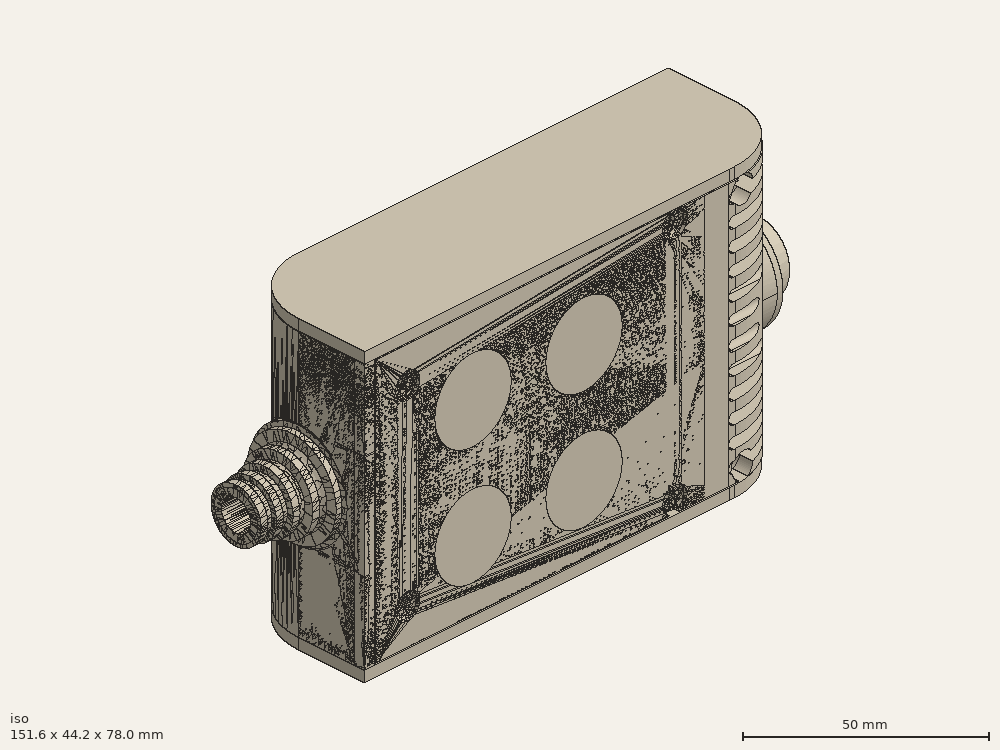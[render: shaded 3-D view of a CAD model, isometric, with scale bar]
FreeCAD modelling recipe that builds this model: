
FCSTD DOCUMENT  (FreeCAD 0.19R0.19.2)
Label: enclosure_182FCStd
License: All rights reserved
LicenseURL: http://en.wikipedia.org/wiki/All_rights_reserved
objects: Part::Revolution×152, Part::MultiFuse×146, Part::Feature×146, Sketcher::SketchObject×84, Part::Cut×70, Part::Cylinder×70, Part::Extrusion×67, Part::Fillet×58, Part::Box×36, App::MeasureDistance×4, PartDesign::Body×2, Image::ImagePlane×1
note: 831 computed .brp shape members not serialized (recipe doc carries the construction recipe); baked Part::Feature solids carry a one-line shape summary decoded from their .brp

FEATURE [Sketcher::SketchObject] Sketch  label="topSketch"
  FullyConstrained = true
  sketch-geometry (20):
    g0: LineSegment StartX=5.21097e-06 StartY=3 StartZ=0 EndX=5.21097e-06 EndY=19 EndZ=0
    g1: ArcOfCircle CenterX=19 CenterY=19 CenterZ=0 NormalX=0 NormalY=0 NormalZ=1 AngleXU=0 Radius=19 StartAngle=1.5708 EndAngle=3.14159
    g2: ArcOfCircle CenterX=19 CenterY=19 CenterZ=0 NormalX=0 NormalY=0 NormalZ=1 AngleXU=0 Radius=16 StartAngle=1.5708 EndAngle=3.14159
    g3: LineSegment StartX=114 StartY=35 StartZ=0 EndX=19 EndY=35 EndZ=0
    g4: LineSegment StartX=5.21097e-06 StartY=3 StartZ=0 EndX=5.21097e-06 EndY=0 EndZ=0
    g5: LineSegment StartX=3 StartY=0 StartZ=0 EndX=5.21097e-06 EndY=0 EndZ=0
    g6: LineSegment StartX=3 StartY=19 StartZ=0 EndX=3 EndY=0 EndZ=0
    g7: LineSegment StartX=19 StartY=38 StartZ=0 EndX=124 EndY=38 EndZ=0
    g8: Circle CenterX=119 CenterY=35 CenterZ=0 NormalX=0 NormalY=0 NormalZ=1 AngleXU=0 Radius=1
    g9: Circle CenterX=121 CenterY=35 CenterZ=0 NormalX=0 NormalY=0 NormalZ=1 AngleXU=0 Radius=1
    g10: Circle CenterX=121 CenterY=33 CenterZ=0 NormalX=0 NormalY=0 NormalZ=1 AngleXU=0 Radius=1
    g11: BSplineCurve PolesCount=3 KnotsCount=2 Degree=2 IsPeriodic=0
    g12: GeomPoint X=119 Y=35 Z=0
    g13: GeomPoint X=121 Y=33 Z=0
    g14: LineSegment StartX=119 StartY=35 StartZ=0 EndX=114 EndY=35 EndZ=0
    g15: ArcOfCircle CenterX=105 CenterY=19 CenterZ=0 NormalX=0 NormalY=0 NormalZ=1 AngleXU=0 Radius=19 StartAngle=5.7297 EndAngle=6.28319
    g16: ArcOfCircle CenterX=105 CenterY=19 CenterZ=0 NormalX=0 NormalY=0 NormalZ=1 AngleXU=0 Radius=16 StartAngle=5.60905 EndAngle=6.28319
    g17: LineSegment StartX=121 StartY=33 StartZ=0 EndX=121 EndY=19 EndZ=0
    g18: LineSegment StartX=124 StartY=38 StartZ=0 EndX=124 EndY=19 EndZ=0
    g19: LineSegment StartX=117.5 StartY=9.01251 StartZ=0 EndX=121.163 EndY=9.0125 EndZ=0
  constraints (46):
    c: Vertical(g0)
    c: Block(g0)
    c: Coincident(g1,g0)
    c: Block(g1)
    c: Coincident(g2,g1)
    c: Block(g2)
    c: Coincident(g3,g2)
    c: Horizontal(g3)
    c: Tangent(g3,g2)
    c: Coincident(g4,g0)
    c: Distance(g4) = 3
    c: Vertical(g4)
    c: Coincident(g5,g4)
    c: Horizontal(g5)
    c: Coincident(g6,g2)
    c: Coincident(g6,g5)
    c: Vertical(g6)
    c: Horizontal(g7)
    c: Distance(g7) = 105
    c: Coincident(g7,g1)
    c: Block(g3)
    c: Weight(g8) = 1
    c: Equal(g8,g9)
    c: Equal(g8,g10)
    c: InternalAlignment(g8,g11)
    c: InternalAlignment(g9,g11)
    c: InternalAlignment(g10,g11)
    c: InternalAlignment(g12,g11)
    c: InternalAlignment(g13,g11)
    c: Block(g11)
    c: Coincident(g14,g11)
    c: Coincident(g14,g3)
    c: Horizontal(g14)
    c: Block(g15)
    c: Coincident(g16,g15)
    c: Block(g16)
    c: Coincident(g17,g11)
    c: Coincident(g17,g16)
    c: Vertical(g17)
    c: Distance(g17) = 14
    c: Coincident(g18,g7)
    c: Coincident(g18,g15)
    c: Vertical(g18)
    c: Distance(g18) = 19
    c: Coincident(g19,g16)
    c: Coincident(g19,g15)
FEATURE [Sketcher::SketchObject] Sketch001  label="bottomSketch"
  FullyConstrained = true
  sketch-geometry (32):
    g0: LineSegment StartX=3.3 StartY=-6.03275e-07 StartZ=0 EndX=98 EndY=-6.03275e-07 EndZ=0
    g1: ArcOfCircle CenterX=98 CenterY=19 CenterZ=0 NormalX=0 NormalY=0 NormalZ=1 AngleXU=0 Radius=19 StartAngle=4.71239 EndAngle=5.71103
    g2: LineSegment StartX=6.3 StartY=8 StartZ=0 EndX=3.3 EndY=8 EndZ=0
    g3: LineSegment StartX=3.3 StartY=8 StartZ=0 EndX=3.3 EndY=-6.03275e-07 EndZ=0
    g4: ArcOfCircle CenterX=8.3 CenterY=5 CenterZ=0 NormalX=0 NormalY=0 NormalZ=1 AngleXU=0 Radius=2 StartAngle=3.14159 EndAngle=4.71239
    g5: LineSegment StartX=6.3 StartY=8 StartZ=0 EndX=6.3 EndY=5 EndZ=0
    g6: ArcOfCircle CenterX=98 CenterY=19 CenterZ=0 NormalX=0 NormalY=0 NormalZ=1 AngleXU=0 Radius=12.7 StartAngle=4.71239 EndAngle=6.28319
    g7: LineSegment StartX=94.7 StartY=3 StartZ=0 EndX=8.3 EndY=3 EndZ=0
    g8-g12: Circle x5 (B-spline internal-alignment scaffolding for g13; pole/knot coordinates omitted)
    g13: BSplineCurve PolesCount=5 KnotsCount=3 Degree=3 IsPeriodic=0
    g14: GeomPoint X=98 Y=6.3 Z=0
    g15: GeomPoint X=96.3938 Y=4.71946 Z=0
    g16: GeomPoint X=94.7 Y=3 Z=0
    g17-g23: Circle x7 (B-spline internal-alignment scaffolding for g24; pole/knot coordinates omitted)
    g24: BSplineCurve PolesCount=7 KnotsCount=5 Degree=3 IsPeriodic=0
    g25-g29: GeomPoint x5 (B-spline internal-alignment scaffolding for g24; pole/knot coordinates omitted)
    g30: ArcOfCircle CenterX=98 CenterY=19 CenterZ=0 NormalX=0 NormalY=0 NormalZ=1 AngleXU=0 Radius=15.7 StartAngle=5.81226 EndAngle=6.28319
    g31: LineSegment StartX=110.7 StartY=19 StartZ=0 EndX=113.7 EndY=19 EndZ=0
  constraints (41):
    c: Horizontal(g0)
    c: Coincident(g1,g0)
    c: Block(g1)
    c: Horizontal(g2)
    c: Distance(g2) = 3
    c: Coincident(g3,g2)
    c: Vertical(g3)
    c: Coincident(g3,g0)
    c: Block(g4)
    c: Block(g2)
    c: Coincident(g5,g2)
    c: Coincident(g5,g4)
    c: Vertical(g5)
    c: Coincident(g6,g1)
    c: Block(g6)
    c: Coincident(g7,g4)
    c: Horizontal(g7)
    c: Block(g0)
    c: Block(g7)
    c: Block(g3)
    c: Coincident(g13,g6)
    c: Weight(g8) = 1
    c: Equal(g8, g9-g12) x4
    c: Coincident(g13,g7)
    c: InternalAlignment(g8-g12 -> g13) x5
    c: InternalAlignment(g14,g13)
    c: InternalAlignment(g15,g13)
    c: InternalAlignment(g16,g13)
    c: Block(g13)
    c: Weight(g17) = 1
    c: Equal(g17, g18-g23) x6
    c: Coincident(g24,g1)
    c: InternalAlignment(g17-g23 -> g24) x7
    c: InternalAlignment(g25-g29 -> g24) x5
    c: Block(g24)
    c: Coincident(g30,g24)
    c: Coincident(g31,g6)
    c: Coincident(g31,g30)
    c: Horizontal(g31)
    c: Block(g31)
    c: Block(g30)
FEATURE [Part::Extrusion] Extrude  label="top"
  Base = -> Sketch
  Dir = (0,0,1)
  DirMode = 2
  FaceMakerClass = Part::FaceMakerBullseye
  LengthFwd = 72
  LengthRev = 0
  Solid = true
  Symmetric = false
FEATURE [Part::Extrusion] Extrude001  label="bottom"
  Base = -> Sketch001
  Dir = (0,0,1)
  DirMode = 2
  FaceMakerClass = Part::FaceMakerBullseye
  LengthFwd = 71.4
  LengthRev = 0
  Placement = pos=(0,0,0.3) rot=(0,0,1;0rad)
  Solid = true
  Symmetric = false
FEATURE [Sketcher::SketchObject] Sketch002  label="topSketch001"
  FullyConstrained = true
  sketch-geometry (8):
    g0: ArcOfCircle CenterX=19 CenterY=19.0975 CenterZ=0 NormalX=0 NormalY=0 NormalZ=1 AngleXU=0 Radius=18.9025 StartAngle=1.5708 EndAngle=3.14674
    g1: LineSegment StartX=0.0977805 StartY=19.0003 StartZ=0 EndX=0.0977805 EndY=0.000251602 EndZ=0
    g2: LineSegment StartX=19 StartY=38 StartZ=0 EndX=124 EndY=38 EndZ=0
    g3: LineSegment StartX=0.0977805 StartY=0.000251602 StartZ=0 EndX=105.098 EndY=0.000251602 EndZ=0
    g4: LineSegment StartX=124 StartY=38 StartZ=0 EndX=125.616 EndY=38 EndZ=0
    g5: LineSegment StartX=105.098 StartY=0.000251602 StartZ=0 EndX=106.713 EndY=0.000251602 EndZ=0
    g6: ArcOfCircle CenterX=106.616 CenterY=19 CenterZ=0 NormalX=0 NormalY=0 NormalZ=1 AngleXU=0 Radius=19 StartAngle=4.71754 EndAngle=6.28319
    g7: LineSegment StartX=125.616 StartY=38 StartZ=0 EndX=125.616 EndY=19 EndZ=0
  constraints (21):
    c: Block(g0)
    c: Coincident(g1,g0)
    c: Vertical(g1)
    c: Horizontal(g2)
    c: Distance(g2) = 105
    c: Coincident(g2,g0)
    c: Distance(g1) = 19
    c: Coincident(g3,g1)
    c: Horizontal(g3)
    c: Distance(g3) = 105
    c: Coincident(g4,g2)
    c: Horizontal(g4)
    c: Distance(g4) = 1.61553
    c: Horizontal(g5)
    c: Equal(g4,g5) = 1.61553
    c: Coincident(g5,g3)
    c: Block(g6)
    c: Coincident(g6,g5)
    c: Coincident(g7,g4)
    c: Coincident(g7,g6)
    c: Vertical(g7)
FEATURE [Part::Extrusion] Extrude002  label="sideA"
  Base = -> Sketch002
  Dir = (0,0,1)
  DirMode = 2
  FaceMakerClass = Part::FaceMakerBullseye
  LengthFwd = 3
  LengthRev = 0
  Placement = pos=(0,0,-3) rot=(0,0,1;0rad)
  Solid = true
  Symmetric = false
FEATURE [Sketcher::SketchObject] Sketch003  label="topSketch002"
  FullyConstrained = true
  sketch-geometry (6):
    g0: LineSegment StartX=19 StartY=38 StartZ=0 EndX=117 EndY=38 EndZ=0
    g1: ArcOfCircle CenterX=19 CenterY=19 CenterZ=0 NormalX=0 NormalY=0 NormalZ=1 AngleXU=0 Radius=19 StartAngle=1.5708 EndAngle=3.14159
    g2: LineSegment StartX=117 StartY=38 StartZ=0 EndX=117 EndY=19 EndZ=0
    g3: LineSegment StartX=98 StartY=1.0161e-12 StartZ=0 EndX=5.22862e-06 EndY=1.0161e-12 EndZ=0
    g4: LineSegment StartX=5.22862e-06 StartY=19 StartZ=0 EndX=5.22862e-06 EndY=1.0161e-12 EndZ=0
    g5: ArcOfCircle CenterX=98 CenterY=19 CenterZ=0 NormalX=0 NormalY=0 NormalZ=1 AngleXU=0 Radius=19 StartAngle=4.71239 EndAngle=6.28319
  constraints (16):
    c: Horizontal(g0)
    c: Distance(g0) = 98
    c: Coincident(g1,g0)
    c: Block(g1)
    c: Coincident(g2,g0)
    c: Vertical(g2)
    c: Distance(g2) = 19
    c: Horizontal(g3)
    c: Coincident(g4,g1)
    c: Vertical(g4)
    c: Coincident(g3,g4)
    c: Block(g3)
    c: Coincident(g5,g2)
    c: Coincident(g5,g3)
    c: Block(g0)
    c: Block(g5)
FEATURE [Sketcher::SketchObject] Sketch004
  FullyConstrained = true
  MapMode = 3
  Placement = pos=(0,0,0) rot=(1,0,0;1.5708rad)
  Support = -> [Extrude]
  sketch-geometry (8):
    g0: Circle CenterX=80.351 CenterY=-67.6202 CenterZ=0 NormalX=0 NormalY=0 NormalZ=1 AngleXU=0 Radius=2
    g1: Circle CenterX=80.351 CenterY=-67.6202 CenterZ=0 NormalX=0 NormalY=0 NormalZ=1 AngleXU=0 Radius=3
    g2: Circle CenterX=80.351 CenterY=-4.92017 CenterZ=0 NormalX=0 NormalY=0 NormalZ=1 AngleXU=0 Radius=2
    g3: Circle CenterX=80.351 CenterY=-4.92017 CenterZ=0 NormalX=0 NormalY=0 NormalZ=1 AngleXU=0 Radius=3
    g4: Circle CenterX=23.851 CenterY=-4.92017 CenterZ=0 NormalX=0 NormalY=0 NormalZ=1 AngleXU=0 Radius=2
    g5: Circle CenterX=23.851 CenterY=-4.92017 CenterZ=0 NormalX=0 NormalY=0 NormalZ=1 AngleXU=0 Radius=3
    g6: Circle CenterX=23.851 CenterY=-67.6202 CenterZ=0 NormalX=0 NormalY=0 NormalZ=1 AngleXU=0 Radius=2
    g7: Circle CenterX=23.851 CenterY=-67.6202 CenterZ=0 NormalX=0 NormalY=0 NormalZ=1 AngleXU=0 Radius=3
  constraints (8):
    c: Block(g3)
    c: Block(g2)
    c: Block(g1)
    c: Block(g0)
    c: Block(g6)
    c: Block(g7)
    c: Block(g4)
    c: Block(g5)
FEATURE [Part::Extrusion] Extrude004
  Base = -> Sketch004
  Dir = (0,-1,2e-16)
  DirMode = 2
  FaceMakerClass = Part::FaceMakerBullseye
  LengthFwd = 6
  LengthRev = 0
  Placement = pos=(0,9,0) rot=(0,0,1;0rad)
  Solid = true
  Symmetric = false
FEATURE [Sketcher::SketchObject] Sketch005
  FullyConstrained = true
  MapMode = 3
  Placement = pos=(0,0,0) rot=(1,0,0;1.5708rad)
  Support = -> [Extrude]
  sketch-geometry (8):
    g0: Circle CenterX=80.351 CenterY=-67.6202 CenterZ=0 NormalX=0 NormalY=0 NormalZ=1 AngleXU=0 Radius=3
    g1: Circle CenterX=80.351 CenterY=-4.92017 CenterZ=0 NormalX=0 NormalY=0 NormalZ=1 AngleXU=0 Radius=3
    g2: Circle CenterX=23.851 CenterY=-4.92017 CenterZ=0 NormalX=0 NormalY=0 NormalZ=1 AngleXU=0 Radius=3
    g3: Circle CenterX=23.851 CenterY=-67.6202 CenterZ=0 NormalX=0 NormalY=0 NormalZ=1 AngleXU=0 Radius=3
    g4: Circle CenterX=23.851 CenterY=-67.6202 CenterZ=0 NormalX=0 NormalY=0 NormalZ=1 AngleXU=0 Radius=5
    g5: Circle CenterX=80.351 CenterY=-67.6202 CenterZ=0 NormalX=0 NormalY=0 NormalZ=1 AngleXU=0 Radius=5
    g6: Circle CenterX=23.851 CenterY=-4.92017 CenterZ=0 NormalX=0 NormalY=0 NormalZ=1 AngleXU=0 Radius=5
    g7: Circle CenterX=80.351 CenterY=-4.92017 CenterZ=0 NormalX=0 NormalY=0 NormalZ=1 AngleXU=0 Radius=5
  constraints (8):
    c: Block(g1)
    c: Block(g0)
    c: Block(g3)
    c: Block(g2)
    c: Block(g5)
    c: Block(g4)
    c: Block(g6)
    c: Block(g7)
FEATURE [Part::Extrusion] Extrude005
  Base = -> Sketch005
  Dir = (0,-1,2e-16)
  DirMode = 2
  FaceMakerClass = Part::FaceMakerBullseye
  LengthFwd = 2
  LengthRev = 0
  Solid = true
  Symmetric = false
FEATURE [Sketcher::SketchObject] Sketch006
  FullyConstrained = true
  MapMode = 3
  Placement = pos=(0,0,0) rot=(1,0,0;1.5708rad)
  sketch-geometry (8):
    g0: Circle CenterX=80.351 CenterY=-67.6202 CenterZ=0 NormalX=0 NormalY=0 NormalZ=1 AngleXU=0 Radius=3
    g1: Circle CenterX=80.351 CenterY=-4.92017 CenterZ=0 NormalX=0 NormalY=0 NormalZ=1 AngleXU=0 Radius=3
    g2: Circle CenterX=23.851 CenterY=-4.92017 CenterZ=0 NormalX=0 NormalY=0 NormalZ=1 AngleXU=0 Radius=3
    g3: Circle CenterX=23.851 CenterY=-67.6202 CenterZ=0 NormalX=0 NormalY=0 NormalZ=1 AngleXU=0 Radius=3
    g4: Circle CenterX=23.851 CenterY=-67.6202 CenterZ=0 NormalX=0 NormalY=0 NormalZ=1 AngleXU=0 Radius=5
    g5: Circle CenterX=80.351 CenterY=-67.6202 CenterZ=0 NormalX=0 NormalY=0 NormalZ=1 AngleXU=0 Radius=5
    g6: Circle CenterX=23.851 CenterY=-4.92017 CenterZ=0 NormalX=0 NormalY=0 NormalZ=1 AngleXU=0 Radius=5
    g7: Circle CenterX=80.351 CenterY=-4.92017 CenterZ=0 NormalX=0 NormalY=0 NormalZ=1 AngleXU=0 Radius=5
  constraints (8):
    c: Block(g1)
    c: Block(g0)
    c: Block(g3)
    c: Block(g2)
    c: Block(g5)
    c: Block(g4)
    c: Block(g6)
    c: Block(g7)
FEATURE [Part::Extrusion] Extrude007
  Base = -> Sketch006
  Dir = (0,-1,2e-16)
  DirMode = 2
  FaceMakerClass = Part::FaceMakerBullseye
  LengthFwd = 2
  LengthRev = 0
  Solid = true
  Symmetric = false
FEATURE [Part::Fillet] Fillet
  Base = -> Extrude007
  Edges = 4 edges r=1.99: [Edge6,Edge12,Edge18,Edge24]
FEATURE [Part::Cut] Cut
  Base = -> Extrude005
  Placement = pos=(0,5,0) rot=(0,0,1;0rad)
  Tool = -> Fillet
FEATURE [Part::MultiFuse] Fusion  label="pCBScrews"
  Placement = pos=(-2.5,0,72.3) rot=(0,0,1;0rad)
  Shapes = -> [Extrude004,Cut]
FEATURE [App::MeasureDistance] Distance  label="Distance: 0.69 mm"
  Distance = 0.685967
  P1 = (24.0138,2.9647,0.3)
  P2 = (23.8901,3,-0.373787)
FEATURE [App::MeasureDistance] Distance001  label="Distance: 0.53 mm"
  Distance = 0.533607
  P1 = (80.2939,3,72.2334)
  P2 = (80.281,2.99661,71.7)
FEATURE [Part::Fillet] Fillet001
  Base = -> Extrude001
  Edges = 1 edges r=2.4: [Edge17]
FEATURE [Part::Fillet] Fillet002  label="bottom001"
  Base = -> Fillet001
  Edges = 1 edges r=2.4: [Edge36]
FEATURE [Part::Fillet] Fillet003  label="top001"
  Base = -> Extrude
  Edges = 1 edges r=2: [Edge1]
FEATURE [Sketcher::SketchObject] Sketch007
  FullyConstrained = true
  sketch-geometry (16):
    g0: LineSegment StartX=4 StartY=0 StartZ=0 EndX=4 EndY=2.4 EndZ=0
    g1: LineSegment StartX=4 StartY=2.4 StartZ=0 EndX=7 EndY=2.4 EndZ=0
    g2: LineSegment StartX=4 StartY=0 StartZ=0 EndX=5.7 EndY=0 EndZ=0
    g3: LineSegment StartX=5.7 StartY=0 StartZ=0 EndX=5.7 EndY=-5.6 EndZ=0
    g4-g8: Circle x5 (B-spline internal-alignment scaffolding for g9; pole/knot coordinates omitted)
    g9: BSplineCurve PolesCount=5 KnotsCount=3 Degree=3 IsPeriodic=0
    g10: GeomPoint X=7 Y=2.4 Z=0
    g11: GeomPoint X=10.4582 Y=-1.55472 Z=0
    g12: GeomPoint X=14 Y=-5.6 Z=0
    g13: LineSegment StartX=14 StartY=-5.6 StartZ=0 EndX=14 EndY=-14.1 EndZ=0
    g14: LineSegment StartX=14 StartY=-14.1 StartZ=0 EndX=6.5 EndY=-14.1 EndZ=0
    g15: LineSegment StartX=5.7 StartY=-5.6 StartZ=0 EndX=6.5 EndY=-14.1 EndZ=0
  constraints (28):
    c: Distance(g0) = 2.4
    c: Vertical(g0)
    c: Block(g0)
    c: Coincident(g1,g0)
    c: Horizontal(g1)
    c: Distance(g1) = 3
    c: Coincident(g2,g0)
    c: Horizontal(g2)
    c: Distance(g2) = 1.7
    c: Coincident(g3,g2)
    c: Vertical(g3)
    c: Distance(g3) = 5.6
    c: Coincident(g9,g1)
    c: Weight(g4) = 1
    c: Equal(g4, g5-g8) x4
    c: InternalAlignment(g4-g8 -> g9) x5
    c: InternalAlignment(g10,g9)
    c: InternalAlignment(g11,g9)
    c: InternalAlignment(g12,g9)
    c: Block(g9)
    c: Coincident(g13,g9)
    c: Vertical(g13)
    c: Distance(g13) = 8.5
    c: Coincident(g14,g13)
    c: Horizontal(g14)
    c: Distance(g14) = 7.5
    c: Coincident(g15,g3)
    c: Coincident(g15,g14)
FEATURE [Part::Feature] Face
  shape: bbox 10 x 16.5 x 2e-07 mm, 1 faces, 0 solids (baked)
FEATURE [Part::Revolution] Revolve  label="plugHousing"
  Angle = 360
  Axis = (0,1,0)
  Base = (0,0,0)
  FaceMakerClass = Part::FaceMakerBullseye
  Placement = pos=(0,0,36.15) rot=(0,0,1;0rad)
  Solid = false
  Source = -> Face
  Symmetric = false
FEATURE [Part::Feature] Face001
  shape: bbox 10 x 16.5 x 2e-07 mm, 1 faces, 0 solids (baked)
FEATURE [Part::Revolution] Revolve001  label="plugHousing001"
  Angle = 360
  Axis = (0,1,0)
  Base = (0,0,0)
  FaceMakerClass = Part::FaceMakerBullseye
  Placement = pos=(0,0,36.15) rot=(0,0,1;0rad)
  Solid = false
  Source = -> Face001
  Symmetric = false
FEATURE [Part::MultiFuse] Fusion001  label="plugHousing002"
  Placement = pos=(0,0,0) rot=(0,0,1;1.5708rad)
  Shapes = -> [Revolve001,Revolve]
FEATURE [Part::Feature] Face002
  shape: bbox 10 x 16.5 x 2e-07 mm, 1 faces, 0 solids (baked)
FEATURE [Part::Revolution] Revolve003  label="plugHousing005"
  Angle = 360
  Axis = (0,1,0)
  Base = (0,0,0)
  FaceMakerClass = Part::FaceMakerBullseye
  Placement = pos=(0,0,36.15) rot=(0,0,1;0rad)
  Solid = false
  Source = -> Face002
  Symmetric = false
FEATURE [Part::Feature] Face003
  shape: bbox 10 x 16.5 x 2e-07 mm, 1 faces, 0 solids (baked)
FEATURE [Part::Revolution] Revolve002  label="plugHousing003"
  Angle = 360
  Axis = (0,1,0)
  Base = (0,0,0)
  FaceMakerClass = Part::FaceMakerBullseye
  Placement = pos=(0,0,36.15) rot=(0,0,1;0rad)
  Solid = false
  Source = -> Face003
  Symmetric = false
FEATURE [Part::MultiFuse] Fusion002  label="plugHousing004"
  Placement = pos=(0,0,0) rot=(0,0,1;1.5708rad)
  Shapes = -> [Revolve002,Revolve003]
FEATURE [Part::MultiFuse] Fusion003  label="plugHousing006"
  Placement = pos=(0,19,0) rot=(0,0,1;3.14159rad)
  Shapes = -> [Fusion002,Fusion001]
FEATURE [Part::Feature] Face004
  shape: bbox 10 x 16.5 x 2e-07 mm, 1 faces, 0 solids (baked)
FEATURE [Part::Revolution] Revolve006  label="plugHousing010"
  Angle = 360
  Axis = (0,1,0)
  Base = (0,0,0)
  FaceMakerClass = Part::FaceMakerBullseye
  Placement = pos=(0,0,36.15) rot=(0,0,1;0rad)
  Solid = false
  Source = -> Face004
  Symmetric = false
FEATURE [Part::Feature] Face005
  shape: bbox 10 x 16.5 x 2e-07 mm, 1 faces, 0 solids (baked)
FEATURE [Part::Revolution] Revolve007  label="plugHousing011"
  Angle = 360
  Axis = (0,1,0)
  Base = (0,0,0)
  FaceMakerClass = Part::FaceMakerBullseye
  Placement = pos=(0,0,36.15) rot=(0,0,1;0rad)
  Solid = false
  Source = -> Face005
  Symmetric = false
FEATURE [Part::Feature] Face006
  shape: bbox 10 x 16.5 x 2e-07 mm, 1 faces, 0 solids (baked)
FEATURE [Part::Revolution] Revolve004  label="plugHousing007"
  Angle = 360
  Axis = (0,1,0)
  Base = (0,0,0)
  FaceMakerClass = Part::FaceMakerBullseye
  Placement = pos=(0,0,36.15) rot=(0,0,1;0rad)
  Solid = false
  Source = -> Face006
  Symmetric = false
FEATURE [Part::MultiFuse] Fusion004  label="plugHousing009"
  Placement = pos=(0,0,0) rot=(0,0,1;1.5708rad)
  Shapes = -> [Revolve004,Revolve007]
FEATURE [Part::Feature] Face007
  shape: bbox 10 x 16.5 x 2e-07 mm, 1 faces, 0 solids (baked)
FEATURE [Part::Revolution] Revolve005  label="plugHousing008"
  Angle = 360
  Axis = (0,1,0)
  Base = (0,0,0)
  FaceMakerClass = Part::FaceMakerBullseye
  Placement = pos=(0,0,36.15) rot=(0,0,1;0rad)
  Solid = false
  Source = -> Face007
  Symmetric = false
FEATURE [Part::MultiFuse] Fusion005  label="plugHousing012"
  Placement = pos=(0,0,0) rot=(0,0,1;1.5708rad)
  Shapes = -> [Revolve006,Revolve005]
FEATURE [Part::MultiFuse] Fusion006  label="plugHousing013"
  Placement = pos=(0,19,0) rot=(0,0,1;3.14159rad)
  Shapes = -> [Fusion005,Fusion004]
FEATURE [Part::MultiFuse] Fusion007  label="plugHousing014"
  Placement = pos=(122.621,0,-0.15) rot=(0,0,1;0rad)
  Shapes = -> [Fusion003,Fusion006]
FEATURE [Part::Cylinder] Cylinder002
  Angle = 360
  AttacherType = Attacher::AttachEngine3D
  Height = 20
  Placement = pos=(0,0,36.15) rot=(0,0,1;0rad)
  Radius = 4
FEATURE [Part::Cylinder] Cylinder003
  Angle = 360
  AttacherType = Attacher::AttachEngine3D
  Height = 10
  Placement = pos=(0,0,36.15) rot=(0,0,1;0rad)
  Radius = 4
FEATURE [Part::MultiFuse] Fusion009  label="removeToCreateHoleForPlugHousing"
  Placement = pos=(70,19,36.15) rot=(0,1,0;1.5708rad)
  Shapes = -> [Cylinder002,Cylinder003]
FEATURE [Part::Cylinder] Cylinder004
  Angle = 360
  AttacherType = Attacher::AttachEngine3D
  Height = 20
  Placement = pos=(0,0,36.15) rot=(0,0,1;0rad)
  Radius = 4
FEATURE [Part::Cylinder] Cylinder005
  Angle = 360
  AttacherType = Attacher::AttachEngine3D
  Height = 10
  Placement = pos=(0,0,36.15) rot=(0,0,1;0rad)
  Radius = 4
FEATURE [Part::MultiFuse] Fusion010  label="removeToCreateHoleForPlugHousing001"
  Placement = pos=(70,19,36.15) rot=(0,1,0;1.5708rad)
  Shapes = -> [Cylinder004,Cylinder005]
FEATURE [Part::Cut] Cut001
  Base = -> Fillet003
  Tool = -> Fusion010
FEATURE [Part::Cut] Cut002  label="Bottom"
  Base = -> Fillet002
  Tool = -> Fusion009
FEATURE [Part::Feature] Face008
  shape: bbox 10 x 16.5 x 2e-07 mm, 1 faces, 0 solids (baked)
FEATURE [Part::Revolution] Revolve011  label="plugHousing021"
  Angle = 360
  Axis = (0,1,0)
  Base = (0,0,0)
  FaceMakerClass = Part::FaceMakerBullseye
  Placement = pos=(0,0,36.15) rot=(0,0,1;0rad)
  Solid = false
  Source = -> Face008
  Symmetric = false
FEATURE [Part::Feature] Face009
  shape: bbox 10 x 16.5 x 2e-07 mm, 1 faces, 0 solids (baked)
FEATURE [Part::Revolution] Revolve012  label="plugHousing022"
  Angle = 360
  Axis = (0,1,0)
  Base = (0,0,0)
  FaceMakerClass = Part::FaceMakerBullseye
  Placement = pos=(0,0,36.15) rot=(0,0,1;0rad)
  Solid = false
  Source = -> Face009
  Symmetric = false
FEATURE [Part::Feature] Face010 .. Face013  x4 (patterned run collapsed; names and placements below)
  shape: bbox 10 x 16.5 x 2e-07 mm, 1 faces, 0 solids (baked)
FEATURE [Part::Revolution] Revolve015  label="plugHousing027"
  Angle = 360
  Axis = (0,1,0)
  Base = (0,0,0)
  FaceMakerClass = Part::FaceMakerBullseye
  Placement = pos=(0,0,36.15) rot=(0,0,1;0rad)
  Solid = false
  Source = -> Face013
  Symmetric = false
FEATURE [Part::Feature] Face014
  shape: bbox 10 x 16.5 x 2e-07 mm, 1 faces, 0 solids (baked)
FEATURE [Part::Feature] Face015
  shape: bbox 10 x 16.5 x 2e-07 mm, 1 faces, 0 solids (baked)
FEATURE [Part::Feature] Face016
  shape: bbox 10 x 16.5 x 2e-07 mm, 1 faces, 0 solids (baked)
FEATURE [Part::Revolution] Revolve019  label="plugHousing033"
  Angle = 360
  Axis = (0,1,0)
  Base = (0,0,0)
  FaceMakerClass = Part::FaceMakerBullseye
  Placement = pos=(0,0,36.15) rot=(0,0,1;0rad)
  Solid = false
  Source = -> Face016
  Symmetric = false
FEATURE [Part::Feature] Face017
  shape: bbox 10 x 16.5 x 2e-07 mm, 1 faces, 0 solids (baked)
FEATURE [Part::Revolution] Revolve020  label="plugHousing034"
  Angle = 360
  Axis = (0,1,0)
  Base = (0,0,0)
  FaceMakerClass = Part::FaceMakerBullseye
  Placement = pos=(0,0,36.15) rot=(0,0,1;0rad)
  Solid = false
  Source = -> Face017
  Symmetric = false
FEATURE [Part::Feature] Face018
  shape: bbox 10 x 16.5 x 2e-07 mm, 1 faces, 0 solids (baked)
FEATURE [Part::Revolution] Revolve016  label="plugHousing030"
  Angle = 360
  Axis = (0,1,0)
  Base = (0,0,0)
  FaceMakerClass = Part::FaceMakerBullseye
  Placement = pos=(0,0,36.15) rot=(0,0,1;0rad)
  Solid = false
  Source = -> Face018
  Symmetric = false
FEATURE [Part::MultiFuse] Fusion020  label="plugHousing038"
  Placement = pos=(0,0,0) rot=(0,0,1;1.5708rad)
  Shapes = -> [Revolve016,Revolve020]
FEATURE [Part::Feature] Face019
  shape: bbox 10 x 16.5 x 2e-07 mm, 1 faces, 0 solids (baked)
FEATURE [Part::Feature] Face020
  shape: bbox 10 x 16.5 x 2e-07 mm, 1 faces, 0 solids (baked)
FEATURE [Part::Revolution] Revolve017  label="plugHousing031"
  Angle = 360
  Axis = (0,1,0)
  Base = (0,0,0)
  FaceMakerClass = Part::FaceMakerBullseye
  Placement = pos=(0,0,36.15) rot=(0,0,1;0rad)
  Solid = false
  Source = -> Face020
  Symmetric = false
FEATURE [Part::MultiFuse] Fusion021  label="plugHousing039"
  Placement = pos=(0,0,0) rot=(0,0,1;1.5708rad)
  Shapes = -> [Revolve019,Revolve017]
FEATURE [Part::MultiFuse] Fusion023  label="plugHousing041"
  Placement = pos=(0,19,0) rot=(0,0,1;3.14159rad)
  Shapes = -> [Fusion021,Fusion020]
FEATURE [Part::Revolution] Revolve022  label="plugHousing043"
  Angle = 360
  Axis = (0,1,0)
  Base = (0,0,0)
  FaceMakerClass = Part::FaceMakerBullseye
  Placement = pos=(0,0,36.15) rot=(0,0,1;0rad)
  Solid = false
  Source = -> Face019
  Symmetric = false
FEATURE [Part::Feature] Face021
  shape: bbox 10 x 16.5 x 2e-07 mm, 1 faces, 0 solids (baked)
FEATURE [Part::Revolution] Revolve023  label="plugHousing044"
  Angle = 360
  Axis = (0,1,0)
  Base = (0,0,0)
  FaceMakerClass = Part::FaceMakerBullseye
  Placement = pos=(0,0,36.15) rot=(0,0,1;0rad)
  Solid = false
  Source = -> Face021
  Symmetric = false
FEATURE [Part::Feature] Face022
  shape: bbox 10 x 16.5 x 2e-07 mm, 1 faces, 0 solids (baked)
FEATURE [Part::Revolution] Revolve018  label="plugHousing032"
  Angle = 360
  Axis = (0,1,0)
  Base = (0,0,0)
  FaceMakerClass = Part::FaceMakerBullseye
  Placement = pos=(0,0,36.15) rot=(0,0,1;0rad)
  Solid = false
  Source = -> Face022
  Symmetric = false
FEATURE [Part::MultiFuse] Fusion022  label="plugHousing040"
  Placement = pos=(0,0,0) rot=(0,0,1;1.5708rad)
  Shapes = -> [Revolve018,Revolve023]
FEATURE [Part::Feature] Face023
  shape: bbox 10 x 16.5 x 2e-07 mm, 1 faces, 0 solids (baked)
FEATURE [Part::Revolution] Revolve021  label="plugHousing035"
  Angle = 360
  Axis = (0,1,0)
  Base = (0,0,0)
  FaceMakerClass = Part::FaceMakerBullseye
  Placement = pos=(0,0,36.15) rot=(0,0,1;0rad)
  Solid = false
  Source = -> Face023
  Symmetric = false
FEATURE [Part::MultiFuse] Fusion018  label="plugHousing036"
  Placement = pos=(0,0,0) rot=(0,0,1;1.5708rad)
  Shapes = -> [Revolve022,Revolve021]
FEATURE [Part::MultiFuse] Fusion019  label="plugHousing037"
  Placement = pos=(0,19,0) rot=(0,0,1;3.14159rad)
  Shapes = -> [Fusion018,Fusion022]
FEATURE [Part::MultiFuse] Fusion024  label="plugHousing042"
  Placement = pos=(122.621,0,-0.15) rot=(0,0,1;0rad)
  Shapes = -> [Fusion023,Fusion019]
FEATURE [Part::Cylinder] Cylinder006
  Angle = 360
  AttacherType = Attacher::AttachEngine3D
  Height = 20
  Placement = pos=(0,0,36.15) rot=(0,0,1;0rad)
  Radius = 14.3
FEATURE [Part::Cylinder] Cylinder007
  Angle = 360
  AttacherType = Attacher::AttachEngine3D
  Height = 10
  Placement = pos=(0,0,36.15) rot=(0,0,1;0rad)
  Radius = 4
FEATURE [Part::MultiFuse] Fusion026  label="removeToCreteHoleForPlugHousing"
  Placement = pos=(70,19,36) rot=(0,1,0;1.5708rad)
  Shapes = -> [Cylinder006,Cylinder007]
FEATURE [Part::Box] Box001  label="Cube001"
  AttacherType = Attacher::AttachEngine3D
  Height = 28
  Length = 3
  Placement = pos=(110.7,19,22) rot=(0,0,1;0rad)
  Width = 15.7
FEATURE [Part::Cut] Cut003  label="top002"
  Base = -> Cut001
  Tool = -> Fusion007
FEATURE [Part::Revolution] Revolve008  label="plugHousing015"
  Angle = 360
  Axis = (0,1,0)
  Base = (0,0,0)
  FaceMakerClass = Part::FaceMakerBullseye
  Placement = pos=(0,0,36.15) rot=(0,0,1;0rad)
  Solid = false
  Source = -> Face010
  Symmetric = false
FEATURE [Part::MultiFuse] Fusion013  label="plugHousing020"
  Placement = pos=(0,0,0) rot=(0,0,1;1.5708rad)
  Shapes = -> [Revolve008,Revolve012]
FEATURE [Part::Cut] Cut004  label="top003"
  Base = -> Cut003
  Placement = pos=(1,0,0) rot=(0,0,1;0rad)
  Tool = -> Fusion026
FEATURE [Part::Cylinder] Cylinder008
  Angle = 360
  AttacherType = Attacher::AttachEngine3D
  Height = 20
  Placement = pos=(0,0,36.15) rot=(0,0,1;0rad)
  Radius = 10.3
FEATURE [Part::Cylinder] Cylinder009
  Angle = 360
  AttacherType = Attacher::AttachEngine3D
  Height = 10
  Placement = pos=(0,0,36.15) rot=(0,0,1;0rad)
  Radius = 4
FEATURE [Part::MultiFuse] Fusion027  label="removeToCreteHoleForPlugHousing001"
  Placement = pos=(70,19,36) rot=(0,1,0;1.5708rad)
  Shapes = -> [Cylinder008,Cylinder009]
FEATURE [Part::Cut] Cut005  label="plugHousingTab"
  Base = -> Box001
  Tool = -> Fusion027
FEATURE [Part::MultiFuse] Fusion028  label="plugHousing045"
  Shapes = -> [Fusion024,Cut005]
FEATURE [Part::Box] Box002  label="Cube002"
  AttacherType = Attacher::AttachEngine3D
  Height = 28.8
  Length = 3
  Placement = pos=(107.3,28,21.6) rot=(0,0,1;0rad)
  Width = 7
FEATURE [Part::Box] Box003  label="Cube003"
  AttacherType = Attacher::AttachEngine3D
  Height = 3
  Length = 6.4
  Placement = pos=(107.3,28,18.6) rot=(0,0,1;0rad)
  Width = 7
FEATURE [Part::Box] Box004  label="Cube004"
  AttacherType = Attacher::AttachEngine3D
  Height = 3
  Length = 6.4
  Placement = pos=(107.3,28,50.4) rot=(0,0,1;0rad)
  Width = 7
FEATURE [Part::MultiFuse] Fusion029  label="plugHousingBracketHolder"
  Shapes = -> [Box004,Box002,Box003]
FEATURE [Part::Cylinder] Cylinder010
  Angle = 360
  AttacherType = Attacher::AttachEngine3D
  Height = 20
  Placement = pos=(0,0,36.15) rot=(0,0,1;0rad)
  Radius = 14.3
FEATURE [Part::Cylinder] Cylinder011
  Angle = 360
  AttacherType = Attacher::AttachEngine3D
  Height = 10
  Placement = pos=(0,0,36.15) rot=(0,0,1;0rad)
  Radius = 4
FEATURE [Part::MultiFuse] Fusion030  label="removeToCreteHoleForPlugHousing002"
  Placement = pos=(70,19,36) rot=(0,1,0;1.5708rad)
  Shapes = -> [Cylinder010,Cylinder011]
FEATURE [Part::Cut] Cut006  label="plugHousingBracketHolder001"
  Base = -> Fusion029
  Tool = -> Fusion030
FEATURE [Part::Cylinder] Cylinder012
  Angle = 360
  AttacherType = Attacher::AttachEngine3D
  Height = 20
  Placement = pos=(0,0,36.15) rot=(0,0,1;0rad)
  Radius = 7
FEATURE [Part::Cylinder] Cylinder013
  Angle = 360
  AttacherType = Attacher::AttachEngine3D
  Height = 10
  Placement = pos=(0,0,36.15) rot=(0,0,1;0rad)
  Radius = 4
FEATURE [Part::MultiFuse] Fusion032  label="removeToCreteHoleForPlugHousing003"
  Placement = pos=(70,19,36) rot=(0,1,0;1.5708rad)
  Shapes = -> [Cylinder012,Cylinder013]
FEATURE [Part::Cut] Cut007  label="bottom002"
  Base = -> Cut002
  Tool = -> Fusion032
FEATURE [Sketcher::SketchObject] Sketch008
  FullyConstrained = true
  sketch-geometry (54):
    g0: LineSegment StartX=-4.2 StartY=0 StartZ=0 EndX=-6.2 EndY=0 EndZ=0
    g1: LineSegment StartX=-14 StartY=-18 StartZ=0 EndX=-14 EndY=-26.5 EndZ=0
    g2: LineSegment StartX=-4.2 StartY=0 StartZ=0 EndX=-4.2 EndY=-13.4877 EndZ=0
    g3: Circle CenterX=-4.2 CenterY=-13.4877 CenterZ=0 NormalX=0 NormalY=0 NormalZ=1 AngleXU=0 Radius=1
    g4: Circle CenterX=-4.2 CenterY=-26.5 CenterZ=0 NormalX=0 NormalY=0 NormalZ=1 AngleXU=0 Radius=1
    g5: Circle CenterX=-8.2 CenterY=-26.5 CenterZ=0 NormalX=0 NormalY=0 NormalZ=1 AngleXU=0 Radius=1
    g6: BSplineCurve PolesCount=3 KnotsCount=2 Degree=2 IsPeriodic=0
    g7: GeomPoint X=-4.2 Y=-13.4877 Z=0
    g8: GeomPoint X=-8.2 Y=-26.5 Z=0
    g9: LineSegment StartX=-14 StartY=-26.5 StartZ=0 EndX=-8.2 EndY=-26.5 EndZ=0
    g10: LineSegment StartX=-10.15 StartY=-12 StartZ=0 EndX=-10.15 EndY=-14 EndZ=0
    g11: LineSegment StartX=-12.8401 StartY=-16 StartZ=0 EndX=-10.1571 EndY=-16 EndZ=0
    g12: LineSegment StartX=-10.15 StartY=-14 StartZ=0 EndX=-8.70761 EndY=-14 EndZ=0
    g13: LineSegment StartX=-12.8401 StartY=-16 StartZ=0 EndX=-12.8401 EndY=-17.6958 EndZ=0
    g14: LineSegment StartX=-10.15 StartY=-12 StartZ=0 EndX=-7.79258 EndY=-12 EndZ=0
    g15: Circle CenterX=-6.2215 CenterY=-2 CenterZ=0 NormalX=0 NormalY=0 NormalZ=1 AngleXU=0 Radius=1
    g16: Circle CenterX=-6.22762 CenterY=-2.58724 CenterZ=0 NormalX=0 NormalY=0 NormalZ=1 AngleXU=0 Radius=1
    g17: Circle CenterX=-6.32538 CenterY=-4 CenterZ=0 NormalX=0 NormalY=0 NormalZ=1 AngleXU=0 Radius=1
    g18: BSplineCurve PolesCount=3 KnotsCount=2 Degree=2 IsPeriodic=0
    g19: GeomPoint X=-6.2215 Y=-2 Z=0
    g20: GeomPoint X=-6.32538 Y=-4 Z=0
    g21: Circle CenterX=-6.48644 CenterY=-5.99526 CenterZ=0 NormalX=0 NormalY=0 NormalZ=1 AngleXU=0 Radius=1
    g22: Circle CenterX=-6.58486 CenterY=-6.99526 CenterZ=0 NormalX=0 NormalY=0 NormalZ=1 AngleXU=0 Radius=1
    g23: Circle CenterX=-6.77343 CenterY=-8 CenterZ=0 NormalX=0 NormalY=0 NormalZ=1 AngleXU=0 Radius=1
    g24: BSplineCurve PolesCount=3 KnotsCount=2 Degree=2 IsPeriodic=0
    g25: GeomPoint X=-6.48644 Y=-5.99526 Z=0
    g26: GeomPoint X=-6.77343 Y=-8 Z=0
    g27: Circle CenterX=-7.19003 CenterY=-10 CenterZ=0 NormalX=0 NormalY=0 NormalZ=1 AngleXU=0 Radius=1
    g28: Circle CenterX=-7.44407 CenterY=-11.0915 CenterZ=0 NormalX=0 NormalY=0 NormalZ=1 AngleXU=0 Radius=1
    g29: Circle CenterX=-7.79258 CenterY=-12 CenterZ=0 NormalX=0 NormalY=0 NormalZ=1 AngleXU=0 Radius=1
    g30: BSplineCurve PolesCount=3 KnotsCount=2 Degree=2 IsPeriodic=0
    g31: GeomPoint X=-7.19003 Y=-10 Z=0
    g32: GeomPoint X=-7.79258 Y=-12 Z=0
    g33: Circle CenterX=-8.70761 CenterY=-14 CenterZ=0 NormalX=0 NormalY=0 NormalZ=1 AngleXU=0 Radius=1
    g34: Circle CenterX=-9.33087 CenterY=-15.1837 CenterZ=0 NormalX=0 NormalY=0 NormalZ=1 AngleXU=0 Radius=1
    g35: Circle CenterX=-10.1571 CenterY=-16 CenterZ=0 NormalX=0 NormalY=0 NormalZ=1 AngleXU=0 Radius=1
    g36: BSplineCurve PolesCount=3 KnotsCount=2 Degree=2 IsPeriodic=0
    g37: GeomPoint X=-8.70761 Y=-14 Z=0
    g38: GeomPoint X=-10.1571 Y=-16 Z=0
    g39: Circle CenterX=-12.8401 CenterY=-17.6958 CenterZ=0 NormalX=0 NormalY=0 NormalZ=1 AngleXU=0 Radius=1
    g40: Circle CenterX=-13.3521 CenterY=-17.9027 CenterZ=0 NormalX=0 NormalY=0 NormalZ=1 AngleXU=0 Radius=1
    g41: Circle CenterX=-14 CenterY=-18 CenterZ=0 NormalX=0 NormalY=0 NormalZ=1 AngleXU=0 Radius=1
    g42: BSplineCurve PolesCount=3 KnotsCount=2 Degree=2 IsPeriodic=0
    g43: GeomPoint X=-12.8401 Y=-17.6958 Z=0
    g44: GeomPoint X=-14 Y=-18 Z=0
    g45: LineSegment StartX=-6.2 StartY=0 StartZ=0 EndX=-7.2 EndY=0 EndZ=0
    g46: LineSegment StartX=-7.2 StartY=0 StartZ=0 EndX=-7.2 EndY=-2 EndZ=0
    g47: LineSegment StartX=-7.2 StartY=-2 StartZ=0 EndX=-6.2215 EndY=-2 EndZ=0
    g48: LineSegment StartX=-6.32538 StartY=-4 StartZ=0 EndX=-7.65538 EndY=-4 EndZ=0
    g49: LineSegment StartX=-7.65538 StartY=-4 StartZ=0 EndX=-7.65538 EndY=-5.99526 EndZ=0
    g50: LineSegment StartX=-7.65538 StartY=-5.99526 StartZ=0 EndX=-6.48644 EndY=-5.99526 EndZ=0
    g51: LineSegment StartX=-6.77343 StartY=-8 StartZ=0 EndX=-8.43343 EndY=-8 EndZ=0
    g52: LineSegment StartX=-8.43343 StartY=-8 StartZ=0 EndX=-8.43343 EndY=-10 EndZ=0
    g53: LineSegment StartX=-8.43343 StartY=-10 StartZ=0 EndX=-7.19003 EndY=-10 EndZ=0
  constraints (112):
    c: Horizontal(g0)
    c: Distance(g0) = 2
    c: Block(g0)
    c: Vertical(g1)
    c: Coincident(g2,g0)
    c: Vertical(g2)
    c: Block(g2)
    c: Coincident(g6,g2)
    c: Weight(g3) = 1
    c: Equal(g3,g4)
    c: Equal(g3,g5)
    c: InternalAlignment(g3,g6)
    c: InternalAlignment(g4,g6)
    c: InternalAlignment(g5,g6)
    c: InternalAlignment(g7,g6)
    c: InternalAlignment(g8,g6)
    c: Block(g6)
    c: Coincident(g9,g1)
    c: Coincident(g9,g6)
    c: Horizontal(g9)
    c: Vertical(g10)
    c: Block(g10)
    c: Horizontal(g11)
    c: Block(g11)
    c: Coincident(g12,g10)
    c: Horizontal(g12)
    c: Block(g12)
    c: Coincident(g13,g11)
    c: Vertical(g13)
    c: Block(g13)
    c: Coincident(g14,g10)
    c: Horizontal(g14)
    c: Block(g14)
    c: Block(g9)
    c: Block(g1)
    c: Weight(g15) = 1
    c: Equal(g15,g16)
    c: Equal(g15,g17)
    c: InternalAlignment(g15,g18)
    c: InternalAlignment(g16,g18)
    c: InternalAlignment(g17,g18)
    c: InternalAlignment(g19,g18)
    c: InternalAlignment(g20,g18)
    c: Weight(g21) = 1
    c: Equal(g21,g22)
    c: Equal(g21,g23)
    c: InternalAlignment(g21,g24)
    c: InternalAlignment(g22,g24)
    c: InternalAlignment(g23,g24)
    c: InternalAlignment(g25,g24)
    c: InternalAlignment(g26,g24)
    c: Weight(g27) = 1
    c: Equal(g27,g28)
    c: Equal(g27,g29)
    c: Coincident(g30,g14)
    c: InternalAlignment(g27,g30)
    c: InternalAlignment(g28,g30)
    c: InternalAlignment(g29,g30)
    c: InternalAlignment(g31,g30)
    c: InternalAlignment(g32,g30)
    c: Coincident(g36,g12)
    c: Weight(g33) = 1
    c: Equal(g33,g34)
    c: Equal(g33,g35)
    c: Coincident(g36,g11)
    c: InternalAlignment(g33,g36)
    c: InternalAlignment(g34,g36)
    c: InternalAlignment(g35,g36)
    c: InternalAlignment(g37,g36)
    c: InternalAlignment(g38,g36)
    c: Coincident(g42,g13)
    c: Weight(g39) = 1
    c: Equal(g39,g40)
    c: Equal(g39,g41)
    c: Coincident(g42,g1)
    c: InternalAlignment(g39,g42)
    c: InternalAlignment(g40,g42)
    c: InternalAlignment(g41,g42)
    c: InternalAlignment(g43,g42)
    c: InternalAlignment(g44,g42)
    c: Block(g18)
    c: Block(g24)
    c: Block(g30)
    c: Block(g36)
    c: Block(g42)
    c: Horizontal(g45)
    c: Coincident(g45,g0)
    c: Vertical(g46)
    c: Coincident(g46,g45)
    c: Coincident(g47,g46)
    c: Coincident(g47,g18)
    c: Horizontal(g47)
    c: Block(g46)
    c: Coincident(g48,g18)
    c: Horizontal(g48)
    c: Distance(g48) = 1.33
    c: Vertical(g49)
    c: Coincident(g49,g48)
    c: Coincident(g50,g49)
    c: Coincident(g50,g24)
    c: Horizontal(g50)
    c: Tangent(g50,g22)
    c: Horizontal(g51)
    c: Coincident(g51,g24)
    c: Block(g51)
    c: Vertical(g52)
    c: Block(g52)
    c: Coincident(g52,g51)
    c: Coincident(g53,g52)
    c: Coincident(g53,g30)
    c: Horizontal(g53)
    c: Distance(g1) = 8.5
FEATURE [Part::Feature] Face024
  shape: bbox 9.8 x 26.5 x 2e-07 mm, 1 faces, 0 solids (baked)
FEATURE [Part::Revolution] Revolve024
  Angle = 360
  Axis = (0,1,0)
  Base = (0,0,0)
  FaceMakerClass = Part::FaceMakerBullseye
  Placement = pos=(0,0,0) rot=(0,0,1;1.5708rad)
  Solid = false
  Source = -> Face024
  Symmetric = false
FEATURE [Part::Feature] Face025
  shape: bbox 9.8 x 26.5 x 2e-07 mm, 1 faces, 0 solids (baked)
FEATURE [Part::Revolution] Revolve025
  Angle = 360
  Axis = (0,1,0)
  Base = (0,0,0)
  FaceMakerClass = Part::FaceMakerBullseye
  Placement = pos=(0,0,0) rot=(0,0,1;1.5708rad)
  Solid = false
  Source = -> Face025
  Symmetric = false
FEATURE [Part::MultiFuse] Fusion033
  Placement = pos=(-18,19,36) rot=(0,0,1;0rad)
  Shapes = -> [Revolve025,Revolve024]
FEATURE [Part::Cylinder] Cylinder014
  Angle = 360
  AttacherType = Attacher::AttachEngine3D
  Height = 20
  Placement = pos=(0,0,36.15) rot=(0,0,1;0rad)
  Radius = 14.3
FEATURE [Part::Cylinder] Cylinder015
  Angle = 360
  AttacherType = Attacher::AttachEngine3D
  Height = 10
  Placement = pos=(0,0,36.15) rot=(0,0,1;0rad)
  Radius = 4
FEATURE [Part::MultiFuse] Fusion034  label="removeToCreteHoleForPlugHousing004"
  Placement = pos=(-42,19,36) rot=(0,1,0;1.5708rad)
  Shapes = -> [Cylinder014,Cylinder015]
FEATURE [Part::Cut] Cut008  label="top004"
  Base = -> Cut004
  Placement = pos=(-1,0,0) rot=(0,0,1;0rad)
  Tool = -> Fusion034
FEATURE [Part::Box] Box005  label="Cube005"
  AttacherType = Attacher::AttachEngine3D
  Height = 28
  Length = 3
  Placement = pos=(110.7,19,22) rot=(0,0,1;0rad)
  Width = 15.7
FEATURE [Part::Cylinder] Cylinder016
  Angle = 360
  AttacherType = Attacher::AttachEngine3D
  Height = 10
  Placement = pos=(0,0,36.15) rot=(0,0,1;0rad)
  Radius = 4
FEATURE [Part::Cylinder] Cylinder017
  Angle = 360
  AttacherType = Attacher::AttachEngine3D
  Height = 20
  Placement = pos=(0,0,36.15) rot=(0,0,1;0rad)
  Radius = 10.3
FEATURE [Part::MultiFuse] Fusion035  label="removeToCreteHoleForPlugHousing005"
  Placement = pos=(70,19,36) rot=(0,1,0;1.5708rad)
  Shapes = -> [Cylinder017,Cylinder016]
FEATURE [Part::Cut] Cut009  label="plugHousingTab001"
  Base = -> Box005
  Placement = pos=(-107.4,-14,0) rot=(0,0,1;0rad)
  Tool = -> Fusion035
FEATURE [Part::Box] Box006  label="Cube006"
  AttacherType = Attacher::AttachEngine3D
  Height = 28
  Length = 3
  Placement = pos=(110.7,19,22) rot=(0,0,1;0rad)
  Width = 15.7
FEATURE [Part::Cylinder] Cylinder018
  Angle = 360
  AttacherType = Attacher::AttachEngine3D
  Height = 10
  Placement = pos=(0,0,36.15) rot=(0,0,1;0rad)
  Radius = 4
FEATURE [Part::Cylinder] Cylinder019
  Angle = 360
  AttacherType = Attacher::AttachEngine3D
  Height = 20
  Placement = pos=(0,0,36.15) rot=(0,0,1;0rad)
  Radius = 10.3
FEATURE [Part::MultiFuse] Fusion036  label="removeToCreteHoleForPlugHousing006"
  Placement = pos=(70,19,36) rot=(0,1,0;1.5708rad)
  Shapes = -> [Cylinder019,Cylinder018]
FEATURE [Part::Cut] Cut010  label="plugHousingTab002"
  Base = -> Box006
  Placement = pos=(-107.4,-14,0) rot=(0,0,1;0rad)
  Tool = -> Fusion036
FEATURE [Part::MultiFuse] Fusion037
  Placement = pos=(9.6,23,0) rot=(0,0,1;3.14159rad)
  Shapes = -> [Cut009,Cut010]
FEATURE [Part::Box] Box  label="Cube"
  AttacherType = Attacher::AttachEngine3D
  Height = 10
  Length = 3
  Placement = pos=(3.3,4,12) rot=(0,0,1;0rad)
  Width = 10
FEATURE [Part::Fillet] Fillet004
  Base = -> Fusion028
  Edges = 1 edges r=2: [Edge25]
FEATURE [Part::Fillet] Fillet005  label="plugHousing046"
  Base = -> Fillet004
  Edges = 1 edges r=2: [Edge8]
FEATURE [Part::Fillet] Fillet006
  Base = -> Box
  Edges = 1 edges r=2: [Edge11]
FEATURE [Part::Box] Box007  label="Cube007"
  AttacherType = Attacher::AttachEngine3D
  Height = 10
  Length = 3
  Placement = pos=(3.3,4,50) rot=(0,0,1;0rad)
  Width = 10
FEATURE [Part::Fillet] Fillet007
  Base = -> Box007
  Edges = 1 edges r=2: [Edge12]
FEATURE [Part::Box] Box008  label="Cube008"
  AttacherType = Attacher::AttachEngine3D
  Height = 28
  Length = 4
  Placement = pos=(5,0,22) rot=(0,0,1;0rad)
  Width = 10
FEATURE [Part::Fillet] Fillet008
  Base = -> Box008
  Edges = 1 edges r=1: [Edge7]
FEATURE [Part::Fillet] Fillet009
  Base = -> Fillet008
  Edges = 1 edges r=2: [Edge5]
FEATURE [Part::Fillet] Fillet010
  Base = -> Fillet009
  Edges = 1 edges r=2: [Edge2]
FEATURE [Sketcher::SketchObject] Sketch009  label="topSketch003"
  FullyConstrained = true
  sketch-geometry (4):
    g0: LineSegment StartX=16.8446 StartY=31.512 StartZ=0 EndX=16.3251 EndY=34.4666 EndZ=0
    g1: ArcOfCircle CenterX=19 CenterY=19.2524 CenterZ=0 NormalX=0 NormalY=0 NormalZ=1 AngleXU=0 Radius=15.4476 StartAngle=1.74483 EndAngle=2.72717
    g2: ArcOfCircle CenterX=19 CenterY=19.2524 CenterZ=0 NormalX=0 NormalY=0 NormalZ=1 AngleXU=0 Radius=12.4476 StartAngle=1.74483 EndAngle=2.73189
    g3: LineSegment StartX=4.86004 StartY=25.4725 StartZ=0 EndX=7.58253 EndY=24.2107 EndZ=0
  constraints (7):
    c: Block(g0)
    c: Coincident(g1,g0)
    c: Coincident(g2,g0)
    c: Coincident(g3,g1)
    c: Coincident(g3,g2)
    c: Block(g1)
    c: Block(g2)
FEATURE [Part::Extrusion] Extrude008
  Base = -> Sketch009
  Dir = (0,0,1)
  DirMode = 2
  FaceMakerClass = Part::FaceMakerBullseye
  LengthFwd = 10
  LengthRev = 0
  Placement = pos=(0,0,31) rot=(0,0,1;0rad)
  Solid = true
  Symmetric = false
FEATURE [Part::Cylinder] Cylinder020
  Angle = 360
  AttacherType = Attacher::AttachEngine3D
  Height = 20
  Placement = pos=(0,0,36.15) rot=(0,0,1;0rad)
  Radius = 8.2
FEATURE [Part::Cylinder] Cylinder021
  Angle = 360
  AttacherType = Attacher::AttachEngine3D
  Height = 10
  Placement = pos=(0,0,36.15) rot=(0,0,1;0rad)
  Radius = 4
FEATURE [Part::MultiFuse] Fusion038  label="removeToCreteHoleForPlugHousing007"
  Placement = pos=(-42,19,36) rot=(0,1,0;1.5708rad)
  Shapes = -> [Cylinder020,Cylinder021]
FEATURE [Part::Cut] Cut011
  Base = -> Extrude008
  Tool = -> Fusion038
FEATURE [Part::Fillet] Fillet011
  Base = -> Cut011
  Edges = 1 edges r=2: [Edge1]
FEATURE [Part::Fillet] Fillet012
  Base = -> Fillet011
  Edges = 1 edges r=2.5: [Edge1]
FEATURE [Part::Fillet] Fillet013
  Base = -> Fillet012
  Edges = 1 edges r=2.5: [Edge2]
FEATURE [Part::Box] Box010  label="Cube010"
  AttacherType = Attacher::AttachEngine3D
  Height = 16
  Length = 8
  Placement = pos=(12.7,31.52,28) rot=(0,0,1;0rad)
  Width = 4
FEATURE [Sketcher::SketchObject] Sketch010  label="topSketch004"
  FullyConstrained = true
  sketch-geometry (4):
    g0: LineSegment StartX=16.8446 StartY=31.512 StartZ=0 EndX=16.3251 EndY=34.4666 EndZ=0
    g1: ArcOfCircle CenterX=19 CenterY=19.2524 CenterZ=0 NormalX=0 NormalY=0 NormalZ=1 AngleXU=0 Radius=15.4476 StartAngle=1.74483 EndAngle=2.72717
    g2: ArcOfCircle CenterX=19 CenterY=19.2524 CenterZ=0 NormalX=0 NormalY=0 NormalZ=1 AngleXU=0 Radius=12.4476 StartAngle=1.74483 EndAngle=2.73189
    g3: LineSegment StartX=4.86004 StartY=25.4725 StartZ=0 EndX=7.58253 EndY=24.2107 EndZ=0
  constraints (7):
    c: Block(g0)
    c: Coincident(g1,g0)
    c: Coincident(g2,g0)
    c: Coincident(g3,g1)
    c: Coincident(g3,g2)
    c: Block(g1)
    c: Block(g2)
FEATURE [Part::Cylinder] Cylinder022
  Angle = 360
  AttacherType = Attacher::AttachEngine3D
  Height = 10
  Placement = pos=(0,0,36.15) rot=(0,0,1;0rad)
  Radius = 4
FEATURE [Sketcher::SketchObject] Sketch011  label="topSketch005"
  FullyConstrained = true
  sketch-geometry (4):
    g0: LineSegment StartX=16.8446 StartY=31.512 StartZ=0 EndX=16.3251 EndY=34.4666 EndZ=0
    g1: ArcOfCircle CenterX=19 CenterY=19.2524 CenterZ=0 NormalX=0 NormalY=0 NormalZ=1 AngleXU=0 Radius=15.4476 StartAngle=1.74483 EndAngle=2.72717
    g2: ArcOfCircle CenterX=19 CenterY=19.2524 CenterZ=0 NormalX=0 NormalY=0 NormalZ=1 AngleXU=0 Radius=12.4476 StartAngle=1.74483 EndAngle=2.73189
    g3: LineSegment StartX=4.86004 StartY=25.4725 StartZ=0 EndX=7.58253 EndY=24.2107 EndZ=0
  constraints (7):
    c: Block(g0)
    c: Coincident(g1,g0)
    c: Coincident(g2,g0)
    c: Coincident(g3,g1)
    c: Coincident(g3,g2)
    c: Block(g1)
    c: Block(g2)
FEATURE [Part::Extrusion] Extrude010
  Base = -> Sketch011
  Dir = (0,0,1)
  DirMode = 2
  FaceMakerClass = Part::FaceMakerBullseye
  LengthFwd = 10.6
  LengthRev = 0
  Placement = pos=(0,0,31) rot=(0,0,1;0rad)
  Solid = true
  Symmetric = false
FEATURE [Part::Cylinder] Cylinder023
  Angle = 360
  AttacherType = Attacher::AttachEngine3D
  Height = 20
  Placement = pos=(0,0,36.15) rot=(0,0,1;0rad)
  Radius = 8.2
FEATURE [Part::MultiFuse] Fusion039  label="removeToCreteHoleForPlugHousing008"
  Placement = pos=(-42,19,36) rot=(0,1,0;1.5708rad)
  Shapes = -> [Cylinder023,Cylinder022]
FEATURE [Part::Cut] Cut012
  Base = -> Extrude010
  Placement = pos=(0,0,-0.3) rot=(0,0,1;0rad)
  Tool = -> Fusion039
FEATURE [Part::Cut] Cut013
  Base = -> Box010
  Tool = -> Cut012
FEATURE [Part::Fillet] Fillet014
  Base = -> Cut013
  Edges = 1 edges r=0.7: [Edge13]
FEATURE [Part::Fillet] Fillet015
  Base = -> Fillet014
  Edges = 1 edges r=0.7: [Edge13]
FEATURE [Part::Fillet] Fillet016
  Base = -> Fillet015
  Edges = 1 edges r=0.7: [Edge16]
FEATURE [Part::Fillet] Fillet017
  Base = -> Fillet016
  Edges = 1 edges r=0.7: [Edge11]
FEATURE [Part::Fillet] Fillet018
  Base = -> Fillet017
  Edges = 1 edges r=0.7: [Edge10]
FEATURE [Part::Fillet] Fillet019
  Base = -> Fillet018
  Edges = 1 edges r=1.2: [Edge5]
FEATURE [Part::Fillet] Fillet020
  Base = -> Fillet019
  Edges = 1 edges r=1.2: [Edge12]
FEATURE [Part::Fillet] Fillet021
  Base = -> Fillet020
  Edges = 1 edges r=2: [Edge1]
  Placement = pos=(0.3,0,0) rot=(0,0,1;0rad)
FEATURE [Part::MultiFuse] Fusion040  label="top005"
  Shapes = -> [Cut008,Fillet021]
FEATURE [Part::MultiFuse] Fusion041  label="wireHolder"
  Shapes = -> [Fusion033,Fillet013]
FEATURE [Part::MultiFuse] Fusion042
  Shapes = -> [Fillet007,Fusion041]
FEATURE [Part::MultiFuse] Fusion043  label="wireHolder001"
  Shapes = -> [Fusion042,Fillet010]
FEATURE [Part::MultiFuse] Fusion044  label="wireHolder002"
  Shapes = -> [Fillet006,Fusion037,Fusion043]
FEATURE [Part::Feature] Face026
  shape: bbox 11 x 6 x 2e-07 mm, 1 faces, 0 solids (baked)
FEATURE [Part::Revolution] Revolve026
  Angle = 360
  Axis = (0,1,0)
  Base = (0,0,0)
  FaceMakerClass = Part::FaceMakerBullseye
  Placement = pos=(30.3,-1,19.7) rot=(0,0,1;0rad)
  Solid = false
  Source = -> Face026
  Symmetric = false
FEATURE [Sketcher::SketchObject] Sketch013  label="topSketch006"
  FullyConstrained = true
  sketch-geometry (13):
    g0: LineSegment StartX=117 StartY=19 StartZ=0 EndX=117 EndY=38 EndZ=0
    g1: ArcOfCircle CenterX=98 CenterY=19 CenterZ=0 NormalX=0 NormalY=0 NormalZ=1 AngleXU=0 Radius=19 StartAngle=5.7297 EndAngle=6.28319
    g2: LineSegment StartX=0 StartY=3 StartZ=0 EndX=0 EndY=19 EndZ=0
    g3: LineSegment StartX=19 StartY=38 StartZ=0 EndX=117 EndY=38 EndZ=0
    g4: ArcOfCircle CenterX=19 CenterY=19 CenterZ=0 NormalX=0 NormalY=0 NormalZ=1 AngleXU=0 Radius=19 StartAngle=1.5708 EndAngle=3.14159
    g5: ArcOfCircle CenterX=19 CenterY=19 CenterZ=0 NormalX=0 NormalY=0 NormalZ=1 AngleXU=0 Radius=16 StartAngle=1.5708 EndAngle=3.14159
    g6: ArcOfCircle CenterX=98 CenterY=19 CenterZ=0 NormalX=0 NormalY=0 NormalZ=1 AngleXU=0 Radius=16 StartAngle=5.60905 EndAngle=6.28319
    g7: LineSegment StartX=114 StartY=19 StartZ=0 EndX=114 EndY=35 EndZ=0
    g8: LineSegment StartX=110.5 StartY=9.01251 StartZ=0 EndX=114.163 EndY=9.01251 EndZ=0
    g9: LineSegment StartX=114 StartY=35 StartZ=0 EndX=19 EndY=35 EndZ=0
    g10: LineSegment StartX=0 StartY=3 StartZ=0 EndX=0 EndY=0 EndZ=0
    g11: LineSegment StartX=3 StartY=0 StartZ=0 EndX=0 EndY=0 EndZ=0
    g12: LineSegment StartX=3 StartY=19 StartZ=0 EndX=3 EndY=0 EndZ=0
  constraints (33):
    c: Vertical(g0)
    c: Distance(g0) = 19
    c: Block(g0)
    c: Coincident(g1,g0)
    c: Block(g1)
    c: Vertical(g2)
    c: Block(g2)
    c: Coincident(g3,g0)
    c: Horizontal(g3)
    c: Distance(g3) = 98
    c: Coincident(g4,g3)
    c: Coincident(g4,g2)
    c: Block(g4)
    c: Coincident(g5,g4)
    c: Coincident(g6,g1)
    c: Block(g6)
    c: Block(g5)
    c: Coincident(g7,g6)
    c: Vertical(g7)
    c: Coincident(g8,g6)
    c: Coincident(g8,g1)
    c: Coincident(g9,g7)
    c: Coincident(g9,g5)
    c: Horizontal(g9)
    c: Tangent(g9,g5)
    c: Coincident(g10,g2)
    c: Distance(g10) = 3
    c: Vertical(g10)
    c: Coincident(g11,g10)
    c: Horizontal(g11)
    c: Coincident(g12,g5)
    c: Coincident(g12,g11)
    c: Vertical(g12)
FEATURE [Part::Extrusion] Extrude011  label="top006"
  Base = -> Sketch013
  Dir = (0,0,1)
  DirMode = 2
  FaceMakerClass = Part::FaceMakerBullseye
  LengthFwd = 72
  LengthRev = 0
  Solid = true
  Symmetric = false
FEATURE [Sketcher::SketchObject] Sketch014
  FullyConstrained = true
  MapMode = 3
  Placement = pos=(0,0,0) rot=(1,0,0;1.5708rad)
  Support = -> [Extrude011]
  sketch-geometry (8):
    g0: Circle CenterX=80.351 CenterY=-67.6202 CenterZ=0 NormalX=0 NormalY=0 NormalZ=1 AngleXU=0 Radius=2
    g1: Circle CenterX=80.351 CenterY=-67.6202 CenterZ=0 NormalX=0 NormalY=0 NormalZ=1 AngleXU=0 Radius=3
    g2: Circle CenterX=80.351 CenterY=-4.92017 CenterZ=0 NormalX=0 NormalY=0 NormalZ=1 AngleXU=0 Radius=2
    g3: Circle CenterX=80.351 CenterY=-4.92017 CenterZ=0 NormalX=0 NormalY=0 NormalZ=1 AngleXU=0 Radius=3
    g4: Circle CenterX=23.851 CenterY=-4.92017 CenterZ=0 NormalX=0 NormalY=0 NormalZ=1 AngleXU=0 Radius=2
    g5: Circle CenterX=23.851 CenterY=-4.92017 CenterZ=0 NormalX=0 NormalY=0 NormalZ=1 AngleXU=0 Radius=3
    g6: Circle CenterX=23.851 CenterY=-67.6202 CenterZ=0 NormalX=0 NormalY=0 NormalZ=1 AngleXU=0 Radius=2
    g7: Circle CenterX=23.851 CenterY=-67.6202 CenterZ=0 NormalX=0 NormalY=0 NormalZ=1 AngleXU=0 Radius=3
  constraints (8):
    c: Block(g3)
    c: Block(g2)
    c: Block(g1)
    c: Block(g0)
    c: Block(g6)
    c: Block(g7)
    c: Block(g4)
    c: Block(g5)
FEATURE [Part::Feature] Face027
  shape: bbox 11 x 6 x 2e-07 mm, 1 faces, 0 solids (baked)
FEATURE [Part::Revolution] Revolve027
  Angle = 360
  Axis = (0,1,0)
  Base = (0,0,0)
  FaceMakerClass = Part::FaceMakerBullseye
  Placement = pos=(30.3,-1,51.7) rot=(0,0,1;0rad)
  Solid = false
  Source = -> Face027
  Symmetric = false
FEATURE [Part::Feature] Face028
  shape: bbox 11 x 6 x 2e-07 mm, 1 faces, 0 solids (baked)
FEATURE [Part::Revolution] Revolve028
  Angle = 360
  Axis = (0,1,0)
  Base = (0,0,0)
  FaceMakerClass = Part::FaceMakerBullseye
  Placement = pos=(62.3,-1,19.7) rot=(0,0,1;0rad)
  Solid = false
  Source = -> Face028
  Symmetric = false
FEATURE [Part::Feature] Face029
  shape: bbox 11 x 6 x 2e-07 mm, 1 faces, 0 solids (baked)
FEATURE [Part::Revolution] Revolve029
  Angle = 360
  Axis = (0,1,0)
  Base = (0,0,0)
  FaceMakerClass = Part::FaceMakerBullseye
  Placement = pos=(62.3,-1,51.7) rot=(0,0,1;0rad)
  Solid = false
  Source = -> Face029
  Symmetric = false
FEATURE [Part::Feature] Wire
  shape: bbox 11 x 5.2 x 2e-07 mm, 0 faces, 0 solids (baked)
FEATURE [Part::Revolution] Revolve030
  Angle = 360
  Axis = (0,1,0)
  Base = (0,0,0)
  FaceMakerClass = Part::FaceMakerBullseye
  Placement = pos=(30.3,38,19.7) rot=(0,0,1;0rad)
  Solid = true
  Source = -> Wire
  Symmetric = false
FEATURE [Part::Feature] Wire001
  shape: bbox 11 x 5.2 x 2e-07 mm, 0 faces, 0 solids (baked)
FEATURE [Part::Revolution] Revolve031
  Angle = 360
  Axis = (0,1,0)
  Base = (0,0,0)
  FaceMakerClass = Part::FaceMakerBullseye
  Placement = pos=(30.3,38,51.7) rot=(0,0,1;0rad)
  Solid = true
  Source = -> Wire001
  Symmetric = false
FEATURE [Part::Feature] Wire002
  shape: bbox 11 x 5.2 x 2e-07 mm, 0 faces, 0 solids (baked)
FEATURE [Part::Revolution] Revolve032
  Angle = 360
  Axis = (0,1,0)
  Base = (0,0,0)
  FaceMakerClass = Part::FaceMakerBullseye
  Placement = pos=(62.3,38,51.7) rot=(0,0,1;0rad)
  Solid = true
  Source = -> Wire002
  Symmetric = false
FEATURE [Part::Feature] Wire003
  shape: bbox 11 x 5.2 x 2e-07 mm, 0 faces, 0 solids (baked)
FEATURE [Part::Revolution] Revolve033
  Angle = 360
  Axis = (0,1,0)
  Base = (0,0,0)
  FaceMakerClass = Part::FaceMakerBullseye
  Placement = pos=(62.3,38,19.7) rot=(0,0,1;0rad)
  Solid = true
  Source = -> Wire003
  Symmetric = false
FEATURE [Part::MultiFuse] Fusion045  label="altRandScrewHousing"
  Shapes = -> [Revolve029,Revolve027,Revolve028,Revolve026]
FEATURE [Part::MultiFuse] Fusion046  label="fanScrewHousing"
  Shapes = -> [Revolve033,Revolve032,Revolve031,Revolve030]
FEATURE [Sketcher::SketchObject] Sketch015
  FullyConstrained = true
  sketch-geometry (17):
    g0: Circle CenterX=-3.5 CenterY=23.5 CenterZ=0 NormalX=0 NormalY=0 NormalZ=1 AngleXU=0 Radius=1
    g1: Circle CenterX=-1 CenterY=15.25 CenterZ=0 NormalX=0 NormalY=0 NormalZ=1 AngleXU=0 Radius=1
    g2: Circle CenterX=-3.5 CenterY=7 CenterZ=0 NormalX=0 NormalY=0 NormalZ=1 AngleXU=0 Radius=1
    g3: BSplineCurve PolesCount=3 KnotsCount=2 Degree=2 IsPeriodic=0
    g4: GeomPoint X=-3.5 Y=23.5 Z=0
    g5: GeomPoint X=-3.5 Y=7 Z=0
    g6: Circle CenterX=-4.8 CenterY=30.5 CenterZ=0 NormalX=0 NormalY=0 NormalZ=1 AngleXU=0 Radius=1
    g7: Circle CenterX=-3.5 CenterY=30.5 CenterZ=0 NormalX=0 NormalY=0 NormalZ=1 AngleXU=0 Radius=1
    g8: Circle CenterX=-3.5 CenterY=29.2 CenterZ=0 NormalX=0 NormalY=0 NormalZ=1 AngleXU=0 Radius=1
    g9: BSplineCurve PolesCount=3 KnotsCount=2 Degree=2 IsPeriodic=0
    g10: GeomPoint X=-4.8 Y=30.5 Z=0
    g11: GeomPoint X=-3.5 Y=29.2 Z=0
    g12: LineSegment StartX=-3.5 StartY=29.2 StartZ=0 EndX=-3.5 EndY=23.5 EndZ=0
    g13: LineSegment StartX=-4.8 StartY=30.5 StartZ=0 EndX=0 EndY=30.5 EndZ=0
    g14: LineSegment StartX=-3.5 StartY=0.3 StartZ=0 EndX=0 EndY=0.3 EndZ=0
    g15: LineSegment StartX=-3.5 StartY=0.3 StartZ=0 EndX=-3.5 EndY=7 EndZ=0
    g16: LineSegment StartX=0 StartY=0.3 StartZ=0 EndX=0 EndY=30.5 EndZ=0
  constraints (33):
    c: Weight(g0) = 1
    c: Equal(g0,g1)
    c: Equal(g0,g2)
    c: InternalAlignment(g0,g3)
    c: InternalAlignment(g1,g3)
    c: InternalAlignment(g2,g3)
    c: InternalAlignment(g4,g3)
    c: InternalAlignment(g5,g3)
    c: Block(g3)
    c: Weight(g6) = 1
    c: Equal(g6,g7)
    c: Equal(g6,g8)
    c: InternalAlignment(g6,g9)
    c: InternalAlignment(g7,g9)
    c: InternalAlignment(g8,g9)
    c: InternalAlignment(g10,g9)
    c: InternalAlignment(g11,g9)
    c: Block(g9)
    c: Coincident(g12,g9)
    c: Coincident(g12,g3)
    c: Vertical(g12)
    c: Coincident(g13,g9)
    c: Horizontal(g13)
    c: Distance(g13) = 4.8
    c: Horizontal(g14)
    c: Block(g14)
    c: Coincident(g15,g14)
    c: Coincident(g15,g3)
    c: Vertical(g15)
    c: Coincident(g16,g14)
    c: Coincident(g16,g13)
    c: Vertical(g16)
    c: Tangent(g16,g1)
FEATURE [Sketcher::SketchObject] Sketch016
  FullyConstrained = true
  sketch-geometry (16):
    g0: Circle CenterX=-3.5 CenterY=23.5 CenterZ=0 NormalX=0 NormalY=0 NormalZ=1 AngleXU=0 Radius=1
    g1: Circle CenterX=-1 CenterY=15.25 CenterZ=0 NormalX=0 NormalY=0 NormalZ=1 AngleXU=0 Radius=1
    g2: Circle CenterX=-3.5 CenterY=7 CenterZ=0 NormalX=0 NormalY=0 NormalZ=1 AngleXU=0 Radius=1
    g3: BSplineCurve PolesCount=3 KnotsCount=2 Degree=2 IsPeriodic=0
    g4: GeomPoint X=-3.5 Y=23.5 Z=0
    g5: GeomPoint X=-3.5 Y=7 Z=0
    g6: LineSegment StartX=-3.5 StartY=28.2 StartZ=0 EndX=-3.5 EndY=23.5 EndZ=0
    g7: LineSegment StartX=0 StartY=29.5 StartZ=0 EndX=0 EndY=30 EndZ=0
    g8: LineSegment StartX=-3.5 StartY=28.2 StartZ=0 EndX=-3.5 EndY=30 EndZ=0
    g9: LineSegment StartX=0 StartY=30 StartZ=0 EndX=0 EndY=30.5 EndZ=0
    g10: LineSegment StartX=0 StartY=30.5 StartZ=0 EndX=-3.5 EndY=30.5 EndZ=0
    g11: LineSegment StartX=-3.5 StartY=30.5 StartZ=0 EndX=-3.5 EndY=30 EndZ=0
    g12: LineSegment StartX=0 StartY=29.5 StartZ=0 EndX=0 EndY=5 EndZ=0
    g13: LineSegment StartX=-3.5 StartY=0.3 StartZ=0 EndX=-3.5 EndY=7 EndZ=0
    g14: LineSegment StartX=-3.5 StartY=0.3 StartZ=0 EndX=0 EndY=0.3 EndZ=0
    g15: LineSegment StartX=0 StartY=5 StartZ=0 EndX=0 EndY=0.3 EndZ=0
  constraints (39):
    c: Weight(g0) = 1
    c: Equal(g0,g1)
    c: Equal(g0,g2)
    c: InternalAlignment(g0,g3)
    c: InternalAlignment(g1,g3)
    c: InternalAlignment(g2,g3)
    c: InternalAlignment(g4,g3)
    c: InternalAlignment(g5,g3)
    c: Block(g3)
    c: Coincident(g6,g3)
    c: Vertical(g6)
    c: Vertical(g7)
    c: Distance(g7) = 0.5
    c: Coincident(g8,g6)
    c: Vertical(g8)
    c: Block(g6)
    c: Block(g7)
    c: Vertical(g9)
    c: Equal(g7,g9) = 0.5
    c: Block(g9)
    c: Coincident(g9,g7)
    c: Horizontal(g10)
    c: Coincident(g10,g9)
    c: Coincident(g11,g10)
    c: Coincident(g11,g8)
    c: Vertical(g11)
    c: Block(g11)
    c: Coincident(g12,g7)
    c: Vertical(g12)
    c: Coincident(g13,g3)
    c: Vertical(g13)
    c: Distance(g13) = 6.7
    c: Coincident(g14,g13)
    c: Horizontal(g14)
    c: Block(g14)
    c: Coincident(g15,g12)
    c: Coincident(g15,g14)
    c: Vertical(g15)
    c: Block(g15)
FEATURE [Sketcher::SketchObject] Sketch017
  FullyConstrained = true
  sketch-geometry (11):
    g0: LineSegment StartX=-3.5 StartY=1e-16 StartZ=0 EndX=-1.6 EndY=1e-16 EndZ=0
    g1: LineSegment StartX=-1.6 StartY=1e-16 StartZ=0 EndX=-1.6 EndY=1.5 EndZ=0
    g2: LineSegment StartX=-3.5 StartY=1.5 StartZ=0 EndX=-1.6 EndY=1.5 EndZ=0
    g3: LineSegment StartX=-3.5 StartY=1e-16 StartZ=0 EndX=-4.8 EndY=1e-16 EndZ=0
    g4: Circle CenterX=-3.5 CenterY=1.3 CenterZ=0 NormalX=0 NormalY=0 NormalZ=1 AngleXU=0 Radius=1
    g5: Circle CenterX=-3.5 CenterY=1e-16 CenterZ=0 NormalX=0 NormalY=0 NormalZ=1 AngleXU=0 Radius=1
    g6: Circle CenterX=-4.8 CenterY=1e-16 CenterZ=0 NormalX=0 NormalY=0 NormalZ=1 AngleXU=0 Radius=1
    g7: BSplineCurve PolesCount=3 KnotsCount=2 Degree=2 IsPeriodic=0
    g8: GeomPoint X=-3.5 Y=1.3 Z=0
    g9: GeomPoint X=-4.8 Y=1e-16 Z=0
    g10: LineSegment StartX=-3.5 StartY=1.3 StartZ=0 EndX=-3.5 EndY=1.5 EndZ=0
  constraints (24):
    c: Horizontal(g0)
    c: Distance(g0) = 1.9
    c: Block(g0)
    c: Coincident(g1,g0)
    c: Vertical(g1)
    c: Coincident(g2,g1)
    c: Horizontal(g2)
    c: Coincident(g3,g0)
    c: Horizontal(g3)
    c: Distance(g3) = 1.3
    c: Weight(g4) = 1
    c: Equal(g4,g5)
    c: Coincident(g5,g0)
    c: Equal(g4,g6)
    c: Coincident(g7,g3)
    c: InternalAlignment(g4,g7)
    c: InternalAlignment(g5,g7)
    c: InternalAlignment(g6,g7)
    c: InternalAlignment(g8,g7)
    c: InternalAlignment(g9,g7)
    c: Coincident(g10,g7)
    c: Coincident(g10,g2)
    c: Vertical(g10)
    c: Block(g10)
FEATURE [Part::Feature] Face035
  shape: bbox 3.2 x 1.5 x 2e-07 mm, 1 faces, 0 solids (baked)
FEATURE [Part::Revolution] Revolve039  label="backCaseScrewRetainer"
  Angle = 360
  Axis = (0,1,0)
  Base = (0,0,0)
  FaceMakerClass = Part::FaceMakerBullseye
  Placement = pos=(12.5,3,62) rot=(0,0,1;0rad)
  Solid = false
  Source = -> Face035
  Symmetric = false
FEATURE [Part::Feature] Face036
  shape: bbox 3.2 x 1.5 x 2e-07 mm, 1 faces, 0 solids (baked)
FEATURE [Part::Feature] Face039
  shape: bbox 4.8 x 30.2 x 2e-07 mm, 1 faces, 0 solids (baked)
FEATURE [Part::Revolution] Revolve043  label="frontCaseScrewPost002"
  Angle = 360
  Axis = (0,1,0)
  Base = (0,0,0)
  FaceMakerClass = Part::FaceMakerBullseye
  Placement = pos=(89.5,4.5,3.5) rot=(0,0,1;0rad)
  Solid = false
  Source = -> Face039
  Symmetric = false
FEATURE [Part::Feature] Face042
  shape: bbox 4.8 x 30.2 x 2e-07 mm, 1 faces, 0 solids (baked)
FEATURE [Part::Revolution] Revolve046  label="frontCaseScrewPost003"
  Angle = 360
  Axis = (0,1,0)
  Base = (0,0,0)
  FaceMakerClass = Part::FaceMakerBullseye
  Placement = pos=(89.5,4.5,68.5) rot=(0,0,1;0rad)
  Solid = false
  Source = -> Face042
  Symmetric = false
FEATURE [Part::Feature] Face043
  shape: bbox 3.2 x 1.5 x 2e-07 mm, 1 faces, 0 solids (baked)
FEATURE [Part::Revolution] Revolve047  label="frontCaseScrewRetainer002"
  Angle = 360
  Axis = (0,1,0)
  Base = (0,0,0)
  FaceMakerClass = Part::FaceMakerBullseye
  Placement = pos=(89.5,3,68.5) rot=(0,0,1;0rad)
  Solid = false
  Source = -> Face043
  Symmetric = false
FEATURE [Part::Feature] Face044
  shape: bbox 3.2 x 1.5 x 2e-07 mm, 1 faces, 0 solids (baked)
FEATURE [Part::Revolution] Revolve048  label="frontCaseScrewRetainer003"
  Angle = 360
  Axis = (0,1,0)
  Base = (0,0,0)
  FaceMakerClass = Part::FaceMakerBullseye
  Placement = pos=(89.5,3,3.5) rot=(0,0,1;0rad)
  Solid = false
  Source = -> Face044
  Symmetric = false
FEATURE [App::MeasureDistance] Distance002  label="Distance: 1.67 mm"
  Distance = 1.66921
  P1 = (99.2361,4.7524,71.7)
  P2 = (99.2347,6.42161,71.7)
FEATURE [Sketcher::SketchObject] Sketch018
  FullyConstrained = true
  sketch-geometry (7):
    g0: LineSegment StartX=0 StartY=0 StartZ=0 EndX=0 EndY=6 EndZ=0
    g1: Circle CenterX=0 CenterY=0 CenterZ=0 NormalX=0 NormalY=0 NormalZ=1 AngleXU=0 Radius=1
    g2: Circle CenterX=8 CenterY=6 CenterZ=0 NormalX=0 NormalY=0 NormalZ=1 AngleXU=0 Radius=1
    g3: BSplineCurve PolesCount=3 KnotsCount=2 Degree=2 IsPeriodic=0
    g4: GeomPoint X=0 Y=0 Z=0
    g5: GeomPoint X=8 Y=6 Z=0
    g6: LineSegment StartX=0 StartY=6 StartZ=0 EndX=8 EndY=6 EndZ=0
  constraints (14):
    c: Coincident(g0,g-1)
    c: Distance(g0) = 6
    c: Vertical(g0)
    c: Coincident(g3,g0)
    c: Weight(g1) = 1
    c: Equal(g1,g2)
    c: InternalAlignment(g1,g3)
    c: InternalAlignment(g2,g3)
    c: InternalAlignment(g4,g3)
    c: InternalAlignment(g5,g3)
    c: Block(g3)
    c: Coincident(g6,g0)
    c: Coincident(g6,g3)
    c: Horizontal(g6)
FEATURE [Part::Extrusion] Extrude012  label="caseScrewPillarBracket"
  Base = -> Sketch018
  Dir = (0,0,1)
  DirMode = 2
  FaceMakerClass = Part::FaceMakerBullseye
  LengthFwd = 2.4
  LengthRev = 0
  Placement = pos=(15.76,29,8.8) rot=(0,1,0;0rad)
  Solid = true
  Symmetric = false
FEATURE [Sketcher::SketchObject] Sketch019
  FullyConstrained = true
  sketch-geometry (7):
    g0: LineSegment StartX=0 StartY=0 StartZ=0 EndX=0 EndY=6 EndZ=0
    g1: Circle CenterX=0 CenterY=0 CenterZ=0 NormalX=0 NormalY=0 NormalZ=1 AngleXU=0 Radius=1
    g2: Circle CenterX=8 CenterY=6 CenterZ=0 NormalX=0 NormalY=0 NormalZ=1 AngleXU=0 Radius=1
    g3: BSplineCurve PolesCount=3 KnotsCount=2 Degree=2 IsPeriodic=0
    g4: GeomPoint X=0 Y=0 Z=0
    g5: GeomPoint X=8 Y=6 Z=0
    g6: LineSegment StartX=0 StartY=6 StartZ=0 EndX=8 EndY=6 EndZ=0
  constraints (14):
    c: Coincident(g0,g-1)
    c: Distance(g0) = 6
    c: Vertical(g0)
    c: Coincident(g3,g0)
    c: Weight(g1) = 1
    c: Equal(g1,g2)
    c: InternalAlignment(g1,g3)
    c: InternalAlignment(g2,g3)
    c: InternalAlignment(g4,g3)
    c: InternalAlignment(g5,g3)
    c: Block(g3)
    c: Coincident(g6,g0)
    c: Coincident(g6,g3)
    c: Horizontal(g6)
FEATURE [Part::Extrusion] Extrude013  label="caseScrewPillarBracket001"
  Base = -> Sketch019
  Dir = (0,0,1)
  DirMode = 2
  FaceMakerClass = Part::FaceMakerBullseye
  LengthFwd = 2.4
  LengthRev = 0
  Placement = pos=(15.76,29,60.8) rot=(0,0,1;0rad)
  Solid = true
  Symmetric = false
FEATURE [Sketcher::SketchObject] Sketch020
  FullyConstrained = true
  sketch-geometry (7):
    g0: LineSegment StartX=0 StartY=0 StartZ=0 EndX=0 EndY=6 EndZ=0
    g1: Circle CenterX=0 CenterY=0 CenterZ=0 NormalX=0 NormalY=0 NormalZ=1 AngleXU=0 Radius=1
    g2: Circle CenterX=8 CenterY=6 CenterZ=0 NormalX=0 NormalY=0 NormalZ=1 AngleXU=0 Radius=1
    g3: BSplineCurve PolesCount=3 KnotsCount=2 Degree=2 IsPeriodic=0
    g4: GeomPoint X=0 Y=0 Z=0
    g5: GeomPoint X=8 Y=6 Z=0
    g6: LineSegment StartX=0 StartY=6 StartZ=0 EndX=8 EndY=6 EndZ=0
  constraints (14):
    c: Coincident(g0,g-1)
    c: Distance(g0) = 6
    c: Vertical(g0)
    c: Coincident(g3,g0)
    c: Weight(g1) = 1
    c: Equal(g1,g2)
    c: InternalAlignment(g1,g3)
    c: InternalAlignment(g2,g3)
    c: InternalAlignment(g4,g3)
    c: InternalAlignment(g5,g3)
    c: Block(g3)
    c: Coincident(g6,g0)
    c: Coincident(g6,g3)
    c: Horizontal(g6)
FEATURE [Part::Extrusion] Extrude014  label="caseScrewPillarBracket002"
  Base = -> Sketch020
  Dir = (0,0,1)
  DirMode = 2
  FaceMakerClass = Part::FaceMakerBullseye
  LengthFwd = 2.4
  LengthRev = 0
  Placement = pos=(13.7,29,13.26) rot=(0,-1,0;1.5708rad)
  Solid = true
  Symmetric = false
FEATURE [Sketcher::SketchObject] Sketch021
  FullyConstrained = true
  sketch-geometry (7):
    g0: LineSegment StartX=0 StartY=0 StartZ=0 EndX=0 EndY=6 EndZ=0
    g1: Circle CenterX=0 CenterY=0 CenterZ=0 NormalX=0 NormalY=0 NormalZ=1 AngleXU=0 Radius=1
    g2: Circle CenterX=8 CenterY=6 CenterZ=0 NormalX=0 NormalY=0 NormalZ=1 AngleXU=0 Radius=1
    g3: BSplineCurve PolesCount=3 KnotsCount=2 Degree=2 IsPeriodic=0
    g4: GeomPoint X=0 Y=0 Z=0
    g5: GeomPoint X=8 Y=6 Z=0
    g6: LineSegment StartX=0 StartY=6 StartZ=0 EndX=8 EndY=6 EndZ=0
  constraints (14):
    c: Coincident(g0,g-1)
    c: Distance(g0) = 6
    c: Vertical(g0)
    c: Coincident(g3,g0)
    c: Weight(g1) = 1
    c: Equal(g1,g2)
    c: InternalAlignment(g1,g3)
    c: InternalAlignment(g2,g3)
    c: InternalAlignment(g4,g3)
    c: InternalAlignment(g5,g3)
    c: Block(g3)
    c: Coincident(g6,g0)
    c: Coincident(g6,g3)
    c: Horizontal(g6)
FEATURE [Part::Extrusion] Extrude015  label="caseScrewPillarBracket003"
  Base = -> Sketch021
  Dir = (0,0,1)
  DirMode = 2
  FaceMakerClass = Part::FaceMakerBullseye
  LengthFwd = 2.4
  LengthRev = 0
  Placement = pos=(11.3,29,58.74) rot=(0,1,0;1.5708rad)
  Solid = true
  Symmetric = false
FEATURE [Sketcher::SketchObject] Sketch022
  FullyConstrained = true
  sketch-geometry (7):
    g0: LineSegment StartX=0 StartY=0 StartZ=0 EndX=0 EndY=6 EndZ=0
    g1: Circle CenterX=0 CenterY=0 CenterZ=0 NormalX=0 NormalY=0 NormalZ=1 AngleXU=0 Radius=1
    g2: Circle CenterX=8 CenterY=6 CenterZ=0 NormalX=0 NormalY=0 NormalZ=1 AngleXU=0 Radius=1
    g3: BSplineCurve PolesCount=3 KnotsCount=2 Degree=2 IsPeriodic=0
    g4: GeomPoint X=0 Y=0 Z=0
    g5: GeomPoint X=8 Y=6 Z=0
    g6: LineSegment StartX=0 StartY=6 StartZ=0 EndX=8 EndY=6 EndZ=0
  constraints (14):
    c: Coincident(g0,g-1)
    c: Distance(g0) = 6
    c: Vertical(g0)
    c: Coincident(g3,g0)
    c: Weight(g1) = 1
    c: Equal(g1,g2)
    c: InternalAlignment(g1,g3)
    c: InternalAlignment(g2,g3)
    c: InternalAlignment(g4,g3)
    c: InternalAlignment(g5,g3)
    c: Block(g3)
    c: Coincident(g6,g0)
    c: Coincident(g6,g3)
    c: Horizontal(g6)
FEATURE [Part::Extrusion] Extrude016  label="caseScrewPillarBracket004"
  Base = -> Sketch022
  Dir = (0,0,1)
  DirMode = 2
  FaceMakerClass = Part::FaceMakerBullseye
  LengthFwd = 2.4
  LengthRev = 0
  Placement = pos=(88.3,29,65.23) rot=(0,1,0;1.5708rad)
  Solid = true
  Symmetric = false
FEATURE [Sketcher::SketchObject] Sketch023
  FullyConstrained = true
  sketch-geometry (7):
    g0: LineSegment StartX=0 StartY=0 StartZ=0 EndX=0 EndY=6 EndZ=0
    g1: Circle CenterX=0 CenterY=0 CenterZ=0 NormalX=0 NormalY=0 NormalZ=1 AngleXU=0 Radius=1
    g2: Circle CenterX=8 CenterY=6 CenterZ=0 NormalX=0 NormalY=0 NormalZ=1 AngleXU=0 Radius=1
    g3: BSplineCurve PolesCount=3 KnotsCount=2 Degree=2 IsPeriodic=0
    g4: GeomPoint X=0 Y=0 Z=0
    g5: GeomPoint X=8 Y=6 Z=0
    g6: LineSegment StartX=0 StartY=6 StartZ=0 EndX=8 EndY=6 EndZ=0
  constraints (14):
    c: Coincident(g0,g-1)
    c: Distance(g0) = 6
    c: Vertical(g0)
    c: Coincident(g3,g0)
    c: Weight(g1) = 1
    c: Equal(g1,g2)
    c: InternalAlignment(g1,g3)
    c: InternalAlignment(g2,g3)
    c: InternalAlignment(g4,g3)
    c: InternalAlignment(g5,g3)
    c: Block(g3)
    c: Coincident(g6,g0)
    c: Coincident(g6,g3)
    c: Horizontal(g6)
FEATURE [Part::Extrusion] Extrude017  label="caseScrewPillarBracket005"
  Base = -> Sketch023
  Dir = (0,0,1)
  DirMode = 2
  FaceMakerClass = Part::FaceMakerBullseye
  LengthFwd = 2.4
  LengthRev = 0
  Placement = pos=(90.7,29,6.77) rot=(0,-1,0;1.5708rad)
  Solid = true
  Symmetric = false
FEATURE [Sketcher::SketchObject] Sketch024
  FullyConstrained = true
  sketch-geometry (7):
    g0: LineSegment StartX=0 StartY=0 StartZ=0 EndX=0 EndY=6 EndZ=0
    g1: Circle CenterX=0 CenterY=0 CenterZ=0 NormalX=0 NormalY=0 NormalZ=1 AngleXU=0 Radius=1
    g2: Circle CenterX=8 CenterY=6 CenterZ=0 NormalX=0 NormalY=0 NormalZ=1 AngleXU=0 Radius=1
    g3: BSplineCurve PolesCount=3 KnotsCount=2 Degree=2 IsPeriodic=0
    g4: GeomPoint X=0 Y=0 Z=0
    g5: GeomPoint X=8 Y=6 Z=0
    g6: LineSegment StartX=0 StartY=6 StartZ=0 EndX=8 EndY=6 EndZ=0
  constraints (14):
    c: Coincident(g0,g-1)
    c: Distance(g0) = 6
    c: Vertical(g0)
    c: Coincident(g3,g0)
    c: Weight(g1) = 1
    c: Equal(g1,g2)
    c: InternalAlignment(g1,g3)
    c: InternalAlignment(g2,g3)
    c: InternalAlignment(g4,g3)
    c: InternalAlignment(g5,g3)
    c: Block(g3)
    c: Coincident(g6,g0)
    c: Coincident(g6,g3)
    c: Horizontal(g6)
FEATURE [Part::Extrusion] Extrude018  label="caseScrewPillarBracket006"
  Base = -> Sketch024
  Dir = (0,0,1)
  DirMode = 2
  FaceMakerClass = Part::FaceMakerBullseye
  LengthFwd = 2.4
  LengthRev = 0
  Placement = pos=(103.7,29,6.77) rot=(0,-1,0;1.5708rad)
  Solid = true
  Symmetric = false
FEATURE [Sketcher::SketchObject] Sketch025
  FullyConstrained = true
  sketch-geometry (7):
    g0: LineSegment StartX=0 StartY=0 StartZ=0 EndX=0 EndY=6 EndZ=0
    g1: Circle CenterX=0 CenterY=0 CenterZ=0 NormalX=0 NormalY=0 NormalZ=1 AngleXU=0 Radius=1
    g2: Circle CenterX=8 CenterY=6 CenterZ=0 NormalX=0 NormalY=0 NormalZ=1 AngleXU=0 Radius=1
    g3: BSplineCurve PolesCount=3 KnotsCount=2 Degree=2 IsPeriodic=0
    g4: GeomPoint X=0 Y=0 Z=0
    g5: GeomPoint X=8 Y=6 Z=0
    g6: LineSegment StartX=0 StartY=6 StartZ=0 EndX=8 EndY=6 EndZ=0
  constraints (14):
    c: Coincident(g0,g-1)
    c: Distance(g0) = 6
    c: Vertical(g0)
    c: Coincident(g3,g0)
    c: Weight(g1) = 1
    c: Equal(g1,g2)
    c: InternalAlignment(g1,g3)
    c: InternalAlignment(g2,g3)
    c: InternalAlignment(g4,g3)
    c: InternalAlignment(g5,g3)
    c: Block(g3)
    c: Coincident(g6,g0)
    c: Coincident(g6,g3)
    c: Horizontal(g6)
FEATURE [Part::Extrusion] Extrude019  label="caseScrewPillarBracket007"
  Base = -> Sketch025
  Dir = (0,0,1)
  DirMode = 2
  FaceMakerClass = Part::FaceMakerBullseye
  LengthFwd = 2.4
  LengthRev = 0
  Placement = pos=(101.3,29,65.23) rot=(0,1,0;1.5708rad)
  Solid = true
  Symmetric = false
FEATURE [Part::Box] Box011  label="frontCaseScrewPillarBracket"
  AttacherType = Attacher::AttachEngine3D
  Height = 2.4
  Length = 16
  Placement = pos=(87,28,2.3) rot=(0,0,1;0rad)
  Width = 7
FEATURE [Part::Box] Box012  label="frontCaseScrewPillarBracket001"
  AttacherType = Attacher::AttachEngine3D
  Height = 2.4
  Length = 16
  Placement = pos=(87,28,67.3) rot=(0,0,1;0rad)
  Width = 7
FEATURE [Sketcher::SketchObject] Sketch026
  FullyConstrained = true
  sketch-geometry (17):
    g0: Circle CenterX=-3.5 CenterY=23.5 CenterZ=0 NormalX=0 NormalY=0 NormalZ=1 AngleXU=0 Radius=1
    g1: Circle CenterX=-1 CenterY=15.25 CenterZ=0 NormalX=0 NormalY=0 NormalZ=1 AngleXU=0 Radius=1
    g2: Circle CenterX=-3.5 CenterY=7 CenterZ=0 NormalX=0 NormalY=0 NormalZ=1 AngleXU=0 Radius=1
    g3: BSplineCurve PolesCount=3 KnotsCount=2 Degree=2 IsPeriodic=0
    g4: GeomPoint X=-3.5 Y=23.5 Z=0
    g5: GeomPoint X=-3.5 Y=7 Z=0
    g6: Circle CenterX=-4.8 CenterY=30.5 CenterZ=0 NormalX=0 NormalY=0 NormalZ=1 AngleXU=0 Radius=1
    g7: Circle CenterX=-3.5 CenterY=30.5 CenterZ=0 NormalX=0 NormalY=0 NormalZ=1 AngleXU=0 Radius=1
    g8: Circle CenterX=-3.5 CenterY=29.2 CenterZ=0 NormalX=0 NormalY=0 NormalZ=1 AngleXU=0 Radius=1
    g9: BSplineCurve PolesCount=3 KnotsCount=2 Degree=2 IsPeriodic=0
    g10: GeomPoint X=-4.8 Y=30.5 Z=0
    g11: GeomPoint X=-3.5 Y=29.2 Z=0
    g12: LineSegment StartX=-3.5 StartY=29.2 StartZ=0 EndX=-3.5 EndY=23.5 EndZ=0
    g13: LineSegment StartX=-4.8 StartY=30.5 StartZ=0 EndX=0 EndY=30.5 EndZ=0
    g14: LineSegment StartX=-3.5 StartY=5 StartZ=0 EndX=-3.5 EndY=7 EndZ=0
    g15: LineSegment StartX=0 StartY=5 StartZ=0 EndX=0 EndY=30.5 EndZ=0
    g16: LineSegment StartX=-3.5 StartY=5 StartZ=0 EndX=0 EndY=5 EndZ=0
  constraints (33):
    c: Weight(g0) = 1
    c: Equal(g0,g1)
    c: Equal(g0,g2)
    c: InternalAlignment(g0,g3)
    c: InternalAlignment(g1,g3)
    c: InternalAlignment(g2,g3)
    c: InternalAlignment(g4,g3)
    c: InternalAlignment(g5,g3)
    c: Block(g3)
    c: Weight(g6) = 1
    c: Equal(g6,g7)
    c: Equal(g6,g8)
    c: InternalAlignment(g6,g9)
    c: InternalAlignment(g7,g9)
    c: InternalAlignment(g8,g9)
    c: InternalAlignment(g10,g9)
    c: InternalAlignment(g11,g9)
    c: Block(g9)
    c: Coincident(g12,g9)
    c: Coincident(g12,g3)
    c: Vertical(g12)
    c: Coincident(g13,g9)
    c: Horizontal(g13)
    c: Distance(g13) = 4.8
    c: Coincident(g14,g3)
    c: Vertical(g14)
    c: Coincident(g15,g13)
    c: Vertical(g15)
    c: Tangent(g15,g1)
    c: Distance(g14) = 2
    c: Coincident(g16,g14)
    c: Horizontal(g16)
    c: Coincident(g15,g16)
FEATURE [Part::Feature] Face050
  shape: bbox 4.8 x 25.5 x 2e-07 mm, 1 faces, 0 solids (baked)
FEATURE [Part::Revolution] Revolve054  label="moreFrontCaseScrewPost001"
  Angle = 360
  Axis = (0,1,0)
  Base = (0,0,0)
  FaceMakerClass = Part::FaceMakerBullseye
  Placement = pos=(102.5,4.5,3.5) rot=(0,0,1;0rad)
  Solid = false
  Source = -> Face050
  Symmetric = false
FEATURE [Part::Feature] Face051
  shape: bbox 4.8 x 25.5 x 2e-07 mm, 1 faces, 0 solids (baked)
FEATURE [Part::Revolution] Revolve055  label="moreFrontCaseScrewPost002"
  Angle = 360
  Axis = (0,1,0)
  Base = (0,0,0)
  FaceMakerClass = Part::FaceMakerBullseye
  Placement = pos=(102.5,4.5,68.5) rot=(0,0,1;0rad)
  Solid = false
  Source = -> Face051
  Symmetric = false
FEATURE [Sketcher::SketchObject] Sketch027
  FullyConstrained = true
  sketch-geometry (10):
    g0: LineSegment StartX=-1.6 StartY=4.7 StartZ=0 EndX=-1.6 EndY=1.7 EndZ=0
    g1: LineSegment StartX=-3.5 StartY=4.7 StartZ=0 EndX=-1.6 EndY=4.7 EndZ=0
    g2: LineSegment StartX=-1.6 StartY=1.7 StartZ=0 EndX=-1.6 EndY=1.5 EndZ=0
    g3: LineSegment StartX=-1.6 StartY=1.5 StartZ=0 EndX=-5.2 EndY=1.5 EndZ=0
    g4: Circle CenterX=-3.5 CenterY=4.7 CenterZ=0 NormalX=0 NormalY=0 NormalZ=1 AngleXU=0 Radius=1
    g5: Circle CenterX=-3.59627 CenterY=2.99743 CenterZ=0 NormalX=0 NormalY=0 NormalZ=1 AngleXU=0 Radius=1
    g6: Circle CenterX=-5.2 CenterY=1.5 CenterZ=0 NormalX=0 NormalY=0 NormalZ=1 AngleXU=0 Radius=1
    g7: BSplineCurve PolesCount=3 KnotsCount=2 Degree=2 IsPeriodic=0
    g8: GeomPoint X=-3.5 Y=4.7 Z=0
    g9: GeomPoint X=-5.2 Y=1.5 Z=0
  constraints (23):
    c: Vertical(g0)
    c: Distance(g0) = 3
    c: Coincident(g1,g0)
    c: Horizontal(g1)
    c: Block(g0)
    c: Block(g1)
    c: Coincident(g2,g0)
    c: Vertical(g2)
    c: Distance(g2) = 0.2
    c: Coincident(g3,g2)
    c: Horizontal(g3)
    c: Block(g3)
    c: Coincident(g7,g1)
    c: Weight(g4) = 1
    c: Equal(g4,g5)
    c: Equal(g4,g6)
    c: Coincident(g7,g3)
    c: InternalAlignment(g4,g7)
    c: InternalAlignment(g5,g7)
    c: InternalAlignment(g6,g7)
    c: InternalAlignment(g8,g7)
    c: InternalAlignment(g9,g7)
    c: Block(g7)
FEATURE [Sketcher::SketchObject] Sketch028
  FullyConstrained = true
  sketch-geometry (18):
    g0: LineSegment StartX=0 StartY=3e-16 StartZ=0 EndX=0 EndY=1.7 EndZ=0
    g1: LineSegment StartX=-3.5 StartY=0 StartZ=0 EndX=-3.5 EndY=0.9 EndZ=0
    g2: Circle CenterX=-2.7 CenterY=1.7 CenterZ=0 NormalX=0 NormalY=0 NormalZ=1 AngleXU=0 Radius=1
    g3: Circle CenterX=-3.5 CenterY=1.7 CenterZ=0 NormalX=0 NormalY=0 NormalZ=1 AngleXU=0 Radius=1
    g4: Circle CenterX=-3.5 CenterY=0.9 CenterZ=0 NormalX=0 NormalY=0 NormalZ=1 AngleXU=0 Radius=1
    g5: BSplineCurve PolesCount=3 KnotsCount=2 Degree=2 IsPeriodic=0
    g6: GeomPoint X=-2.7 Y=1.7 Z=0
    g7: GeomPoint X=-3.5 Y=0.9 Z=0
    g8: LineSegment StartX=-3.5 StartY=0 StartZ=0 EndX=-3.5 EndY=-7 EndZ=0
    g9: LineSegment StartX=0 StartY=3e-16 StartZ=0 EndX=0 EndY=-7 EndZ=0
    g10: LineSegment StartX=-3.5 StartY=-7 StartZ=0 EndX=0 EndY=-7 EndZ=0
    g11: LineSegment StartX=-2.7 StartY=1.7 StartZ=0 EndX=-1.6 EndY=1.7 EndZ=0
    g12: LineSegment StartX=0 StartY=1.7 StartZ=0 EndX=0 EndY=4.5 EndZ=0
    g13: LineSegment StartX=0 StartY=4.5 StartZ=0 EndX=0 EndY=10.8 EndZ=0
    g14: LineSegment StartX=0 StartY=10.8 StartZ=0 EndX=-2 EndY=10.8 EndZ=0
    g15: LineSegment StartX=-1.6 StartY=4.7 StartZ=0 EndX=-1.6 EndY=1.7 EndZ=0
    g16: LineSegment StartX=-1.6 StartY=4.7 StartZ=0 EndX=-2 EndY=4.7 EndZ=0
    g17: LineSegment StartX=-2 StartY=4.7 StartZ=0 EndX=-2 EndY=10.8 EndZ=0
  constraints (44):
    c: Vertical(g0)
    c: Vertical(g1)
    c: Distance(g1) = 0.9
    c: Block(g0)
    c: Distance(g0) = 1.7
    c: Weight(g2) = 1
    c: Equal(g2,g3)
    c: Equal(g2,g4)
    c: Coincident(g5,g1)
    c: InternalAlignment(g2,g5)
    c: InternalAlignment(g3,g5)
    c: InternalAlignment(g4,g5)
    c: InternalAlignment(g6,g5)
    c: InternalAlignment(g7,g5)
    c: Block(g5)
    c: Coincident(g8,g1)
    c: Vertical(g8)
    c: Distance(g8) = 7
    c: Vertical(g9)
    c: Equal(g8,g9) = 7
    c: Coincident(g9,g0)
    c: Coincident(g10,g8)
    c: Coincident(g10,g9)
    c: Horizontal(g10)
    c: Coincident(g11,g5)
    c: Horizontal(g11)
    c: Coincident(g12,g0)
    c: Vertical(g12)
    c: Distance(g12) = 2.8
    c: Coincident(g13,g12)
    c: Vertical(g13)
    c: Distance(g13) = 6.3
    c: Coincident(g14,g13)
    c: Horizontal(g14)
    c: Distance(g14) = 2
    c: Vertical(g15)
    c: Distance(g15) = 3
    c: Block(g11)
    c: Coincident(g15,g11)
    c: Coincident(g16,g15)
    c: Horizontal(g16)
    c: Coincident(g17,g16)
    c: Coincident(g17,g14)
    c: Vertical(g17)
FEATURE [Part::Revolution] Revolve040  label="backCaseScrewRetainer001"
  Angle = 360
  Axis = (0,1,0)
  Base = (0,0,0)
  FaceMakerClass = Part::FaceMakerBullseye
  Placement = pos=(12.5,3,10) rot=(0,0,1;0rad)
  Solid = false
  Source = -> Face036
  Symmetric = false
FEATURE [Part::Feature] Face055
  shape: bbox 3.5 x 30.2 x 2e-07 mm, 1 faces, 0 solids (baked)
FEATURE [Part::Revolution] Revolve059  label="backCaseScrewPost"
  Angle = 360
  Axis = (0,1,0)
  Base = (0,0,0)
  FaceMakerClass = Part::FaceMakerBullseye
  Placement = pos=(12.5,4.5,10) rot=(0,0,1;0rad)
  Solid = false
  Source = -> Face055
  Symmetric = false
FEATURE [Part::Feature] Face056
  shape: bbox 3.5 x 30.2 x 2e-07 mm, 1 faces, 0 solids (baked)
FEATURE [Part::Revolution] Revolve060  label="backCaseScrewPost001"
  Angle = 360
  Axis = (0,1,0)
  Base = (0,0,0)
  FaceMakerClass = Part::FaceMakerBullseye
  Placement = pos=(12.5,4.5,62) rot=(0,0,1;0rad)
  Solid = false
  Source = -> Face056
  Symmetric = false
FEATURE [Part::Feature] Face057
  shape: bbox 3.5 x 17.8 x 2e-07 mm, 1 faces, 0 solids (baked)
FEATURE [Part::Revolution] Revolve061  label="removeToCreateScrewAndThreadedInsertHole"
  Angle = 360
  Axis = (0,1,0)
  Base = (0,0,0)
  FaceMakerClass = Part::FaceMakerBullseye
  Placement = pos=(12.5,0,10) rot=(0,0,1;0rad)
  Solid = false
  Source = -> Face057
  Symmetric = false
FEATURE [Part::Feature] Face058
  shape: bbox 3.5 x 17.8 x 2e-07 mm, 1 faces, 0 solids (baked)
FEATURE [Part::Revolution] Revolve062  label="removeToCreateScrewAndThreadedInsertHole001"
  Angle = 360
  Axis = (0,1,0)
  Base = (0,0,0)
  FaceMakerClass = Part::FaceMakerBullseye
  Placement = pos=(12.5,0,62) rot=(0,0,1;0rad)
  Solid = false
  Source = -> Face058
  Symmetric = false
FEATURE [Part::Feature] Face059
  shape: bbox 3.5 x 17.8 x 2e-07 mm, 1 faces, 0 solids (baked)
FEATURE [Part::Revolution] Revolve063  label="removeToCreateScrewAndThreadedInsertHole002"
  Angle = 360
  Axis = (0,1,0)
  Base = (0,0,0)
  FaceMakerClass = Part::FaceMakerBullseye
  Placement = pos=(89.5,0,68.5) rot=(0,0,1;0rad)
  Solid = false
  Source = -> Face059
  Symmetric = false
FEATURE [Part::Feature] Face060
  shape: bbox 3.5 x 17.8 x 2e-07 mm, 1 faces, 0 solids (baked)
FEATURE [Part::Revolution] Revolve064  label="removeToCreateScrewAndThreadedInsertHole003"
  Angle = 360
  Axis = (0,1,0)
  Base = (0,0,0)
  FaceMakerClass = Part::FaceMakerBullseye
  Placement = pos=(89.5,0,3.5) rot=(0,0,1;0rad)
  Solid = false
  Source = -> Face060
  Symmetric = false
FEATURE [Part::Feature] Face061
  shape: bbox 3.5 x 17.8 x 2e-07 mm, 1 faces, 0 solids (baked)
FEATURE [Part::Revolution] Revolve065  label="removeToCreateScrewAndThreadedInsertHole004"
  Angle = 360
  Axis = (0,1,0)
  Base = (0,0,0)
  FaceMakerClass = Part::FaceMakerBullseye
  Placement = pos=(102.5,4.7,3.5) rot=(0,0,1;0rad)
  Solid = false
  Source = -> Face061
  Symmetric = false
FEATURE [Part::Feature] Face062
  shape: bbox 3.5 x 17.8 x 2e-07 mm, 1 faces, 0 solids (baked)
FEATURE [Part::Revolution] Revolve066  label="removeToCreateScrewAndThreadedInsertHole005"
  Angle = 360
  Axis = (0,1,0)
  Base = (0,0,0)
  FaceMakerClass = Part::FaceMakerBullseye
  Placement = pos=(102.5,4.7,68.5) rot=(0,0,1;0rad)
  Solid = false
  Source = -> Face062
  Symmetric = false
FEATURE [Part::MultiFuse] Fusion047  label="makeHoles"
  Shapes = -> [Revolve066,Revolve065,Revolve064,Revolve063,Revolve062,Revolve061]
FEATURE [Part::Feature] Face063
  shape: bbox 3.6 x 3.2 x 2e-07 mm, 1 faces, 0 solids (baked)
FEATURE [Part::Revolution] Revolve067  label="moreFrontCaseScrewRetainer002"
  Angle = 360
  Axis = (0,1,0)
  Base = (0,0,0)
  FaceMakerClass = Part::FaceMakerBullseye
  Placement = pos=(102.5,4.5,68.5) rot=(0,0,1;0rad)
  Solid = false
  Source = -> Face063
  Symmetric = false
FEATURE [Part::Feature] Face064
  shape: bbox 3.6 x 3.2 x 2e-07 mm, 1 faces, 0 solids (baked)
FEATURE [Part::Revolution] Revolve068  label="moreFrontCaseScrewRetainer003"
  Angle = 360
  Axis = (0,1,0)
  Base = (0,0,0)
  FaceMakerClass = Part::FaceMakerBullseye
  Placement = pos=(102.5,4.5,3.5) rot=(0,0,1;0rad)
  Solid = false
  Source = -> Face064
  Symmetric = false
FEATURE [Part::Feature] Face065
  shape: bbox 3.5 x 17.8 x 2e-07 mm, 1 faces, 0 solids (baked)
FEATURE [Part::Revolution] Revolve069  label="removeToCreateScrewAndThreadedInsertHole006"
  Angle = 360
  Axis = (0,1,0)
  Base = (0,0,0)
  FaceMakerClass = Part::FaceMakerBullseye
  Placement = pos=(12.5,0,10) rot=(0,0,1;0rad)
  Solid = false
  Source = -> Face065
  Symmetric = false
FEATURE [Part::Feature] Face066
  shape: bbox 3.5 x 17.8 x 2e-07 mm, 1 faces, 0 solids (baked)
FEATURE [Part::Revolution] Revolve070  label="removeToCreateScrewAndThreadedInsertHole007"
  Angle = 360
  Axis = (0,1,0)
  Base = (0,0,0)
  FaceMakerClass = Part::FaceMakerBullseye
  Placement = pos=(12.5,0,62) rot=(0,0,1;0rad)
  Solid = false
  Source = -> Face066
  Symmetric = false
FEATURE [Part::Feature] Face067
  shape: bbox 3.5 x 17.8 x 2e-07 mm, 1 faces, 0 solids (baked)
FEATURE [Part::Revolution] Revolve071  label="removeToCreateScrewAndThreadedInsertHole008"
  Angle = 360
  Axis = (0,1,0)
  Base = (0,0,0)
  FaceMakerClass = Part::FaceMakerBullseye
  Placement = pos=(89.5,0,68.5) rot=(0,0,1;0rad)
  Solid = false
  Source = -> Face067
  Symmetric = false
FEATURE [Part::Feature] Face068
  shape: bbox 3.5 x 17.8 x 2e-07 mm, 1 faces, 0 solids (baked)
FEATURE [Part::Revolution] Revolve072  label="removeToCreateScrewAndThreadedInsertHole009"
  Angle = 360
  Axis = (0,1,0)
  Base = (0,0,0)
  FaceMakerClass = Part::FaceMakerBullseye
  Placement = pos=(89.5,0,3.5) rot=(0,0,1;0rad)
  Solid = false
  Source = -> Face068
  Symmetric = false
FEATURE [Part::Feature] Face069
  shape: bbox 3.5 x 17.8 x 2e-07 mm, 1 faces, 0 solids (baked)
FEATURE [Part::Feature] Face070
  shape: bbox 3.5 x 17.8 x 2e-07 mm, 1 faces, 0 solids (baked)
FEATURE [Part::Revolution] Revolve073  label="removeToCreateScrewAndThreadedInsertHole010"
  Angle = 360
  Axis = (0,1,0)
  Base = (0,0,0)
  FaceMakerClass = Part::FaceMakerBullseye
  Placement = pos=(102.5,4.7,3.5) rot=(0,0,1;0rad)
  Solid = false
  Source = -> Face069
  Symmetric = false
FEATURE [Part::Revolution] Revolve074  label="removeToCreateScrewAndThreadedInsertHole011"
  Angle = 360
  Axis = (0,1,0)
  Base = (0,0,0)
  FaceMakerClass = Part::FaceMakerBullseye
  Placement = pos=(102.5,4.7,68.5) rot=(0,0,1;0rad)
  Solid = false
  Source = -> Face070
  Symmetric = false
FEATURE [Part::MultiFuse] Fusion048  label="makeHoles001"
  Shapes = -> [Revolve074,Revolve073,Revolve072,Revolve071,Revolve070,Revolve069]
FEATURE [Part::MultiFuse] Fusion049  label="caseScrewRetainers"
  Shapes = -> [Revolve067,Revolve068,Revolve048,Revolve047,Revolve039,Revolve040]
FEATURE [Part::Cut] Cut015  label="caseScrewRetainers001"
  Base = -> Fusion049
  Tool = -> Fusion048
FEATURE [Part::MultiFuse] Fusion050  label="casePillars"
  Shapes = -> [Revolve055,Revolve054,Revolve043,Revolve046,Revolve059,Revolve060]
FEATURE [Part::Feature] Face071 .. Face076  x6 (patterned run collapsed; names and placements below)
  shape: bbox 3.5 x 17.8 x 2e-07 mm, 1 faces, 0 solids (baked)
FEATURE [Part::Revolution] Revolve075  label="removeToCreateScrewAndThreadedInsertHole012"
  Angle = 360
  Axis = (0,1,0)
  Base = (0,0,0)
  FaceMakerClass = Part::FaceMakerBullseye
  Placement = pos=(12.5,0,10) rot=(0,0,1;0rad)
  Solid = false
  Source = -> Face071
  Symmetric = false
FEATURE [Part::Revolution] Revolve076  label="removeToCreateScrewAndThreadedInsertHole013"
  Angle = 360
  Axis = (0,1,0)
  Base = (0,0,0)
  FaceMakerClass = Part::FaceMakerBullseye
  Placement = pos=(12.5,0,62) rot=(0,0,1;0rad)
  Solid = false
  Source = -> Face072
  Symmetric = false
FEATURE [Part::Revolution] Revolve077  label="removeToCreateScrewAndThreadedInsertHole014"
  Angle = 360
  Axis = (0,1,0)
  Base = (0,0,0)
  FaceMakerClass = Part::FaceMakerBullseye
  Placement = pos=(89.5,0,68.5) rot=(0,0,1;0rad)
  Solid = false
  Source = -> Face073
  Symmetric = false
FEATURE [Part::Revolution] Revolve078  label="removeToCreateScrewAndThreadedInsertHole015"
  Angle = 360
  Axis = (0,1,0)
  Base = (0,0,0)
  FaceMakerClass = Part::FaceMakerBullseye
  Placement = pos=(89.5,0,3.5) rot=(0,0,1;0rad)
  Solid = false
  Source = -> Face074
  Symmetric = false
FEATURE [Part::Revolution] Revolve079  label="removeToCreateScrewAndThreadedInsertHole016"
  Angle = 360
  Axis = (0,1,0)
  Base = (0,0,0)
  FaceMakerClass = Part::FaceMakerBullseye
  Placement = pos=(102.5,4.7,3.5) rot=(0,0,1;0rad)
  Solid = false
  Source = -> Face075
  Symmetric = false
FEATURE [Part::Revolution] Revolve080  label="removeToCreateScrewAndThreadedInsertHole017"
  Angle = 360
  Axis = (0,1,0)
  Base = (0,0,0)
  FaceMakerClass = Part::FaceMakerBullseye
  Placement = pos=(102.5,4.7,68.5) rot=(0,0,1;0rad)
  Solid = false
  Source = -> Face076
  Symmetric = false
FEATURE [Part::MultiFuse] Fusion051  label="makeHoles002"
  Shapes = -> [Revolve080,Revolve079,Revolve078,Revolve077,Revolve076,Revolve075]
FEATURE [Part::Cut] Cut016  label="caesPillars"
  Base = -> Fusion050
  Tool = -> Fusion051
FEATURE [Part::Revolution] Revolve009  label="plugHousing016"
  Angle = 360
  Axis = (0,1,0)
  Base = (0,0,0)
  FaceMakerClass = Part::FaceMakerBullseye
  Placement = pos=(0,0,36.15) rot=(0,0,1;0rad)
  Solid = false
  Source = -> Face012
  Symmetric = false
FEATURE [Part::MultiFuse] Fusion014  label="plugHousing023"
  Placement = pos=(0,0,0) rot=(0,0,1;1.5708rad)
  Shapes = -> [Revolve011,Revolve009]
FEATURE [Part::Revolution] Revolve010  label="plugHousing017"
  Angle = 360
  Axis = (0,1,0)
  Base = (0,0,0)
  FaceMakerClass = Part::FaceMakerBullseye
  Placement = pos=(0,0,36.15) rot=(0,0,1;0rad)
  Solid = false
  Source = -> Face014
  Symmetric = false
FEATURE [Part::MultiFuse] Fusion015  label="plugHousing024"
  Placement = pos=(0,0,0) rot=(0,0,1;1.5708rad)
  Shapes = -> [Revolve010,Revolve015]
FEATURE [Part::Revolution] Revolve014  label="plugHousing026"
  Angle = 360
  Axis = (0,1,0)
  Base = (0,0,0)
  FaceMakerClass = Part::FaceMakerBullseye
  Placement = pos=(0,0,36.15) rot=(0,0,1;0rad)
  Solid = false
  Source = -> Face011
  Symmetric = false
FEATURE [Part::Revolution] Revolve013  label="plugHousing025"
  Angle = 360
  Axis = (0,1,0)
  Base = (0,0,0)
  FaceMakerClass = Part::FaceMakerBullseye
  Placement = pos=(0,0,36.15) rot=(0,0,1;0rad)
  Solid = false
  Source = -> Face015
  Symmetric = false
FEATURE [Part::MultiFuse] Fusion016  label="plugHousing028"
  Placement = pos=(0,19,0) rot=(0,0,1;3.14159rad)
  Shapes = -> [Fusion014,Fusion013]
FEATURE [Part::MultiFuse] Fusion011  label="plugHousing018"
  Placement = pos=(0,0,0) rot=(0,0,1;1.5708rad)
  Shapes = -> [Revolve014,Revolve013]
FEATURE [Part::MultiFuse] Fusion012  label="plugHousing019"
  Placement = pos=(0,19,0) rot=(0,0,1;3.14159rad)
  Shapes = -> [Fusion011,Fusion015]
FEATURE [Part::MultiFuse] Fusion017  label="plugHousing029"
  Placement = pos=(122.621,0,-0.15) rot=(0,0,1;0rad)
  Shapes = -> [Fusion016,Fusion012]
FEATURE [Part::MultiFuse] Fusion052  label="casePillarRetainers"
  Shapes = -> [Extrude012,Extrude013,Extrude014,Extrude015,Extrude016,Extrude017,Extrude018,Extrude019,Box011,Box012]
FEATURE [Part::Feature] Face077
  shape: bbox 3.5 x 17.8 x 2e-07 mm, 1 faces, 0 solids (baked)
FEATURE [Part::Revolution] Revolve081  label="removeToCreateScrewAndThreadedInsertHole018"
  Angle = 360
  Axis = (0,1,0)
  Base = (0,0,0)
  FaceMakerClass = Part::FaceMakerBullseye
  Placement = pos=(62.3,30.3,19.7) rot=(0,0,1;0rad)
  Solid = false
  Source = -> Face077
  Symmetric = false
FEATURE [Part::Feature] Face078
  shape: bbox 3.5 x 17.8 x 2e-07 mm, 1 faces, 0 solids (baked)
FEATURE [Part::Revolution] Revolve082  label="removeToCreateScrewAndThreadedInsertHole019"
  Angle = 360
  Axis = (0,1,0)
  Base = (0,0,0)
  FaceMakerClass = Part::FaceMakerBullseye
  Placement = pos=(62.3,30.3,51.7) rot=(0,0,1;0rad)
  Solid = false
  Source = -> Face078
  Symmetric = false
FEATURE [Part::Feature] Face079
  shape: bbox 3.5 x 17.8 x 2e-07 mm, 1 faces, 0 solids (baked)
FEATURE [Part::Revolution] Revolve083  label="removeToCreateScrewAndThreadedInsertHole020"
  Angle = 360
  Axis = (0,1,0)
  Base = (0,0,0)
  FaceMakerClass = Part::FaceMakerBullseye
  Placement = pos=(30.3,30.3,19.7) rot=(0,0,1;0rad)
  Solid = false
  Source = -> Face079
  Symmetric = false
FEATURE [Part::Feature] Face080
  shape: bbox 3.5 x 17.8 x 2e-07 mm, 1 faces, 0 solids (baked)
FEATURE [Part::Revolution] Revolve084  label="removeToCreateScrewAndThreadedInsertHole021"
  Angle = 360
  Axis = (0,1,0)
  Base = (0,0,0)
  FaceMakerClass = Part::FaceMakerBullseye
  Placement = pos=(30.3,30.3,51.7) rot=(0,0,1;0rad)
  Solid = false
  Source = -> Face080
  Symmetric = false
FEATURE [Part::MultiFuse] Fusion053  label="createThreadedInsertHolesForFan"
  Shapes = -> [Revolve081,Revolve082,Revolve083,Revolve084]
FEATURE [Part::Cut] Cut017  label="fanScrewHousing001"
  Base = -> Fusion046
  Tool = -> Fusion053
FEATURE [Part::Feature] Face081
  shape: bbox 3.5 x 17.8 x 2e-07 mm, 1 faces, 0 solids (baked)
FEATURE [Part::Revolution] Revolve085  label="removeToCreateScrewAndThreadedInsertHole022"
  Angle = 360
  Axis = (0,1,0)
  Base = (0,0,0)
  FaceMakerClass = Part::FaceMakerBullseye
  Placement = pos=(62.3,30.3,19.7) rot=(0,0,1;0rad)
  Solid = false
  Source = -> Face081
  Symmetric = false
FEATURE [Part::Feature] Face082
  shape: bbox 3.5 x 17.8 x 2e-07 mm, 1 faces, 0 solids (baked)
FEATURE [Part::Revolution] Revolve086  label="removeToCreateScrewAndThreadedInsertHole023"
  Angle = 360
  Axis = (0,1,0)
  Base = (0,0,0)
  FaceMakerClass = Part::FaceMakerBullseye
  Placement = pos=(62.3,30.3,51.7) rot=(0,0,1;0rad)
  Solid = false
  Source = -> Face082
  Symmetric = false
FEATURE [Part::Feature] Face083
  shape: bbox 3.5 x 17.8 x 2e-07 mm, 1 faces, 0 solids (baked)
FEATURE [Part::Revolution] Revolve087  label="removeToCreateScrewAndThreadedInsertHole024"
  Angle = 360
  Axis = (0,1,0)
  Base = (0,0,0)
  FaceMakerClass = Part::FaceMakerBullseye
  Placement = pos=(30.3,30.3,19.7) rot=(0,0,1;0rad)
  Solid = false
  Source = -> Face083
  Symmetric = false
FEATURE [Part::Feature] Face084
  shape: bbox 3.5 x 17.8 x 2e-07 mm, 1 faces, 0 solids (baked)
FEATURE [Part::Revolution] Revolve088  label="removeToCreateScrewAndThreadedInsertHole025"
  Angle = 360
  Axis = (0,1,0)
  Base = (0,0,0)
  FaceMakerClass = Part::FaceMakerBullseye
  Placement = pos=(30.3,30.3,51.7) rot=(0,0,1;0rad)
  Solid = false
  Source = -> Face084
  Symmetric = false
FEATURE [Part::MultiFuse] Fusion054  label="createThreadedInsertHolesForFan001"
  Shapes = -> [Revolve085,Revolve086,Revolve087,Revolve088]
FEATURE [Part::Cut] Cut018  label="top007"
  Base = -> Fusion040
  Tool = -> Fusion054
FEATURE [Sketcher::SketchObject] Sketch029
  FullyConstrained = false
  Placement = pos=(0,0,0) rot=(1,0,0;1.5708rad)
  sketch-geometry (24):
    g0: ArcOfCircle CenterX=-4 CenterY=-10.5 CenterZ=0 NormalX=0 NormalY=0 NormalZ=1 AngleXU=0 Radius=1.5 StartAngle=6e-16 EndAngle=3.14159
    g1: ArcOfCircle CenterX=-34.2 CenterY=-10.5 CenterZ=0 NormalX=0 NormalY=0 NormalZ=1 AngleXU=0 Radius=1.5 StartAngle=0 EndAngle=3.14159
    g2: ArcOfCircle CenterX=-34.2 CenterY=-27.7 CenterZ=0 NormalX=0 NormalY=0 NormalZ=1 AngleXU=0 Radius=1.5 StartAngle=3.14159 EndAngle=6.28319
    g3: ArcOfCircle CenterX=-4 CenterY=-27.7 CenterZ=0 NormalX=0 NormalY=0 NormalZ=1 AngleXU=0 Radius=1.5 StartAngle=3.1416 EndAngle=6.28319
    g4: ArcOfCircle CenterX=-10 CenterY=-4.3 CenterZ=0 NormalX=0 NormalY=0 NormalZ=1 AngleXU=0 Radius=1.5 StartAngle=2e-16 EndAngle=3.14159
    g5: ArcOfCircle CenterX=-16.1 CenterY=-1.8 CenterZ=0 NormalX=0 NormalY=0 NormalZ=1 AngleXU=0 Radius=1.5 StartAngle=5e-16 EndAngle=3.14159
    g6: ArcOfCircle CenterX=-22.1 CenterY=-1.8 CenterZ=0 NormalX=0 NormalY=0 NormalZ=1 AngleXU=0 Radius=1.5 StartAngle=5e-16 EndAngle=3.14159
    g7: ArcOfCircle CenterX=-28.2 CenterY=-4.3 CenterZ=0 NormalX=0 NormalY=0 NormalZ=1 AngleXU=0 Radius=1.5 StartAngle=2e-16 EndAngle=3.14159
    g8: ArcOfCircle CenterX=-10 CenterY=-33.9 CenterZ=0 NormalX=0 NormalY=0 NormalZ=1 AngleXU=0 Radius=1.5 StartAngle=3.14159 EndAngle=6.28319
    g9: ArcOfCircle CenterX=-16.1 CenterY=-36.4 CenterZ=0 NormalX=0 NormalY=0 NormalZ=1 AngleXU=0 Radius=1.5 StartAngle=3.14159 EndAngle=6.28319
    g10: ArcOfCircle CenterX=-22.1 CenterY=-36.4 CenterZ=0 NormalX=0 NormalY=0 NormalZ=1 AngleXU=0 Radius=1.5 StartAngle=3.14159 EndAngle=6.28319
    g11: ArcOfCircle CenterX=-28.2 CenterY=-33.9 CenterZ=0 NormalX=0 NormalY=0 NormalZ=1 AngleXU=0 Radius=1.5 StartAngle=3.14159 EndAngle=6.28319
    g12: LineSegment StartX=-35.7 StartY=-10.5 StartZ=0 EndX=-35.7 EndY=-27.7 EndZ=0
    g13: LineSegment StartX=-32.7 StartY=-10.5 StartZ=0 EndX=-32.7 EndY=-27.7 EndZ=0
    g14: LineSegment StartX=-29.7 StartY=-33.9 StartZ=0 EndX=-29.7 EndY=-4.3 EndZ=0
    g15: LineSegment StartX=-26.7 StartY=-33.9 StartZ=0 EndX=-26.7 EndY=-4.3 EndZ=0
    g16: LineSegment StartX=-2.5 StartY=-10.5 StartZ=0 EndX=-2.5 EndY=-27.7 EndZ=0
    g17: LineSegment StartX=-8.5 StartY=-4.3 StartZ=0 EndX=-8.5 EndY=-33.9 EndZ=0
    g18: LineSegment StartX=-5.5 StartY=-10.5 StartZ=0 EndX=-5.5 EndY=-27.7 EndZ=0
    g19: LineSegment StartX=-11.5 StartY=-4.3 StartZ=0 EndX=-11.5 EndY=-33.9 EndZ=0
    g20: LineSegment StartX=-14.6 StartY=-1.8 StartZ=0 EndX=-14.6 EndY=-36.4 EndZ=0
    g21: LineSegment StartX=-17.6 StartY=-1.8 StartZ=0 EndX=-17.6 EndY=-36.4 EndZ=0
    g22: LineSegment StartX=-20.6 StartY=-36.4 StartZ=0 EndX=-20.6 EndY=-1.8 EndZ=0
    g23: LineSegment StartX=-23.6 StartY=-1.8 StartZ=0 EndX=-23.6 EndY=-36.4 EndZ=0
  constraints (48):
    c: Block(g0)
    c: Block(g1)
    c: Block(g2)
    c: Block(g3)
    c: Block(g4)
    c: Block(g5)
    c: Block(g6)
    c: Block(g7)
    c: Block(g8)
    c: Block(g9)
    c: Block(g10)
    c: Block(g11)
    c: Coincident(g12,g1)
    c: Coincident(g12,g2)
    c: Vertical(g12)
    c: Coincident(g13,g1)
    c: Coincident(g13,g2)
    c: Vertical(g13)
    c: Coincident(g14,g11)
    c: Coincident(g14,g7)
    c: Vertical(g14)
    c: Coincident(g15,g11)
    c: Coincident(g15,g7)
    c: Vertical(g15)
    c: Coincident(g16,g0)
    c: Coincident(g16,g3)
    c: Vertical(g16)
    c: Coincident(g17,g4)
    c: Coincident(g17,g8)
    c: Vertical(g17)
    c: Coincident(g18,g0)
    c: Coincident(g18,g3)
    c: Vertical(g18)
    c: Coincident(g19,g4)
    c: Coincident(g19,g8)
    c: Vertical(g19)
    c: Coincident(g20,g5)
    c: Coincident(g20,g9)
    c: Vertical(g20)
    c: Coincident(g21,g5)
    c: Coincident(g21,g9)
    c: Vertical(g21)
    c: Coincident(g22,g10)
    c: Coincident(g22,g6)
    c: Vertical(g22)
    c: Coincident(g23,g6)
    c: Coincident(g23,g10)
    c: Vertical(g23)
FEATURE [Part::Extrusion] Extrude020  label="removeToCreateFanGrillHoles"
  Base = -> Sketch029
  Dir = (0,-1,6e-16)
  DirMode = 2
  FaceMakerClass = Part::FaceMakerBullseye
  LengthFwd = 10
  LengthRev = 0
  Placement = pos=(65.4,44,54.82) rot=(0,0,1;0rad)
  Solid = true
  Symmetric = false
FEATURE [Part::MultiFuse] Fusion055  label="top008"
  Shapes = -> [Cut017,Cut018]
FEATURE [Part::Cut] Cut019  label="top009"
  Base = -> Fusion055
  Tool = -> Extrude020
FEATURE [App::MeasureDistance] Distance003  label="Distance: 71.95 mm"
  Distance = 71.9513
  P1 = (117,38,72)
  P2 = (117,38,0.0487319)
FEATURE [Sketcher::SketchObject] Sketch030
  FullyConstrained = true
  Placement = pos=(117,19,0) rot=(0.57735,0.57735,0.57735;2.0944rad)
  sketch-geometry (48):
    g0: LineSegment StartX=-49.19 StartY=69.25 StartZ=0 EndX=-49.19 EndY=66.25 EndZ=0
    g1: LineSegment StartX=-49.19 StartY=63.5 StartZ=0 EndX=-49.19 EndY=60.5 EndZ=0
    g2: LineSegment StartX=-49.19 StartY=57.75 StartZ=0 EndX=-49.19 EndY=54.75 EndZ=0
    g3: LineSegment StartX=-49.19 StartY=52 StartZ=0 EndX=-49.19 EndY=49 EndZ=0
    g4: LineSegment StartX=-49.19 StartY=46.25 StartZ=0 EndX=-49.19 EndY=43.25 EndZ=0
    g5: LineSegment StartX=-49.19 StartY=40.5 StartZ=0 EndX=-49.19 EndY=37.5 EndZ=0
    g6: LineSegment StartX=-49.19 StartY=34.5 StartZ=0 EndX=-49.19 EndY=31.5 EndZ=0
    g7: LineSegment StartX=-49.19 StartY=28.75 StartZ=0 EndX=-49.19 EndY=25.75 EndZ=0
    g8: LineSegment StartX=-49.19 StartY=23 StartZ=0 EndX=-49.19 EndY=20 EndZ=0
    g9: LineSegment StartX=-49.19 StartY=17.25 StartZ=0 EndX=-49.19 EndY=14.25 EndZ=0
    g10: LineSegment StartX=-49.19 StartY=11.5 StartZ=0 EndX=-49.19 EndY=8.5 EndZ=0
    g11: LineSegment StartX=-49.19 StartY=5.75 StartZ=0 EndX=-49.19 EndY=2.75 EndZ=0
    g12: ArcOfCircle CenterX=-1.5 CenterY=67.75 CenterZ=0 NormalX=0 NormalY=0 NormalZ=1 AngleXU=0 Radius=1.5 StartAngle=4.71239 EndAngle=7.85398
    g13: ArcOfCircle CenterX=-1.5 CenterY=62 CenterZ=0 NormalX=0 NormalY=0 NormalZ=1 AngleXU=0 Radius=1.5 StartAngle=4.71239 EndAngle=7.85398
    g14: ArcOfCircle CenterX=-1.5 CenterY=56.25 CenterZ=0 NormalX=0 NormalY=0 NormalZ=1 AngleXU=0 Radius=1.5 StartAngle=4.71239 EndAngle=7.85398
    g15: ArcOfCircle CenterX=-11.49 CenterY=50.5 CenterZ=0 NormalX=0 NormalY=0 NormalZ=1 AngleXU=0 Radius=1.5 StartAngle=4.71239 EndAngle=7.85398
    g16: ArcOfCircle CenterX=-16.28 CenterY=44.75 CenterZ=0 NormalX=0 NormalY=0 NormalZ=1 AngleXU=0 Radius=1.5 StartAngle=4.71239 EndAngle=7.85398
    g17: ArcOfCircle CenterX=-18.2337 CenterY=39 CenterZ=0 NormalX=0 NormalY=0 NormalZ=1 AngleXU=0 Radius=1.5 StartAngle=4.71485 EndAngle=7.85398
    g18: ArcOfCircle CenterX=-16.2837 CenterY=27.25 CenterZ=0 NormalX=0 NormalY=0 NormalZ=1 AngleXU=0 Radius=1.5 StartAngle=4.71485 EndAngle=7.85398
    g19: ArcOfCircle CenterX=-18.2337 CenterY=33 CenterZ=0 NormalX=0 NormalY=0 NormalZ=1 AngleXU=0 Radius=1.5 StartAngle=4.71485 EndAngle=7.85398
    g20: ArcOfCircle CenterX=-11.49 CenterY=21.5 CenterZ=0 NormalX=0 NormalY=0 NormalZ=1 AngleXU=0 Radius=1.5 StartAngle=4.71239 EndAngle=7.85398
    g21: ArcOfCircle CenterX=-1.5 CenterY=4.25 CenterZ=0 NormalX=0 NormalY=0 NormalZ=1 AngleXU=0 Radius=1.5 StartAngle=4.71239 EndAngle=7.85398
    g22: ArcOfCircle CenterX=-1.5 CenterY=10 CenterZ=0 NormalX=0 NormalY=0 NormalZ=1 AngleXU=0 Radius=1.5 StartAngle=4.71239 EndAngle=7.85398
    g23: ArcOfCircle CenterX=-1.5 CenterY=15.75 CenterZ=0 NormalX=0 NormalY=0 NormalZ=1 AngleXU=0 Radius=1.5 StartAngle=4.71239 EndAngle=7.85398
    g24: LineSegment StartX=-49.19 StartY=69.25 StartZ=0 EndX=-1.5 EndY=69.25 EndZ=0
    g25: LineSegment StartX=-49.19 StartY=66.25 StartZ=0 EndX=-1.5 EndY=66.25 EndZ=0
    g26: LineSegment StartX=-49.19 StartY=63.5 StartZ=0 EndX=-1.5 EndY=63.5 EndZ=0
    g27: LineSegment StartX=-49.19 StartY=60.5 StartZ=0 EndX=-1.5 EndY=60.5 EndZ=0
    g28: LineSegment StartX=-49.19 StartY=57.75 StartZ=0 EndX=-1.5 EndY=57.75 EndZ=0
    g29: LineSegment StartX=-49.19 StartY=54.75 StartZ=0 EndX=-1.5 EndY=54.75 EndZ=0
    g30: LineSegment StartX=-49.19 StartY=52 StartZ=0 EndX=-11.49 EndY=52 EndZ=0
    g31: LineSegment StartX=-49.19 StartY=49 StartZ=0 EndX=-11.49 EndY=49 EndZ=0
    g32: LineSegment StartX=-49.19 StartY=46.25 StartZ=0 EndX=-16.28 EndY=46.25 EndZ=0
    g33: LineSegment StartX=-49.19 StartY=43.25 StartZ=0 EndX=-16.28 EndY=43.25 EndZ=0
    g34: LineSegment StartX=-49.19 StartY=40.5 StartZ=0 EndX=-18.2337 EndY=40.5 EndZ=0
    g35: LineSegment StartX=-49.19 StartY=37.5 StartZ=0 EndX=-18.23 EndY=37.5 EndZ=0
    g36: LineSegment StartX=-49.19 StartY=34.5 StartZ=0 EndX=-18.2337 EndY=34.5 EndZ=0
    g37: LineSegment StartX=-49.19 StartY=31.5 StartZ=0 EndX=-18.23 EndY=31.5 EndZ=0
    g38: LineSegment StartX=-49.19 StartY=28.75 StartZ=0 EndX=-16.2837 EndY=28.75 EndZ=0
    g39: LineSegment StartX=-49.19 StartY=25.75 StartZ=0 EndX=-16.28 EndY=25.75 EndZ=0
    g40: LineSegment StartX=-49.19 StartY=23 StartZ=0 EndX=-11.49 EndY=23 EndZ=0
    g41: LineSegment StartX=-49.19 StartY=20 StartZ=0 EndX=-11.49 EndY=20 EndZ=0
    g42: LineSegment StartX=-49.19 StartY=17.25 StartZ=0 EndX=-1.5 EndY=17.25 EndZ=0
    g43: LineSegment StartX=-49.19 StartY=14.25 StartZ=0 EndX=-1.5 EndY=14.25 EndZ=0
    g44: LineSegment StartX=-49.19 StartY=11.5 StartZ=0 EndX=-1.5 EndY=11.5 EndZ=0
    g45: LineSegment StartX=-49.19 StartY=8.5 StartZ=0 EndX=-1.5 EndY=8.5 EndZ=0
    g46: LineSegment StartX=-49.19 StartY=5.75 StartZ=0 EndX=-1.5 EndY=5.75 EndZ=0
    g47: LineSegment StartX=-49.19 StartY=2.75 StartZ=0 EndX=-1.5 EndY=2.75 EndZ=0
  constraints (120):
    c: Vertical(g0)
    c: Distance(g0) = 3
    c: Block(g0)
    c: Vertical(g1)
    c: Distance(g1) = 3
    c: Vertical(g2)
    c: Equal(g0,g2) = 3
    c: Block(g2)
    c: Vertical(g3)
    c: Equal(g1,g3) = 3
    c: Vertical(g4)
    c: Equal(g0,g4) = 3
    c: Block(g4)
    c: Vertical(g5)
    c: Equal(g1,g5) = 3
    c: Vertical(g6)
    c: Equal(g0,g6) = 3
    c: Block(g6)
    c: Vertical(g7)
    c: Equal(g1,g7) = 3
    c: Vertical(g8)
    c: Equal(g0,g8) = 3
    c: Block(g8)
    c: Vertical(g9)
    c: Equal(g1,g9) = 3
    c: Vertical(g10)
    c: Equal(g0,g10) = 3
    c: Block(g10)
    c: Vertical(g11)
    c: Equal(g1,g11) = 3
    c: Block(g12)
    c: Block(g13)
    c: Block(g14)
    c: Block(g15)
    c: Block(g16)
    c: Block(g17)
    c: Block(g18)
    c: Block(g19)
    c: Block(g20)
    c: Block(g21)
    c: Block(g22)
    c: Block(g23)
    c: Block(g11)
    c: Block(g9)
    c: Block(g7)
    c: Block(g5)
    c: Block(g3)
    c: Block(g1)
    c: Coincident(g24,g0)
    c: Coincident(g24,g12)
    c: Horizontal(g24)
    c: Coincident(g25,g0)
    c: Coincident(g25,g12)
    c: Horizontal(g25)
    c: Coincident(g26,g1)
    c: Coincident(g26,g13)
    c: Horizontal(g26)
    c: Coincident(g27,g1)
    c: Coincident(g27,g13)
    c: Horizontal(g27)
    c: Coincident(g28,g2)
    c: Coincident(g28,g14)
    c: Horizontal(g28)
    c: Coincident(g29,g2)
    c: Coincident(g29,g14)
    c: Horizontal(g29)
    c: Coincident(g30,g3)
    c: Coincident(g30,g15)
    c: Horizontal(g30)
    c: Coincident(g31,g3)
    c: Coincident(g31,g15)
    c: Horizontal(g31)
    c: Coincident(g32,g4)
    c: Coincident(g32,g16)
    c: Horizontal(g32)
    c: Coincident(g33,g4)
    c: Coincident(g33,g16)
    c: Horizontal(g33)
    c: Coincident(g34,g5)
    c: Coincident(g34,g17)
    c: Horizontal(g34)
    c: Coincident(g35,g5)
    c: Coincident(g35,g17)
    c: Horizontal(g35)
    c: Coincident(g36,g6)
    c: Coincident(g36,g19)
    c: Horizontal(g36)
    c: Coincident(g37,g6)
    c: Coincident(g37,g19)
    c: Horizontal(g37)
    c: Coincident(g38,g7)
    c: Coincident(g38,g18)
    c: Horizontal(g38)
    c: Coincident(g39,g7)
    c: Coincident(g39,g18)
    c: Horizontal(g39)
    c: Coincident(g40,g8)
    c: Coincident(g40,g20)
    c: Horizontal(g40)
    c: Coincident(g41,g8)
    c: Coincident(g41,g20)
    c: Horizontal(g41)
    c: Coincident(g42,g9)
    c: Coincident(g42,g23)
    c: Horizontal(g42)
    c: Coincident(g43,g9)
    c: Coincident(g43,g23)
    c: Horizontal(g43)
    c: Coincident(g44,g10)
    c: Coincident(g44,g22)
    c: Horizontal(g44)
    c: Coincident(g45,g10)
    c: Coincident(g45,g22)
    c: Horizontal(g45)
    c: Coincident(g46,g11)
    c: Coincident(g46,g21)
    c: Horizontal(g46)
    c: Coincident(g47,g11)
    c: Coincident(g47,g21)
    c: Horizontal(g47)
FEATURE [Sketcher::SketchObject] Sketch031
  FullyConstrained = true
  Placement = pos=(117,19,0) rot=(0.57735,0.57735,0.57735;2.0944rad)
  sketch-geometry (24):
    g0: ArcOfCircle CenterX=-49.19 CenterY=67.75 CenterZ=0 NormalX=0 NormalY=0 NormalZ=1 AngleXU=0 Radius=1.5 StartAngle=1.5708 EndAngle=4.71239
    g1: ArcOfCircle CenterX=-49.19 CenterY=62 CenterZ=0 NormalX=0 NormalY=0 NormalZ=1 AngleXU=0 Radius=1.5 StartAngle=1.5708 EndAngle=4.71239
    g2: ArcOfCircle CenterX=-49.19 CenterY=56.25 CenterZ=0 NormalX=0 NormalY=0 NormalZ=1 AngleXU=0 Radius=1.5 StartAngle=1.5708 EndAngle=4.71239
    g3: ArcOfCircle CenterX=-49.19 CenterY=50.5 CenterZ=0 NormalX=0 NormalY=0 NormalZ=1 AngleXU=0 Radius=1.5 StartAngle=1.5708 EndAngle=4.71239
    g4: ArcOfCircle CenterX=-49.19 CenterY=44.75 CenterZ=0 NormalX=0 NormalY=0 NormalZ=1 AngleXU=0 Radius=1.5 StartAngle=1.5708 EndAngle=4.71239
    g5: ArcOfCircle CenterX=-49.19 CenterY=39 CenterZ=0 NormalX=0 NormalY=0 NormalZ=1 AngleXU=0 Radius=1.5 StartAngle=1.5708 EndAngle=4.71239
    g6: ArcOfCircle CenterX=-49.19 CenterY=33 CenterZ=0 NormalX=0 NormalY=0 NormalZ=1 AngleXU=0 Radius=1.5 StartAngle=1.5708 EndAngle=4.71239
    g7: ArcOfCircle CenterX=-49.19 CenterY=27.25 CenterZ=0 NormalX=0 NormalY=0 NormalZ=1 AngleXU=0 Radius=1.5 StartAngle=1.5708 EndAngle=4.71239
    g8: ArcOfCircle CenterX=-49.19 CenterY=21.5 CenterZ=0 NormalX=0 NormalY=0 NormalZ=1 AngleXU=0 Radius=1.5 StartAngle=1.5708 EndAngle=4.71239
    g9: ArcOfCircle CenterX=-49.19 CenterY=15.75 CenterZ=0 NormalX=0 NormalY=0 NormalZ=1 AngleXU=0 Radius=1.5 StartAngle=1.5708 EndAngle=4.71239
    g10: ArcOfCircle CenterX=-49.19 CenterY=10 CenterZ=0 NormalX=0 NormalY=0 NormalZ=1 AngleXU=0 Radius=1.5 StartAngle=1.5708 EndAngle=4.71239
    g11: ArcOfCircle CenterX=-49.19 CenterY=4.25 CenterZ=0 NormalX=0 NormalY=0 NormalZ=1 AngleXU=0 Radius=1.5 StartAngle=1.5708 EndAngle=4.71239
    g12: LineSegment StartX=-49.19 StartY=69.25 StartZ=0 EndX=-49.19 EndY=66.25 EndZ=0
    g13: LineSegment StartX=-49.19 StartY=63.5 StartZ=0 EndX=-49.19 EndY=60.5 EndZ=0
    g14: LineSegment StartX=-49.19 StartY=57.75 StartZ=0 EndX=-49.19 EndY=54.75 EndZ=0
    g15: LineSegment StartX=-49.19 StartY=52 StartZ=0 EndX=-49.19 EndY=49 EndZ=0
    g16: LineSegment StartX=-49.19 StartY=46.25 StartZ=0 EndX=-49.19 EndY=43.25 EndZ=0
    g17: LineSegment StartX=-49.19 StartY=40.5 StartZ=0 EndX=-49.19 EndY=37.5 EndZ=0
    g18: LineSegment StartX=-49.19 StartY=34.5 StartZ=0 EndX=-49.19 EndY=31.5 EndZ=0
    g19: LineSegment StartX=-49.19 StartY=28.75 StartZ=0 EndX=-49.19 EndY=25.75 EndZ=0
    g20: LineSegment StartX=-49.19 StartY=23 StartZ=0 EndX=-49.19 EndY=20 EndZ=0
    g21: LineSegment StartX=-49.19 StartY=17.25 StartZ=0 EndX=-49.19 EndY=14.25 EndZ=0
    g22: LineSegment StartX=-49.19 StartY=11.5 StartZ=0 EndX=-49.19 EndY=8.5 EndZ=0
    g23: LineSegment StartX=-49.19 StartY=5.75 StartZ=0 EndX=-49.19 EndY=2.75 EndZ=0
  constraints (48):
    c: Block(g0)
    c: Block(g1)
    c: Block(g2)
    c: Block(g3)
    c: Block(g4)
    c: Block(g5)
    c: Block(g6)
    c: Block(g7)
    c: Block(g8)
    c: Block(g9)
    c: Block(g10)
    c: Block(g11)
    c: Coincident(g12,g0)
    c: Coincident(g12,g0)
    c: Vertical(g12)
    c: Vertical(g13)
    c: Coincident(g13,g1)
    c: Vertical(g14)
    c: Coincident(g14,g2)
    c: Vertical(g15)
    c: Coincident(g15,g3)
    c: Vertical(g16)
    c: Coincident(g16,g4)
    c: Vertical(g17)
    c: Coincident(g17,g5)
    c: Vertical(g18)
    c: Coincident(g18,g6)
    c: Vertical(g19)
    c: Coincident(g19,g7)
    c: Vertical(g20)
    c: Coincident(g20,g8)
    c: Vertical(g21)
    c: Coincident(g21,g9)
    c: Vertical(g22)
    c: Coincident(g22,g10)
    c: Vertical(g23)
    c: Coincident(g23,g11)
    c: Block(g23)
    c: Block(g22)
    c: Block(g21)
    c: Block(g20)
    c: Block(g13)
    c: Block(g14)
    c: Block(g15)
    c: Block(g16)
    c: Block(g17)
    c: Block(g18)
    c: Block(g19)
FEATURE [Part::Extrusion] Extrude022
  Base = -> Sketch030
  Dir = (1,-2e-16,2e-16)
  DirMode = 2
  FaceMakerClass = Part::FaceMakerBullseye
  LengthFwd = 19
  LengthRev = 0
  Placement = pos=(-19,0,0) rot=(0,0,1;0rad)
  Solid = true
  Symmetric = false
FEATURE [Part::Fillet] Fillet022
  Base = -> Extrude022
  Edges = 24 edges r=1.49: [Edge6,Edge11,Edge18,Edge23,Edge30,Edge35,Edge42,Edge47,Edge54,Edge59,Edge66,Edge71,Edge78,Edge83,Edge90,Edge95,Edge102,Edge107,Edge114,Edge119,Edge126,Edge131,Edge138,Edge143]
FEATURE [Part::Cut] Cut020  label="top010"
  Base = -> Cut019
  Tool = -> Fillet022
FEATURE [Sketcher::SketchObject] Sketch032
  FullyConstrained = true
  Placement = pos=(117,19,0) rot=(0.57735,0.57735,0.57735;2.0944rad)
  sketch-geometry (48):
    g0: LineSegment StartX=-49.19 StartY=69.25 StartZ=0 EndX=-49.19 EndY=66.25 EndZ=0
    g1: LineSegment StartX=-49.19 StartY=63.5 StartZ=0 EndX=-49.19 EndY=60.5 EndZ=0
    g2: LineSegment StartX=-49.19 StartY=57.75 StartZ=0 EndX=-49.19 EndY=54.75 EndZ=0
    g3: LineSegment StartX=-49.19 StartY=52 StartZ=0 EndX=-49.19 EndY=49 EndZ=0
    g4: LineSegment StartX=-49.19 StartY=46.25 StartZ=0 EndX=-49.19 EndY=43.25 EndZ=0
    g5: LineSegment StartX=-49.19 StartY=40.5 StartZ=0 EndX=-49.19 EndY=37.5 EndZ=0
    g6: LineSegment StartX=-49.19 StartY=34.5 StartZ=0 EndX=-49.19 EndY=31.5 EndZ=0
    g7: LineSegment StartX=-49.19 StartY=28.75 StartZ=0 EndX=-49.19 EndY=25.75 EndZ=0
    g8: LineSegment StartX=-49.19 StartY=23 StartZ=0 EndX=-49.19 EndY=20 EndZ=0
    g9: LineSegment StartX=-49.19 StartY=17.25 StartZ=0 EndX=-49.19 EndY=14.25 EndZ=0
    g10: LineSegment StartX=-49.19 StartY=11.5 StartZ=0 EndX=-49.19 EndY=8.5 EndZ=0
    g11: LineSegment StartX=-49.19 StartY=5.75 StartZ=0 EndX=-49.19 EndY=2.75 EndZ=0
    g12: ArcOfCircle CenterX=-1.5 CenterY=67.75 CenterZ=0 NormalX=0 NormalY=0 NormalZ=1 AngleXU=0 Radius=1.5 StartAngle=4.71239 EndAngle=7.85398
    g13: ArcOfCircle CenterX=-1.5 CenterY=62 CenterZ=0 NormalX=0 NormalY=0 NormalZ=1 AngleXU=0 Radius=1.5 StartAngle=4.71239 EndAngle=7.85398
    g14: ArcOfCircle CenterX=-1.5 CenterY=56.25 CenterZ=0 NormalX=0 NormalY=0 NormalZ=1 AngleXU=0 Radius=1.5 StartAngle=4.71239 EndAngle=7.85398
    g15: ArcOfCircle CenterX=-11.49 CenterY=50.5 CenterZ=0 NormalX=0 NormalY=0 NormalZ=1 AngleXU=0 Radius=1.5 StartAngle=4.71239 EndAngle=7.85398
    g16: ArcOfCircle CenterX=-16.28 CenterY=44.75 CenterZ=0 NormalX=0 NormalY=0 NormalZ=1 AngleXU=0 Radius=1.5 StartAngle=4.71239 EndAngle=7.85398
    g17: ArcOfCircle CenterX=-18.2337 CenterY=39 CenterZ=0 NormalX=0 NormalY=0 NormalZ=1 AngleXU=0 Radius=1.5 StartAngle=4.71485 EndAngle=7.85398
    g18: ArcOfCircle CenterX=-16.2837 CenterY=27.25 CenterZ=0 NormalX=0 NormalY=0 NormalZ=1 AngleXU=0 Radius=1.5 StartAngle=4.71485 EndAngle=7.85398
    g19: ArcOfCircle CenterX=-18.2337 CenterY=33 CenterZ=0 NormalX=0 NormalY=0 NormalZ=1 AngleXU=0 Radius=1.5 StartAngle=4.71485 EndAngle=7.85398
    g20: ArcOfCircle CenterX=-11.49 CenterY=21.5 CenterZ=0 NormalX=0 NormalY=0 NormalZ=1 AngleXU=0 Radius=1.5 StartAngle=4.71239 EndAngle=7.85398
    g21: ArcOfCircle CenterX=-1.5 CenterY=4.25 CenterZ=0 NormalX=0 NormalY=0 NormalZ=1 AngleXU=0 Radius=1.5 StartAngle=4.71239 EndAngle=7.85398
    g22: ArcOfCircle CenterX=-1.5 CenterY=10 CenterZ=0 NormalX=0 NormalY=0 NormalZ=1 AngleXU=0 Radius=1.5 StartAngle=4.71239 EndAngle=7.85398
    g23: ArcOfCircle CenterX=-1.5 CenterY=15.75 CenterZ=0 NormalX=0 NormalY=0 NormalZ=1 AngleXU=0 Radius=1.5 StartAngle=4.71239 EndAngle=7.85398
    g24: LineSegment StartX=-49.19 StartY=69.25 StartZ=0 EndX=-1.5 EndY=69.25 EndZ=0
    g25: LineSegment StartX=-49.19 StartY=66.25 StartZ=0 EndX=-1.5 EndY=66.25 EndZ=0
    g26: LineSegment StartX=-49.19 StartY=63.5 StartZ=0 EndX=-1.5 EndY=63.5 EndZ=0
    g27: LineSegment StartX=-49.19 StartY=60.5 StartZ=0 EndX=-1.5 EndY=60.5 EndZ=0
    g28: LineSegment StartX=-49.19 StartY=57.75 StartZ=0 EndX=-1.5 EndY=57.75 EndZ=0
    g29: LineSegment StartX=-49.19 StartY=54.75 StartZ=0 EndX=-1.5 EndY=54.75 EndZ=0
    g30: LineSegment StartX=-49.19 StartY=52 StartZ=0 EndX=-11.49 EndY=52 EndZ=0
    g31: LineSegment StartX=-49.19 StartY=49 StartZ=0 EndX=-11.49 EndY=49 EndZ=0
    g32: LineSegment StartX=-49.19 StartY=46.25 StartZ=0 EndX=-16.28 EndY=46.25 EndZ=0
    g33: LineSegment StartX=-49.19 StartY=43.25 StartZ=0 EndX=-16.28 EndY=43.25 EndZ=0
    g34: LineSegment StartX=-49.19 StartY=40.5 StartZ=0 EndX=-18.2337 EndY=40.5 EndZ=0
    g35: LineSegment StartX=-49.19 StartY=37.5 StartZ=0 EndX=-18.23 EndY=37.5 EndZ=0
    g36: LineSegment StartX=-49.19 StartY=34.5 StartZ=0 EndX=-18.2337 EndY=34.5 EndZ=0
    g37: LineSegment StartX=-49.19 StartY=31.5 StartZ=0 EndX=-18.23 EndY=31.5 EndZ=0
    g38: LineSegment StartX=-49.19 StartY=28.75 StartZ=0 EndX=-16.2837 EndY=28.75 EndZ=0
    g39: LineSegment StartX=-49.19 StartY=25.75 StartZ=0 EndX=-16.28 EndY=25.75 EndZ=0
    g40: LineSegment StartX=-49.19 StartY=23 StartZ=0 EndX=-11.49 EndY=23 EndZ=0
    g41: LineSegment StartX=-49.19 StartY=20 StartZ=0 EndX=-11.49 EndY=20 EndZ=0
    g42: LineSegment StartX=-49.19 StartY=17.25 StartZ=0 EndX=-1.5 EndY=17.25 EndZ=0
    g43: LineSegment StartX=-49.19 StartY=14.25 StartZ=0 EndX=-1.5 EndY=14.25 EndZ=0
    g44: LineSegment StartX=-49.19 StartY=11.5 StartZ=0 EndX=-1.5 EndY=11.5 EndZ=0
    g45: LineSegment StartX=-49.19 StartY=8.5 StartZ=0 EndX=-1.5 EndY=8.5 EndZ=0
    g46: LineSegment StartX=-49.19 StartY=5.75 StartZ=0 EndX=-1.5 EndY=5.75 EndZ=0
    g47: LineSegment StartX=-49.19 StartY=2.75 StartZ=0 EndX=-1.5 EndY=2.75 EndZ=0
  constraints (120):
    c: Vertical(g0)
    c: Distance(g0) = 3
    c: Block(g0)
    c: Vertical(g1)
    c: Distance(g1) = 3
    c: Vertical(g2)
    c: Equal(g0,g2) = 3
    c: Block(g2)
    c: Vertical(g3)
    c: Equal(g1,g3) = 3
    c: Vertical(g4)
    c: Equal(g0,g4) = 3
    c: Block(g4)
    c: Vertical(g5)
    c: Equal(g1,g5) = 3
    c: Vertical(g6)
    c: Equal(g0,g6) = 3
    c: Block(g6)
    c: Vertical(g7)
    c: Equal(g1,g7) = 3
    c: Vertical(g8)
    c: Equal(g0,g8) = 3
    c: Block(g8)
    c: Vertical(g9)
    c: Equal(g1,g9) = 3
    c: Vertical(g10)
    c: Equal(g0,g10) = 3
    c: Block(g10)
    c: Vertical(g11)
    c: Equal(g1,g11) = 3
    c: Block(g12)
    c: Block(g13)
    c: Block(g14)
    c: Block(g15)
    c: Block(g16)
    c: Block(g17)
    c: Block(g18)
    c: Block(g19)
    c: Block(g20)
    c: Block(g21)
    c: Block(g22)
    c: Block(g23)
    c: Block(g11)
    c: Block(g9)
    c: Block(g7)
    c: Block(g5)
    c: Block(g3)
    c: Block(g1)
    c: Coincident(g24,g0)
    c: Coincident(g24,g12)
    c: Horizontal(g24)
    c: Coincident(g25,g0)
    c: Coincident(g25,g12)
    c: Horizontal(g25)
    c: Coincident(g26,g1)
    c: Coincident(g26,g13)
    c: Horizontal(g26)
    c: Coincident(g27,g1)
    c: Coincident(g27,g13)
    c: Horizontal(g27)
    c: Coincident(g28,g2)
    c: Coincident(g28,g14)
    c: Horizontal(g28)
    c: Coincident(g29,g2)
    c: Coincident(g29,g14)
    c: Horizontal(g29)
    c: Coincident(g30,g3)
    c: Coincident(g30,g15)
    c: Horizontal(g30)
    c: Coincident(g31,g3)
    c: Coincident(g31,g15)
    c: Horizontal(g31)
    c: Coincident(g32,g4)
    c: Coincident(g32,g16)
    c: Horizontal(g32)
    c: Coincident(g33,g4)
    c: Coincident(g33,g16)
    c: Horizontal(g33)
    c: Coincident(g34,g5)
    c: Coincident(g34,g17)
    c: Horizontal(g34)
    c: Coincident(g35,g5)
    c: Coincident(g35,g17)
    c: Horizontal(g35)
    c: Coincident(g36,g6)
    c: Coincident(g36,g19)
    c: Horizontal(g36)
    c: Coincident(g37,g6)
    c: Coincident(g37,g19)
    c: Horizontal(g37)
    c: Coincident(g38,g7)
    c: Coincident(g38,g18)
    c: Horizontal(g38)
    c: Coincident(g39,g7)
    c: Coincident(g39,g18)
    c: Horizontal(g39)
    c: Coincident(g40,g8)
    c: Coincident(g40,g20)
    c: Horizontal(g40)
    c: Coincident(g41,g8)
    c: Coincident(g41,g20)
    c: Horizontal(g41)
    c: Coincident(g42,g9)
    c: Coincident(g42,g23)
    c: Horizontal(g42)
    c: Coincident(g43,g9)
    c: Coincident(g43,g23)
    c: Horizontal(g43)
    c: Coincident(g44,g10)
    c: Coincident(g44,g22)
    c: Horizontal(g44)
    c: Coincident(g45,g10)
    c: Coincident(g45,g22)
    c: Horizontal(g45)
    c: Coincident(g46,g11)
    c: Coincident(g46,g21)
    c: Horizontal(g46)
    c: Coincident(g47,g11)
    c: Coincident(g47,g21)
    c: Horizontal(g47)
FEATURE [Part::Extrusion] Extrude023
  Base = -> Sketch032
  Dir = (1,-2e-16,2e-16)
  DirMode = 2
  FaceMakerClass = Part::FaceMakerBullseye
  LengthFwd = 19
  LengthRev = 0
  Placement = pos=(-19,0,0) rot=(0,0,1;0rad)
  Solid = true
  Symmetric = false
FEATURE [Part::Fillet] Fillet023
  Base = -> Extrude023
  Edges = <same value as first occurrence — deduplicated (x6 in doc)>
  Placement = pos=(0,0.05,0) rot=(0,0,1;0rad)
FEATURE [Part::Cut] Cut014  label="bottom003"
  Base = -> Cut007
  Tool = -> Fusion047
FEATURE [Part::Cut] Cut021  label="bottom004"
  Base = -> Cut014
  Tool = -> Fillet023
FEATURE [Sketcher::SketchObject] Sketch033
  FullyConstrained = true
  Placement = pos=(117,19,0) rot=(0.57735,0.57735,0.57735;2.0944rad)
  sketch-geometry (8):
    g0: LineSegment StartX=-49.19 StartY=69.25 StartZ=0 EndX=-49.19 EndY=66.25 EndZ=0
    g1: LineSegment StartX=-49.19 StartY=5.75 StartZ=0 EndX=-49.19 EndY=2.75 EndZ=0
    g2: ArcOfCircle CenterX=-1.5 CenterY=67.75 CenterZ=0 NormalX=0 NormalY=0 NormalZ=1 AngleXU=0 Radius=1.5 StartAngle=4.71239 EndAngle=7.85398
    g3: ArcOfCircle CenterX=-1.5 CenterY=4.25 CenterZ=0 NormalX=0 NormalY=0 NormalZ=1 AngleXU=0 Radius=1.5 StartAngle=4.71239 EndAngle=7.85398
    g4: LineSegment StartX=-49.19 StartY=69.25 StartZ=0 EndX=-1.5 EndY=69.25 EndZ=0
    g5: LineSegment StartX=-49.19 StartY=66.25 StartZ=0 EndX=-1.5 EndY=66.25 EndZ=0
    g6: LineSegment StartX=-49.19 StartY=5.75 StartZ=0 EndX=-1.5 EndY=5.75 EndZ=0
    g7: LineSegment StartX=-49.19 StartY=2.75 StartZ=0 EndX=-1.5 EndY=2.75 EndZ=0
  constraints (19):
    c: Vertical(g0)
    c: Distance(g0) = 3
    c: Block(g0)
    c: Vertical(g1)
    c: Block(g2)
    c: Block(g3)
    c: Block(g1)
    c: Coincident(g4,g0)
    c: Coincident(g4,g2)
    c: Horizontal(g4)
    c: Coincident(g5,g0)
    c: Coincident(g5,g2)
    c: Horizontal(g5)
    c: Coincident(g6,g1)
    c: Coincident(g6,g3)
    c: Horizontal(g6)
    c: Coincident(g7,g1)
    c: Coincident(g7,g3)
    c: Horizontal(g7)
FEATURE [Sketcher::SketchObject] Sketch034
  FullyConstrained = true
  Placement = pos=(117,19,0) rot=(0.57735,0.57735,0.57735;2.0944rad)
  sketch-geometry (8):
    g0: LineSegment StartX=-49.19 StartY=63.5 StartZ=0 EndX=-49.19 EndY=60.5 EndZ=0
    g1: LineSegment StartX=-49.19 StartY=11.5 StartZ=0 EndX=-49.19 EndY=8.5 EndZ=0
    g2: ArcOfCircle CenterX=-1.5 CenterY=62 CenterZ=0 NormalX=0 NormalY=0 NormalZ=1 AngleXU=0 Radius=1.5 StartAngle=4.71239 EndAngle=7.85398
    g3: ArcOfCircle CenterX=-1.5 CenterY=10 CenterZ=0 NormalX=0 NormalY=0 NormalZ=1 AngleXU=0 Radius=1.5 StartAngle=4.71239 EndAngle=7.85398
    g4: LineSegment StartX=-49.19 StartY=63.5 StartZ=0 EndX=-1.5 EndY=63.5 EndZ=0
    g5: LineSegment StartX=-49.19 StartY=60.5 StartZ=0 EndX=-1.5 EndY=60.5 EndZ=0
    g6: LineSegment StartX=-49.19 StartY=11.5 StartZ=0 EndX=-1.5 EndY=11.5 EndZ=0
    g7: LineSegment StartX=-49.19 StartY=8.5 StartZ=0 EndX=-1.5 EndY=8.5 EndZ=0
  constraints (19):
    c: Vertical(g0)
    c: Distance(g0) = 3
    c: Vertical(g1)
    c: Block(g1)
    c: Block(g2)
    c: Block(g3)
    c: Block(g0)
    c: Coincident(g4,g0)
    c: Coincident(g4,g2)
    c: Horizontal(g4)
    c: Coincident(g5,g0)
    c: Coincident(g5,g2)
    c: Horizontal(g5)
    c: Coincident(g6,g1)
    c: Coincident(g6,g3)
    c: Horizontal(g6)
    c: Coincident(g7,g1)
    c: Coincident(g7,g3)
    c: Horizontal(g7)
FEATURE [Part::Extrusion] Extrude024
  Base = -> Sketch033
  Dir = (1,0,0)
  DirMode = 2
  FaceMakerClass = Part::FaceMakerBullseye
  LengthFwd = 10
  LengthRev = 0
  Solid = true
  Symmetric = false
FEATURE [Part::Extrusion] Extrude025
  Base = -> Sketch034
  Dir = (1,0,0)
  DirMode = 2
  FaceMakerClass = Part::FaceMakerBullseye
  LengthFwd = 10
  LengthRev = 0
  Solid = true
  Symmetric = false
FEATURE [Part::Fillet] Fillet024  label="removeFromtMoreFrontCaseScrewRetainers"
  Base = -> Extrude024
  Edges = 4 edges r=1.49: [Edge6,Edge11,Edge18,Edge23]
  Placement = pos=(-11,0,0) rot=(0,0,1;0rad)
FEATURE [Part::Fillet] Fillet025  label="removeFromtMoreFrontCaseScrewRetainers001"
  Base = -> Extrude025
  Edges = 4 edges r=1.49: [Edge6,Edge11,Edge18,Edge23]
  Placement = pos=(-19,0,0) rot=(0,0,1;0rad)
FEATURE [Part::Cut] Cut022
  Base = -> Cut015
  Tool = -> Fillet025
FEATURE [Part::Cut] Cut023  label="screwRetainers"
  Base = -> Cut022
  Tool = -> Fillet024
FEATURE [Part::MultiFuse] Fusion056  label="bottom005"
  Shapes = -> [Fusion044,Cut021]
FEATURE [Part::MultiFuse] Fusion057  label="casePillars001"
  Shapes = -> [Cut016,Fusion052]
FEATURE [Part::MultiFuse] Fusion058  label="bottom006"
  Shapes = -> [Fusion056,Cut023]
FEATURE [Part::MultiFuse] Fusion059  label="bottom007"
  Shapes = -> [Fusion058,Fillet005]
FEATURE [Part::MultiFuse] Fusion060  label="bottom008"
  Shapes = -> [Fusion059,Fusion]
FEATURE [Part::MultiFuse] Fusion061  label="top011"
  Shapes = -> [Cut006,Cut020]
FEATURE [Part::MultiFuse] Fusion062  label="top012"
  Shapes = -> [Fusion057,Fusion061]
FEATURE [Sketcher::SketchObject] Sketch035  label="topSketch007"
  FullyConstrained = true
  sketch-geometry (6):
    g0: LineSegment StartX=19 StartY=38 StartZ=0 EndX=117 EndY=38 EndZ=0
    g1: ArcOfCircle CenterX=19 CenterY=19 CenterZ=0 NormalX=0 NormalY=0 NormalZ=1 AngleXU=0 Radius=19 StartAngle=1.5708 EndAngle=3.14159
    g2: LineSegment StartX=117 StartY=38 StartZ=0 EndX=117 EndY=19 EndZ=0
    g3: LineSegment StartX=98 StartY=1.0161e-12 StartZ=0 EndX=5.22862e-06 EndY=1.0161e-12 EndZ=0
    g4: LineSegment StartX=5.22862e-06 StartY=19 StartZ=0 EndX=5.22862e-06 EndY=1.0161e-12 EndZ=0
    g5: ArcOfCircle CenterX=98 CenterY=19 CenterZ=0 NormalX=0 NormalY=0 NormalZ=1 AngleXU=0 Radius=19 StartAngle=4.71239 EndAngle=6.28319
  constraints (16):
    c: Horizontal(g0)
    c: Distance(g0) = 98
    c: Coincident(g1,g0)
    c: Block(g1)
    c: Coincident(g2,g0)
    c: Vertical(g2)
    c: Distance(g2) = 19
    c: Horizontal(g3)
    c: Coincident(g4,g1)
    c: Vertical(g4)
    c: Coincident(g3,g4)
    c: Block(g3)
    c: Coincident(g5,g2)
    c: Coincident(g5,g3)
    c: Block(g0)
    c: Block(g5)
FEATURE [Part::Extrusion] Extrude026  label="sideA001"
  Base = -> Sketch035
  Dir = (0,0,1)
  DirMode = 2
  FaceMakerClass = Part::FaceMakerBullseye
  LengthFwd = 3
  LengthRev = 0
  Placement = pos=(0,0,-2.7) rot=(0,0,1;0rad)
  Solid = true
  Symmetric = false
FEATURE [Sketcher::SketchObject] Sketch036  label="topSketch008"
  FullyConstrained = true
  sketch-geometry (6):
    g0: LineSegment StartX=19 StartY=38 StartZ=0 EndX=117 EndY=38 EndZ=0
    g1: ArcOfCircle CenterX=19 CenterY=19 CenterZ=0 NormalX=0 NormalY=0 NormalZ=1 AngleXU=0 Radius=19 StartAngle=1.5708 EndAngle=3.14159
    g2: LineSegment StartX=117 StartY=38 StartZ=0 EndX=117 EndY=19 EndZ=0
    g3: LineSegment StartX=98 StartY=1.0161e-12 StartZ=0 EndX=5.22862e-06 EndY=1.0161e-12 EndZ=0
    g4: LineSegment StartX=5.22862e-06 StartY=19 StartZ=0 EndX=5.22862e-06 EndY=1.0161e-12 EndZ=0
    g5: ArcOfCircle CenterX=98 CenterY=19 CenterZ=0 NormalX=0 NormalY=0 NormalZ=1 AngleXU=0 Radius=19 StartAngle=4.71239 EndAngle=6.28319
  constraints (16):
    c: Horizontal(g0)
    c: Distance(g0) = 98
    c: Coincident(g1,g0)
    c: Block(g1)
    c: Coincident(g2,g0)
    c: Vertical(g2)
    c: Distance(g2) = 19
    c: Horizontal(g3)
    c: Coincident(g4,g1)
    c: Vertical(g4)
    c: Coincident(g3,g4)
    c: Block(g3)
    c: Coincident(g5,g2)
    c: Coincident(g5,g3)
    c: Block(g0)
    c: Block(g5)
FEATURE [Part::Extrusion] Extrude027  label="sideB001"
  Base = -> Sketch036
  Dir = (0,0,1)
  DirMode = 2
  FaceMakerClass = Part::FaceMakerBullseye
  LengthFwd = 3
  LengthRev = 0
  Placement = pos=(0,0,71.7) rot=(0,0,1;0rad)
  Solid = true
  Symmetric = false
FEATURE [Part::MultiFuse] Fusion064  label="removeFromBottom"
  Shapes = -> [Extrude026,Extrude027]
FEATURE [Part::Cut] Cut024  label="bottom009"
  Base = -> Fusion060
  Tool = -> Fusion064
FEATURE [Sketcher::SketchObject] Sketch037  label="topSketch009"
  FullyConstrained = true
  sketch-geometry (8):
    g0: ArcOfCircle CenterX=19 CenterY=19.1201 CenterZ=0 NormalX=0 NormalY=0 NormalZ=1 AngleXU=0 Radius=18.8799 StartAngle=1.5708 EndAngle=3.14793
    g1: LineSegment StartX=0.120501 StartY=19.0004 StartZ=0 EndX=0.120501 EndY=0.000382114 EndZ=0
    g2: LineSegment StartX=19 StartY=38 StartZ=0 EndX=124 EndY=38 EndZ=0
    g3: LineSegment StartX=0.120501 StartY=0.000382114 StartZ=0 EndX=105.121 EndY=0.000382114 EndZ=0
    g4: LineSegment StartX=124 StartY=38 StartZ=0 EndX=125.616 EndY=38 EndZ=0
    g5: LineSegment StartX=105.121 StartY=0.000382114 StartZ=0 EndX=106.736 EndY=0.000382114 EndZ=0
    g6: ArcOfCircle CenterX=106.616 CenterY=19 CenterZ=0 NormalX=0 NormalY=0 NormalZ=1 AngleXU=0 Radius=19 StartAngle=4.71873 EndAngle=6.28319
    g7: LineSegment StartX=125.616 StartY=38 StartZ=0 EndX=125.616 EndY=19 EndZ=0
  constraints (21):
    c: Block(g0)
    c: Coincident(g1,g0)
    c: Vertical(g1)
    c: Horizontal(g2)
    c: Distance(g2) = 105
    c: Coincident(g2,g0)
    c: Distance(g1) = 19
    c: Coincident(g3,g1)
    c: Horizontal(g3)
    c: Distance(g3) = 105
    c: Coincident(g4,g2)
    c: Horizontal(g4)
    c: Distance(g4) = 1.61553
    c: Horizontal(g5)
    c: Equal(g4,g5) = 1.61553
    c: Coincident(g5,g3)
    c: Block(g6)
    c: Coincident(g6,g5)
    c: Coincident(g7,g4)
    c: Coincident(g7,g6)
    c: Vertical(g7)
FEATURE [Part::Extrusion] Extrude028  label="sideB"
  Base = -> Sketch037
  Dir = (0,0,1)
  DirMode = 2
  FaceMakerClass = Part::FaceMakerBullseye
  LengthFwd = 3
  LengthRev = 0
  Placement = pos=(0,0,72) rot=(0,0,1;0rad)
  Solid = true
  Symmetric = false
FEATURE [Sketcher::SketchObject] Sketch038  label="topSketch010"
  FullyConstrained = true
  sketch-geometry (22):
    g0: LineSegment StartX=5.21097e-06 StartY=3 StartZ=0 EndX=5.21097e-06 EndY=19 EndZ=0
    g1: ArcOfCircle CenterX=19 CenterY=19 CenterZ=0 NormalX=0 NormalY=0 NormalZ=1 AngleXU=0 Radius=19 StartAngle=1.5708 EndAngle=3.14159
    g2: ArcOfCircle CenterX=19 CenterY=19 CenterZ=0 NormalX=0 NormalY=0 NormalZ=1 AngleXU=0 Radius=16 StartAngle=1.5708 EndAngle=3.14159
    g3: LineSegment StartX=114 StartY=35 StartZ=0 EndX=19 EndY=35 EndZ=0
    g4: LineSegment StartX=5.21097e-06 StartY=3 StartZ=0 EndX=5.21097e-06 EndY=0 EndZ=0
    g5: LineSegment StartX=3 StartY=0 StartZ=0 EndX=5.21097e-06 EndY=0 EndZ=0
    g6: LineSegment StartX=3 StartY=19 StartZ=0 EndX=3 EndY=0 EndZ=0
    g7: LineSegment StartX=19 StartY=38 StartZ=0 EndX=124 EndY=38 EndZ=0
    g8: Circle CenterX=119 CenterY=35 CenterZ=0 NormalX=0 NormalY=0 NormalZ=1 AngleXU=0 Radius=1
    g9: Circle CenterX=121 CenterY=35 CenterZ=0 NormalX=0 NormalY=0 NormalZ=1 AngleXU=0 Radius=1
    g10: Circle CenterX=121 CenterY=33 CenterZ=0 NormalX=0 NormalY=0 NormalZ=1 AngleXU=0 Radius=1
    g11: BSplineCurve PolesCount=3 KnotsCount=2 Degree=2 IsPeriodic=0
    g12: GeomPoint X=119 Y=35 Z=0
    g13: GeomPoint X=121 Y=33 Z=0
    g14: LineSegment StartX=119 StartY=35 StartZ=0 EndX=114 EndY=35 EndZ=0
    g15: ArcOfCircle CenterX=105 CenterY=19 CenterZ=0 NormalX=0 NormalY=0 NormalZ=1 AngleXU=0 Radius=16 StartAngle=5.60905 EndAngle=6.28319
    g16: LineSegment StartX=121 StartY=33 StartZ=0 EndX=121 EndY=19 EndZ=0
    g17: LineSegment StartX=117.5 StartY=9.01251 StartZ=0 EndX=121.163 EndY=9.0125 EndZ=0
    g18: ArcOfCircle CenterX=105 CenterY=19 CenterZ=0 NormalX=0 NormalY=0 NormalZ=1 AngleXU=0 Radius=20.6155 StartAngle=5.7297 EndAngle=6.28319
    g19: LineSegment StartX=121.163 StartY=9.0125 StartZ=0 EndX=122.538 EndY=8.16329 EndZ=0
    g20: LineSegment StartX=124 StartY=38 StartZ=0 EndX=125.616 EndY=38 EndZ=0
    g21: LineSegment StartX=125.616 StartY=19 StartZ=0 EndX=125.616 EndY=38 EndZ=0
  constraints (49):
    c: Vertical(g0)
    c: Block(g0)
    c: Coincident(g1,g0)
    c: Block(g1)
    c: Coincident(g2,g1)
    c: Block(g2)
    c: Coincident(g3,g2)
    c: Horizontal(g3)
    c: Tangent(g3,g2)
    c: Coincident(g4,g0)
    c: Distance(g4) = 3
    c: Vertical(g4)
    c: Coincident(g5,g4)
    c: Horizontal(g5)
    c: Coincident(g6,g2)
    c: Coincident(g6,g5)
    c: Vertical(g6)
    c: Horizontal(g7)
    c: Distance(g7) = 105
    c: Coincident(g7,g1)
    c: Block(g3)
    c: Weight(g8) = 1
    c: Equal(g8,g9)
    c: Equal(g8,g10)
    c: InternalAlignment(g8,g11)
    c: InternalAlignment(g9,g11)
    c: InternalAlignment(g10,g11)
    c: InternalAlignment(g12,g11)
    c: InternalAlignment(g13,g11)
    c: Block(g11)
    c: Coincident(g14,g11)
    c: Coincident(g14,g3)
    c: Horizontal(g14)
    c: Block(g15)
    c: Coincident(g16,g11)
    c: Coincident(g16,g15)
    c: Vertical(g16)
    c: Distance(g16) = 14
    c: Coincident(g17,g15)
    c: Block(g18)
    c: Coincident(g19,g18)
    c: Coincident(g20,g7)
    c: Horizontal(g20)
    c: Vertical(g21)
    c: Coincident(g20,g21)
    c: Block(g20)
    c: Block(g21)
    c: Block(g19)
    c: Block(g17)
FEATURE [Part::Extrusion] Extrude029
  Base = -> Sketch038
  Dir = (0,0,1)
  DirMode = 2
  FaceMakerClass = Part::FaceMakerBullseye
  LengthFwd = 72
  LengthRev = 0
  Solid = true
  Symmetric = false
FEATURE [Part::Feature] Face085
  shape: bbox 4.8 x 25.5 x 2e-07 mm, 1 faces, 0 solids (baked)
FEATURE [Part::Revolution] Revolve089  label="moreFrontCaseScrewPost003"
  Angle = 360
  Axis = (0,1,0)
  Base = (0,0,0)
  FaceMakerClass = Part::FaceMakerBullseye
  Placement = pos=(109.5,4.5,3.5) rot=(0,0,1;0rad)
  Solid = false
  Source = -> Face085
  Symmetric = false
FEATURE [Part::Feature] Face086
  shape: bbox 4.8 x 25.5 x 2e-07 mm, 1 faces, 0 solids (baked)
FEATURE [Part::Revolution] Revolve090  label="moreFrontCaseScrewPost004"
  Angle = 360
  Axis = (0,1,0)
  Base = (0,0,0)
  FaceMakerClass = Part::FaceMakerBullseye
  Placement = pos=(109.5,4.5,68.5) rot=(0,0,1;0rad)
  Solid = false
  Source = -> Face086
  Symmetric = false
FEATURE [Part::Fillet] Fillet026  label="top013"
  Base = -> Extrude029
  Edges = 1 edges r=2: [Edge35]
FEATURE [Sketcher::SketchObject] Sketch039
  FullyConstrained = true
  sketch-geometry (7):
    g0: LineSegment StartX=0 StartY=0 StartZ=0 EndX=0 EndY=6 EndZ=0
    g1: Circle CenterX=0 CenterY=0 CenterZ=0 NormalX=0 NormalY=0 NormalZ=1 AngleXU=0 Radius=1
    g2: Circle CenterX=8 CenterY=6 CenterZ=0 NormalX=0 NormalY=0 NormalZ=1 AngleXU=0 Radius=1
    g3: BSplineCurve PolesCount=3 KnotsCount=2 Degree=2 IsPeriodic=0
    g4: GeomPoint X=0 Y=0 Z=0
    g5: GeomPoint X=8 Y=6 Z=0
    g6: LineSegment StartX=0 StartY=6 StartZ=0 EndX=8 EndY=6 EndZ=0
  constraints (14):
    c: Coincident(g0,g-1)
    c: Distance(g0) = 6
    c: Vertical(g0)
    c: Coincident(g3,g0)
    c: Weight(g1) = 1
    c: Equal(g1,g2)
    c: InternalAlignment(g1,g3)
    c: InternalAlignment(g2,g3)
    c: InternalAlignment(g4,g3)
    c: InternalAlignment(g5,g3)
    c: Block(g3)
    c: Coincident(g6,g0)
    c: Coincident(g6,g3)
    c: Horizontal(g6)
FEATURE [Sketcher::SketchObject] Sketch040
  FullyConstrained = true
  sketch-geometry (7):
    g0: LineSegment StartX=0 StartY=0 StartZ=0 EndX=0 EndY=6 EndZ=0
    g1: Circle CenterX=0 CenterY=0 CenterZ=0 NormalX=0 NormalY=0 NormalZ=1 AngleXU=0 Radius=1
    g2: Circle CenterX=8 CenterY=6 CenterZ=0 NormalX=0 NormalY=0 NormalZ=1 AngleXU=0 Radius=1
    g3: BSplineCurve PolesCount=3 KnotsCount=2 Degree=2 IsPeriodic=0
    g4: GeomPoint X=0 Y=0 Z=0
    g5: GeomPoint X=8 Y=6 Z=0
    g6: LineSegment StartX=0 StartY=6 StartZ=0 EndX=8 EndY=6 EndZ=0
  constraints (14):
    c: Coincident(g0,g-1)
    c: Distance(g0) = 6
    c: Vertical(g0)
    c: Coincident(g3,g0)
    c: Weight(g1) = 1
    c: Equal(g1,g2)
    c: InternalAlignment(g1,g3)
    c: InternalAlignment(g2,g3)
    c: InternalAlignment(g4,g3)
    c: InternalAlignment(g5,g3)
    c: Block(g3)
    c: Coincident(g6,g0)
    c: Coincident(g6,g3)
    c: Horizontal(g6)
FEATURE [Sketcher::SketchObject] Sketch041
  FullyConstrained = true
  sketch-geometry (7):
    g0: LineSegment StartX=0 StartY=0 StartZ=0 EndX=0 EndY=6 EndZ=0
    g1: Circle CenterX=0 CenterY=0 CenterZ=0 NormalX=0 NormalY=0 NormalZ=1 AngleXU=0 Radius=1
    g2: Circle CenterX=8 CenterY=6 CenterZ=0 NormalX=0 NormalY=0 NormalZ=1 AngleXU=0 Radius=1
    g3: BSplineCurve PolesCount=3 KnotsCount=2 Degree=2 IsPeriodic=0
    g4: GeomPoint X=0 Y=0 Z=0
    g5: GeomPoint X=8 Y=6 Z=0
    g6: LineSegment StartX=0 StartY=6 StartZ=0 EndX=8 EndY=6 EndZ=0
  constraints (14):
    c: Coincident(g0,g-1)
    c: Distance(g0) = 6
    c: Vertical(g0)
    c: Coincident(g3,g0)
    c: Weight(g1) = 1
    c: Equal(g1,g2)
    c: InternalAlignment(g1,g3)
    c: InternalAlignment(g2,g3)
    c: InternalAlignment(g4,g3)
    c: InternalAlignment(g5,g3)
    c: Block(g3)
    c: Coincident(g6,g0)
    c: Coincident(g6,g3)
    c: Horizontal(g6)
FEATURE [Sketcher::SketchObject] Sketch042
  FullyConstrained = true
  sketch-geometry (7):
    g0: LineSegment StartX=0 StartY=0 StartZ=0 EndX=0 EndY=6 EndZ=0
    g1: Circle CenterX=0 CenterY=0 CenterZ=0 NormalX=0 NormalY=0 NormalZ=1 AngleXU=0 Radius=1
    g2: Circle CenterX=8 CenterY=6 CenterZ=0 NormalX=0 NormalY=0 NormalZ=1 AngleXU=0 Radius=1
    g3: BSplineCurve PolesCount=3 KnotsCount=2 Degree=2 IsPeriodic=0
    g4: GeomPoint X=0 Y=0 Z=0
    g5: GeomPoint X=8 Y=6 Z=0
    g6: LineSegment StartX=0 StartY=6 StartZ=0 EndX=8 EndY=6 EndZ=0
  constraints (14):
    c: Coincident(g0,g-1)
    c: Distance(g0) = 6
    c: Vertical(g0)
    c: Coincident(g3,g0)
    c: Weight(g1) = 1
    c: Equal(g1,g2)
    c: InternalAlignment(g1,g3)
    c: InternalAlignment(g2,g3)
    c: InternalAlignment(g4,g3)
    c: InternalAlignment(g5,g3)
    c: Block(g3)
    c: Coincident(g6,g0)
    c: Coincident(g6,g3)
    c: Horizontal(g6)
FEATURE [Part::Extrusion] Extrude030  label="caseScrewPillarBracket008"
  Base = -> Sketch039
  Dir = (0,0,1)
  DirMode = 2
  FaceMakerClass = Part::FaceMakerBullseye
  LengthFwd = 2.4
  LengthRev = 0
  Placement = pos=(15.76,29,8.8) rot=(0,1,0;0rad)
  Solid = true
  Symmetric = false
FEATURE [Part::Extrusion] Extrude031  label="caseScrewPillarBracket009"
  Base = -> Sketch040
  Dir = (0,0,1)
  DirMode = 2
  FaceMakerClass = Part::FaceMakerBullseye
  LengthFwd = 2.4
  LengthRev = 0
  Placement = pos=(15.76,29,60.8) rot=(0,0,1;0rad)
  Solid = true
  Symmetric = false
FEATURE [Part::Extrusion] Extrude032  label="caseScrewPillarBracket010"
  Base = -> Sketch041
  Dir = (0,0,1)
  DirMode = 2
  FaceMakerClass = Part::FaceMakerBullseye
  LengthFwd = 2.4
  LengthRev = 0
  Placement = pos=(13.7,29,13.26) rot=(0,-1,0;1.5708rad)
  Solid = true
  Symmetric = false
FEATURE [Part::Extrusion] Extrude033  label="caseScrewPillarBracket011"
  Base = -> Sketch042
  Dir = (0,0,1)
  DirMode = 2
  FaceMakerClass = Part::FaceMakerBullseye
  LengthFwd = 2.4
  LengthRev = 0
  Placement = pos=(11.3,29,58.74) rot=(0,1,0;1.5708rad)
  Solid = true
  Symmetric = false
FEATURE [Sketcher::SketchObject] Sketch043
  FullyConstrained = true
  sketch-geometry (7):
    g0: LineSegment StartX=0 StartY=0 StartZ=0 EndX=0 EndY=6 EndZ=0
    g1: Circle CenterX=0 CenterY=0 CenterZ=0 NormalX=0 NormalY=0 NormalZ=1 AngleXU=0 Radius=1
    g2: Circle CenterX=8 CenterY=6 CenterZ=0 NormalX=0 NormalY=0 NormalZ=1 AngleXU=0 Radius=1
    g3: BSplineCurve PolesCount=3 KnotsCount=2 Degree=2 IsPeriodic=0
    g4: GeomPoint X=0 Y=0 Z=0
    g5: GeomPoint X=8 Y=6 Z=0
    g6: LineSegment StartX=0 StartY=6 StartZ=0 EndX=8 EndY=6 EndZ=0
  constraints (14):
    c: Coincident(g0,g-1)
    c: Distance(g0) = 6
    c: Vertical(g0)
    c: Coincident(g3,g0)
    c: Weight(g1) = 1
    c: Equal(g1,g2)
    c: InternalAlignment(g1,g3)
    c: InternalAlignment(g2,g3)
    c: InternalAlignment(g4,g3)
    c: InternalAlignment(g5,g3)
    c: Block(g3)
    c: Coincident(g6,g0)
    c: Coincident(g6,g3)
    c: Horizontal(g6)
FEATURE [Part::Extrusion] Extrude034  label="caseScrewPillarBracket012"
  Base = -> Sketch043
  Dir = (0,0,1)
  DirMode = 2
  FaceMakerClass = Part::FaceMakerBullseye
  LengthFwd = 2.4
  LengthRev = 0
  Placement = pos=(88.3,29,65.23) rot=(0,1,0;1.5708rad)
  Solid = true
  Symmetric = false
FEATURE [Sketcher::SketchObject] Sketch044
  FullyConstrained = true
  sketch-geometry (7):
    g0: LineSegment StartX=0 StartY=0 StartZ=0 EndX=0 EndY=6 EndZ=0
    g1: Circle CenterX=0 CenterY=0 CenterZ=0 NormalX=0 NormalY=0 NormalZ=1 AngleXU=0 Radius=1
    g2: Circle CenterX=8 CenterY=6 CenterZ=0 NormalX=0 NormalY=0 NormalZ=1 AngleXU=0 Radius=1
    g3: BSplineCurve PolesCount=3 KnotsCount=2 Degree=2 IsPeriodic=0
    g4: GeomPoint X=0 Y=0 Z=0
    g5: GeomPoint X=8 Y=6 Z=0
    g6: LineSegment StartX=0 StartY=6 StartZ=0 EndX=8 EndY=6 EndZ=0
  constraints (14):
    c: Coincident(g0,g-1)
    c: Distance(g0) = 6
    c: Vertical(g0)
    c: Coincident(g3,g0)
    c: Weight(g1) = 1
    c: Equal(g1,g2)
    c: InternalAlignment(g1,g3)
    c: InternalAlignment(g2,g3)
    c: InternalAlignment(g4,g3)
    c: InternalAlignment(g5,g3)
    c: Block(g3)
    c: Coincident(g6,g0)
    c: Coincident(g6,g3)
    c: Horizontal(g6)
FEATURE [Part::Extrusion] Extrude035  label="caseScrewPillarBracket013"
  Base = -> Sketch044
  Dir = (0,0,1)
  DirMode = 2
  FaceMakerClass = Part::FaceMakerBullseye
  LengthFwd = 2.4
  LengthRev = 0
  Placement = pos=(90.7,29,6.77) rot=(0,-1,0;1.5708rad)
  Solid = true
  Symmetric = false
FEATURE [Sketcher::SketchObject] Sketch045
  FullyConstrained = true
  sketch-geometry (7):
    g0: LineSegment StartX=0 StartY=0 StartZ=0 EndX=0 EndY=6 EndZ=0
    g1: Circle CenterX=0 CenterY=0 CenterZ=0 NormalX=0 NormalY=0 NormalZ=1 AngleXU=0 Radius=1
    g2: Circle CenterX=8 CenterY=6 CenterZ=0 NormalX=0 NormalY=0 NormalZ=1 AngleXU=0 Radius=1
    g3: BSplineCurve PolesCount=3 KnotsCount=2 Degree=2 IsPeriodic=0
    g4: GeomPoint X=0 Y=0 Z=0
    g5: GeomPoint X=8 Y=6 Z=0
    g6: LineSegment StartX=0 StartY=6 StartZ=0 EndX=8 EndY=6 EndZ=0
  constraints (14):
    c: Coincident(g0,g-1)
    c: Distance(g0) = 6
    c: Vertical(g0)
    c: Coincident(g3,g0)
    c: Weight(g1) = 1
    c: Equal(g1,g2)
    c: InternalAlignment(g1,g3)
    c: InternalAlignment(g2,g3)
    c: InternalAlignment(g4,g3)
    c: InternalAlignment(g5,g3)
    c: Block(g3)
    c: Coincident(g6,g0)
    c: Coincident(g6,g3)
    c: Horizontal(g6)
FEATURE [Sketcher::SketchObject] Sketch046
  FullyConstrained = true
  sketch-geometry (7):
    g0: LineSegment StartX=0 StartY=0 StartZ=0 EndX=0 EndY=6 EndZ=0
    g1: Circle CenterX=0 CenterY=0 CenterZ=0 NormalX=0 NormalY=0 NormalZ=1 AngleXU=0 Radius=1
    g2: Circle CenterX=8 CenterY=6 CenterZ=0 NormalX=0 NormalY=0 NormalZ=1 AngleXU=0 Radius=1
    g3: BSplineCurve PolesCount=3 KnotsCount=2 Degree=2 IsPeriodic=0
    g4: GeomPoint X=0 Y=0 Z=0
    g5: GeomPoint X=8 Y=6 Z=0
    g6: LineSegment StartX=0 StartY=6 StartZ=0 EndX=8 EndY=6 EndZ=0
  constraints (14):
    c: Coincident(g0,g-1)
    c: Distance(g0) = 6
    c: Vertical(g0)
    c: Coincident(g3,g0)
    c: Weight(g1) = 1
    c: Equal(g1,g2)
    c: InternalAlignment(g1,g3)
    c: InternalAlignment(g2,g3)
    c: InternalAlignment(g4,g3)
    c: InternalAlignment(g5,g3)
    c: Block(g3)
    c: Coincident(g6,g0)
    c: Coincident(g6,g3)
    c: Horizontal(g6)
FEATURE [Part::Extrusion] Extrude036  label="caseScrewPillarBracket014"
  Base = -> Sketch045
  Dir = (0,0,1)
  DirMode = 2
  FaceMakerClass = Part::FaceMakerBullseye
  LengthFwd = 2.4
  LengthRev = 0
  Placement = pos=(110.7,29,6.77) rot=(0,-1,0;1.5708rad)
  Solid = true
  Symmetric = false
FEATURE [Part::Extrusion] Extrude037  label="caseScrewPillarBracket015"
  Base = -> Sketch046
  Dir = (0,0,1)
  DirMode = 2
  FaceMakerClass = Part::FaceMakerBullseye
  LengthFwd = 2.4
  LengthRev = 0
  Placement = pos=(108.3,29,65.23) rot=(0,1,0;1.5708rad)
  Solid = true
  Symmetric = false
FEATURE [Part::Box] Box013  label="frontCaseScrewPillarBracket002"
  AttacherType = Attacher::AttachEngine3D
  Height = 2.4
  Length = 22
  Placement = pos=(87,28,2.3) rot=(0,0,1;0rad)
  Width = 7
FEATURE [Part::Box] Box014  label="frontCaseScrewPillarBracket003"
  AttacherType = Attacher::AttachEngine3D
  Height = 2.4
  Length = 22
  Placement = pos=(87,28,67.3) rot=(0,0,1;0rad)
  Width = 7
FEATURE [Part::Feature] Face087
  shape: bbox 4.8 x 30.2 x 2e-07 mm, 1 faces, 0 solids (baked)
FEATURE [Part::Revolution] Revolve091  label="frontCaseScrewPost004"
  Angle = 360
  Axis = (0,1,0)
  Base = (0,0,0)
  FaceMakerClass = Part::FaceMakerBullseye
  Placement = pos=(89.5,4.5,3.5) rot=(0,0,1;0rad)
  Solid = false
  Source = -> Face087
  Symmetric = false
FEATURE [Part::Feature] Face088
  shape: bbox 4.8 x 30.2 x 2e-07 mm, 1 faces, 0 solids (baked)
FEATURE [Part::Revolution] Revolve092  label="frontCaseScrewPost005"
  Angle = 360
  Axis = (0,1,0)
  Base = (0,0,0)
  FaceMakerClass = Part::FaceMakerBullseye
  Placement = pos=(89.5,4.5,68.5) rot=(0,0,1;0rad)
  Solid = false
  Source = -> Face088
  Symmetric = false
FEATURE [Part::Feature] Face089
  shape: bbox 3.5 x 30.2 x 2e-07 mm, 1 faces, 0 solids (baked)
FEATURE [Part::Revolution] Revolve093  label="backCaseScrewPost002"
  Angle = 360
  Axis = (0,1,0)
  Base = (0,0,0)
  FaceMakerClass = Part::FaceMakerBullseye
  Placement = pos=(12.5,4.5,10) rot=(0,0,1;0rad)
  Solid = false
  Source = -> Face089
  Symmetric = false
FEATURE [Part::Feature] Face090
  shape: bbox 3.5 x 30.2 x 2e-07 mm, 1 faces, 0 solids (baked)
FEATURE [Part::Revolution] Revolve094  label="backCaseScrewPost003"
  Angle = 360
  Axis = (0,1,0)
  Base = (0,0,0)
  FaceMakerClass = Part::FaceMakerBullseye
  Placement = pos=(12.5,4.5,62) rot=(0,0,1;0rad)
  Solid = false
  Source = -> Face090
  Symmetric = false
FEATURE [Part::Box] Box015  label="Cube011"
  AttacherType = Attacher::AttachEngine3D
  Height = 28.8
  Length = 3
  Placement = pos=(107.3,28,21.6) rot=(0,0,1;0rad)
  Width = 7
FEATURE [Part::Box] Box016  label="Cube012"
  AttacherType = Attacher::AttachEngine3D
  Height = 3
  Length = 7.4
  Placement = pos=(107.3,28,18.6) rot=(0,0,1;0rad)
  Width = 7
FEATURE [Part::Box] Box017  label="Cube013"
  AttacherType = Attacher::AttachEngine3D
  Height = 3
  Length = 7.4
  Placement = pos=(107.3,28,50.4) rot=(0,0,1;0rad)
  Width = 7
FEATURE [Part::Cylinder] Cylinder024
  Angle = 360
  AttacherType = Attacher::AttachEngine3D
  Height = 20
  Placement = pos=(0,0,36.15) rot=(0,0,1;0rad)
  Radius = 14.3
FEATURE [Part::Cylinder] Cylinder025
  Angle = 360
  AttacherType = Attacher::AttachEngine3D
  Height = 10
  Placement = pos=(0,0,36.15) rot=(0,0,1;0rad)
  Radius = 4
FEATURE [Part::MultiFuse] Fusion066  label="removeToCreteHoleForPlugHousing009"
  Placement = pos=(70,19,36) rot=(0,1,0;1.5708rad)
  Shapes = -> [Cylinder024,Cylinder025]
FEATURE [Part::MultiFuse] Fusion065  label="plugHousingBracketHolder002"
  Shapes = -> [Box017,Box015,Box016]
FEATURE [Part::Cut] Cut025  label="plugHousingBracketHolder003"
  Base = -> Fusion065
  Placement = pos=(7,0,0) rot=(0,0,1;0rad)
  Tool = -> Fusion066
FEATURE [Sketcher::SketchObject] Sketch047
  FullyConstrained = false
  Placement = pos=(0,0,0) rot=(1,0,0;1.5708rad)
  sketch-geometry (24):
    g0: ArcOfCircle CenterX=-4 CenterY=-10.5 CenterZ=0 NormalX=0 NormalY=0 NormalZ=1 AngleXU=0 Radius=1.5 StartAngle=6e-16 EndAngle=3.14159
    g1: ArcOfCircle CenterX=-34.2 CenterY=-10.5 CenterZ=0 NormalX=0 NormalY=0 NormalZ=1 AngleXU=0 Radius=1.5 StartAngle=0 EndAngle=3.14159
    g2: ArcOfCircle CenterX=-34.2 CenterY=-27.7 CenterZ=0 NormalX=0 NormalY=0 NormalZ=1 AngleXU=0 Radius=1.5 StartAngle=3.14159 EndAngle=6.28319
    g3: ArcOfCircle CenterX=-4 CenterY=-27.7 CenterZ=0 NormalX=0 NormalY=0 NormalZ=1 AngleXU=0 Radius=1.5 StartAngle=3.1416 EndAngle=6.28319
    g4: ArcOfCircle CenterX=-10 CenterY=-4.3 CenterZ=0 NormalX=0 NormalY=0 NormalZ=1 AngleXU=0 Radius=1.5 StartAngle=2e-16 EndAngle=3.14159
    g5: ArcOfCircle CenterX=-16.1 CenterY=-1.8 CenterZ=0 NormalX=0 NormalY=0 NormalZ=1 AngleXU=0 Radius=1.5 StartAngle=5e-16 EndAngle=3.14159
    g6: ArcOfCircle CenterX=-22.1 CenterY=-1.8 CenterZ=0 NormalX=0 NormalY=0 NormalZ=1 AngleXU=0 Radius=1.5 StartAngle=5e-16 EndAngle=3.14159
    g7: ArcOfCircle CenterX=-28.2 CenterY=-4.3 CenterZ=0 NormalX=0 NormalY=0 NormalZ=1 AngleXU=0 Radius=1.5 StartAngle=2e-16 EndAngle=3.14159
    g8: ArcOfCircle CenterX=-10 CenterY=-33.9 CenterZ=0 NormalX=0 NormalY=0 NormalZ=1 AngleXU=0 Radius=1.5 StartAngle=3.14159 EndAngle=6.28319
    g9: ArcOfCircle CenterX=-16.1 CenterY=-36.4 CenterZ=0 NormalX=0 NormalY=0 NormalZ=1 AngleXU=0 Radius=1.5 StartAngle=3.14159 EndAngle=6.28319
    g10: ArcOfCircle CenterX=-22.1 CenterY=-36.4 CenterZ=0 NormalX=0 NormalY=0 NormalZ=1 AngleXU=0 Radius=1.5 StartAngle=3.14159 EndAngle=6.28319
    g11: ArcOfCircle CenterX=-28.2 CenterY=-33.9 CenterZ=0 NormalX=0 NormalY=0 NormalZ=1 AngleXU=0 Radius=1.5 StartAngle=3.14159 EndAngle=6.28319
    g12: LineSegment StartX=-35.7 StartY=-10.5 StartZ=0 EndX=-35.7 EndY=-27.7 EndZ=0
    g13: LineSegment StartX=-32.7 StartY=-10.5 StartZ=0 EndX=-32.7 EndY=-27.7 EndZ=0
    g14: LineSegment StartX=-29.7 StartY=-33.9 StartZ=0 EndX=-29.7 EndY=-4.3 EndZ=0
    g15: LineSegment StartX=-26.7 StartY=-33.9 StartZ=0 EndX=-26.7 EndY=-4.3 EndZ=0
    g16: LineSegment StartX=-2.5 StartY=-10.5 StartZ=0 EndX=-2.5 EndY=-27.7 EndZ=0
    g17: LineSegment StartX=-8.5 StartY=-4.3 StartZ=0 EndX=-8.5 EndY=-33.9 EndZ=0
    g18: LineSegment StartX=-5.5 StartY=-10.5 StartZ=0 EndX=-5.5 EndY=-27.7 EndZ=0
    g19: LineSegment StartX=-11.5 StartY=-4.3 StartZ=0 EndX=-11.5 EndY=-33.9 EndZ=0
    g20: LineSegment StartX=-14.6 StartY=-1.8 StartZ=0 EndX=-14.6 EndY=-36.4 EndZ=0
    g21: LineSegment StartX=-17.6 StartY=-1.8 StartZ=0 EndX=-17.6 EndY=-36.4 EndZ=0
    g22: LineSegment StartX=-20.6 StartY=-36.4 StartZ=0 EndX=-20.6 EndY=-1.8 EndZ=0
    g23: LineSegment StartX=-23.6 StartY=-1.8 StartZ=0 EndX=-23.6 EndY=-36.4 EndZ=0
  constraints (48):
    c: Block(g0)
    c: Block(g1)
    c: Block(g2)
    c: Block(g3)
    c: Block(g4)
    c: Block(g5)
    c: Block(g6)
    c: Block(g7)
    c: Block(g8)
    c: Block(g9)
    c: Block(g10)
    c: Block(g11)
    c: Coincident(g12,g1)
    c: Coincident(g12,g2)
    c: Vertical(g12)
    c: Coincident(g13,g1)
    c: Coincident(g13,g2)
    c: Vertical(g13)
    c: Coincident(g14,g11)
    c: Coincident(g14,g7)
    c: Vertical(g14)
    c: Coincident(g15,g11)
    c: Coincident(g15,g7)
    c: Vertical(g15)
    c: Coincident(g16,g0)
    c: Coincident(g16,g3)
    c: Vertical(g16)
    c: Coincident(g17,g4)
    c: Coincident(g17,g8)
    c: Vertical(g17)
    c: Coincident(g18,g0)
    c: Coincident(g18,g3)
    c: Vertical(g18)
    c: Coincident(g19,g4)
    c: Coincident(g19,g8)
    c: Vertical(g19)
    c: Coincident(g20,g5)
    c: Coincident(g20,g9)
    c: Vertical(g20)
    c: Coincident(g21,g5)
    c: Coincident(g21,g9)
    c: Vertical(g21)
    c: Coincident(g22,g10)
    c: Coincident(g22,g6)
    c: Vertical(g22)
    c: Coincident(g23,g6)
    c: Coincident(g23,g10)
    c: Vertical(g23)
FEATURE [Part::Extrusion] Extrude038  label="removeToCreateFanGrillHoles001"
  Base = -> Sketch047
  Dir = (0,-1,6e-16)
  DirMode = 2
  FaceMakerClass = Part::FaceMakerBullseye
  LengthFwd = 10
  LengthRev = 0
  Placement = pos=(65.4,44,54.82) rot=(0,0,1;0rad)
  Solid = true
  Symmetric = false
FEATURE [Part::Feature] Wire004
  shape: bbox 11 x 5.2 x 2e-07 mm, 0 faces, 0 solids (baked)
FEATURE [Part::Revolution] Revolve095
  Angle = 360
  Axis = (0,1,0)
  Base = (0,0,0)
  FaceMakerClass = Part::FaceMakerBullseye
  Placement = pos=(30.3,38,19.7) rot=(0,0,1;0rad)
  Solid = true
  Source = -> Wire004
  Symmetric = false
FEATURE [Part::Feature] Wire005
  shape: bbox 11 x 5.2 x 2e-07 mm, 0 faces, 0 solids (baked)
FEATURE [Part::Revolution] Revolve096
  Angle = 360
  Axis = (0,1,0)
  Base = (0,0,0)
  FaceMakerClass = Part::FaceMakerBullseye
  Placement = pos=(30.3,38,51.7) rot=(0,0,1;0rad)
  Solid = true
  Source = -> Wire005
  Symmetric = false
FEATURE [Part::Feature] Wire006
  shape: bbox 11 x 5.2 x 2e-07 mm, 0 faces, 0 solids (baked)
FEATURE [Part::Revolution] Revolve097
  Angle = 360
  Axis = (0,1,0)
  Base = (0,0,0)
  FaceMakerClass = Part::FaceMakerBullseye
  Placement = pos=(62.3,38,51.7) rot=(0,0,1;0rad)
  Solid = true
  Source = -> Wire006
  Symmetric = false
FEATURE [Part::Feature] Wire007
  shape: bbox 11 x 5.2 x 2e-07 mm, 0 faces, 0 solids (baked)
FEATURE [Part::Revolution] Revolve098
  Angle = 360
  Axis = (0,1,0)
  Base = (0,0,0)
  FaceMakerClass = Part::FaceMakerBullseye
  Placement = pos=(62.3,38,19.7) rot=(0,0,1;0rad)
  Solid = true
  Source = -> Wire007
  Symmetric = false
FEATURE [Part::MultiFuse] Fusion067  label="fanScrewHousing002"
  Shapes = -> [Revolve098,Revolve097,Revolve096,Revolve095]
FEATURE [Part::Feature] Face091 .. Face094  x4 (patterned run collapsed; names and placements below)
  shape: bbox 3.5 x 17.8 x 2e-07 mm, 1 faces, 0 solids (baked)
FEATURE [Part::Revolution] Revolve099  label="removeToCreateScrewAndThreadedInsertHole026"
  Angle = 360
  Axis = (0,1,0)
  Base = (0,0,0)
  FaceMakerClass = Part::FaceMakerBullseye
  Placement = pos=(62.3,30.3,19.7) rot=(0,0,1;0rad)
  Solid = false
  Source = -> Face091
  Symmetric = false
FEATURE [Part::Revolution] Revolve100  label="removeToCreateScrewAndThreadedInsertHole027"
  Angle = 360
  Axis = (0,1,0)
  Base = (0,0,0)
  FaceMakerClass = Part::FaceMakerBullseye
  Placement = pos=(62.3,30.3,51.7) rot=(0,0,1;0rad)
  Solid = false
  Source = -> Face092
  Symmetric = false
FEATURE [Part::Revolution] Revolve101  label="removeToCreateScrewAndThreadedInsertHole028"
  Angle = 360
  Axis = (0,1,0)
  Base = (0,0,0)
  FaceMakerClass = Part::FaceMakerBullseye
  Placement = pos=(30.3,30.3,19.7) rot=(0,0,1;0rad)
  Solid = false
  Source = -> Face093
  Symmetric = false
FEATURE [Part::Revolution] Revolve102  label="removeToCreateScrewAndThreadedInsertHole029"
  Angle = 360
  Axis = (0,1,0)
  Base = (0,0,0)
  FaceMakerClass = Part::FaceMakerBullseye
  Placement = pos=(30.3,30.3,51.7) rot=(0,0,1;0rad)
  Solid = false
  Source = -> Face094
  Symmetric = false
FEATURE [Part::MultiFuse] Fusion068  label="createThreadedInsertHolesForFan002"
  Shapes = -> [Revolve099,Revolve100,Revolve101,Revolve102]
FEATURE [Part::Cut] Cut026  label="fanScrewHousing003"
  Base = -> Fusion067
  Tool = -> Fusion068
FEATURE [Sketcher::SketchObject] Sketch048
  FullyConstrained = false
  Placement = pos=(0,0,0) rot=(1,0,0;1.5708rad)
  sketch-geometry (24):
    g0: ArcOfCircle CenterX=-4 CenterY=-10.5 CenterZ=0 NormalX=0 NormalY=0 NormalZ=1 AngleXU=0 Radius=1.5 StartAngle=6e-16 EndAngle=3.14159
    g1: ArcOfCircle CenterX=-34.2 CenterY=-10.5 CenterZ=0 NormalX=0 NormalY=0 NormalZ=1 AngleXU=0 Radius=1.5 StartAngle=0 EndAngle=3.14159
    g2: ArcOfCircle CenterX=-34.2 CenterY=-27.7 CenterZ=0 NormalX=0 NormalY=0 NormalZ=1 AngleXU=0 Radius=1.5 StartAngle=3.14159 EndAngle=6.28319
    g3: ArcOfCircle CenterX=-4 CenterY=-27.7 CenterZ=0 NormalX=0 NormalY=0 NormalZ=1 AngleXU=0 Radius=1.5 StartAngle=3.1416 EndAngle=6.28319
    g4: ArcOfCircle CenterX=-10 CenterY=-4.3 CenterZ=0 NormalX=0 NormalY=0 NormalZ=1 AngleXU=0 Radius=1.5 StartAngle=2e-16 EndAngle=3.14159
    g5: ArcOfCircle CenterX=-16.1 CenterY=-1.8 CenterZ=0 NormalX=0 NormalY=0 NormalZ=1 AngleXU=0 Radius=1.5 StartAngle=5e-16 EndAngle=3.14159
    g6: ArcOfCircle CenterX=-22.1 CenterY=-1.8 CenterZ=0 NormalX=0 NormalY=0 NormalZ=1 AngleXU=0 Radius=1.5 StartAngle=5e-16 EndAngle=3.14159
    g7: ArcOfCircle CenterX=-28.2 CenterY=-4.3 CenterZ=0 NormalX=0 NormalY=0 NormalZ=1 AngleXU=0 Radius=1.5 StartAngle=2e-16 EndAngle=3.14159
    g8: ArcOfCircle CenterX=-10 CenterY=-33.9 CenterZ=0 NormalX=0 NormalY=0 NormalZ=1 AngleXU=0 Radius=1.5 StartAngle=3.14159 EndAngle=6.28319
    g9: ArcOfCircle CenterX=-16.1 CenterY=-36.4 CenterZ=0 NormalX=0 NormalY=0 NormalZ=1 AngleXU=0 Radius=1.5 StartAngle=3.14159 EndAngle=6.28319
    g10: ArcOfCircle CenterX=-22.1 CenterY=-36.4 CenterZ=0 NormalX=0 NormalY=0 NormalZ=1 AngleXU=0 Radius=1.5 StartAngle=3.14159 EndAngle=6.28319
    g11: ArcOfCircle CenterX=-28.2 CenterY=-33.9 CenterZ=0 NormalX=0 NormalY=0 NormalZ=1 AngleXU=0 Radius=1.5 StartAngle=3.14159 EndAngle=6.28319
    g12: LineSegment StartX=-35.7 StartY=-10.5 StartZ=0 EndX=-35.7 EndY=-27.7 EndZ=0
    g13: LineSegment StartX=-32.7 StartY=-10.5 StartZ=0 EndX=-32.7 EndY=-27.7 EndZ=0
    g14: LineSegment StartX=-29.7 StartY=-33.9 StartZ=0 EndX=-29.7 EndY=-4.3 EndZ=0
    g15: LineSegment StartX=-26.7 StartY=-33.9 StartZ=0 EndX=-26.7 EndY=-4.3 EndZ=0
    g16: LineSegment StartX=-2.5 StartY=-10.5 StartZ=0 EndX=-2.5 EndY=-27.7 EndZ=0
    g17: LineSegment StartX=-8.5 StartY=-4.3 StartZ=0 EndX=-8.5 EndY=-33.9 EndZ=0
    g18: LineSegment StartX=-5.5 StartY=-10.5 StartZ=0 EndX=-5.5 EndY=-27.7 EndZ=0
    g19: LineSegment StartX=-11.5 StartY=-4.3 StartZ=0 EndX=-11.5 EndY=-33.9 EndZ=0
    g20: LineSegment StartX=-14.6 StartY=-1.8 StartZ=0 EndX=-14.6 EndY=-36.4 EndZ=0
    g21: LineSegment StartX=-17.6 StartY=-1.8 StartZ=0 EndX=-17.6 EndY=-36.4 EndZ=0
    g22: LineSegment StartX=-20.6 StartY=-36.4 StartZ=0 EndX=-20.6 EndY=-1.8 EndZ=0
    g23: LineSegment StartX=-23.6 StartY=-1.8 StartZ=0 EndX=-23.6 EndY=-36.4 EndZ=0
  constraints (48):
    c: Block(g0)
    c: Block(g1)
    c: Block(g2)
    c: Block(g3)
    c: Block(g4)
    c: Block(g5)
    c: Block(g6)
    c: Block(g7)
    c: Block(g8)
    c: Block(g9)
    c: Block(g10)
    c: Block(g11)
    c: Coincident(g12,g1)
    c: Coincident(g12,g2)
    c: Vertical(g12)
    c: Coincident(g13,g1)
    c: Coincident(g13,g2)
    c: Vertical(g13)
    c: Coincident(g14,g11)
    c: Coincident(g14,g7)
    c: Vertical(g14)
    c: Coincident(g15,g11)
    c: Coincident(g15,g7)
    c: Vertical(g15)
    c: Coincident(g16,g0)
    c: Coincident(g16,g3)
    c: Vertical(g16)
    c: Coincident(g17,g4)
    c: Coincident(g17,g8)
    c: Vertical(g17)
    c: Coincident(g18,g0)
    c: Coincident(g18,g3)
    c: Vertical(g18)
    c: Coincident(g19,g4)
    c: Coincident(g19,g8)
    c: Vertical(g19)
    c: Coincident(g20,g5)
    c: Coincident(g20,g9)
    c: Vertical(g20)
    c: Coincident(g21,g5)
    c: Coincident(g21,g9)
    c: Vertical(g21)
    c: Coincident(g22,g10)
    c: Coincident(g22,g6)
    c: Vertical(g22)
    c: Coincident(g23,g6)
    c: Coincident(g23,g10)
    c: Vertical(g23)
FEATURE [Part::Extrusion] Extrude039  label="removeToCreateFanGrillHoles002"
  Base = -> Sketch048
  Dir = (0,-1,6e-16)
  DirMode = 2
  FaceMakerClass = Part::FaceMakerBullseye
  LengthFwd = 10
  LengthRev = 0
  Placement = pos=(65.4,44,54.82) rot=(0,0,1;0rad)
  Solid = true
  Symmetric = false
FEATURE [Part::Cut] Cut027  label="fanScrewHousing004"
  Base = -> Cut026
  Tool = -> Extrude038
FEATURE [Part::Cut] Cut028  label="top014"
  Base = -> Fillet026
  Tool = -> Extrude039
FEATURE [Part::Feature] Face095 .. Face098  x4 (patterned run collapsed; names and placements below)
  shape: bbox 3.5 x 17.8 x 2e-07 mm, 1 faces, 0 solids (baked)
FEATURE [Part::Revolution] Revolve103  label="removeToCreateScrewAndThreadedInsertHole030"
  Angle = 360
  Axis = (0,1,0)
  Base = (0,0,0)
  FaceMakerClass = Part::FaceMakerBullseye
  Placement = pos=(62.3,30.3,19.7) rot=(0,0,1;0rad)
  Solid = false
  Source = -> Face095
  Symmetric = false
FEATURE [Part::Revolution] Revolve104  label="removeToCreateScrewAndThreadedInsertHole031"
  Angle = 360
  Axis = (0,1,0)
  Base = (0,0,0)
  FaceMakerClass = Part::FaceMakerBullseye
  Placement = pos=(62.3,30.3,51.7) rot=(0,0,1;0rad)
  Solid = false
  Source = -> Face096
  Symmetric = false
FEATURE [Part::Revolution] Revolve105  label="removeToCreateScrewAndThreadedInsertHole032"
  Angle = 360
  Axis = (0,1,0)
  Base = (0,0,0)
  FaceMakerClass = Part::FaceMakerBullseye
  Placement = pos=(30.3,30.3,19.7) rot=(0,0,1;0rad)
  Solid = false
  Source = -> Face097
  Symmetric = false
FEATURE [Part::Revolution] Revolve106  label="removeToCreateScrewAndThreadedInsertHole033"
  Angle = 360
  Axis = (0,1,0)
  Base = (0,0,0)
  FaceMakerClass = Part::FaceMakerBullseye
  Placement = pos=(30.3,30.3,51.7) rot=(0,0,1;0rad)
  Solid = false
  Source = -> Face098
  Symmetric = false
FEATURE [Part::MultiFuse] Fusion069  label="createThreadedInsertHolesForFan003"
  Shapes = -> [Revolve103,Revolve104,Revolve105,Revolve106]
FEATURE [Part::Cut] Cut029  label="top015"
  Base = -> Cut028
  Tool = -> Fusion054
FEATURE [Part::Cut] Cut030  label="fanScrewHousing005"
  Base = -> Cut027
  Tool = -> Fusion069
FEATURE [Part::Cylinder] Cylinder026  label="removeToCreteHoleForPlugHousing010"
  Angle = 360
  AttacherType = Attacher::AttachEngine3D
  Height = 20
  Placement = pos=(-2,19,36) rot=(0,1,0;1.5708rad)
  Radius = 14.3
FEATURE [Part::Box] Box018  label="removeToCreteHoleForPlugHousing011"
  AttacherType = Attacher::AttachEngine3D
  Height = 28.6
  Length = 10
  Placement = pos=(-2,0,21.7) rot=(0,0,1;0rad)
  Width = 19
FEATURE [Part::Box] Box019  label="wireHolderBottomCaseBit"
  AttacherType = Attacher::AttachEngine3D
  Height = 28
  Length = 3
  Placement = pos=(0,0,22) rot=(0,0,1;0rad)
  Width = 21
FEATURE [Part::Cylinder] Cylinder027  label="removeToCreteHoleForPlugHousing012"
  Angle = 360
  AttacherType = Attacher::AttachEngine3D
  Height = 20
  Placement = pos=(-2,19,36) rot=(0,1,0;1.5708rad)
  Radius = 14.3
FEATURE [Part::Cut] Cut031  label="wireHolderBottomCaseBit001"
  Base = -> Box019
  Tool = -> Cylinder027
FEATURE [Part::MultiFuse] Fusion070  label="removeToCreteHoleForPlugHousing013"
  Shapes = -> [Box018,Cylinder026]
FEATURE [Part::Cut] Cut032  label="top016"
  Base = -> Cut029
  Tool = -> Fusion070
FEATURE [Part::Cylinder] Cylinder028
  Angle = 360
  AttacherType = Attacher::AttachEngine3D
  Height = 20
  Placement = pos=(0,0,36.15) rot=(0,0,1;0rad)
  Radius = 14.3
FEATURE [Part::Cylinder] Cylinder029
  Angle = 360
  AttacherType = Attacher::AttachEngine3D
  Height = 10
  Placement = pos=(0,0,36.15) rot=(0,0,1;0rad)
  Radius = 4
FEATURE [Part::MultiFuse] Fusion071  label="removeToCreteHoleForPlugHousing014"
  Placement = pos=(70,19,36) rot=(0,1,0;1.5708rad)
  Shapes = -> [Cylinder028,Cylinder029]
FEATURE [Sketcher::SketchObject] Sketch049  label="topSketch011"
  FullyConstrained = true
  sketch-geometry (4):
    g0: ArcOfCircle CenterX=105 CenterY=19 CenterZ=0 NormalX=0 NormalY=0 NormalZ=1 AngleXU=0 Radius=20.6155 StartAngle=5.54125 EndAngle=6.28319
    g1: ArcOfCircle CenterX=105 CenterY=19 CenterZ=0 NormalX=0 NormalY=0 NormalZ=1 AngleXU=0 Radius=13 StartAngle=5.54125 EndAngle=6.28319
    g2: LineSegment StartX=118 StartY=19 StartZ=0 EndX=125.616 EndY=19 EndZ=0
    g3: LineSegment StartX=114.583 StartY=10.2157 StartZ=0 EndX=120.197 EndY=5.06982 EndZ=0
  constraints (7):
    c: Block(g0)
    c: Block(g1)
    c: Coincident(g2,g1)
    c: Coincident(g2,g0)
    c: Horizontal(g2)
    c: Coincident(g3,g1)
    c: Coincident(g3,g0)
FEATURE [Part::Box] Box020  label="removeToCreteHoleForPlugHousing015"
  AttacherType = Attacher::AttachEngine3D
  Height = 28.6
  Length = 20
  Placement = pos=(106.15,0,21.7) rot=(0,0,1;0rad)
  Width = 19
FEATURE [Part::MultiFuse] Fusion072  label="removeToCreteHoleForPlugHousing016"
  Shapes = -> [Box020,Fusion071]
FEATURE [Part::Cut] Cut033  label="removeToCreteHoleForPlugHousing017"
  Base = -> Cut032
  Tool = -> Fusion072
FEATURE [Part::Cylinder] Cylinder030
  Angle = 360
  AttacherType = Attacher::AttachEngine3D
  Height = 20
  Placement = pos=(0,0,36.15) rot=(0,0,1;0rad)
  Radius = 14.3
FEATURE [Part::Cylinder] Cylinder031
  Angle = 360
  AttacherType = Attacher::AttachEngine3D
  Height = 10
  Placement = pos=(0,0,36.15) rot=(0,0,1;0rad)
  Radius = 4
FEATURE [Part::Box] Box021  label="removeToCreteHoleForPlugHousing019"
  AttacherType = Attacher::AttachEngine3D
  Height = 28.6
  Length = 20
  Placement = pos=(106.15,0,21.7) rot=(0,0,1;0rad)
  Width = 19
FEATURE [Part::MultiFuse] Fusion074  label="removeToCreteHoleForPlugHousing020"
  Placement = pos=(70,19,36) rot=(0,1,0;1.5708rad)
  Shapes = -> [Cylinder030,Cylinder031]
FEATURE [Part::MultiFuse] Fusion073  label="removeToCreteHoleForPlugHousing018"
  Placement = pos=(0,0,28.3) rot=(0,0,1;0rad)
  Shapes = -> [Box021,Fusion074]
FEATURE [Part::Cylinder] Cylinder032
  Angle = 360
  AttacherType = Attacher::AttachEngine3D
  Height = 20
  Placement = pos=(0,0,36.15) rot=(0,0,1;0rad)
  Radius = 14.3
FEATURE [Part::Cylinder] Cylinder033
  Angle = 360
  AttacherType = Attacher::AttachEngine3D
  Height = 10
  Placement = pos=(0,0,36.15) rot=(0,0,1;0rad)
  Radius = 4
FEATURE [Part::Box] Box022  label="removeToCreteHoleForPlugHousing021"
  AttacherType = Attacher::AttachEngine3D
  Height = 28.6
  Length = 20
  Placement = pos=(106.15,0,21.7) rot=(0,0,1;0rad)
  Width = 19
FEATURE [Part::MultiFuse] Fusion076  label="removeToCreteHoleForPlugHousing023"
  Placement = pos=(70,19,36) rot=(0,1,0;1.5708rad)
  Shapes = -> [Cylinder032,Cylinder033]
FEATURE [Part::MultiFuse] Fusion075  label="removeToCreteHoleForPlugHousing022"
  Placement = pos=(0,0,-28.3) rot=(0,0,1;0rad)
  Shapes = -> [Box022,Fusion076]
FEATURE [Part::MultiFuse] Fusion077  label="removeToCreatePlugHousingBottomBit"
  Shapes = -> [Fusion075,Fusion073]
FEATURE [Part::Cylinder] Cylinder034
  Angle = 360
  AttacherType = Attacher::AttachEngine3D
  Height = 20
  Placement = pos=(0,0,36.15) rot=(0,0,1;0rad)
  Radius = 14
FEATURE [Part::Cylinder] Cylinder035
  Angle = 360
  AttacherType = Attacher::AttachEngine3D
  Height = 10
  Placement = pos=(0,0,36.15) rot=(0,0,1;0rad)
  Radius = 4
FEATURE [Part::MultiFuse] Fusion078  label="removeToCreteHoleForPlugHousing024"
  Placement = pos=(70,19,36) rot=(0,1,0;1.5708rad)
  Shapes = -> [Cylinder034,Cylinder035]
FEATURE [Part::MultiFuse] Fusion079  label="removeToCreatePlugHousingBottomBit001"
  Shapes = -> [Fusion078,Fusion077]
FEATURE [Part::Extrusion] Extrude040  label="bottomPlugHousingBit"
  Base = -> Sketch049
  Dir = (0,0,1)
  DirMode = 2
  FaceMakerClass = Part::FaceMakerBullseye
  LengthFwd = 72
  LengthRev = 0
  Solid = true
  Symmetric = false
FEATURE [Part::Cut] Cut034  label="bottomPlugHousingBit001"
  Base = -> Extrude040
  Placement = pos=(-0.09,0,0) rot=(0,0,1;0rad)
  Tool = -> Fusion079
FEATURE [Part::Box] Box023  label="Cube014"
  AttacherType = Attacher::AttachEngine3D
  Height = 16
  Length = 8
  Placement = pos=(12.7,31.52,28) rot=(0,0,1;0rad)
  Width = 4
FEATURE [Part::Cylinder] Cylinder036
  Angle = 360
  AttacherType = Attacher::AttachEngine3D
  Height = 10
  Placement = pos=(0,0,36.15) rot=(0,0,1;0rad)
  Radius = 4
FEATURE [Part::Cylinder] Cylinder037
  Angle = 360
  AttacherType = Attacher::AttachEngine3D
  Height = 20
  Placement = pos=(0,0,36.15) rot=(0,0,1;0rad)
  Radius = 8.2
FEATURE [Part::MultiFuse] Fusion080  label="removeToCreteHoleForPlugHousing025"
  Placement = pos=(-42,19,36) rot=(0,1,0;1.5708rad)
  Shapes = -> [Cylinder037,Cylinder036]
FEATURE [Sketcher::SketchObject] Sketch050  label="topSketch012"
  FullyConstrained = true
  sketch-geometry (4):
    g0: LineSegment StartX=16.8446 StartY=31.512 StartZ=0 EndX=16.3251 EndY=34.4666 EndZ=0
    g1: ArcOfCircle CenterX=19 CenterY=19.2524 CenterZ=0 NormalX=0 NormalY=0 NormalZ=1 AngleXU=0 Radius=15.4476 StartAngle=1.74483 EndAngle=2.72717
    g2: ArcOfCircle CenterX=19 CenterY=19.2524 CenterZ=0 NormalX=0 NormalY=0 NormalZ=1 AngleXU=0 Radius=12.4476 StartAngle=1.74483 EndAngle=2.73189
    g3: LineSegment StartX=4.86004 StartY=25.4725 StartZ=0 EndX=7.58253 EndY=24.2107 EndZ=0
  constraints (7):
    c: Block(g0)
    c: Coincident(g1,g0)
    c: Coincident(g2,g0)
    c: Coincident(g3,g1)
    c: Coincident(g3,g2)
    c: Block(g1)
    c: Block(g2)
FEATURE [Part::Extrusion] Extrude041
  Base = -> Sketch050
  Dir = (0,0,1)
  DirMode = 2
  FaceMakerClass = Part::FaceMakerBullseye
  LengthFwd = 10.6
  LengthRev = 0
  Placement = pos=(0,0,31) rot=(0,0,1;0rad)
  Solid = true
  Symmetric = false
FEATURE [Part::Cut] Cut035
  Base = -> Extrude041
  Placement = pos=(0,0,-0.3) rot=(0,0,1;0rad)
  Tool = -> Fusion080
FEATURE [Part::Cut] Cut036
  Base = -> Box023
  Tool = -> Cut035
FEATURE [Part::Fillet] Fillet027
  Base = -> Cut036
  Edges = 1 edges r=0.7: [Edge13]
FEATURE [Part::Fillet] Fillet028
  Base = -> Fillet027
  Edges = 1 edges r=0.7: [Edge13]
FEATURE [Part::Fillet] Fillet029
  Base = -> Fillet028
  Edges = 1 edges r=0.7: [Edge16]
FEATURE [Part::Fillet] Fillet030
  Base = -> Fillet029
  Edges = 1 edges r=0.7: [Edge11]
FEATURE [Part::Fillet] Fillet031
  Base = -> Fillet030
  Edges = 1 edges r=0.7: [Edge10]
FEATURE [Part::Fillet] Fillet032
  Base = -> Fillet031
  Edges = 1 edges r=1.2: [Edge5]
FEATURE [Part::Fillet] Fillet033
  Base = -> Fillet032
  Edges = 1 edges r=1.2: [Edge12]
FEATURE [Part::Fillet] Fillet034  label="wireHousingRetainer"
  Base = -> Fillet033
  Edges = 1 edges r=2: [Edge1]
  Placement = pos=(0.3,0,0) rot=(0,0,1;0rad)
FEATURE [Part::Feature] Face099
  shape: bbox 3.5 x 17.8 x 2e-07 mm, 1 faces, 0 solids (baked)
FEATURE [Part::Revolution] Revolve107  label="removeToCreateScrewAndThreadedInsertHole034"
  Angle = 360
  Axis = (0,1,0)
  Base = (0,0,0)
  FaceMakerClass = Part::FaceMakerBullseye
  Placement = pos=(12.5,0,10) rot=(0,0,1;0rad)
  Solid = false
  Source = -> Face099
  Symmetric = false
FEATURE [Part::Feature] Face100
  shape: bbox 3.5 x 17.8 x 2e-07 mm, 1 faces, 0 solids (baked)
FEATURE [Part::Revolution] Revolve108  label="removeToCreateScrewAndThreadedInsertHole035"
  Angle = 360
  Axis = (0,1,0)
  Base = (0,0,0)
  FaceMakerClass = Part::FaceMakerBullseye
  Placement = pos=(12.5,0,62) rot=(0,0,1;0rad)
  Solid = false
  Source = -> Face100
  Symmetric = false
FEATURE [Part::Feature] Face101
  shape: bbox 3.5 x 17.8 x 2e-07 mm, 1 faces, 0 solids (baked)
FEATURE [Part::Revolution] Revolve109  label="removeToCreateScrewAndThreadedInsertHole036"
  Angle = 360
  Axis = (0,1,0)
  Base = (0,0,0)
  FaceMakerClass = Part::FaceMakerBullseye
  Placement = pos=(89.5,0,68.5) rot=(0,0,1;0rad)
  Solid = false
  Source = -> Face101
  Symmetric = false
FEATURE [Part::Feature] Face102
  shape: bbox 3.5 x 17.8 x 2e-07 mm, 1 faces, 0 solids (baked)
FEATURE [Part::Revolution] Revolve110  label="removeToCreateScrewAndThreadedInsertHole037"
  Angle = 360
  Axis = (0,1,0)
  Base = (0,0,0)
  FaceMakerClass = Part::FaceMakerBullseye
  Placement = pos=(89.5,0,3.5) rot=(0,0,1;0rad)
  Solid = false
  Source = -> Face102
  Symmetric = false
FEATURE [Part::Feature] Face103
  shape: bbox 3.5 x 17.8 x 2e-07 mm, 1 faces, 0 solids (baked)
FEATURE [Part::Revolution] Revolve111  label="removeToCreateScrewAndThreadedInsertHole038"
  Angle = 360
  Axis = (0,1,0)
  Base = (0,0,0)
  FaceMakerClass = Part::FaceMakerBullseye
  Placement = pos=(109.5,4.7,3.5) rot=(0,0,1;0rad)
  Solid = false
  Source = -> Face103
  Symmetric = false
FEATURE [Part::Feature] Face104
  shape: bbox 3.5 x 17.8 x 2e-07 mm, 1 faces, 0 solids (baked)
FEATURE [Part::Revolution] Revolve112  label="removeToCreateScrewAndThreadedInsertHole039"
  Angle = 360
  Axis = (0,1,0)
  Base = (0,0,0)
  FaceMakerClass = Part::FaceMakerBullseye
  Placement = pos=(109.5,4.7,68.5) rot=(0,0,1;0rad)
  Solid = false
  Source = -> Face104
  Symmetric = false
FEATURE [Part::MultiFuse] Fusion081  label="removeToCreateScrewAndThreadedInsertHole040"
  Shapes = -> [Revolve107,Revolve108,Revolve109,Revolve110,Revolve111,Revolve112]
FEATURE [Part::MultiFuse] Fusion082  label="casePillars002"
  Shapes = -> [Revolve094,Revolve092,Revolve090,Revolve089,Revolve091,Revolve093]
FEATURE [Part::Cut] Cut037  label="casePillars003"
  Base = -> Fusion082
  Tool = -> Fusion081
FEATURE [Sketcher::SketchObject] Sketch051
  FullyConstrained = true
  Placement = pos=(117,19,0) rot=(0.57735,0.57735,0.57735;2.0944rad)
  sketch-geometry (48):
    g0: LineSegment StartX=-49.19 StartY=69.25 StartZ=0 EndX=-49.19 EndY=66.25 EndZ=0
    g1: LineSegment StartX=-49.19 StartY=63.5 StartZ=0 EndX=-49.19 EndY=60.5 EndZ=0
    g2: LineSegment StartX=-49.19 StartY=57.75 StartZ=0 EndX=-49.19 EndY=54.75 EndZ=0
    g3: LineSegment StartX=-49.19 StartY=52 StartZ=0 EndX=-49.19 EndY=49 EndZ=0
    g4: LineSegment StartX=-49.19 StartY=46.25 StartZ=0 EndX=-49.19 EndY=43.25 EndZ=0
    g5: LineSegment StartX=-49.19 StartY=40.5 StartZ=0 EndX=-49.19 EndY=37.5 EndZ=0
    g6: LineSegment StartX=-49.19 StartY=34.5 StartZ=0 EndX=-49.19 EndY=31.5 EndZ=0
    g7: LineSegment StartX=-49.19 StartY=28.75 StartZ=0 EndX=-49.19 EndY=25.75 EndZ=0
    g8: LineSegment StartX=-49.19 StartY=23 StartZ=0 EndX=-49.19 EndY=20 EndZ=0
    g9: LineSegment StartX=-49.19 StartY=17.25 StartZ=0 EndX=-49.19 EndY=14.25 EndZ=0
    g10: LineSegment StartX=-49.19 StartY=11.5 StartZ=0 EndX=-49.19 EndY=8.5 EndZ=0
    g11: LineSegment StartX=-49.19 StartY=5.75 StartZ=0 EndX=-49.19 EndY=2.75 EndZ=0
    g12: ArcOfCircle CenterX=-1.5 CenterY=67.75 CenterZ=0 NormalX=0 NormalY=0 NormalZ=1 AngleXU=0 Radius=1.5 StartAngle=4.71239 EndAngle=7.85398
    g13: ArcOfCircle CenterX=-1.5 CenterY=62 CenterZ=0 NormalX=0 NormalY=0 NormalZ=1 AngleXU=0 Radius=1.5 StartAngle=4.71239 EndAngle=7.85398
    g14: ArcOfCircle CenterX=-1.5 CenterY=56.25 CenterZ=0 NormalX=0 NormalY=0 NormalZ=1 AngleXU=0 Radius=1.5 StartAngle=4.71239 EndAngle=7.85398
    g15: ArcOfCircle CenterX=-11.49 CenterY=50.5 CenterZ=0 NormalX=0 NormalY=0 NormalZ=1 AngleXU=0 Radius=1.5 StartAngle=4.71239 EndAngle=7.85398
    g16: ArcOfCircle CenterX=-16.28 CenterY=44.75 CenterZ=0 NormalX=0 NormalY=0 NormalZ=1 AngleXU=0 Radius=1.5 StartAngle=4.71239 EndAngle=7.85398
    g17: ArcOfCircle CenterX=-18.2337 CenterY=39 CenterZ=0 NormalX=0 NormalY=0 NormalZ=1 AngleXU=0 Radius=1.5 StartAngle=4.71485 EndAngle=7.85398
    g18: ArcOfCircle CenterX=-16.2837 CenterY=27.25 CenterZ=0 NormalX=0 NormalY=0 NormalZ=1 AngleXU=0 Radius=1.5 StartAngle=4.71485 EndAngle=7.85398
    g19: ArcOfCircle CenterX=-18.2337 CenterY=33 CenterZ=0 NormalX=0 NormalY=0 NormalZ=1 AngleXU=0 Radius=1.5 StartAngle=4.71485 EndAngle=7.85398
    g20: ArcOfCircle CenterX=-11.49 CenterY=21.5 CenterZ=0 NormalX=0 NormalY=0 NormalZ=1 AngleXU=0 Radius=1.5 StartAngle=4.71239 EndAngle=7.85398
    g21: ArcOfCircle CenterX=-1.5 CenterY=4.25 CenterZ=0 NormalX=0 NormalY=0 NormalZ=1 AngleXU=0 Radius=1.5 StartAngle=4.71239 EndAngle=7.85398
    g22: ArcOfCircle CenterX=-1.5 CenterY=10 CenterZ=0 NormalX=0 NormalY=0 NormalZ=1 AngleXU=0 Radius=1.5 StartAngle=4.71239 EndAngle=7.85398
    g23: ArcOfCircle CenterX=-1.5 CenterY=15.75 CenterZ=0 NormalX=0 NormalY=0 NormalZ=1 AngleXU=0 Radius=1.5 StartAngle=4.71239 EndAngle=7.85398
    g24: LineSegment StartX=-49.19 StartY=69.25 StartZ=0 EndX=-1.5 EndY=69.25 EndZ=0
    g25: LineSegment StartX=-49.19 StartY=66.25 StartZ=0 EndX=-1.5 EndY=66.25 EndZ=0
    g26: LineSegment StartX=-49.19 StartY=63.5 StartZ=0 EndX=-1.5 EndY=63.5 EndZ=0
    g27: LineSegment StartX=-49.19 StartY=60.5 StartZ=0 EndX=-1.5 EndY=60.5 EndZ=0
    g28: LineSegment StartX=-49.19 StartY=57.75 StartZ=0 EndX=-1.5 EndY=57.75 EndZ=0
    g29: LineSegment StartX=-49.19 StartY=54.75 StartZ=0 EndX=-1.5 EndY=54.75 EndZ=0
    g30: LineSegment StartX=-49.19 StartY=52 StartZ=0 EndX=-11.49 EndY=52 EndZ=0
    g31: LineSegment StartX=-49.19 StartY=49 StartZ=0 EndX=-11.49 EndY=49 EndZ=0
    g32: LineSegment StartX=-49.19 StartY=46.25 StartZ=0 EndX=-16.28 EndY=46.25 EndZ=0
    g33: LineSegment StartX=-49.19 StartY=43.25 StartZ=0 EndX=-16.28 EndY=43.25 EndZ=0
    g34: LineSegment StartX=-49.19 StartY=40.5 StartZ=0 EndX=-18.2337 EndY=40.5 EndZ=0
    g35: LineSegment StartX=-49.19 StartY=37.5 StartZ=0 EndX=-18.23 EndY=37.5 EndZ=0
    g36: LineSegment StartX=-49.19 StartY=34.5 StartZ=0 EndX=-18.2337 EndY=34.5 EndZ=0
    g37: LineSegment StartX=-49.19 StartY=31.5 StartZ=0 EndX=-18.23 EndY=31.5 EndZ=0
    g38: LineSegment StartX=-49.19 StartY=28.75 StartZ=0 EndX=-16.2837 EndY=28.75 EndZ=0
    g39: LineSegment StartX=-49.19 StartY=25.75 StartZ=0 EndX=-16.28 EndY=25.75 EndZ=0
    g40: LineSegment StartX=-49.19 StartY=23 StartZ=0 EndX=-11.49 EndY=23 EndZ=0
    g41: LineSegment StartX=-49.19 StartY=20 StartZ=0 EndX=-11.49 EndY=20 EndZ=0
    g42: LineSegment StartX=-49.19 StartY=17.25 StartZ=0 EndX=-1.5 EndY=17.25 EndZ=0
    g43: LineSegment StartX=-49.19 StartY=14.25 StartZ=0 EndX=-1.5 EndY=14.25 EndZ=0
    g44: LineSegment StartX=-49.19 StartY=11.5 StartZ=0 EndX=-1.5 EndY=11.5 EndZ=0
    g45: LineSegment StartX=-49.19 StartY=8.5 StartZ=0 EndX=-1.5 EndY=8.5 EndZ=0
    g46: LineSegment StartX=-49.19 StartY=5.75 StartZ=0 EndX=-1.5 EndY=5.75 EndZ=0
    g47: LineSegment StartX=-49.19 StartY=2.75 StartZ=0 EndX=-1.5 EndY=2.75 EndZ=0
  constraints (120):
    c: Vertical(g0)
    c: Distance(g0) = 3
    c: Block(g0)
    c: Vertical(g1)
    c: Distance(g1) = 3
    c: Vertical(g2)
    c: Equal(g0,g2) = 3
    c: Block(g2)
    c: Vertical(g3)
    c: Equal(g1,g3) = 3
    c: Vertical(g4)
    c: Equal(g0,g4) = 3
    c: Block(g4)
    c: Vertical(g5)
    c: Equal(g1,g5) = 3
    c: Vertical(g6)
    c: Equal(g0,g6) = 3
    c: Block(g6)
    c: Vertical(g7)
    c: Equal(g1,g7) = 3
    c: Vertical(g8)
    c: Equal(g0,g8) = 3
    c: Block(g8)
    c: Vertical(g9)
    c: Equal(g1,g9) = 3
    c: Vertical(g10)
    c: Equal(g0,g10) = 3
    c: Block(g10)
    c: Vertical(g11)
    c: Equal(g1,g11) = 3
    c: Block(g12)
    c: Block(g13)
    c: Block(g14)
    c: Block(g15)
    c: Block(g16)
    c: Block(g17)
    c: Block(g18)
    c: Block(g19)
    c: Block(g20)
    c: Block(g21)
    c: Block(g22)
    c: Block(g23)
    c: Block(g11)
    c: Block(g9)
    c: Block(g7)
    c: Block(g5)
    c: Block(g3)
    c: Block(g1)
    c: Coincident(g24,g0)
    c: Coincident(g24,g12)
    c: Horizontal(g24)
    c: Coincident(g25,g0)
    c: Coincident(g25,g12)
    c: Horizontal(g25)
    c: Coincident(g26,g1)
    c: Coincident(g26,g13)
    c: Horizontal(g26)
    c: Coincident(g27,g1)
    c: Coincident(g27,g13)
    c: Horizontal(g27)
    c: Coincident(g28,g2)
    c: Coincident(g28,g14)
    c: Horizontal(g28)
    c: Coincident(g29,g2)
    c: Coincident(g29,g14)
    c: Horizontal(g29)
    c: Coincident(g30,g3)
    c: Coincident(g30,g15)
    c: Horizontal(g30)
    c: Coincident(g31,g3)
    c: Coincident(g31,g15)
    c: Horizontal(g31)
    c: Coincident(g32,g4)
    c: Coincident(g32,g16)
    c: Horizontal(g32)
    c: Coincident(g33,g4)
    c: Coincident(g33,g16)
    c: Horizontal(g33)
    c: Coincident(g34,g5)
    c: Coincident(g34,g17)
    c: Horizontal(g34)
    c: Coincident(g35,g5)
    c: Coincident(g35,g17)
    c: Horizontal(g35)
    c: Coincident(g36,g6)
    c: Coincident(g36,g19)
    c: Horizontal(g36)
    c: Coincident(g37,g6)
    c: Coincident(g37,g19)
    c: Horizontal(g37)
    c: Coincident(g38,g7)
    c: Coincident(g38,g18)
    c: Horizontal(g38)
    c: Coincident(g39,g7)
    c: Coincident(g39,g18)
    c: Horizontal(g39)
    c: Coincident(g40,g8)
    c: Coincident(g40,g20)
    c: Horizontal(g40)
    c: Coincident(g41,g8)
    c: Coincident(g41,g20)
    c: Horizontal(g41)
    c: Coincident(g42,g9)
    c: Coincident(g42,g23)
    c: Horizontal(g42)
    c: Coincident(g43,g9)
    c: Coincident(g43,g23)
    c: Horizontal(g43)
    c: Coincident(g44,g10)
    c: Coincident(g44,g22)
    c: Horizontal(g44)
    c: Coincident(g45,g10)
    c: Coincident(g45,g22)
    c: Horizontal(g45)
    c: Coincident(g46,g11)
    c: Coincident(g46,g21)
    c: Horizontal(g46)
    c: Coincident(g47,g11)
    c: Coincident(g47,g21)
    c: Horizontal(g47)
FEATURE [Part::Extrusion] Extrude042
  Base = -> Sketch051
  Dir = (1,-2e-16,2e-16)
  DirMode = 2
  FaceMakerClass = Part::FaceMakerBullseye
  LengthFwd = 19
  LengthRev = 0
  Placement = pos=(-19,0,0) rot=(0,0,1;0rad)
  Solid = true
  Symmetric = false
FEATURE [Part::Fillet] Fillet035  label="removeToCreateVentalationHoles"
  Base = -> Extrude042
  Edges = <same value as first occurrence — deduplicated (x6 in doc)>
  Placement = pos=(7,0,0) rot=(0,0,1;0rad)
FEATURE [Part::Cut] Cut038  label="top017"
  Base = -> Cut033
  Tool = -> Fillet035
FEATURE [Sketcher::SketchObject] Sketch052  label="bottomSketch001"
  FullyConstrained = true
  sketch-geometry (45):
    g0: LineSegment StartX=6.29999 StartY=8 StartZ=0 EndX=3.29999 EndY=8 EndZ=0
    g1: LineSegment StartX=3.29999 StartY=8 StartZ=0 EndX=3.29999 EndY=-6.03275e-07 EndZ=0
    g2: ArcOfCircle CenterX=8.29999 CenterY=5 CenterZ=0 NormalX=0 NormalY=0 NormalZ=1 AngleXU=0 Radius=2 StartAngle=3.14159 EndAngle=4.71239
    g3: LineSegment StartX=6.29999 StartY=8 StartZ=0 EndX=6.29999 EndY=5 EndZ=0
    g4: ArcOfCircle CenterX=105 CenterY=19 CenterZ=0 NormalX=0 NormalY=0 NormalZ=1 AngleXU=0 Radius=12.7 StartAngle=4.71239 EndAngle=5.94289
    g5-g11: Circle x7 (B-spline internal-alignment scaffolding for g12; pole/knot coordinates omitted)
    g12: BSplineCurve PolesCount=7 KnotsCount=5 Degree=3 IsPeriodic=0
    g13-g17: GeomPoint x5 (B-spline internal-alignment scaffolding for g12; pole/knot coordinates omitted)
    g18: ArcOfCircle CenterX=105 CenterY=19 CenterZ=0 NormalX=0 NormalY=0 NormalZ=1 AngleXU=0 Radius=15.7 StartAngle=5.81226 EndAngle=6.28319
    g19: BSplineCurve PolesCount=5 KnotsCount=3 Degree=3 IsPeriodic=0
    g20: LineSegment StartX=8.29999 StartY=3 StartZ=0 EndX=101.7 EndY=3 EndZ=0
    g21: LineSegment StartX=3.29999 StartY=-6.03275e-07 StartZ=0 EndX=105 EndY=-6.03275e-07 EndZ=0
    g22: LineSegment StartX=120.974 StartY=8.71251 StartZ=0 EndX=122.332 EndY=7.83778 EndZ=0
    g23: LineSegment StartX=105 StartY=-6.03274e-07 StartZ=0 EndX=113 EndY=-6.03274e-07 EndZ=0
    g24: ArcOfCircle CenterX=105 CenterY=19 CenterZ=0 NormalX=0 NormalY=0 NormalZ=1 AngleXU=0 Radius=20.6155 StartAngle=5.11091 EndAngle=5.71103
    g25: ArcOfCircle CenterX=117.7 CenterY=19 CenterZ=0 NormalX=0 NormalY=0 NormalZ=1 AngleXU=0 Radius=3 StartAngle=1.2e-15 EndAngle=2.10468
    g26: Circle CenterX=116.345 CenterY=16.3232 CenterZ=0 NormalX=0 NormalY=0 NormalZ=1 AngleXU=0 Radius=1
    g27: Circle CenterX=117.24 CenterY=15.7584 CenterZ=0 NormalX=0 NormalY=0 NormalZ=1 AngleXU=0 Radius=1
    g28: Circle CenterX=116.972 CenterY=14.7612 CenterZ=0 NormalX=0 NormalY=0 NormalZ=1 AngleXU=0 Radius=1
    g29: BSplineCurve PolesCount=3 KnotsCount=2 Degree=2 IsPeriodic=0
    g30: GeomPoint X=116.345 Y=16.3232 Z=0
    g31: GeomPoint X=116.972 Y=14.7612 Z=0
    g32: Circle CenterX=115.828 CenterY=17.157 CenterZ=0 NormalX=0 NormalY=0 NormalZ=1 AngleXU=0 Radius=1
    g33: Circle CenterX=115.841 CenterY=16.639 CenterZ=0 NormalX=0 NormalY=0 NormalZ=1 AngleXU=0 Radius=1
    g34: Circle CenterX=116.345 CenterY=16.3232 CenterZ=0 NormalX=0 NormalY=0 NormalZ=1 AngleXU=0 Radius=1
    g35: BSplineCurve PolesCount=3 KnotsCount=2 Degree=2 IsPeriodic=0
    g36: GeomPoint X=115.828 Y=17.157 Z=0
    g37: GeomPoint X=116.345 Y=16.3232 Z=0
    g38: LineSegment StartX=115.828 StartY=17.157 StartZ=0 EndX=115.828 EndY=20.8307 EndZ=0
    g39: Circle CenterX=115.828 CenterY=20.8307 CenterZ=0 NormalX=0 NormalY=0 NormalZ=1 AngleXU=0 Radius=1
    g40: Circle CenterX=115.831 CenterY=21.3396 CenterZ=0 NormalX=0 NormalY=0 NormalZ=1 AngleXU=0 Radius=1
    g41: Circle CenterX=116.173 CenterY=21.5825 CenterZ=0 NormalX=0 NormalY=0 NormalZ=1 AngleXU=0 Radius=1
    g42: BSplineCurve PolesCount=3 KnotsCount=2 Degree=2 IsPeriodic=0
    g43: GeomPoint X=115.828 Y=20.8307 Z=0
    g44: GeomPoint X=116.173 Y=21.5825 Z=0
  constraints (70):
    c: Horizontal(g0)
    c: Distance(g0) = 3
    c: Coincident(g1,g0)
    c: Vertical(g1)
    c: Block(g2)
    c: Block(g0)
    c: Coincident(g3,g0)
    c: Coincident(g3,g2)
    c: Vertical(g3)
    c: Block(g1)
    c: Block(g4)
    c: Coincident(g19,g4)
    c: Block(g19)
    c: Equal(g5, g6-g11) x6
    c: InternalAlignment(g5-g11 -> g12) x7
    c: InternalAlignment(g13-g17 -> g12) x5
    c: Block(g12)
    c: Coincident(g18,g12)
    c: Block(g18)
    c: Coincident(g20,g2)
    c: Coincident(g20,g19)
    c: Horizontal(g20)
    c: Distance(g20) = 93.4
    c: Coincident(g21,g1)
    c: Horizontal(g21)
    c: Distance(g21) = 101.7
    c: Horizontal(g23)
    c: Distance(g23) = 8
    c: Coincident(g24,g23)
    c: Block(g23)
    c: Coincident(g22,g24)
    c: Block(g24)
    c: Block(g22)
    c: Distance(g22) = 1.61553
    c: Coincident(g25,g18)
    c: Block(g25)
    c: Weight(g26) = 1
    c: Equal(g26,g27)
    c: Equal(g26,g28)
    c: Coincident(g29,g4)
    c: InternalAlignment(g26,g29)
    c: InternalAlignment(g27,g29)
    c: InternalAlignment(g28,g29)
    c: InternalAlignment(g30,g29)
    c: InternalAlignment(g31,g29)
    c: Block(g29)
    c: Weight(g32) = 1
    c: Equal(g32,g33)
    c: Equal(g32,g34)
    c: Coincident(g35,g29)
    c: InternalAlignment(g32,g35)
    c: InternalAlignment(g33,g35)
    c: InternalAlignment(g34,g35)
    c: InternalAlignment(g36,g35)
    c: InternalAlignment(g37,g35)
    c: Block(g35)
    c: Coincident(g38,g35)
    c: Vertical(g38)
    c: Block(g38)
    c: Coincident(g42,g38)
    c: Weight(g39) = 1
    c: Equal(g39,g40)
    c: Equal(g39,g41)
    c: Coincident(g42,g25)
    c: InternalAlignment(g39,g42)
    c: InternalAlignment(g40,g42)
    c: InternalAlignment(g41,g42)
    c: InternalAlignment(g43,g42)
    c: InternalAlignment(g44,g42)
    c: Block(g42)
FEATURE [Part::Extrusion] Extrude043  label="bottom010"
  Base = -> Sketch052
  Dir = (0,0,1)
  DirMode = 2
  FaceMakerClass = Part::FaceMakerBullseye
  LengthFwd = 71.4
  LengthRev = 0
  Placement = pos=(0,0,0.3) rot=(0,0,1;0rad)
  Solid = true
  Symmetric = false
FEATURE [Sketcher::SketchObject] Sketch053  label="topSketch013"
  FullyConstrained = true
  sketch-geometry (22):
    g0: LineSegment StartX=5.21097e-06 StartY=3 StartZ=0 EndX=5.21097e-06 EndY=19 EndZ=0
    g1: ArcOfCircle CenterX=19 CenterY=19 CenterZ=0 NormalX=0 NormalY=0 NormalZ=1 AngleXU=0 Radius=19 StartAngle=1.5708 EndAngle=3.14159
    g2: ArcOfCircle CenterX=19 CenterY=19 CenterZ=0 NormalX=0 NormalY=0 NormalZ=1 AngleXU=0 Radius=16 StartAngle=1.5708 EndAngle=3.14159
    g3: LineSegment StartX=114 StartY=35 StartZ=0 EndX=19 EndY=35 EndZ=0
    g4: LineSegment StartX=5.21097e-06 StartY=3 StartZ=0 EndX=5.21097e-06 EndY=0 EndZ=0
    g5: LineSegment StartX=3 StartY=0 StartZ=0 EndX=5.21097e-06 EndY=0 EndZ=0
    g6: LineSegment StartX=3 StartY=19 StartZ=0 EndX=3 EndY=0 EndZ=0
    g7: LineSegment StartX=19 StartY=38 StartZ=0 EndX=124 EndY=38 EndZ=0
    g8: Circle CenterX=119 CenterY=35 CenterZ=0 NormalX=0 NormalY=0 NormalZ=1 AngleXU=0 Radius=1
    g9: Circle CenterX=121 CenterY=35 CenterZ=0 NormalX=0 NormalY=0 NormalZ=1 AngleXU=0 Radius=1
    g10: Circle CenterX=121 CenterY=33 CenterZ=0 NormalX=0 NormalY=0 NormalZ=1 AngleXU=0 Radius=1
    g11: BSplineCurve PolesCount=3 KnotsCount=2 Degree=2 IsPeriodic=0
    g12: GeomPoint X=119 Y=35 Z=0
    g13: GeomPoint X=121 Y=33 Z=0
    g14: LineSegment StartX=119 StartY=35 StartZ=0 EndX=114 EndY=35 EndZ=0
    g15: ArcOfCircle CenterX=105 CenterY=19 CenterZ=0 NormalX=0 NormalY=0 NormalZ=1 AngleXU=0 Radius=16 StartAngle=5.60905 EndAngle=6.28319
    g16: LineSegment StartX=121 StartY=33 StartZ=0 EndX=121 EndY=19 EndZ=0
    g17: LineSegment StartX=117.5 StartY=9.01251 StartZ=0 EndX=121.163 EndY=9.0125 EndZ=0
    g18: ArcOfCircle CenterX=105 CenterY=19 CenterZ=0 NormalX=0 NormalY=0 NormalZ=1 AngleXU=0 Radius=20.6155 StartAngle=5.7297 EndAngle=6.28319
    g19: LineSegment StartX=121.163 StartY=9.0125 StartZ=0 EndX=122.538 EndY=8.16329 EndZ=0
    g20: LineSegment StartX=124 StartY=38 StartZ=0 EndX=125.616 EndY=38 EndZ=0
    g21: LineSegment StartX=125.616 StartY=19 StartZ=0 EndX=125.616 EndY=38 EndZ=0
  constraints (50):
    c: Vertical(g0)
    c: Block(g0)
    c: Coincident(g1,g0)
    c: Block(g1)
    c: Coincident(g2,g1)
    c: Block(g2)
    c: Coincident(g3,g2)
    c: Horizontal(g3)
    c: Tangent(g3,g2)
    c: Coincident(g4,g0)
    c: Distance(g4) = 3
    c: Vertical(g4)
    c: Coincident(g5,g4)
    c: Horizontal(g5)
    c: Coincident(g6,g2)
    c: Coincident(g6,g5)
    c: Vertical(g6)
    c: Horizontal(g7)
    c: Distance(g7) = 105
    c: Coincident(g7,g1)
    c: Block(g3)
    c: Weight(g8) = 1
    c: Equal(g8,g9)
    c: Equal(g8,g10)
    c: InternalAlignment(g8,g11)
    c: InternalAlignment(g9,g11)
    c: InternalAlignment(g10,g11)
    c: InternalAlignment(g12,g11)
    c: InternalAlignment(g13,g11)
    c: Block(g11)
    c: Coincident(g14,g11)
    c: Coincident(g14,g3)
    c: Horizontal(g14)
    c: Block(g15)
    c: Coincident(g16,g11)
    c: Coincident(g16,g15)
    c: Vertical(g16)
    c: Distance(g16) = 14
    c: Coincident(g17,g15)
    c: Block(g18)
    c: Coincident(g19,g18)
    c: Coincident(g20,g7)
    c: Horizontal(g20)
    c: Vertical(g21)
    c: Coincident(g20,g21)
    c: Block(g20)
    c: Block(g21)
    c: Block(g19)
    c: Block(g17)
    c: Distance(g20) = 1.61553
FEATURE [Part::Extrusion] Extrude044
  Base = -> Sketch053
  Dir = (0,0,1)
  DirMode = 2
  FaceMakerClass = Part::FaceMakerBullseye
  LengthFwd = 72
  LengthRev = 0
  Solid = true
  Symmetric = false
FEATURE [Part::Fillet] Fillet036  label="top018"
  Base = -> Extrude044
  Edges = 1 edges r=2: [Edge41]
FEATURE [Sketcher::SketchObject] Sketch054
  FullyConstrained = false
  Placement = pos=(0,0,0) rot=(1,0,0;1.5708rad)
  sketch-geometry (24):
    g0: ArcOfCircle CenterX=-4 CenterY=-10.5 CenterZ=0 NormalX=0 NormalY=0 NormalZ=1 AngleXU=0 Radius=1.5 StartAngle=6e-16 EndAngle=3.14159
    g1: ArcOfCircle CenterX=-34.2 CenterY=-10.5 CenterZ=0 NormalX=0 NormalY=0 NormalZ=1 AngleXU=0 Radius=1.5 StartAngle=0 EndAngle=3.14159
    g2: ArcOfCircle CenterX=-34.2 CenterY=-27.7 CenterZ=0 NormalX=0 NormalY=0 NormalZ=1 AngleXU=0 Radius=1.5 StartAngle=3.14159 EndAngle=6.28319
    g3: ArcOfCircle CenterX=-4 CenterY=-27.7 CenterZ=0 NormalX=0 NormalY=0 NormalZ=1 AngleXU=0 Radius=1.5 StartAngle=3.1416 EndAngle=6.28319
    g4: ArcOfCircle CenterX=-10 CenterY=-4.3 CenterZ=0 NormalX=0 NormalY=0 NormalZ=1 AngleXU=0 Radius=1.5 StartAngle=2e-16 EndAngle=3.14159
    g5: ArcOfCircle CenterX=-16.1 CenterY=-1.8 CenterZ=0 NormalX=0 NormalY=0 NormalZ=1 AngleXU=0 Radius=1.5 StartAngle=5e-16 EndAngle=3.14159
    g6: ArcOfCircle CenterX=-22.1 CenterY=-1.8 CenterZ=0 NormalX=0 NormalY=0 NormalZ=1 AngleXU=0 Radius=1.5 StartAngle=5e-16 EndAngle=3.14159
    g7: ArcOfCircle CenterX=-28.2 CenterY=-4.3 CenterZ=0 NormalX=0 NormalY=0 NormalZ=1 AngleXU=0 Radius=1.5 StartAngle=2e-16 EndAngle=3.14159
    g8: ArcOfCircle CenterX=-10 CenterY=-33.9 CenterZ=0 NormalX=0 NormalY=0 NormalZ=1 AngleXU=0 Radius=1.5 StartAngle=3.14159 EndAngle=6.28319
    g9: ArcOfCircle CenterX=-16.1 CenterY=-36.4 CenterZ=0 NormalX=0 NormalY=0 NormalZ=1 AngleXU=0 Radius=1.5 StartAngle=3.14159 EndAngle=6.28319
    g10: ArcOfCircle CenterX=-22.1 CenterY=-36.4 CenterZ=0 NormalX=0 NormalY=0 NormalZ=1 AngleXU=0 Radius=1.5 StartAngle=3.14159 EndAngle=6.28319
    g11: ArcOfCircle CenterX=-28.2 CenterY=-33.9 CenterZ=0 NormalX=0 NormalY=0 NormalZ=1 AngleXU=0 Radius=1.5 StartAngle=3.14159 EndAngle=6.28319
    g12: LineSegment StartX=-35.7 StartY=-10.5 StartZ=0 EndX=-35.7 EndY=-27.7 EndZ=0
    g13: LineSegment StartX=-32.7 StartY=-10.5 StartZ=0 EndX=-32.7 EndY=-27.7 EndZ=0
    g14: LineSegment StartX=-29.7 StartY=-33.9 StartZ=0 EndX=-29.7 EndY=-4.3 EndZ=0
    g15: LineSegment StartX=-26.7 StartY=-33.9 StartZ=0 EndX=-26.7 EndY=-4.3 EndZ=0
    g16: LineSegment StartX=-2.5 StartY=-10.5 StartZ=0 EndX=-2.5 EndY=-27.7 EndZ=0
    g17: LineSegment StartX=-8.5 StartY=-4.3 StartZ=0 EndX=-8.5 EndY=-33.9 EndZ=0
    g18: LineSegment StartX=-5.5 StartY=-10.5 StartZ=0 EndX=-5.5 EndY=-27.7 EndZ=0
    g19: LineSegment StartX=-11.5 StartY=-4.3 StartZ=0 EndX=-11.5 EndY=-33.9 EndZ=0
    g20: LineSegment StartX=-14.6 StartY=-1.8 StartZ=0 EndX=-14.6 EndY=-36.4 EndZ=0
    g21: LineSegment StartX=-17.6 StartY=-1.8 StartZ=0 EndX=-17.6 EndY=-36.4 EndZ=0
    g22: LineSegment StartX=-20.6 StartY=-36.4 StartZ=0 EndX=-20.6 EndY=-1.8 EndZ=0
    g23: LineSegment StartX=-23.6 StartY=-1.8 StartZ=0 EndX=-23.6 EndY=-36.4 EndZ=0
  constraints (48):
    c: Block(g0)
    c: Block(g1)
    c: Block(g2)
    c: Block(g3)
    c: Block(g4)
    c: Block(g5)
    c: Block(g6)
    c: Block(g7)
    c: Block(g8)
    c: Block(g9)
    c: Block(g10)
    c: Block(g11)
    c: Coincident(g12,g1)
    c: Coincident(g12,g2)
    c: Vertical(g12)
    c: Coincident(g13,g1)
    c: Coincident(g13,g2)
    c: Vertical(g13)
    c: Coincident(g14,g11)
    c: Coincident(g14,g7)
    c: Vertical(g14)
    c: Coincident(g15,g11)
    c: Coincident(g15,g7)
    c: Vertical(g15)
    c: Coincident(g16,g0)
    c: Coincident(g16,g3)
    c: Vertical(g16)
    c: Coincident(g17,g4)
    c: Coincident(g17,g8)
    c: Vertical(g17)
    c: Coincident(g18,g0)
    c: Coincident(g18,g3)
    c: Vertical(g18)
    c: Coincident(g19,g4)
    c: Coincident(g19,g8)
    c: Vertical(g19)
    c: Coincident(g20,g5)
    c: Coincident(g20,g9)
    c: Vertical(g20)
    c: Coincident(g21,g5)
    c: Coincident(g21,g9)
    c: Vertical(g21)
    c: Coincident(g22,g10)
    c: Coincident(g22,g6)
    c: Vertical(g22)
    c: Coincident(g23,g6)
    c: Coincident(g23,g10)
    c: Vertical(g23)
FEATURE [Part::Extrusion] Extrude045  label="removeToCreateFanGrillHoles003"
  Base = -> Sketch054
  Dir = (0,-1,6e-16)
  DirMode = 2
  FaceMakerClass = Part::FaceMakerBullseye
  LengthFwd = 10
  LengthRev = 0
  Placement = pos=(65.4,44,54.82) rot=(0,0,1;0rad)
  Solid = true
  Symmetric = false
FEATURE [Part::Feature] Face105 .. Face108  x4 (patterned run collapsed; names and placements below)
  shape: bbox 3.5 x 17.8 x 2e-07 mm, 1 faces, 0 solids (baked)
FEATURE [Part::Revolution] Revolve113  label="removeToCreateScrewAndThreadedInsertHole041"
  Angle = 360
  Axis = (0,1,0)
  Base = (0,0,0)
  FaceMakerClass = Part::FaceMakerBullseye
  Placement = pos=(62.3,30.3,19.7) rot=(0,0,1;0rad)
  Solid = false
  Source = -> Face105
  Symmetric = false
FEATURE [Part::Revolution] Revolve114  label="removeToCreateScrewAndThreadedInsertHole042"
  Angle = 360
  Axis = (0,1,0)
  Base = (0,0,0)
  FaceMakerClass = Part::FaceMakerBullseye
  Placement = pos=(62.3,30.3,51.7) rot=(0,0,1;0rad)
  Solid = false
  Source = -> Face106
  Symmetric = false
FEATURE [Part::Revolution] Revolve115  label="removeToCreateScrewAndThreadedInsertHole043"
  Angle = 360
  Axis = (0,1,0)
  Base = (0,0,0)
  FaceMakerClass = Part::FaceMakerBullseye
  Placement = pos=(30.3,30.3,19.7) rot=(0,0,1;0rad)
  Solid = false
  Source = -> Face107
  Symmetric = false
FEATURE [Part::Revolution] Revolve116  label="removeToCreateScrewAndThreadedInsertHole044"
  Angle = 360
  Axis = (0,1,0)
  Base = (0,0,0)
  FaceMakerClass = Part::FaceMakerBullseye
  Placement = pos=(30.3,30.3,51.7) rot=(0,0,1;0rad)
  Solid = false
  Source = -> Face108
  Symmetric = false
FEATURE [Part::MultiFuse] Fusion083  label="createThreadedInsertHolesForFan004"
  Shapes = -> [Revolve113,Revolve114,Revolve115,Revolve116]
FEATURE [Part::Box] Box024  label="removeToCreteHoleForPlugHousing026"
  AttacherType = Attacher::AttachEngine3D
  Height = 28.6
  Length = 10
  Placement = pos=(-2,0,21.7) rot=(0,0,1;0rad)
  Width = 19
FEATURE [Part::Cylinder] Cylinder038  label="removeToCreteHoleForPlugHousing027"
  Angle = 360
  AttacherType = Attacher::AttachEngine3D
  Height = 20
  Placement = pos=(-2,19,36) rot=(0,1,0;1.5708rad)
  Radius = 14.3
FEATURE [Part::MultiFuse] Fusion084  label="removeToCreteHoleForPlugHousing028"
  Shapes = -> [Box024,Cylinder038]
FEATURE [Part::Cylinder] Cylinder039
  Angle = 360
  AttacherType = Attacher::AttachEngine3D
  Height = 20
  Placement = pos=(0,0,36.15) rot=(0,0,1;0rad)
  Radius = 14.3
FEATURE [Part::Cylinder] Cylinder040
  Angle = 360
  AttacherType = Attacher::AttachEngine3D
  Height = 10
  Placement = pos=(0,0,36.15) rot=(0,0,1;0rad)
  Radius = 4
FEATURE [Part::Box] Box025  label="removeToCreteHoleForPlugHousing030"
  AttacherType = Attacher::AttachEngine3D
  Height = 28.6
  Length = 20
  Placement = pos=(106.15,0,21.7) rot=(0,0,1;0rad)
  Width = 19
FEATURE [Part::MultiFuse] Fusion086  label="removeToCreteHoleForPlugHousing031"
  Placement = pos=(70,19,36) rot=(0,1,0;1.5708rad)
  Shapes = -> [Cylinder039,Cylinder040]
FEATURE [Part::MultiFuse] Fusion085  label="removeToCreteHoleForPlugHousing029"
  Shapes = -> [Box025,Fusion086]
FEATURE [Sketcher::SketchObject] Sketch055
  FullyConstrained = true
  Placement = pos=(117,19,0) rot=(0.57735,0.57735,0.57735;2.0944rad)
  sketch-geometry (48):
    g0: LineSegment StartX=-49.19 StartY=69.25 StartZ=0 EndX=-49.19 EndY=66.25 EndZ=0
    g1: LineSegment StartX=-49.19 StartY=63.5 StartZ=0 EndX=-49.19 EndY=60.5 EndZ=0
    g2: LineSegment StartX=-49.19 StartY=57.75 StartZ=0 EndX=-49.19 EndY=54.75 EndZ=0
    g3: LineSegment StartX=-49.19 StartY=52 StartZ=0 EndX=-49.19 EndY=49 EndZ=0
    g4: LineSegment StartX=-49.19 StartY=46.25 StartZ=0 EndX=-49.19 EndY=43.25 EndZ=0
    g5: LineSegment StartX=-49.19 StartY=40.5 StartZ=0 EndX=-49.19 EndY=37.5 EndZ=0
    g6: LineSegment StartX=-49.19 StartY=34.5 StartZ=0 EndX=-49.19 EndY=31.5 EndZ=0
    g7: LineSegment StartX=-49.19 StartY=28.75 StartZ=0 EndX=-49.19 EndY=25.75 EndZ=0
    g8: LineSegment StartX=-49.19 StartY=23 StartZ=0 EndX=-49.19 EndY=20 EndZ=0
    g9: LineSegment StartX=-49.19 StartY=17.25 StartZ=0 EndX=-49.19 EndY=14.25 EndZ=0
    g10: LineSegment StartX=-49.19 StartY=11.5 StartZ=0 EndX=-49.19 EndY=8.5 EndZ=0
    g11: LineSegment StartX=-49.19 StartY=5.75 StartZ=0 EndX=-49.19 EndY=2.75 EndZ=0
    g12: ArcOfCircle CenterX=-1.5 CenterY=67.75 CenterZ=0 NormalX=0 NormalY=0 NormalZ=1 AngleXU=0 Radius=1.5 StartAngle=4.71239 EndAngle=7.85398
    g13: ArcOfCircle CenterX=-1.5 CenterY=62 CenterZ=0 NormalX=0 NormalY=0 NormalZ=1 AngleXU=0 Radius=1.5 StartAngle=4.71239 EndAngle=7.85398
    g14: ArcOfCircle CenterX=-1.5 CenterY=56.25 CenterZ=0 NormalX=0 NormalY=0 NormalZ=1 AngleXU=0 Radius=1.5 StartAngle=4.71239 EndAngle=7.85398
    g15: ArcOfCircle CenterX=-11.49 CenterY=50.5 CenterZ=0 NormalX=0 NormalY=0 NormalZ=1 AngleXU=0 Radius=1.5 StartAngle=4.71239 EndAngle=7.85398
    g16: ArcOfCircle CenterX=-16.28 CenterY=44.75 CenterZ=0 NormalX=0 NormalY=0 NormalZ=1 AngleXU=0 Radius=1.5 StartAngle=4.71239 EndAngle=7.85398
    g17: ArcOfCircle CenterX=-18.2337 CenterY=39 CenterZ=0 NormalX=0 NormalY=0 NormalZ=1 AngleXU=0 Radius=1.5 StartAngle=4.71485 EndAngle=7.85398
    g18: ArcOfCircle CenterX=-16.2837 CenterY=27.25 CenterZ=0 NormalX=0 NormalY=0 NormalZ=1 AngleXU=0 Radius=1.5 StartAngle=4.71485 EndAngle=7.85398
    g19: ArcOfCircle CenterX=-18.2337 CenterY=33 CenterZ=0 NormalX=0 NormalY=0 NormalZ=1 AngleXU=0 Radius=1.5 StartAngle=4.71485 EndAngle=7.85398
    g20: ArcOfCircle CenterX=-11.49 CenterY=21.5 CenterZ=0 NormalX=0 NormalY=0 NormalZ=1 AngleXU=0 Radius=1.5 StartAngle=4.71239 EndAngle=7.85398
    g21: ArcOfCircle CenterX=-1.5 CenterY=4.25 CenterZ=0 NormalX=0 NormalY=0 NormalZ=1 AngleXU=0 Radius=1.5 StartAngle=4.71239 EndAngle=7.85398
    g22: ArcOfCircle CenterX=-1.5 CenterY=10 CenterZ=0 NormalX=0 NormalY=0 NormalZ=1 AngleXU=0 Radius=1.5 StartAngle=4.71239 EndAngle=7.85398
    g23: ArcOfCircle CenterX=-1.5 CenterY=15.75 CenterZ=0 NormalX=0 NormalY=0 NormalZ=1 AngleXU=0 Radius=1.5 StartAngle=4.71239 EndAngle=7.85398
    g24: LineSegment StartX=-49.19 StartY=69.25 StartZ=0 EndX=-1.5 EndY=69.25 EndZ=0
    g25: LineSegment StartX=-49.19 StartY=66.25 StartZ=0 EndX=-1.5 EndY=66.25 EndZ=0
    g26: LineSegment StartX=-49.19 StartY=63.5 StartZ=0 EndX=-1.5 EndY=63.5 EndZ=0
    g27: LineSegment StartX=-49.19 StartY=60.5 StartZ=0 EndX=-1.5 EndY=60.5 EndZ=0
    g28: LineSegment StartX=-49.19 StartY=57.75 StartZ=0 EndX=-1.5 EndY=57.75 EndZ=0
    g29: LineSegment StartX=-49.19 StartY=54.75 StartZ=0 EndX=-1.5 EndY=54.75 EndZ=0
    g30: LineSegment StartX=-49.19 StartY=52 StartZ=0 EndX=-11.49 EndY=52 EndZ=0
    g31: LineSegment StartX=-49.19 StartY=49 StartZ=0 EndX=-11.49 EndY=49 EndZ=0
    g32: LineSegment StartX=-49.19 StartY=46.25 StartZ=0 EndX=-16.28 EndY=46.25 EndZ=0
    g33: LineSegment StartX=-49.19 StartY=43.25 StartZ=0 EndX=-16.28 EndY=43.25 EndZ=0
    g34: LineSegment StartX=-49.19 StartY=40.5 StartZ=0 EndX=-18.2337 EndY=40.5 EndZ=0
    g35: LineSegment StartX=-49.19 StartY=37.5 StartZ=0 EndX=-18.23 EndY=37.5 EndZ=0
    g36: LineSegment StartX=-49.19 StartY=34.5 StartZ=0 EndX=-18.2337 EndY=34.5 EndZ=0
    g37: LineSegment StartX=-49.19 StartY=31.5 StartZ=0 EndX=-18.23 EndY=31.5 EndZ=0
    g38: LineSegment StartX=-49.19 StartY=28.75 StartZ=0 EndX=-16.2837 EndY=28.75 EndZ=0
    g39: LineSegment StartX=-49.19 StartY=25.75 StartZ=0 EndX=-16.28 EndY=25.75 EndZ=0
    g40: LineSegment StartX=-49.19 StartY=23 StartZ=0 EndX=-11.49 EndY=23 EndZ=0
    g41: LineSegment StartX=-49.19 StartY=20 StartZ=0 EndX=-11.49 EndY=20 EndZ=0
    g42: LineSegment StartX=-49.19 StartY=17.25 StartZ=0 EndX=-1.5 EndY=17.25 EndZ=0
    g43: LineSegment StartX=-49.19 StartY=14.25 StartZ=0 EndX=-1.5 EndY=14.25 EndZ=0
    g44: LineSegment StartX=-49.19 StartY=11.5 StartZ=0 EndX=-1.5 EndY=11.5 EndZ=0
    g45: LineSegment StartX=-49.19 StartY=8.5 StartZ=0 EndX=-1.5 EndY=8.5 EndZ=0
    g46: LineSegment StartX=-49.19 StartY=5.75 StartZ=0 EndX=-1.5 EndY=5.75 EndZ=0
    g47: LineSegment StartX=-49.19 StartY=2.75 StartZ=0 EndX=-1.5 EndY=2.75 EndZ=0
  constraints (120):
    c: Vertical(g0)
    c: Distance(g0) = 3
    c: Block(g0)
    c: Vertical(g1)
    c: Distance(g1) = 3
    c: Vertical(g2)
    c: Equal(g0,g2) = 3
    c: Block(g2)
    c: Vertical(g3)
    c: Equal(g1,g3) = 3
    c: Vertical(g4)
    c: Equal(g0,g4) = 3
    c: Block(g4)
    c: Vertical(g5)
    c: Equal(g1,g5) = 3
    c: Vertical(g6)
    c: Equal(g0,g6) = 3
    c: Block(g6)
    c: Vertical(g7)
    c: Equal(g1,g7) = 3
    c: Vertical(g8)
    c: Equal(g0,g8) = 3
    c: Block(g8)
    c: Vertical(g9)
    c: Equal(g1,g9) = 3
    c: Vertical(g10)
    c: Equal(g0,g10) = 3
    c: Block(g10)
    c: Vertical(g11)
    c: Equal(g1,g11) = 3
    c: Block(g12)
    c: Block(g13)
    c: Block(g14)
    c: Block(g15)
    c: Block(g16)
    c: Block(g17)
    c: Block(g18)
    c: Block(g19)
    c: Block(g20)
    c: Block(g21)
    c: Block(g22)
    c: Block(g23)
    c: Block(g11)
    c: Block(g9)
    c: Block(g7)
    c: Block(g5)
    c: Block(g3)
    c: Block(g1)
    c: Coincident(g24,g0)
    c: Coincident(g24,g12)
    c: Horizontal(g24)
    c: Coincident(g25,g0)
    c: Coincident(g25,g12)
    c: Horizontal(g25)
    c: Coincident(g26,g1)
    c: Coincident(g26,g13)
    c: Horizontal(g26)
    c: Coincident(g27,g1)
    c: Coincident(g27,g13)
    c: Horizontal(g27)
    c: Coincident(g28,g2)
    c: Coincident(g28,g14)
    c: Horizontal(g28)
    c: Coincident(g29,g2)
    c: Coincident(g29,g14)
    c: Horizontal(g29)
    c: Coincident(g30,g3)
    c: Coincident(g30,g15)
    c: Horizontal(g30)
    c: Coincident(g31,g3)
    c: Coincident(g31,g15)
    c: Horizontal(g31)
    c: Coincident(g32,g4)
    c: Coincident(g32,g16)
    c: Horizontal(g32)
    c: Coincident(g33,g4)
    c: Coincident(g33,g16)
    c: Horizontal(g33)
    c: Coincident(g34,g5)
    c: Coincident(g34,g17)
    c: Horizontal(g34)
    c: Coincident(g35,g5)
    c: Coincident(g35,g17)
    c: Horizontal(g35)
    c: Coincident(g36,g6)
    c: Coincident(g36,g19)
    c: Horizontal(g36)
    c: Coincident(g37,g6)
    c: Coincident(g37,g19)
    c: Horizontal(g37)
    c: Coincident(g38,g7)
    c: Coincident(g38,g18)
    c: Horizontal(g38)
    c: Coincident(g39,g7)
    c: Coincident(g39,g18)
    c: Horizontal(g39)
    c: Coincident(g40,g8)
    c: Coincident(g40,g20)
    c: Horizontal(g40)
    c: Coincident(g41,g8)
    c: Coincident(g41,g20)
    c: Horizontal(g41)
    c: Coincident(g42,g9)
    c: Coincident(g42,g23)
    c: Horizontal(g42)
    c: Coincident(g43,g9)
    c: Coincident(g43,g23)
    c: Horizontal(g43)
    c: Coincident(g44,g10)
    c: Coincident(g44,g22)
    c: Horizontal(g44)
    c: Coincident(g45,g10)
    c: Coincident(g45,g22)
    c: Horizontal(g45)
    c: Coincident(g46,g11)
    c: Coincident(g46,g21)
    c: Horizontal(g46)
    c: Coincident(g47,g11)
    c: Coincident(g47,g21)
    c: Horizontal(g47)
FEATURE [Part::Extrusion] Extrude046
  Base = -> Sketch055
  Dir = (1,0,0)
  DirMode = 2
  FaceMakerClass = Part::FaceMakerBullseye
  LengthFwd = 23
  LengthRev = 0
  Placement = pos=(-19,0,0) rot=(0,0,1;0rad)
  Solid = true
  Symmetric = false
FEATURE [Part::Fillet] Fillet038  label="removeToCreateVentalationHoles001"
  Base = -> Extrude046
  Edges = <same value as first occurrence — deduplicated (x6 in doc)>
  Placement = pos=(7,0,0) rot=(0,0,1;0rad)
FEATURE [Sketcher::SketchObject] Sketch056  label="topSketch014"
  FullyConstrained = true
  sketch-geometry (22):
    g0: LineSegment StartX=5.21097e-06 StartY=3 StartZ=0 EndX=5.21097e-06 EndY=19 EndZ=0
    g1: ArcOfCircle CenterX=19 CenterY=19 CenterZ=0 NormalX=0 NormalY=0 NormalZ=1 AngleXU=0 Radius=19 StartAngle=1.5708 EndAngle=3.14159
    g2: ArcOfCircle CenterX=19 CenterY=19 CenterZ=0 NormalX=0 NormalY=0 NormalZ=1 AngleXU=0 Radius=16 StartAngle=1.5708 EndAngle=3.14159
    g3: LineSegment StartX=114 StartY=35 StartZ=0 EndX=19 EndY=35 EndZ=0
    g4: LineSegment StartX=5.21097e-06 StartY=3 StartZ=0 EndX=5.21097e-06 EndY=0 EndZ=0
    g5: LineSegment StartX=3 StartY=0 StartZ=0 EndX=5.21097e-06 EndY=0 EndZ=0
    g6: LineSegment StartX=3 StartY=19 StartZ=0 EndX=3 EndY=0 EndZ=0
    g7: LineSegment StartX=19 StartY=38 StartZ=0 EndX=124 EndY=38 EndZ=0
    g8: Circle CenterX=119 CenterY=35 CenterZ=0 NormalX=0 NormalY=0 NormalZ=1 AngleXU=0 Radius=1
    g9: Circle CenterX=121 CenterY=35 CenterZ=0 NormalX=0 NormalY=0 NormalZ=1 AngleXU=0 Radius=1
    g10: Circle CenterX=121 CenterY=33 CenterZ=0 NormalX=0 NormalY=0 NormalZ=1 AngleXU=0 Radius=1
    g11: BSplineCurve PolesCount=3 KnotsCount=2 Degree=2 IsPeriodic=0
    g12: GeomPoint X=119 Y=35 Z=0
    g13: GeomPoint X=121 Y=33 Z=0
    g14: LineSegment StartX=119 StartY=35 StartZ=0 EndX=114 EndY=35 EndZ=0
    g15: ArcOfCircle CenterX=105 CenterY=19 CenterZ=0 NormalX=0 NormalY=0 NormalZ=1 AngleXU=0 Radius=16 StartAngle=5.60905 EndAngle=6.28319
    g16: LineSegment StartX=121 StartY=33 StartZ=0 EndX=121 EndY=19 EndZ=0
    g17: LineSegment StartX=117.5 StartY=9.01251 StartZ=0 EndX=121.163 EndY=9.0125 EndZ=0
    g18: ArcOfCircle CenterX=105 CenterY=19 CenterZ=0 NormalX=0 NormalY=0 NormalZ=1 AngleXU=0 Radius=20.6155 StartAngle=5.7297 EndAngle=6.28319
    g19: LineSegment StartX=121.163 StartY=9.0125 StartZ=0 EndX=122.538 EndY=8.16329 EndZ=0
    g20: LineSegment StartX=124 StartY=38 StartZ=0 EndX=125.616 EndY=38 EndZ=0
    g21: LineSegment StartX=125.616 StartY=19 StartZ=0 EndX=125.616 EndY=38 EndZ=0
  constraints (49):
    c: Vertical(g0)
    c: Block(g0)
    c: Coincident(g1,g0)
    c: Block(g1)
    c: Coincident(g2,g1)
    c: Block(g2)
    c: Coincident(g3,g2)
    c: Horizontal(g3)
    c: Tangent(g3,g2)
    c: Coincident(g4,g0)
    c: Distance(g4) = 3
    c: Vertical(g4)
    c: Coincident(g5,g4)
    c: Horizontal(g5)
    c: Coincident(g6,g2)
    c: Coincident(g6,g5)
    c: Vertical(g6)
    c: Horizontal(g7)
    c: Distance(g7) = 105
    c: Coincident(g7,g1)
    c: Block(g3)
    c: Weight(g8) = 1
    c: Equal(g8,g9)
    c: Equal(g8,g10)
    c: InternalAlignment(g8,g11)
    c: InternalAlignment(g9,g11)
    c: InternalAlignment(g10,g11)
    c: InternalAlignment(g12,g11)
    c: InternalAlignment(g13,g11)
    c: Block(g11)
    c: Coincident(g14,g11)
    c: Coincident(g14,g3)
    c: Horizontal(g14)
    c: Block(g15)
    c: Coincident(g16,g11)
    c: Coincident(g16,g15)
    c: Vertical(g16)
    c: Distance(g16) = 14
    c: Coincident(g17,g15)
    c: Block(g18)
    c: Coincident(g19,g18)
    c: Coincident(g20,g7)
    c: Horizontal(g20)
    c: Vertical(g21)
    c: Coincident(g20,g21)
    c: Block(g20)
    c: Block(g21)
    c: Block(g19)
    c: Block(g17)
FEATURE [Part::Box] Box026  label="removeToCreteHoleForPlugHousing032"
  AttacherType = Attacher::AttachEngine3D
  Height = 28.6
  Length = 10
  Placement = pos=(-2,0,21.7) rot=(0,0,1;0rad)
  Width = 19
FEATURE [Part::Feature] Face109 .. Face112  x4 (patterned run collapsed; names and placements below)
  shape: bbox 3.5 x 17.8 x 2e-07 mm, 1 faces, 0 solids (baked)
FEATURE [Part::Revolution] Revolve117  label="removeToCreateScrewAndThreadedInsertHole045"
  Angle = 360
  Axis = (0,1,0)
  Base = (0,0,0)
  FaceMakerClass = Part::FaceMakerBullseye
  Placement = pos=(62.3,30.3,19.7) rot=(0,0,1;0rad)
  Solid = false
  Source = -> Face109
  Symmetric = false
FEATURE [Part::Revolution] Revolve118  label="removeToCreateScrewAndThreadedInsertHole046"
  Angle = 360
  Axis = (0,1,0)
  Base = (0,0,0)
  FaceMakerClass = Part::FaceMakerBullseye
  Placement = pos=(62.3,30.3,51.7) rot=(0,0,1;0rad)
  Solid = false
  Source = -> Face110
  Symmetric = false
FEATURE [Part::Revolution] Revolve119  label="removeToCreateScrewAndThreadedInsertHole047"
  Angle = 360
  Axis = (0,1,0)
  Base = (0,0,0)
  FaceMakerClass = Part::FaceMakerBullseye
  Placement = pos=(30.3,30.3,19.7) rot=(0,0,1;0rad)
  Solid = false
  Source = -> Face111
  Symmetric = false
FEATURE [Part::Revolution] Revolve120  label="removeToCreateScrewAndThreadedInsertHole048"
  Angle = 360
  Axis = (0,1,0)
  Base = (0,0,0)
  FaceMakerClass = Part::FaceMakerBullseye
  Placement = pos=(30.3,30.3,51.7) rot=(0,0,1;0rad)
  Solid = false
  Source = -> Face112
  Symmetric = false
FEATURE [Part::MultiFuse] Fusion087  label="createThreadedInsertHolesForFan005"
  Shapes = -> [Revolve117,Revolve118,Revolve119,Revolve120]
FEATURE [Part::Extrusion] Extrude047
  Base = -> Sketch056
  Dir = (0,0,1)
  DirMode = 2
  FaceMakerClass = Part::FaceMakerBullseye
  LengthFwd = 72
  LengthRev = 0
  Solid = true
  Symmetric = false
FEATURE [Part::Fillet] Fillet039  label="top019"
  Base = -> Extrude047
  Edges = 1 edges r=2: [Edge35]
FEATURE [Sketcher::SketchObject] Sketch057
  FullyConstrained = false
  Placement = pos=(0,0,0) rot=(1,0,0;1.5708rad)
  sketch-geometry (24):
    g0: ArcOfCircle CenterX=-4 CenterY=-10.5 CenterZ=0 NormalX=0 NormalY=0 NormalZ=1 AngleXU=0 Radius=1.5 StartAngle=6e-16 EndAngle=3.14159
    g1: ArcOfCircle CenterX=-34.2 CenterY=-10.5 CenterZ=0 NormalX=0 NormalY=0 NormalZ=1 AngleXU=0 Radius=1.5 StartAngle=0 EndAngle=3.14159
    g2: ArcOfCircle CenterX=-34.2 CenterY=-27.7 CenterZ=0 NormalX=0 NormalY=0 NormalZ=1 AngleXU=0 Radius=1.5 StartAngle=3.14159 EndAngle=6.28319
    g3: ArcOfCircle CenterX=-4 CenterY=-27.7 CenterZ=0 NormalX=0 NormalY=0 NormalZ=1 AngleXU=0 Radius=1.5 StartAngle=3.1416 EndAngle=6.28319
    g4: ArcOfCircle CenterX=-10 CenterY=-4.3 CenterZ=0 NormalX=0 NormalY=0 NormalZ=1 AngleXU=0 Radius=1.5 StartAngle=2e-16 EndAngle=3.14159
    g5: ArcOfCircle CenterX=-16.1 CenterY=-1.8 CenterZ=0 NormalX=0 NormalY=0 NormalZ=1 AngleXU=0 Radius=1.5 StartAngle=5e-16 EndAngle=3.14159
    g6: ArcOfCircle CenterX=-22.1 CenterY=-1.8 CenterZ=0 NormalX=0 NormalY=0 NormalZ=1 AngleXU=0 Radius=1.5 StartAngle=5e-16 EndAngle=3.14159
    g7: ArcOfCircle CenterX=-28.2 CenterY=-4.3 CenterZ=0 NormalX=0 NormalY=0 NormalZ=1 AngleXU=0 Radius=1.5 StartAngle=2e-16 EndAngle=3.14159
    g8: ArcOfCircle CenterX=-10 CenterY=-33.9 CenterZ=0 NormalX=0 NormalY=0 NormalZ=1 AngleXU=0 Radius=1.5 StartAngle=3.14159 EndAngle=6.28319
    g9: ArcOfCircle CenterX=-16.1 CenterY=-36.4 CenterZ=0 NormalX=0 NormalY=0 NormalZ=1 AngleXU=0 Radius=1.5 StartAngle=3.14159 EndAngle=6.28319
    g10: ArcOfCircle CenterX=-22.1 CenterY=-36.4 CenterZ=0 NormalX=0 NormalY=0 NormalZ=1 AngleXU=0 Radius=1.5 StartAngle=3.14159 EndAngle=6.28319
    g11: ArcOfCircle CenterX=-28.2 CenterY=-33.9 CenterZ=0 NormalX=0 NormalY=0 NormalZ=1 AngleXU=0 Radius=1.5 StartAngle=3.14159 EndAngle=6.28319
    g12: LineSegment StartX=-35.7 StartY=-10.5 StartZ=0 EndX=-35.7 EndY=-27.7 EndZ=0
    g13: LineSegment StartX=-32.7 StartY=-10.5 StartZ=0 EndX=-32.7 EndY=-27.7 EndZ=0
    g14: LineSegment StartX=-29.7 StartY=-33.9 StartZ=0 EndX=-29.7 EndY=-4.3 EndZ=0
    g15: LineSegment StartX=-26.7 StartY=-33.9 StartZ=0 EndX=-26.7 EndY=-4.3 EndZ=0
    g16: LineSegment StartX=-2.5 StartY=-10.5 StartZ=0 EndX=-2.5 EndY=-27.7 EndZ=0
    g17: LineSegment StartX=-8.5 StartY=-4.3 StartZ=0 EndX=-8.5 EndY=-33.9 EndZ=0
    g18: LineSegment StartX=-5.5 StartY=-10.5 StartZ=0 EndX=-5.5 EndY=-27.7 EndZ=0
    g19: LineSegment StartX=-11.5 StartY=-4.3 StartZ=0 EndX=-11.5 EndY=-33.9 EndZ=0
    g20: LineSegment StartX=-14.6 StartY=-1.8 StartZ=0 EndX=-14.6 EndY=-36.4 EndZ=0
    g21: LineSegment StartX=-17.6 StartY=-1.8 StartZ=0 EndX=-17.6 EndY=-36.4 EndZ=0
    g22: LineSegment StartX=-20.6 StartY=-36.4 StartZ=0 EndX=-20.6 EndY=-1.8 EndZ=0
    g23: LineSegment StartX=-23.6 StartY=-1.8 StartZ=0 EndX=-23.6 EndY=-36.4 EndZ=0
  constraints (48):
    c: Block(g0)
    c: Block(g1)
    c: Block(g2)
    c: Block(g3)
    c: Block(g4)
    c: Block(g5)
    c: Block(g6)
    c: Block(g7)
    c: Block(g8)
    c: Block(g9)
    c: Block(g10)
    c: Block(g11)
    c: Coincident(g12,g1)
    c: Coincident(g12,g2)
    c: Vertical(g12)
    c: Coincident(g13,g1)
    c: Coincident(g13,g2)
    c: Vertical(g13)
    c: Coincident(g14,g11)
    c: Coincident(g14,g7)
    c: Vertical(g14)
    c: Coincident(g15,g11)
    c: Coincident(g15,g7)
    c: Vertical(g15)
    c: Coincident(g16,g0)
    c: Coincident(g16,g3)
    c: Vertical(g16)
    c: Coincident(g17,g4)
    c: Coincident(g17,g8)
    c: Vertical(g17)
    c: Coincident(g18,g0)
    c: Coincident(g18,g3)
    c: Vertical(g18)
    c: Coincident(g19,g4)
    c: Coincident(g19,g8)
    c: Vertical(g19)
    c: Coincident(g20,g5)
    c: Coincident(g20,g9)
    c: Vertical(g20)
    c: Coincident(g21,g5)
    c: Coincident(g21,g9)
    c: Vertical(g21)
    c: Coincident(g22,g10)
    c: Coincident(g22,g6)
    c: Vertical(g22)
    c: Coincident(g23,g6)
    c: Coincident(g23,g10)
    c: Vertical(g23)
FEATURE [Part::Extrusion] Extrude048  label="removeToCreateFanGrillHoles004"
  Base = -> Sketch057
  Dir = (0,-1,6e-16)
  DirMode = 2
  FaceMakerClass = Part::FaceMakerBullseye
  LengthFwd = 10
  LengthRev = 0
  Placement = pos=(65.4,44,54.82) rot=(0,0,1;0rad)
  Solid = true
  Symmetric = false
FEATURE [Part::Cut] Cut040  label="top021"
  Base = -> Fillet039
  Tool = -> Extrude048
FEATURE [Part::Cylinder] Cylinder041  label="removeToCreteHoleForPlugHousing034"
  Angle = 360
  AttacherType = Attacher::AttachEngine3D
  Height = 20
  Placement = pos=(-2,19,36) rot=(0,1,0;1.5708rad)
  Radius = 14.3
FEATURE [Part::MultiFuse] Fusion089  label="removeToCreteHoleForPlugHousing035"
  Shapes = -> [Box026,Cylinder041]
FEATURE [Part::Cylinder] Cylinder042
  Angle = 360
  AttacherType = Attacher::AttachEngine3D
  Height = 20
  Placement = pos=(0,0,36.15) rot=(0,0,1;0rad)
  Radius = 14.3
FEATURE [Part::Cylinder] Cylinder043
  Angle = 360
  AttacherType = Attacher::AttachEngine3D
  Height = 10
  Placement = pos=(0,0,36.15) rot=(0,0,1;0rad)
  Radius = 4
FEATURE [Part::Box] Box027  label="removeToCreteHoleForPlugHousing036"
  AttacherType = Attacher::AttachEngine3D
  Height = 28.6
  Length = 20
  Placement = pos=(106.15,0,21.7) rot=(0,0,1;0rad)
  Width = 19
FEATURE [Part::Cut] Cut041  label="top022"
  Base = -> Cut040
  Tool = -> Fusion087
FEATURE [Part::Cut] Cut039  label="top020"
  Base = -> Cut041
  Tool = -> Fusion089
FEATURE [Part::MultiFuse] Fusion090  label="removeToCreteHoleForPlugHousing037"
  Placement = pos=(70,19,36) rot=(0,1,0;1.5708rad)
  Shapes = -> [Cylinder042,Cylinder043]
FEATURE [Part::MultiFuse] Fusion088  label="removeToCreteHoleForPlugHousing033"
  Shapes = -> [Box027,Fusion090]
FEATURE [Part::Cut] Cut042  label="removeToCreteHoleForPlugHousing038"
  Base = -> Cut039
  Tool = -> Fusion088
FEATURE [Part::MultiFuse] Fusion091  label="removeFromTop"
  Shapes = -> [Fillet038,Fusion085,Fusion084,Fusion083,Extrude045]
FEATURE [Part::Cut] Cut043  label="REAL TOP ====="
  Base = -> Fillet036
  Tool = -> Fusion091
FEATURE [Part::MultiFuse] Fusion092  label="caseScrewPillarBracket016"
  Shapes = -> [Extrude030,Extrude031,Extrude032,Extrude033,Extrude034,Extrude035,Extrude036,Extrude037,Box013,Box014]
FEATURE [Sketcher::SketchObject] Sketch058  label="topSketch015"
  FullyConstrained = true
  sketch-geometry (20):
    g0: LineSegment StartX=5.21097e-06 StartY=3 StartZ=0 EndX=5.21097e-06 EndY=19 EndZ=0
    g1: ArcOfCircle CenterX=19 CenterY=19 CenterZ=0 NormalX=0 NormalY=0 NormalZ=1 AngleXU=0 Radius=19 StartAngle=1.5708 EndAngle=3.14159
    g2: ArcOfCircle CenterX=19 CenterY=19 CenterZ=0 NormalX=0 NormalY=0 NormalZ=1 AngleXU=0 Radius=16 StartAngle=1.5708 EndAngle=3.14159
    g3: LineSegment StartX=114 StartY=35 StartZ=0 EndX=19 EndY=35 EndZ=0
    g4: LineSegment StartX=5.21097e-06 StartY=3 StartZ=0 EndX=5.21097e-06 EndY=0 EndZ=0
    g5: LineSegment StartX=3 StartY=0 StartZ=0 EndX=5.21097e-06 EndY=0 EndZ=0
    g6: LineSegment StartX=3 StartY=19 StartZ=0 EndX=3 EndY=0 EndZ=0
    g7: LineSegment StartX=19 StartY=38 StartZ=0 EndX=124 EndY=38 EndZ=0
    g8: Circle CenterX=119 CenterY=35 CenterZ=0 NormalX=0 NormalY=0 NormalZ=1 AngleXU=0 Radius=1
    g9: Circle CenterX=121 CenterY=35 CenterZ=0 NormalX=0 NormalY=0 NormalZ=1 AngleXU=0 Radius=1
    g10: Circle CenterX=121 CenterY=33 CenterZ=0 NormalX=0 NormalY=0 NormalZ=1 AngleXU=0 Radius=1
    g11: BSplineCurve PolesCount=3 KnotsCount=2 Degree=2 IsPeriodic=0
    g12: GeomPoint X=119 Y=35 Z=0
    g13: GeomPoint X=121 Y=33 Z=0
    g14: LineSegment StartX=119 StartY=35 StartZ=0 EndX=114 EndY=35 EndZ=0
    g15: ArcOfCircle CenterX=105 CenterY=19 CenterZ=0 NormalX=0 NormalY=0 NormalZ=1 AngleXU=0 Radius=19 StartAngle=5.7297 EndAngle=6.28319
    g16: ArcOfCircle CenterX=105 CenterY=19 CenterZ=0 NormalX=0 NormalY=0 NormalZ=1 AngleXU=0 Radius=16 StartAngle=5.60905 EndAngle=6.28319
    g17: LineSegment StartX=121 StartY=33 StartZ=0 EndX=121 EndY=19 EndZ=0
    g18: LineSegment StartX=124 StartY=38 StartZ=0 EndX=124 EndY=19 EndZ=0
    g19: LineSegment StartX=117.5 StartY=9.01251 StartZ=0 EndX=121.163 EndY=9.0125 EndZ=0
  constraints (46):
    c: Vertical(g0)
    c: Block(g0)
    c: Coincident(g1,g0)
    c: Block(g1)
    c: Coincident(g2,g1)
    c: Block(g2)
    c: Coincident(g3,g2)
    c: Horizontal(g3)
    c: Tangent(g3,g2)
    c: Coincident(g4,g0)
    c: Distance(g4) = 3
    c: Vertical(g4)
    c: Coincident(g5,g4)
    c: Horizontal(g5)
    c: Coincident(g6,g2)
    c: Coincident(g6,g5)
    c: Vertical(g6)
    c: Horizontal(g7)
    c: Distance(g7) = 105
    c: Coincident(g7,g1)
    c: Block(g3)
    c: Weight(g8) = 1
    c: Equal(g8,g9)
    c: Equal(g8,g10)
    c: InternalAlignment(g8,g11)
    c: InternalAlignment(g9,g11)
    c: InternalAlignment(g10,g11)
    c: InternalAlignment(g12,g11)
    c: InternalAlignment(g13,g11)
    c: Block(g11)
    c: Coincident(g14,g11)
    c: Coincident(g14,g3)
    c: Horizontal(g14)
    c: Block(g15)
    c: Coincident(g16,g15)
    c: Block(g16)
    c: Coincident(g17,g11)
    c: Coincident(g17,g16)
    c: Vertical(g17)
    c: Distance(g17) = 14
    c: Coincident(g18,g7)
    c: Coincident(g18,g15)
    c: Vertical(g18)
    c: Distance(g18) = 19
    c: Coincident(g19,g16)
    c: Coincident(g19,g15)
FEATURE [Part::Extrusion] Extrude049  label="top023"
  Base = -> Sketch058
  Dir = (0,0,1)
  DirMode = 2
  FaceMakerClass = Part::FaceMakerBullseye
  LengthFwd = 72
  LengthRev = 0
  Solid = true
  Symmetric = false
FEATURE [Sketcher::SketchObject] Sketch059
  FullyConstrained = true
  MapMode = 3
  Placement = pos=(0,0,0) rot=(1,0,0;1.5708rad)
  Support = -> [Extrude049]
  sketch-geometry (8):
    g0: Circle CenterX=80.351 CenterY=-67.6202 CenterZ=0 NormalX=0 NormalY=0 NormalZ=1 AngleXU=0 Radius=2
    g1: Circle CenterX=80.351 CenterY=-67.6202 CenterZ=0 NormalX=0 NormalY=0 NormalZ=1 AngleXU=0 Radius=3
    g2: Circle CenterX=80.351 CenterY=-4.92017 CenterZ=0 NormalX=0 NormalY=0 NormalZ=1 AngleXU=0 Radius=2
    g3: Circle CenterX=80.351 CenterY=-4.92017 CenterZ=0 NormalX=0 NormalY=0 NormalZ=1 AngleXU=0 Radius=3
    g4: Circle CenterX=23.851 CenterY=-4.92017 CenterZ=0 NormalX=0 NormalY=0 NormalZ=1 AngleXU=0 Radius=2
    g5: Circle CenterX=23.851 CenterY=-4.92017 CenterZ=0 NormalX=0 NormalY=0 NormalZ=1 AngleXU=0 Radius=3
    g6: Circle CenterX=23.851 CenterY=-67.6202 CenterZ=0 NormalX=0 NormalY=0 NormalZ=1 AngleXU=0 Radius=2
    g7: Circle CenterX=23.851 CenterY=-67.6202 CenterZ=0 NormalX=0 NormalY=0 NormalZ=1 AngleXU=0 Radius=3
  constraints (8):
    c: Block(g3)
    c: Block(g2)
    c: Block(g1)
    c: Block(g0)
    c: Block(g6)
    c: Block(g7)
    c: Block(g4)
    c: Block(g5)
FEATURE [Sketcher::SketchObject] Sketch060
  FullyConstrained = true
  MapMode = 3
  Placement = pos=(0,0,0) rot=(1,0,0;1.5708rad)
  Support = -> [Extrude049]
  sketch-geometry (8):
    g0: Circle CenterX=80.351 CenterY=-67.6202 CenterZ=0 NormalX=0 NormalY=0 NormalZ=1 AngleXU=0 Radius=3
    g1: Circle CenterX=80.351 CenterY=-4.92017 CenterZ=0 NormalX=0 NormalY=0 NormalZ=1 AngleXU=0 Radius=3
    g2: Circle CenterX=23.851 CenterY=-4.92017 CenterZ=0 NormalX=0 NormalY=0 NormalZ=1 AngleXU=0 Radius=3
    g3: Circle CenterX=23.851 CenterY=-67.6202 CenterZ=0 NormalX=0 NormalY=0 NormalZ=1 AngleXU=0 Radius=3
    g4: Circle CenterX=23.851 CenterY=-67.6202 CenterZ=0 NormalX=0 NormalY=0 NormalZ=1 AngleXU=0 Radius=5
    g5: Circle CenterX=80.351 CenterY=-67.6202 CenterZ=0 NormalX=0 NormalY=0 NormalZ=1 AngleXU=0 Radius=5
    g6: Circle CenterX=23.851 CenterY=-4.92017 CenterZ=0 NormalX=0 NormalY=0 NormalZ=1 AngleXU=0 Radius=5
    g7: Circle CenterX=80.351 CenterY=-4.92017 CenterZ=0 NormalX=0 NormalY=0 NormalZ=1 AngleXU=0 Radius=5
  constraints (8):
    c: Block(g1)
    c: Block(g0)
    c: Block(g3)
    c: Block(g2)
    c: Block(g5)
    c: Block(g4)
    c: Block(g6)
    c: Block(g7)
FEATURE [Sketcher::SketchObject] Sketch061
  FullyConstrained = true
  MapMode = 3
  Placement = pos=(0,0,0) rot=(1,0,0;1.5708rad)
  sketch-geometry (8):
    g0: Circle CenterX=80.351 CenterY=-67.6202 CenterZ=0 NormalX=0 NormalY=0 NormalZ=1 AngleXU=0 Radius=3
    g1: Circle CenterX=80.351 CenterY=-4.92017 CenterZ=0 NormalX=0 NormalY=0 NormalZ=1 AngleXU=0 Radius=3
    g2: Circle CenterX=23.851 CenterY=-4.92017 CenterZ=0 NormalX=0 NormalY=0 NormalZ=1 AngleXU=0 Radius=3
    g3: Circle CenterX=23.851 CenterY=-67.6202 CenterZ=0 NormalX=0 NormalY=0 NormalZ=1 AngleXU=0 Radius=3
    g4: Circle CenterX=23.851 CenterY=-67.6202 CenterZ=0 NormalX=0 NormalY=0 NormalZ=1 AngleXU=0 Radius=5
    g5: Circle CenterX=80.351 CenterY=-67.6202 CenterZ=0 NormalX=0 NormalY=0 NormalZ=1 AngleXU=0 Radius=5
    g6: Circle CenterX=23.851 CenterY=-4.92017 CenterZ=0 NormalX=0 NormalY=0 NormalZ=1 AngleXU=0 Radius=5
    g7: Circle CenterX=80.351 CenterY=-4.92017 CenterZ=0 NormalX=0 NormalY=0 NormalZ=1 AngleXU=0 Radius=5
  constraints (8):
    c: Block(g1)
    c: Block(g0)
    c: Block(g3)
    c: Block(g2)
    c: Block(g5)
    c: Block(g4)
    c: Block(g6)
    c: Block(g7)
FEATURE [Sketcher::SketchObject] Sketch062  label="topSketch016"
  FullyConstrained = true
  sketch-geometry (20):
    g0: LineSegment StartX=5.21097e-06 StartY=3 StartZ=0 EndX=5.21097e-06 EndY=19 EndZ=0
    g1: ArcOfCircle CenterX=19 CenterY=19 CenterZ=0 NormalX=0 NormalY=0 NormalZ=1 AngleXU=0 Radius=19 StartAngle=1.5708 EndAngle=3.14159
    g2: ArcOfCircle CenterX=19 CenterY=19 CenterZ=0 NormalX=0 NormalY=0 NormalZ=1 AngleXU=0 Radius=16 StartAngle=1.5708 EndAngle=3.14159
    g3: LineSegment StartX=114 StartY=35 StartZ=0 EndX=19 EndY=35 EndZ=0
    g4: LineSegment StartX=5.21097e-06 StartY=3 StartZ=0 EndX=5.21097e-06 EndY=0 EndZ=0
    g5: LineSegment StartX=3 StartY=0 StartZ=0 EndX=5.21097e-06 EndY=0 EndZ=0
    g6: LineSegment StartX=3 StartY=19 StartZ=0 EndX=3 EndY=0 EndZ=0
    g7: LineSegment StartX=19 StartY=38 StartZ=0 EndX=124 EndY=38 EndZ=0
    g8: Circle CenterX=119 CenterY=35 CenterZ=0 NormalX=0 NormalY=0 NormalZ=1 AngleXU=0 Radius=1
    g9: Circle CenterX=121 CenterY=35 CenterZ=0 NormalX=0 NormalY=0 NormalZ=1 AngleXU=0 Radius=1
    g10: Circle CenterX=121 CenterY=33 CenterZ=0 NormalX=0 NormalY=0 NormalZ=1 AngleXU=0 Radius=1
    g11: BSplineCurve PolesCount=3 KnotsCount=2 Degree=2 IsPeriodic=0
    g12: GeomPoint X=119 Y=35 Z=0
    g13: GeomPoint X=121 Y=33 Z=0
    g14: LineSegment StartX=119 StartY=35 StartZ=0 EndX=114 EndY=35 EndZ=0
    g15: ArcOfCircle CenterX=105 CenterY=19 CenterZ=0 NormalX=0 NormalY=0 NormalZ=1 AngleXU=0 Radius=19 StartAngle=5.7297 EndAngle=6.28319
    g16: ArcOfCircle CenterX=105 CenterY=19 CenterZ=0 NormalX=0 NormalY=0 NormalZ=1 AngleXU=0 Radius=16 StartAngle=5.60905 EndAngle=6.28319
    g17: LineSegment StartX=121 StartY=33 StartZ=0 EndX=121 EndY=19 EndZ=0
    g18: LineSegment StartX=124 StartY=38 StartZ=0 EndX=124 EndY=19 EndZ=0
    g19: LineSegment StartX=117.5 StartY=9.01251 StartZ=0 EndX=121.163 EndY=9.0125 EndZ=0
  constraints (46):
    c: Vertical(g0)
    c: Block(g0)
    c: Coincident(g1,g0)
    c: Block(g1)
    c: Coincident(g2,g1)
    c: Block(g2)
    c: Coincident(g3,g2)
    c: Horizontal(g3)
    c: Tangent(g3,g2)
    c: Coincident(g4,g0)
    c: Distance(g4) = 3
    c: Vertical(g4)
    c: Coincident(g5,g4)
    c: Horizontal(g5)
    c: Coincident(g6,g2)
    c: Coincident(g6,g5)
    c: Vertical(g6)
    c: Horizontal(g7)
    c: Distance(g7) = 105
    c: Coincident(g7,g1)
    c: Block(g3)
    c: Weight(g8) = 1
    c: Equal(g8,g9)
    c: Equal(g8,g10)
    c: InternalAlignment(g8,g11)
    c: InternalAlignment(g9,g11)
    c: InternalAlignment(g10,g11)
    c: InternalAlignment(g12,g11)
    c: InternalAlignment(g13,g11)
    c: Block(g11)
    c: Coincident(g14,g11)
    c: Coincident(g14,g3)
    c: Horizontal(g14)
    c: Block(g15)
    c: Coincident(g16,g15)
    c: Block(g16)
    c: Coincident(g17,g11)
    c: Coincident(g17,g16)
    c: Vertical(g17)
    c: Distance(g17) = 14
    c: Coincident(g18,g7)
    c: Coincident(g18,g15)
    c: Vertical(g18)
    c: Distance(g18) = 19
    c: Coincident(g19,g16)
    c: Coincident(g19,g15)
FEATURE [Part::Extrusion] Extrude053  label="top024"
  Base = -> Sketch062
  Dir = (0,0,1)
  DirMode = 2
  FaceMakerClass = Part::FaceMakerBullseye
  LengthFwd = 72
  LengthRev = 0
  Solid = true
  Symmetric = false
FEATURE [Sketcher::SketchObject] Sketch063
  FullyConstrained = true
  MapMode = 3
  Placement = pos=(0,0,0) rot=(1,0,0;1.5708rad)
  Support = -> [Extrude053]
  sketch-geometry (8):
    g0: Circle CenterX=80.351 CenterY=-67.6202 CenterZ=0 NormalX=0 NormalY=0 NormalZ=1 AngleXU=0 Radius=2
    g1: Circle CenterX=80.351 CenterY=-67.6202 CenterZ=0 NormalX=0 NormalY=0 NormalZ=1 AngleXU=0 Radius=3
    g2: Circle CenterX=80.351 CenterY=-4.92017 CenterZ=0 NormalX=0 NormalY=0 NormalZ=1 AngleXU=0 Radius=2
    g3: Circle CenterX=80.351 CenterY=-4.92017 CenterZ=0 NormalX=0 NormalY=0 NormalZ=1 AngleXU=0 Radius=3
    g4: Circle CenterX=23.851 CenterY=-4.92017 CenterZ=0 NormalX=0 NormalY=0 NormalZ=1 AngleXU=0 Radius=2
    g5: Circle CenterX=23.851 CenterY=-4.92017 CenterZ=0 NormalX=0 NormalY=0 NormalZ=1 AngleXU=0 Radius=3
    g6: Circle CenterX=23.851 CenterY=-67.6202 CenterZ=0 NormalX=0 NormalY=0 NormalZ=1 AngleXU=0 Radius=2
    g7: Circle CenterX=23.851 CenterY=-67.6202 CenterZ=0 NormalX=0 NormalY=0 NormalZ=1 AngleXU=0 Radius=3
  constraints (8):
    c: Block(g3)
    c: Block(g2)
    c: Block(g1)
    c: Block(g0)
    c: Block(g6)
    c: Block(g7)
    c: Block(g4)
    c: Block(g5)
FEATURE [Part::Extrusion] Extrude054
  Base = -> Sketch063
  Dir = (0,-1,2e-16)
  DirMode = 2
  FaceMakerClass = Part::FaceMakerBullseye
  LengthFwd = 6
  LengthRev = 0
  Placement = pos=(0,9,0) rot=(0,0,1;0rad)
  Solid = true
  Symmetric = false
FEATURE [Sketcher::SketchObject] Sketch064  label="topSketch017"
  FullyConstrained = true
  sketch-geometry (20):
    g0: LineSegment StartX=5.21097e-06 StartY=3 StartZ=0 EndX=5.21097e-06 EndY=19 EndZ=0
    g1: ArcOfCircle CenterX=19 CenterY=19 CenterZ=0 NormalX=0 NormalY=0 NormalZ=1 AngleXU=0 Radius=19 StartAngle=1.5708 EndAngle=3.14159
    g2: ArcOfCircle CenterX=19 CenterY=19 CenterZ=0 NormalX=0 NormalY=0 NormalZ=1 AngleXU=0 Radius=16 StartAngle=1.5708 EndAngle=3.14159
    g3: LineSegment StartX=114 StartY=35 StartZ=0 EndX=19 EndY=35 EndZ=0
    g4: LineSegment StartX=5.21097e-06 StartY=3 StartZ=0 EndX=5.21097e-06 EndY=0 EndZ=0
    g5: LineSegment StartX=3 StartY=0 StartZ=0 EndX=5.21097e-06 EndY=0 EndZ=0
    g6: LineSegment StartX=3 StartY=19 StartZ=0 EndX=3 EndY=0 EndZ=0
    g7: LineSegment StartX=19 StartY=38 StartZ=0 EndX=124 EndY=38 EndZ=0
    g8: Circle CenterX=119 CenterY=35 CenterZ=0 NormalX=0 NormalY=0 NormalZ=1 AngleXU=0 Radius=1
    g9: Circle CenterX=121 CenterY=35 CenterZ=0 NormalX=0 NormalY=0 NormalZ=1 AngleXU=0 Radius=1
    g10: Circle CenterX=121 CenterY=33 CenterZ=0 NormalX=0 NormalY=0 NormalZ=1 AngleXU=0 Radius=1
    g11: BSplineCurve PolesCount=3 KnotsCount=2 Degree=2 IsPeriodic=0
    g12: GeomPoint X=119 Y=35 Z=0
    g13: GeomPoint X=121 Y=33 Z=0
    g14: LineSegment StartX=119 StartY=35 StartZ=0 EndX=114 EndY=35 EndZ=0
    g15: ArcOfCircle CenterX=105 CenterY=19 CenterZ=0 NormalX=0 NormalY=0 NormalZ=1 AngleXU=0 Radius=19 StartAngle=5.7297 EndAngle=6.28319
    g16: ArcOfCircle CenterX=105 CenterY=19 CenterZ=0 NormalX=0 NormalY=0 NormalZ=1 AngleXU=0 Radius=16 StartAngle=5.60905 EndAngle=6.28319
    g17: LineSegment StartX=121 StartY=33 StartZ=0 EndX=121 EndY=19 EndZ=0
    g18: LineSegment StartX=124 StartY=38 StartZ=0 EndX=124 EndY=19 EndZ=0
    g19: LineSegment StartX=117.5 StartY=9.01251 StartZ=0 EndX=121.163 EndY=9.0125 EndZ=0
  constraints (46):
    c: Vertical(g0)
    c: Block(g0)
    c: Coincident(g1,g0)
    c: Block(g1)
    c: Coincident(g2,g1)
    c: Block(g2)
    c: Coincident(g3,g2)
    c: Horizontal(g3)
    c: Tangent(g3,g2)
    c: Coincident(g4,g0)
    c: Distance(g4) = 3
    c: Vertical(g4)
    c: Coincident(g5,g4)
    c: Horizontal(g5)
    c: Coincident(g6,g2)
    c: Coincident(g6,g5)
    c: Vertical(g6)
    c: Horizontal(g7)
    c: Distance(g7) = 105
    c: Coincident(g7,g1)
    c: Block(g3)
    c: Weight(g8) = 1
    c: Equal(g8,g9)
    c: Equal(g8,g10)
    c: InternalAlignment(g8,g11)
    c: InternalAlignment(g9,g11)
    c: InternalAlignment(g10,g11)
    c: InternalAlignment(g12,g11)
    c: InternalAlignment(g13,g11)
    c: Block(g11)
    c: Coincident(g14,g11)
    c: Coincident(g14,g3)
    c: Horizontal(g14)
    c: Block(g15)
    c: Coincident(g16,g15)
    c: Block(g16)
    c: Coincident(g17,g11)
    c: Coincident(g17,g16)
    c: Vertical(g17)
    c: Distance(g17) = 14
    c: Coincident(g18,g7)
    c: Coincident(g18,g15)
    c: Vertical(g18)
    c: Distance(g18) = 19
    c: Coincident(g19,g16)
    c: Coincident(g19,g15)
FEATURE [Sketcher::SketchObject] Sketch065
  FullyConstrained = true
  MapMode = 3
  Placement = pos=(0,0,0) rot=(1,0,0;1.5708rad)
  sketch-geometry (8):
    g0: Circle CenterX=80.351 CenterY=-67.6202 CenterZ=0 NormalX=0 NormalY=0 NormalZ=1 AngleXU=0 Radius=3
    g1: Circle CenterX=80.351 CenterY=-4.92017 CenterZ=0 NormalX=0 NormalY=0 NormalZ=1 AngleXU=0 Radius=3
    g2: Circle CenterX=23.851 CenterY=-4.92017 CenterZ=0 NormalX=0 NormalY=0 NormalZ=1 AngleXU=0 Radius=3
    g3: Circle CenterX=23.851 CenterY=-67.6202 CenterZ=0 NormalX=0 NormalY=0 NormalZ=1 AngleXU=0 Radius=3
    g4: Circle CenterX=23.851 CenterY=-67.6202 CenterZ=0 NormalX=0 NormalY=0 NormalZ=1 AngleXU=0 Radius=5
    g5: Circle CenterX=80.351 CenterY=-67.6202 CenterZ=0 NormalX=0 NormalY=0 NormalZ=1 AngleXU=0 Radius=5
    g6: Circle CenterX=23.851 CenterY=-4.92017 CenterZ=0 NormalX=0 NormalY=0 NormalZ=1 AngleXU=0 Radius=5
    g7: Circle CenterX=80.351 CenterY=-4.92017 CenterZ=0 NormalX=0 NormalY=0 NormalZ=1 AngleXU=0 Radius=5
  constraints (8):
    c: Block(g1)
    c: Block(g0)
    c: Block(g3)
    c: Block(g2)
    c: Block(g5)
    c: Block(g4)
    c: Block(g6)
    c: Block(g7)
FEATURE [Part::Extrusion] Extrude056
  Base = -> Sketch065
  Dir = (0,-1,2e-16)
  DirMode = 2
  FaceMakerClass = Part::FaceMakerBullseye
  LengthFwd = 2
  LengthRev = 0
  Solid = true
  Symmetric = false
FEATURE [Part::Extrusion] Extrude057  label="top025"
  Base = -> Sketch064
  Dir = (0,0,1)
  DirMode = 2
  FaceMakerClass = Part::FaceMakerBullseye
  LengthFwd = 72
  LengthRev = 0
  Solid = true
  Symmetric = false
FEATURE [Sketcher::SketchObject] Sketch066
  FullyConstrained = true
  MapMode = 3
  Placement = pos=(0,0,0) rot=(1,0,0;1.5708rad)
  Support = -> [Extrude057]
  sketch-geometry (8):
    g0: Circle CenterX=80.351 CenterY=-67.6202 CenterZ=0 NormalX=0 NormalY=0 NormalZ=1 AngleXU=0 Radius=3
    g1: Circle CenterX=80.351 CenterY=-4.92017 CenterZ=0 NormalX=0 NormalY=0 NormalZ=1 AngleXU=0 Radius=3
    g2: Circle CenterX=23.851 CenterY=-4.92017 CenterZ=0 NormalX=0 NormalY=0 NormalZ=1 AngleXU=0 Radius=3
    g3: Circle CenterX=23.851 CenterY=-67.6202 CenterZ=0 NormalX=0 NormalY=0 NormalZ=1 AngleXU=0 Radius=3
    g4: Circle CenterX=23.851 CenterY=-67.6202 CenterZ=0 NormalX=0 NormalY=0 NormalZ=1 AngleXU=0 Radius=5
    g5: Circle CenterX=80.351 CenterY=-67.6202 CenterZ=0 NormalX=0 NormalY=0 NormalZ=1 AngleXU=0 Radius=5
    g6: Circle CenterX=23.851 CenterY=-4.92017 CenterZ=0 NormalX=0 NormalY=0 NormalZ=1 AngleXU=0 Radius=5
    g7: Circle CenterX=80.351 CenterY=-4.92017 CenterZ=0 NormalX=0 NormalY=0 NormalZ=1 AngleXU=0 Radius=5
  constraints (8):
    c: Block(g1)
    c: Block(g0)
    c: Block(g3)
    c: Block(g2)
    c: Block(g5)
    c: Block(g4)
    c: Block(g6)
    c: Block(g7)
FEATURE [Part::Extrusion] Extrude055
  Base = -> Sketch066
  Dir = (0,-1,2e-16)
  DirMode = 2
  FaceMakerClass = Part::FaceMakerBullseye
  LengthFwd = 2
  LengthRev = 0
  Solid = true
  Symmetric = false
FEATURE [Part::Fillet] Fillet041
  Base = -> Extrude056
  Edges = 4 edges r=1.99: [Edge6,Edge12,Edge18,Edge24]
FEATURE [Part::Cut] Cut045
  Base = -> Extrude055
  Placement = pos=(0,6,0) rot=(0,0,1;0rad)
  Tool = -> Fillet041
FEATURE [Part::MultiFuse] Fusion095  label="pcbScrewPillars"
  Placement = pos=(-3.2,-1,72.3) rot=(0,0,1;0rad)
  Shapes = -> [Cut045,Extrude054]
FEATURE [Part::Feature] Face113
  shape: bbox 3.2 x 1.5 x 2e-07 mm, 1 faces, 0 solids (baked)
FEATURE [Part::Revolution] Revolve121  label="backCaseScrewRetainer002"
  Angle = 360
  Axis = (0,1,0)
  Base = (0,0,0)
  FaceMakerClass = Part::FaceMakerBullseye
  Placement = pos=(12.5,3,62) rot=(0,0,1;0rad)
  Solid = false
  Source = -> Face113
  Symmetric = false
FEATURE [Part::Feature] Face114
  shape: bbox 3.2 x 1.5 x 2e-07 mm, 1 faces, 0 solids (baked)
FEATURE [Part::Feature] Face115
  shape: bbox 3.2 x 1.5 x 2e-07 mm, 1 faces, 0 solids (baked)
FEATURE [Part::Feature] Face116
  shape: bbox 3.2 x 1.5 x 2e-07 mm, 1 faces, 0 solids (baked)
FEATURE [Part::Revolution] Revolve122  label="frontCaseScrewRetainer004"
  Angle = 360
  Axis = (0,1,0)
  Base = (0,0,0)
  FaceMakerClass = Part::FaceMakerBullseye
  Placement = pos=(89.5,3,68.5) rot=(0,0,1;0rad)
  Solid = false
  Source = -> Face115
  Symmetric = false
FEATURE [Part::Revolution] Revolve123  label="frontCaseScrewRetainer005"
  Angle = 360
  Axis = (0,1,0)
  Base = (0,0,0)
  FaceMakerClass = Part::FaceMakerBullseye
  Placement = pos=(89.5,3,3.5) rot=(0,0,1;0rad)
  Solid = false
  Source = -> Face116
  Symmetric = false
FEATURE [Part::Revolution] Revolve124  label="backCaseScrewRetainer003"
  Angle = 360
  Axis = (0,1,0)
  Base = (0,0,0)
  FaceMakerClass = Part::FaceMakerBullseye
  Placement = pos=(12.5,3,10) rot=(0,0,1;0rad)
  Solid = false
  Source = -> Face114
  Symmetric = false
FEATURE [Part::Feature] Face117
  shape: bbox 3.6 x 3.2 x 2e-07 mm, 1 faces, 0 solids (baked)
FEATURE [Part::Revolution] Revolve125  label="moreFrontCaseScrewRetainer004"
  Angle = 360
  Axis = (0,1,0)
  Base = (0,0,0)
  FaceMakerClass = Part::FaceMakerBullseye
  Placement = pos=(109.5,4.5,68.5) rot=(0,0,1;0rad)
  Solid = false
  Source = -> Face117
  Symmetric = false
FEATURE [Part::Feature] Face118
  shape: bbox 3.6 x 3.2 x 2e-07 mm, 1 faces, 0 solids (baked)
FEATURE [Part::Revolution] Revolve126  label="moreFrontCaseScrewRetainer005"
  Angle = 360
  Axis = (0,1,0)
  Base = (0,0,0)
  FaceMakerClass = Part::FaceMakerBullseye
  Placement = pos=(109.5,4.5,3.5) rot=(0,0,1;0rad)
  Solid = false
  Source = -> Face118
  Symmetric = false
FEATURE [Part::MultiFuse] Fusion096  label="screwRetainers001"
  Shapes = -> [Revolve126,Revolve125,Revolve124,Revolve123,Revolve122,Revolve121]
FEATURE [Part::Feature] Face119
  shape: bbox 10 x 16.5 x 2e-07 mm, 1 faces, 0 solids (baked)
FEATURE [Part::Revolution] Revolve130  label="plugHousing050"
  Angle = 360
  Axis = (0,1,0)
  Base = (0,0,0)
  FaceMakerClass = Part::FaceMakerBullseye
  Placement = pos=(0,0,36.15) rot=(0,0,1;0rad)
  Solid = false
  Source = -> Face119
  Symmetric = false
FEATURE [Part::Feature] Face120
  shape: bbox 10 x 16.5 x 2e-07 mm, 1 faces, 0 solids (baked)
FEATURE [Part::Feature] Face121
  shape: bbox 10 x 16.5 x 2e-07 mm, 1 faces, 0 solids (baked)
FEATURE [Part::Revolution] Revolve127  label="plugHousing047"
  Angle = 360
  Axis = (0,1,0)
  Base = (0,0,0)
  FaceMakerClass = Part::FaceMakerBullseye
  Placement = pos=(0,0,36.15) rot=(0,0,1;0rad)
  Solid = false
  Source = -> Face121
  Symmetric = false
FEATURE [Part::Feature] Face122
  shape: bbox 10 x 16.5 x 2e-07 mm, 1 faces, 0 solids (baked)
FEATURE [Part::Feature] Face123
  shape: bbox 10 x 16.5 x 2e-07 mm, 1 faces, 0 solids (baked)
FEATURE [Part::Revolution] Revolve128  label="plugHousing048"
  Angle = 360
  Axis = (0,1,0)
  Base = (0,0,0)
  FaceMakerClass = Part::FaceMakerBullseye
  Placement = pos=(0,0,36.15) rot=(0,0,1;0rad)
  Solid = false
  Source = -> Face123
  Symmetric = false
FEATURE [Part::MultiFuse] Fusion100  label="plugHousing054"
  Placement = pos=(0,0,0) rot=(0,0,1;1.5708rad)
  Shapes = -> [Revolve130,Revolve128]
FEATURE [Part::Feature] Face124
  shape: bbox 10 x 16.5 x 2e-07 mm, 1 faces, 0 solids (baked)
FEATURE [Part::Feature] Face125
  shape: bbox 10 x 16.5 x 2e-07 mm, 1 faces, 0 solids (baked)
FEATURE [Part::Revolution] Revolve129  label="plugHousing049"
  Angle = 360
  Axis = (0,1,0)
  Base = (0,0,0)
  FaceMakerClass = Part::FaceMakerBullseye
  Placement = pos=(0,0,36.15) rot=(0,0,1;0rad)
  Solid = false
  Source = -> Face125
  Symmetric = false
FEATURE [Part::Feature] Face126
  shape: bbox 10 x 16.5 x 2e-07 mm, 1 faces, 0 solids (baked)
FEATURE [Part::Revolution] Revolve131  label="plugHousing058"
  Angle = 360
  Axis = (0,1,0)
  Base = (0,0,0)
  FaceMakerClass = Part::FaceMakerBullseye
  Placement = pos=(0,0,36.15) rot=(0,0,1;0rad)
  Solid = false
  Source = -> Face120
  Symmetric = false
FEATURE [Part::MultiFuse] Fusion099  label="plugHousing053"
  Placement = pos=(0,0,0) rot=(0,0,1;1.5708rad)
  Shapes = -> [Revolve127,Revolve131]
FEATURE [Part::MultiFuse] Fusion102  label="plugHousing056"
  Placement = pos=(0,19,0) rot=(0,0,1;3.14159rad)
  Shapes = -> [Fusion100,Fusion099]
FEATURE [Part::Revolution] Revolve132  label="plugHousing059"
  Angle = 360
  Axis = (0,1,0)
  Base = (0,0,0)
  FaceMakerClass = Part::FaceMakerBullseye
  Placement = pos=(0,0,36.15) rot=(0,0,1;0rad)
  Solid = false
  Source = -> Face126
  Symmetric = false
FEATURE [Part::Revolution] Revolve133  label="plugHousing060"
  Angle = 360
  Axis = (0,1,0)
  Base = (0,0,0)
  FaceMakerClass = Part::FaceMakerBullseye
  Placement = pos=(0,0,36.15) rot=(0,0,1;0rad)
  Solid = false
  Source = -> Face122
  Symmetric = false
FEATURE [Part::MultiFuse] Fusion097  label="plugHousing051"
  Placement = pos=(0,0,0) rot=(0,0,1;1.5708rad)
  Shapes = -> [Revolve133,Revolve132]
FEATURE [Part::Revolution] Revolve134  label="plugHousing061"
  Angle = 360
  Axis = (0,1,0)
  Base = (0,0,0)
  FaceMakerClass = Part::FaceMakerBullseye
  Placement = pos=(0,0,36.15) rot=(0,0,1;0rad)
  Solid = false
  Source = -> Face124
  Symmetric = false
FEATURE [Part::MultiFuse] Fusion101  label="plugHousing055"
  Placement = pos=(0,0,0) rot=(0,0,1;1.5708rad)
  Shapes = -> [Revolve129,Revolve134]
FEATURE [Part::MultiFuse] Fusion098  label="plugHousing052"
  Placement = pos=(0,19,0) rot=(0,0,1;3.14159rad)
  Shapes = -> [Fusion097,Fusion101]
FEATURE [Part::MultiFuse] Fusion103  label="plugHousing057"
  Placement = pos=(122.621,0,-0.15) rot=(0,0,1;0rad)
  Shapes = -> [Fusion102,Fusion098]
FEATURE [Part::Box] Box028  label="Cube015"
  AttacherType = Attacher::AttachEngine3D
  Height = 28
  Length = 3
  Placement = pos=(110.7,19,22) rot=(0,0,1;0rad)
  Width = 15.7
FEATURE [Part::Cylinder] Cylinder044
  Angle = 360
  AttacherType = Attacher::AttachEngine3D
  Height = 20
  Placement = pos=(0,0,36.15) rot=(0,0,1;0rad)
  Radius = 10.3
FEATURE [Part::Cylinder] Cylinder045
  Angle = 360
  AttacherType = Attacher::AttachEngine3D
  Height = 10
  Placement = pos=(0,0,36.15) rot=(0,0,1;0rad)
  Radius = 4
FEATURE [Part::MultiFuse] Fusion104  label="removeToCreteHoleForPlugHousing040"
  Placement = pos=(70,19,36) rot=(0,1,0;1.5708rad)
  Shapes = -> [Cylinder044,Cylinder045]
FEATURE [Part::Cut] Cut046  label="plugHousingTab003"
  Base = -> Box028
  Tool = -> Fusion104
FEATURE [Part::MultiFuse] Fusion105  label="plugHousing062"
  Shapes = -> [Fusion103,Cut046]
FEATURE [Part::Fillet] Fillet042
  Base = -> Fusion105
  Edges = 1 edges r=2: [Edge25]
FEATURE [Part::Fillet] Fillet043  label="plugHousing063"
  Base = -> Fillet042
  Edges = 1 edges r=2: [Edge8]
  Placement = pos=(7,0,0) rot=(0,0,1;0rad)
FEATURE [Part::Feature] Face127
  shape: bbox 10 x 16.5 x 2e-07 mm, 1 faces, 0 solids (baked)
FEATURE [Part::Feature] Face128
  shape: bbox 10 x 16.5 x 2e-07 mm, 1 faces, 0 solids (baked)
FEATURE [Part::Revolution] Revolve137  label="plugHousing070"
  Angle = 360
  Axis = (0,1,0)
  Base = (0,0,0)
  FaceMakerClass = Part::FaceMakerBullseye
  Placement = pos=(0,0,36.15) rot=(0,0,1;0rad)
  Solid = false
  Source = -> Face127
  Symmetric = false
FEATURE [Part::Revolution] Revolve140  label="plugHousing073"
  Angle = 360
  Axis = (0,1,0)
  Base = (0,0,0)
  FaceMakerClass = Part::FaceMakerBullseye
  Placement = pos=(0,0,36.15) rot=(0,0,1;0rad)
  Solid = false
  Source = -> Face128
  Symmetric = false
FEATURE [Part::Feature] Face129
  shape: bbox 10 x 16.5 x 2e-07 mm, 1 faces, 0 solids (baked)
FEATURE [Part::Revolution] Revolve138  label="plugHousing071"
  Angle = 360
  Axis = (0,1,0)
  Base = (0,0,0)
  FaceMakerClass = Part::FaceMakerBullseye
  Placement = pos=(0,0,36.15) rot=(0,0,1;0rad)
  Solid = false
  Source = -> Face129
  Symmetric = false
FEATURE [Part::Feature] Face130
  shape: bbox 10 x 16.5 x 2e-07 mm, 1 faces, 0 solids (baked)
FEATURE [Part::Revolution] Revolve139  label="plugHousing072"
  Angle = 360
  Axis = (0,1,0)
  Base = (0,0,0)
  FaceMakerClass = Part::FaceMakerBullseye
  Placement = pos=(0,0,36.15) rot=(0,0,1;0rad)
  Solid = false
  Source = -> Face130
  Symmetric = false
FEATURE [Part::Feature] Face131
  shape: bbox 10 x 16.5 x 2e-07 mm, 1 faces, 0 solids (baked)
FEATURE [Part::Revolution] Revolve135  label="plugHousing068"
  Angle = 360
  Axis = (0,1,0)
  Base = (0,0,0)
  FaceMakerClass = Part::FaceMakerBullseye
  Placement = pos=(0,0,36.15) rot=(0,0,1;0rad)
  Solid = false
  Source = -> Face131
  Symmetric = false
FEATURE [Part::MultiFuse] Fusion112  label="plugHousing078"
  Placement = pos=(0,0,0) rot=(0,0,1;1.5708rad)
  Shapes = -> [Revolve135,Revolve139]
FEATURE [Part::Feature] Face132
  shape: bbox 10 x 16.5 x 2e-07 mm, 1 faces, 0 solids (baked)
FEATURE [Part::Revolution] Revolve141  label="plugHousing074"
  Angle = 360
  Axis = (0,1,0)
  Base = (0,0,0)
  FaceMakerClass = Part::FaceMakerBullseye
  Placement = pos=(0,0,36.15) rot=(0,0,1;0rad)
  Solid = false
  Source = -> Face132
  Symmetric = false
FEATURE [Part::MultiFuse] Fusion110  label="plugHousing076"
  Placement = pos=(0,0,0) rot=(0,0,1;1.5708rad)
  Shapes = -> [Revolve141,Revolve140]
FEATURE [Part::Feature] Face133
  shape: bbox 10 x 16.5 x 2e-07 mm, 1 faces, 0 solids (baked)
FEATURE [Part::Revolution] Revolve136  label="plugHousing069"
  Angle = 360
  Axis = (0,1,0)
  Base = (0,0,0)
  FaceMakerClass = Part::FaceMakerBullseye
  Placement = pos=(0,0,36.15) rot=(0,0,1;0rad)
  Solid = false
  Source = -> Face133
  Symmetric = false
FEATURE [Part::MultiFuse] Fusion106  label="plugHousing064"
  Placement = pos=(0,0,0) rot=(0,0,1;1.5708rad)
  Shapes = -> [Revolve138,Revolve136]
FEATURE [Part::MultiFuse] Fusion108  label="plugHousing066"
  Placement = pos=(0,19,0) rot=(0,0,1;3.14159rad)
  Shapes = -> [Fusion106,Fusion112]
FEATURE [Part::Feature] Face134
  shape: bbox 10 x 16.5 x 2e-07 mm, 1 faces, 0 solids (baked)
FEATURE [Part::Revolution] Revolve142  label="plugHousing075"
  Angle = 360
  Axis = (0,1,0)
  Base = (0,0,0)
  FaceMakerClass = Part::FaceMakerBullseye
  Placement = pos=(0,0,36.15) rot=(0,0,1;0rad)
  Solid = false
  Source = -> Face134
  Symmetric = false
FEATURE [Part::MultiFuse] Fusion107  label="plugHousing065"
  Placement = pos=(0,0,0) rot=(0,0,1;1.5708rad)
  Shapes = -> [Revolve137,Revolve142]
FEATURE [Part::MultiFuse] Fusion111  label="plugHousing077"
  Placement = pos=(0,19,0) rot=(0,0,1;3.14159rad)
  Shapes = -> [Fusion110,Fusion107]
FEATURE [Part::MultiFuse] Fusion109  label="plugHousing067"
  Placement = pos=(131.236,0,-0.15) rot=(0,0,1;0rad)
  Shapes = -> [Fusion108,Fusion111]
FEATURE [Part::MultiFuse] Fusion113  label="plugHousing079"
  Shapes = -> [Fillet043,Fusion109]
FEATURE [Part::Feature] Face135
  shape: bbox 3.5 x 17.8 x 2e-07 mm, 1 faces, 0 solids (baked)
FEATURE [Part::Revolution] Revolve143  label="removeToCreateScrewAndThreadedInsertHole049"
  Angle = 360
  Axis = (0,1,0)
  Base = (0,0,0)
  FaceMakerClass = Part::FaceMakerBullseye
  Placement = pos=(12.5,0,10) rot=(0,0,1;0rad)
  Solid = false
  Source = -> Face135
  Symmetric = false
FEATURE [Part::Feature] Face136
  shape: bbox 3.5 x 17.8 x 2e-07 mm, 1 faces, 0 solids (baked)
FEATURE [Part::Revolution] Revolve144  label="removeToCreateScrewAndThreadedInsertHole050"
  Angle = 360
  Axis = (0,1,0)
  Base = (0,0,0)
  FaceMakerClass = Part::FaceMakerBullseye
  Placement = pos=(12.5,0,62) rot=(0,0,1;0rad)
  Solid = false
  Source = -> Face136
  Symmetric = false
FEATURE [Part::Feature] Face137
  shape: bbox 3.5 x 17.8 x 2e-07 mm, 1 faces, 0 solids (baked)
FEATURE [Part::Revolution] Revolve145  label="removeToCreateScrewAndThreadedInsertHole051"
  Angle = 360
  Axis = (0,1,0)
  Base = (0,0,0)
  FaceMakerClass = Part::FaceMakerBullseye
  Placement = pos=(89.5,0,68.5) rot=(0,0,1;0rad)
  Solid = false
  Source = -> Face137
  Symmetric = false
FEATURE [Part::Feature] Face138
  shape: bbox 3.5 x 17.8 x 2e-07 mm, 1 faces, 0 solids (baked)
FEATURE [Part::Revolution] Revolve146  label="removeToCreateScrewAndThreadedInsertHole052"
  Angle = 360
  Axis = (0,1,0)
  Base = (0,0,0)
  FaceMakerClass = Part::FaceMakerBullseye
  Placement = pos=(89.5,0,3.5) rot=(0,0,1;0rad)
  Solid = false
  Source = -> Face138
  Symmetric = false
FEATURE [Part::Feature] Face139
  shape: bbox 3.5 x 17.8 x 2e-07 mm, 1 faces, 0 solids (baked)
FEATURE [Part::Revolution] Revolve147  label="removeToCreateScrewAndThreadedInsertHole053"
  Angle = 360
  Axis = (0,1,0)
  Base = (0,0,0)
  FaceMakerClass = Part::FaceMakerBullseye
  Placement = pos=(109.5,4.7,3.5) rot=(0,0,1;0rad)
  Solid = false
  Source = -> Face139
  Symmetric = false
FEATURE [Part::Feature] Face140
  shape: bbox 3.5 x 17.8 x 2e-07 mm, 1 faces, 0 solids (baked)
FEATURE [Part::Revolution] Revolve148  label="removeToCreateScrewAndThreadedInsertHole054"
  Angle = 360
  Axis = (0,1,0)
  Base = (0,0,0)
  FaceMakerClass = Part::FaceMakerBullseye
  Placement = pos=(109.5,4.7,68.5) rot=(0,0,1;0rad)
  Solid = false
  Source = -> Face140
  Symmetric = false
FEATURE [Part::MultiFuse] Fusion114  label="removeToCreateScrewAndThreadedInsertHole055"
  Shapes = -> [Revolve148,Revolve147,Revolve146,Revolve145,Revolve144,Revolve143]
FEATURE [Part::Cut] Cut047  label="casePillars004"
  Base = -> Cut037
  Tool = -> Fusion114
FEATURE [Part::Feature] Face141
  shape: bbox 3.5 x 17.8 x 2e-07 mm, 1 faces, 0 solids (baked)
FEATURE [Part::Feature] Face142
  shape: bbox 3.5 x 17.8 x 2e-07 mm, 1 faces, 0 solids (baked)
FEATURE [Part::Feature] Face143
  shape: bbox 3.5 x 17.8 x 2e-07 mm, 1 faces, 0 solids (baked)
FEATURE [Part::Revolution] Revolve149  label="removeToCreateScrewAndThreadedInsertHole057"
  Angle = 360
  Axis = (0,1,0)
  Base = (0,0,0)
  FaceMakerClass = Part::FaceMakerBullseye
  Placement = pos=(12.5,0,10) rot=(0,0,1;0rad)
  Solid = false
  Source = -> Face141
  Symmetric = false
FEATURE [Part::Feature] Face144
  shape: bbox 3.5 x 17.8 x 2e-07 mm, 1 faces, 0 solids (baked)
FEATURE [Part::Feature] Face145
  shape: bbox 3.5 x 17.8 x 2e-07 mm, 1 faces, 0 solids (baked)
FEATURE [Part::Feature] Face146
  shape: bbox 3.5 x 17.8 x 2e-07 mm, 1 faces, 0 solids (baked)
FEATURE [Part::Revolution] Revolve150  label="removeToCreateScrewAndThreadedInsertHole058"
  Angle = 360
  Axis = (0,1,0)
  Base = (0,0,0)
  FaceMakerClass = Part::FaceMakerBullseye
  Placement = pos=(12.5,0,62) rot=(0,0,1;0rad)
  Solid = false
  Source = -> Face146
  Symmetric = false
FEATURE [Part::Revolution] Revolve151  label="removeToCreateScrewAndThreadedInsertHole059"
  Angle = 360
  Axis = (0,1,0)
  Base = (0,0,0)
  FaceMakerClass = Part::FaceMakerBullseye
  Placement = pos=(89.5,0,68.5) rot=(0,0,1;0rad)
  Solid = false
  Source = -> Face143
  Symmetric = false
FEATURE [Part::Revolution] Revolve152  label="removeToCreateScrewAndThreadedInsertHole060"
  Angle = 360
  Axis = (0,1,0)
  Base = (0,0,0)
  FaceMakerClass = Part::FaceMakerBullseye
  Placement = pos=(89.5,0,3.5) rot=(0,0,1;0rad)
  Solid = false
  Source = -> Face142
  Symmetric = false
FEATURE [Part::Revolution] Revolve153  label="removeToCreateScrewAndThreadedInsertHole061"
  Angle = 360
  Axis = (0,1,0)
  Base = (0,0,0)
  FaceMakerClass = Part::FaceMakerBullseye
  Placement = pos=(109.5,4.7,3.5) rot=(0,0,1;0rad)
  Solid = false
  Source = -> Face145
  Symmetric = false
FEATURE [Part::Revolution] Revolve154  label="removeToCreateScrewAndThreadedInsertHole062"
  Angle = 360
  Axis = (0,1,0)
  Base = (0,0,0)
  FaceMakerClass = Part::FaceMakerBullseye
  Placement = pos=(109.5,4.7,68.5) rot=(0,0,1;0rad)
  Solid = false
  Source = -> Face144
  Symmetric = false
FEATURE [Part::MultiFuse] Fusion115  label="removeToCreateScrewAndThreadedInsertHole056"
  Shapes = -> [Revolve154,Revolve153,Revolve152,Revolve151,Revolve150,Revolve149]
FEATURE [Part::Feature] Face147
  shape: bbox 9.8 x 26.5 x 2e-07 mm, 1 faces, 0 solids (baked)
FEATURE [Part::Revolution] Revolve155
  Angle = 360
  Axis = (0,1,0)
  Base = (0,0,0)
  FaceMakerClass = Part::FaceMakerBullseye
  Placement = pos=(0,0,0) rot=(0,0,1;1.5708rad)
  Solid = false
  Source = -> Face147
  Symmetric = false
FEATURE [Part::Feature] Face148
  shape: bbox 9.8 x 26.5 x 2e-07 mm, 1 faces, 0 solids (baked)
FEATURE [Part::Revolution] Revolve156
  Angle = 360
  Axis = (0,1,0)
  Base = (0,0,0)
  FaceMakerClass = Part::FaceMakerBullseye
  Placement = pos=(0,0,0) rot=(0,0,1;1.5708rad)
  Solid = false
  Source = -> Face148
  Symmetric = false
FEATURE [Part::MultiFuse] Fusion116
  Placement = pos=(-18,19,36) rot=(0,0,1;0rad)
  Shapes = -> [Revolve156,Revolve155]
FEATURE [Part::Box] Box029  label="Cube016"
  AttacherType = Attacher::AttachEngine3D
  Height = 28
  Length = 3
  Placement = pos=(110.7,19,22) rot=(0,0,1;0rad)
  Width = 15.7
FEATURE [Part::Cylinder] Cylinder046
  Angle = 360
  AttacherType = Attacher::AttachEngine3D
  Height = 10
  Placement = pos=(0,0,36.15) rot=(0,0,1;0rad)
  Radius = 4
FEATURE [Part::Cylinder] Cylinder047
  Angle = 360
  AttacherType = Attacher::AttachEngine3D
  Height = 20
  Placement = pos=(0,0,36.15) rot=(0,0,1;0rad)
  Radius = 10.3
FEATURE [Part::MultiFuse] Fusion117  label="removeToCreteHoleForPlugHousing041"
  Placement = pos=(70,19,36) rot=(0,1,0;1.5708rad)
  Shapes = -> [Cylinder047,Cylinder046]
FEATURE [Part::Cut] Cut049  label="plugHousingTab004"
  Base = -> Box029
  Placement = pos=(-107.4,-14,0) rot=(0,0,1;0rad)
  Tool = -> Fusion117
FEATURE [Part::Box] Box030  label="Cube017"
  AttacherType = Attacher::AttachEngine3D
  Height = 28
  Length = 3
  Placement = pos=(110.7,19,22) rot=(0,0,1;0rad)
  Width = 15.7
FEATURE [Part::Cylinder] Cylinder048
  Angle = 360
  AttacherType = Attacher::AttachEngine3D
  Height = 10
  Placement = pos=(0,0,36.15) rot=(0,0,1;0rad)
  Radius = 4
FEATURE [Part::Cylinder] Cylinder049
  Angle = 360
  AttacherType = Attacher::AttachEngine3D
  Height = 20
  Placement = pos=(0,0,36.15) rot=(0,0,1;0rad)
  Radius = 10.3
FEATURE [Part::MultiFuse] Fusion118  label="removeToCreteHoleForPlugHousing042"
  Placement = pos=(70,19,36) rot=(0,1,0;1.5708rad)
  Shapes = -> [Cylinder049,Cylinder048]
FEATURE [Part::Cut] Cut050  label="plugHousingTab005"
  Base = -> Box030
  Placement = pos=(-107.4,-14,0) rot=(0,0,1;0rad)
  Tool = -> Fusion118
FEATURE [Part::MultiFuse] Fusion119
  Placement = pos=(9.6,23,0) rot=(0,0,1;3.14159rad)
  Shapes = -> [Cut049,Cut050]
FEATURE [Part::Box] Box031  label="Cube018"
  AttacherType = Attacher::AttachEngine3D
  Height = 10
  Length = 3
  Placement = pos=(3.3,4,12) rot=(0,0,1;0rad)
  Width = 10
FEATURE [Part::Fillet] Fillet044
  Base = -> Box031
  Edges = 1 edges r=2: [Edge11]
FEATURE [Part::Box] Box032  label="Cube019"
  AttacherType = Attacher::AttachEngine3D
  Height = 10
  Length = 3
  Placement = pos=(3.3,4,50) rot=(0,0,1;0rad)
  Width = 10
FEATURE [Part::Fillet] Fillet045
  Base = -> Box032
  Edges = 1 edges r=2: [Edge12]
FEATURE [Part::Box] Box033  label="Cube020"
  AttacherType = Attacher::AttachEngine3D
  Height = 28
  Length = 4
  Placement = pos=(5,0,22) rot=(0,0,1;0rad)
  Width = 10
FEATURE [Part::Fillet] Fillet046
  Base = -> Box033
  Edges = 1 edges r=1: [Edge7]
FEATURE [Part::Fillet] Fillet047
  Base = -> Fillet046
  Edges = 1 edges r=2: [Edge5]
FEATURE [Part::Fillet] Fillet048
  Base = -> Fillet047
  Edges = 1 edges r=2: [Edge2]
FEATURE [Part::Cylinder] Cylinder050
  Angle = 360
  AttacherType = Attacher::AttachEngine3D
  Height = 20
  Placement = pos=(0,0,36.15) rot=(0,0,1;0rad)
  Radius = 8.2
FEATURE [Part::Cylinder] Cylinder051
  Angle = 360
  AttacherType = Attacher::AttachEngine3D
  Height = 10
  Placement = pos=(0,0,36.15) rot=(0,0,1;0rad)
  Radius = 4
FEATURE [Part::MultiFuse] Fusion120  label="removeToCreteHoleForPlugHousing043"
  Placement = pos=(-42,19,36) rot=(0,1,0;1.5708rad)
  Shapes = -> [Cylinder050,Cylinder051]
FEATURE [Sketcher::SketchObject] Sketch067  label="topSketch018"
  FullyConstrained = true
  sketch-geometry (4):
    g0: LineSegment StartX=16.8446 StartY=31.512 StartZ=0 EndX=16.3251 EndY=34.4666 EndZ=0
    g1: ArcOfCircle CenterX=19 CenterY=19.2524 CenterZ=0 NormalX=0 NormalY=0 NormalZ=1 AngleXU=0 Radius=15.4476 StartAngle=1.74483 EndAngle=2.72717
    g2: ArcOfCircle CenterX=19 CenterY=19.2524 CenterZ=0 NormalX=0 NormalY=0 NormalZ=1 AngleXU=0 Radius=12.4476 StartAngle=1.74483 EndAngle=2.73189
    g3: LineSegment StartX=4.86004 StartY=25.4725 StartZ=0 EndX=7.58253 EndY=24.2107 EndZ=0
  constraints (7):
    c: Block(g0)
    c: Coincident(g1,g0)
    c: Coincident(g2,g0)
    c: Coincident(g3,g1)
    c: Coincident(g3,g2)
    c: Block(g1)
    c: Block(g2)
FEATURE [Part::Extrusion] Extrude058
  Base = -> Sketch067
  Dir = (0,0,1)
  DirMode = 2
  FaceMakerClass = Part::FaceMakerBullseye
  LengthFwd = 10
  LengthRev = 0
  Placement = pos=(0,0,31) rot=(0,0,1;0rad)
  Solid = true
  Symmetric = false
FEATURE [Part::Cut] Cut051
  Base = -> Extrude058
  Tool = -> Fusion120
FEATURE [Part::Fillet] Fillet049
  Base = -> Cut051
  Edges = 1 edges r=2: [Edge1]
FEATURE [Part::Fillet] Fillet050
  Base = -> Fillet049
  Edges = 1 edges r=2.5: [Edge1]
FEATURE [Part::Fillet] Fillet051
  Base = -> Fillet050
  Edges = 1 edges r=2.5: [Edge2]
FEATURE [Part::MultiFuse] Fusion121  label="wireHolder003"
  Shapes = -> [Fusion116,Fillet051]
FEATURE [Part::MultiFuse] Fusion122
  Shapes = -> [Fillet045,Fusion121]
FEATURE [Part::MultiFuse] Fusion123  label="wireHolder004"
  Shapes = -> [Fusion122,Fillet048]
FEATURE [Part::MultiFuse] Fusion124  label="wireHolder005"
  Shapes = -> [Fillet044,Fusion119,Fusion123]
FEATURE [Sketcher::SketchObject] Sketch068  label="topSketch019"
  FullyConstrained = true
  sketch-geometry (6):
    g0: LineSegment StartX=19 StartY=38 StartZ=0 EndX=117 EndY=38 EndZ=0
    g1: ArcOfCircle CenterX=19 CenterY=19 CenterZ=0 NormalX=0 NormalY=0 NormalZ=1 AngleXU=0 Radius=19 StartAngle=1.5708 EndAngle=3.14159
    g2: LineSegment StartX=117 StartY=38 StartZ=0 EndX=117 EndY=19 EndZ=0
    g3: LineSegment StartX=98 StartY=1.0161e-12 StartZ=0 EndX=5.22862e-06 EndY=1.0161e-12 EndZ=0
    g4: LineSegment StartX=5.22862e-06 StartY=19 StartZ=0 EndX=5.22862e-06 EndY=1.0161e-12 EndZ=0
    g5: ArcOfCircle CenterX=98 CenterY=19 CenterZ=0 NormalX=0 NormalY=0 NormalZ=1 AngleXU=0 Radius=19 StartAngle=4.71239 EndAngle=6.28319
  constraints (16):
    c: Horizontal(g0)
    c: Distance(g0) = 98
    c: Coincident(g1,g0)
    c: Block(g1)
    c: Coincident(g2,g0)
    c: Vertical(g2)
    c: Distance(g2) = 19
    c: Horizontal(g3)
    c: Coincident(g4,g1)
    c: Vertical(g4)
    c: Coincident(g3,g4)
    c: Block(g3)
    c: Coincident(g5,g2)
    c: Coincident(g5,g3)
    c: Block(g0)
    c: Block(g5)
FEATURE [Part::Extrusion] Extrude059  label="sideA002"
  Base = -> Sketch068
  Dir = (0,0,1)
  DirMode = 2
  FaceMakerClass = Part::FaceMakerBullseye
  LengthFwd = 3
  LengthRev = 0
  Placement = pos=(0,0,-2.7) rot=(0,0,1;0rad)
  Solid = true
  Symmetric = false
FEATURE [Sketcher::SketchObject] Sketch069  label="topSketch020"
  FullyConstrained = true
  sketch-geometry (6):
    g0: LineSegment StartX=19 StartY=38 StartZ=0 EndX=117 EndY=38 EndZ=0
    g1: ArcOfCircle CenterX=19 CenterY=19 CenterZ=0 NormalX=0 NormalY=0 NormalZ=1 AngleXU=0 Radius=19 StartAngle=1.5708 EndAngle=3.14159
    g2: LineSegment StartX=117 StartY=38 StartZ=0 EndX=117 EndY=19 EndZ=0
    g3: LineSegment StartX=98 StartY=1.0161e-12 StartZ=0 EndX=5.22862e-06 EndY=1.0161e-12 EndZ=0
    g4: LineSegment StartX=5.22862e-06 StartY=19 StartZ=0 EndX=5.22862e-06 EndY=1.0161e-12 EndZ=0
    g5: ArcOfCircle CenterX=98 CenterY=19 CenterZ=0 NormalX=0 NormalY=0 NormalZ=1 AngleXU=0 Radius=19 StartAngle=4.71239 EndAngle=6.28319
  constraints (16):
    c: Horizontal(g0)
    c: Distance(g0) = 98
    c: Coincident(g1,g0)
    c: Block(g1)
    c: Coincident(g2,g0)
    c: Vertical(g2)
    c: Distance(g2) = 19
    c: Horizontal(g3)
    c: Coincident(g4,g1)
    c: Vertical(g4)
    c: Coincident(g3,g4)
    c: Block(g3)
    c: Coincident(g5,g2)
    c: Coincident(g5,g3)
    c: Block(g0)
    c: Block(g5)
FEATURE [Part::Extrusion] Extrude060  label="sideB002"
  Base = -> Sketch069
  Dir = (0,0,1)
  DirMode = 2
  FaceMakerClass = Part::FaceMakerBullseye
  LengthFwd = 3
  LengthRev = 0
  Placement = pos=(0,0,71.7) rot=(0,0,1;0rad)
  Solid = true
  Symmetric = false
FEATURE [Part::MultiFuse] Fusion127  label="removeFromBottom001"
  Placement = pos=(2,0,0) rot=(0,0,1;0rad)
  Shapes = -> [Extrude059,Extrude060]
FEATURE [Part::Cylinder] Cylinder052
  Angle = 360
  AttacherType = Attacher::AttachEngine3D
  Height = 20
  Placement = pos=(0,0,36.15) rot=(0,0,1;0rad)
  Radius = 14
FEATURE [Part::Cylinder] Cylinder053
  Angle = 360
  AttacherType = Attacher::AttachEngine3D
  Height = 10
  Placement = pos=(0,0,36.15) rot=(0,0,1;0rad)
  Radius = 4
FEATURE [Part::MultiFuse] Fusion128  label="removeToCreteHoleForPlugHousing044"
  Placement = pos=(70,19,36) rot=(0,1,0;1.5708rad)
  Shapes = -> [Cylinder052,Cylinder053]
FEATURE [Part::Cut] Cut052  label="bottom011"
  Base = -> Extrude043
  Tool = -> Fusion128
FEATURE [Part::Cut] Cut054  label="bottom012"
  Base = -> Cut052
  Tool = -> Fusion115
FEATURE [Sketcher::SketchObject] Sketch070
  FullyConstrained = true
  Placement = pos=(117,19,0) rot=(0.57735,0.57735,0.57735;2.0944rad)
  sketch-geometry (48):
    g0: LineSegment StartX=-49.19 StartY=69.25 StartZ=0 EndX=-49.19 EndY=66.25 EndZ=0
    g1: LineSegment StartX=-49.19 StartY=63.5 StartZ=0 EndX=-49.19 EndY=60.5 EndZ=0
    g2: LineSegment StartX=-49.19 StartY=57.75 StartZ=0 EndX=-49.19 EndY=54.75 EndZ=0
    g3: LineSegment StartX=-49.19 StartY=52 StartZ=0 EndX=-49.19 EndY=49 EndZ=0
    g4: LineSegment StartX=-49.19 StartY=46.25 StartZ=0 EndX=-49.19 EndY=43.25 EndZ=0
    g5: LineSegment StartX=-49.19 StartY=40.5 StartZ=0 EndX=-49.19 EndY=37.5 EndZ=0
    g6: LineSegment StartX=-49.19 StartY=34.5 StartZ=0 EndX=-49.19 EndY=31.5 EndZ=0
    g7: LineSegment StartX=-49.19 StartY=28.75 StartZ=0 EndX=-49.19 EndY=25.75 EndZ=0
    g8: LineSegment StartX=-49.19 StartY=23 StartZ=0 EndX=-49.19 EndY=20 EndZ=0
    g9: LineSegment StartX=-49.19 StartY=17.25 StartZ=0 EndX=-49.19 EndY=14.25 EndZ=0
    g10: LineSegment StartX=-49.19 StartY=11.5 StartZ=0 EndX=-49.19 EndY=8.5 EndZ=0
    g11: LineSegment StartX=-49.19 StartY=5.75 StartZ=0 EndX=-49.19 EndY=2.75 EndZ=0
    g12: ArcOfCircle CenterX=-1.5 CenterY=67.75 CenterZ=0 NormalX=0 NormalY=0 NormalZ=1 AngleXU=0 Radius=1.5 StartAngle=4.71239 EndAngle=7.85398
    g13: ArcOfCircle CenterX=-1.5 CenterY=62 CenterZ=0 NormalX=0 NormalY=0 NormalZ=1 AngleXU=0 Radius=1.5 StartAngle=4.71239 EndAngle=7.85398
    g14: ArcOfCircle CenterX=-1.5 CenterY=56.25 CenterZ=0 NormalX=0 NormalY=0 NormalZ=1 AngleXU=0 Radius=1.5 StartAngle=4.71239 EndAngle=7.85398
    g15: ArcOfCircle CenterX=-11.49 CenterY=50.5 CenterZ=0 NormalX=0 NormalY=0 NormalZ=1 AngleXU=0 Radius=1.5 StartAngle=4.71239 EndAngle=7.85398
    g16: ArcOfCircle CenterX=-16.28 CenterY=44.75 CenterZ=0 NormalX=0 NormalY=0 NormalZ=1 AngleXU=0 Radius=1.5 StartAngle=4.71239 EndAngle=7.85398
    g17: ArcOfCircle CenterX=-18.2337 CenterY=39 CenterZ=0 NormalX=0 NormalY=0 NormalZ=1 AngleXU=0 Radius=1.5 StartAngle=4.71485 EndAngle=7.85398
    g18: ArcOfCircle CenterX=-16.2837 CenterY=27.25 CenterZ=0 NormalX=0 NormalY=0 NormalZ=1 AngleXU=0 Radius=1.5 StartAngle=4.71485 EndAngle=7.85398
    g19: ArcOfCircle CenterX=-18.2337 CenterY=33 CenterZ=0 NormalX=0 NormalY=0 NormalZ=1 AngleXU=0 Radius=1.5 StartAngle=4.71485 EndAngle=7.85398
    g20: ArcOfCircle CenterX=-11.49 CenterY=21.5 CenterZ=0 NormalX=0 NormalY=0 NormalZ=1 AngleXU=0 Radius=1.5 StartAngle=4.71239 EndAngle=7.85398
    g21: ArcOfCircle CenterX=-1.5 CenterY=4.25 CenterZ=0 NormalX=0 NormalY=0 NormalZ=1 AngleXU=0 Radius=1.5 StartAngle=4.71239 EndAngle=7.85398
    g22: ArcOfCircle CenterX=-1.5 CenterY=10 CenterZ=0 NormalX=0 NormalY=0 NormalZ=1 AngleXU=0 Radius=1.5 StartAngle=4.71239 EndAngle=7.85398
    g23: ArcOfCircle CenterX=-1.5 CenterY=15.75 CenterZ=0 NormalX=0 NormalY=0 NormalZ=1 AngleXU=0 Radius=1.5 StartAngle=4.71239 EndAngle=7.85398
    g24: LineSegment StartX=-49.19 StartY=69.25 StartZ=0 EndX=-1.5 EndY=69.25 EndZ=0
    g25: LineSegment StartX=-49.19 StartY=66.25 StartZ=0 EndX=-1.5 EndY=66.25 EndZ=0
    g26: LineSegment StartX=-49.19 StartY=63.5 StartZ=0 EndX=-1.5 EndY=63.5 EndZ=0
    g27: LineSegment StartX=-49.19 StartY=60.5 StartZ=0 EndX=-1.5 EndY=60.5 EndZ=0
    g28: LineSegment StartX=-49.19 StartY=57.75 StartZ=0 EndX=-1.5 EndY=57.75 EndZ=0
    g29: LineSegment StartX=-49.19 StartY=54.75 StartZ=0 EndX=-1.5 EndY=54.75 EndZ=0
    g30: LineSegment StartX=-49.19 StartY=52 StartZ=0 EndX=-11.49 EndY=52 EndZ=0
    g31: LineSegment StartX=-49.19 StartY=49 StartZ=0 EndX=-11.49 EndY=49 EndZ=0
    g32: LineSegment StartX=-49.19 StartY=46.25 StartZ=0 EndX=-16.28 EndY=46.25 EndZ=0
    g33: LineSegment StartX=-49.19 StartY=43.25 StartZ=0 EndX=-16.28 EndY=43.25 EndZ=0
    g34: LineSegment StartX=-49.19 StartY=40.5 StartZ=0 EndX=-18.2337 EndY=40.5 EndZ=0
    g35: LineSegment StartX=-49.19 StartY=37.5 StartZ=0 EndX=-18.23 EndY=37.5 EndZ=0
    g36: LineSegment StartX=-49.19 StartY=34.5 StartZ=0 EndX=-18.2337 EndY=34.5 EndZ=0
    g37: LineSegment StartX=-49.19 StartY=31.5 StartZ=0 EndX=-18.23 EndY=31.5 EndZ=0
    g38: LineSegment StartX=-49.19 StartY=28.75 StartZ=0 EndX=-16.2837 EndY=28.75 EndZ=0
    g39: LineSegment StartX=-49.19 StartY=25.75 StartZ=0 EndX=-16.28 EndY=25.75 EndZ=0
    g40: LineSegment StartX=-49.19 StartY=23 StartZ=0 EndX=-11.49 EndY=23 EndZ=0
    g41: LineSegment StartX=-49.19 StartY=20 StartZ=0 EndX=-11.49 EndY=20 EndZ=0
    g42: LineSegment StartX=-49.19 StartY=17.25 StartZ=0 EndX=-1.5 EndY=17.25 EndZ=0
    g43: LineSegment StartX=-49.19 StartY=14.25 StartZ=0 EndX=-1.5 EndY=14.25 EndZ=0
    g44: LineSegment StartX=-49.19 StartY=11.5 StartZ=0 EndX=-1.5 EndY=11.5 EndZ=0
    g45: LineSegment StartX=-49.19 StartY=8.5 StartZ=0 EndX=-1.5 EndY=8.5 EndZ=0
    g46: LineSegment StartX=-49.19 StartY=5.75 StartZ=0 EndX=-1.5 EndY=5.75 EndZ=0
    g47: LineSegment StartX=-49.19 StartY=2.75 StartZ=0 EndX=-1.5 EndY=2.75 EndZ=0
  constraints (120):
    c: Vertical(g0)
    c: Distance(g0) = 3
    c: Block(g0)
    c: Vertical(g1)
    c: Distance(g1) = 3
    c: Vertical(g2)
    c: Equal(g0,g2) = 3
    c: Block(g2)
    c: Vertical(g3)
    c: Equal(g1,g3) = 3
    c: Vertical(g4)
    c: Equal(g0,g4) = 3
    c: Block(g4)
    c: Vertical(g5)
    c: Equal(g1,g5) = 3
    c: Vertical(g6)
    c: Equal(g0,g6) = 3
    c: Block(g6)
    c: Vertical(g7)
    c: Equal(g1,g7) = 3
    c: Vertical(g8)
    c: Equal(g0,g8) = 3
    c: Block(g8)
    c: Vertical(g9)
    c: Equal(g1,g9) = 3
    c: Vertical(g10)
    c: Equal(g0,g10) = 3
    c: Block(g10)
    c: Vertical(g11)
    c: Equal(g1,g11) = 3
    c: Block(g12)
    c: Block(g13)
    c: Block(g14)
    c: Block(g15)
    c: Block(g16)
    c: Block(g17)
    c: Block(g18)
    c: Block(g19)
    c: Block(g20)
    c: Block(g21)
    c: Block(g22)
    c: Block(g23)
    c: Block(g11)
    c: Block(g9)
    c: Block(g7)
    c: Block(g5)
    c: Block(g3)
    c: Block(g1)
    c: Coincident(g24,g0)
    c: Coincident(g24,g12)
    c: Horizontal(g24)
    c: Coincident(g25,g0)
    c: Coincident(g25,g12)
    c: Horizontal(g25)
    c: Coincident(g26,g1)
    c: Coincident(g26,g13)
    c: Horizontal(g26)
    c: Coincident(g27,g1)
    c: Coincident(g27,g13)
    c: Horizontal(g27)
    c: Coincident(g28,g2)
    c: Coincident(g28,g14)
    c: Horizontal(g28)
    c: Coincident(g29,g2)
    c: Coincident(g29,g14)
    c: Horizontal(g29)
    c: Coincident(g30,g3)
    c: Coincident(g30,g15)
    c: Horizontal(g30)
    c: Coincident(g31,g3)
    c: Coincident(g31,g15)
    c: Horizontal(g31)
    c: Coincident(g32,g4)
    c: Coincident(g32,g16)
    c: Horizontal(g32)
    c: Coincident(g33,g4)
    c: Coincident(g33,g16)
    c: Horizontal(g33)
    c: Coincident(g34,g5)
    c: Coincident(g34,g17)
    c: Horizontal(g34)
    c: Coincident(g35,g5)
    c: Coincident(g35,g17)
    c: Horizontal(g35)
    c: Coincident(g36,g6)
    c: Coincident(g36,g19)
    c: Horizontal(g36)
    c: Coincident(g37,g6)
    c: Coincident(g37,g19)
    c: Horizontal(g37)
    c: Coincident(g38,g7)
    c: Coincident(g38,g18)
    c: Horizontal(g38)
    c: Coincident(g39,g7)
    c: Coincident(g39,g18)
    c: Horizontal(g39)
    c: Coincident(g40,g8)
    c: Coincident(g40,g20)
    c: Horizontal(g40)
    c: Coincident(g41,g8)
    c: Coincident(g41,g20)
    c: Horizontal(g41)
    c: Coincident(g42,g9)
    c: Coincident(g42,g23)
    c: Horizontal(g42)
    c: Coincident(g43,g9)
    c: Coincident(g43,g23)
    c: Horizontal(g43)
    c: Coincident(g44,g10)
    c: Coincident(g44,g22)
    c: Horizontal(g44)
    c: Coincident(g45,g10)
    c: Coincident(g45,g22)
    c: Horizontal(g45)
    c: Coincident(g46,g11)
    c: Coincident(g46,g21)
    c: Horizontal(g46)
    c: Coincident(g47,g11)
    c: Coincident(g47,g21)
    c: Horizontal(g47)
FEATURE [Part::Extrusion] Extrude061
  Base = -> Sketch070
  Dir = (1,0,0)
  DirMode = 2
  FaceMakerClass = Part::FaceMakerBullseye
  LengthFwd = 23
  LengthRev = 0
  Placement = pos=(-19,0,0) rot=(0,0,1;0rad)
  Solid = true
  Symmetric = false
FEATURE [Part::Fillet] Fillet052  label="removeToCreateVentalationHoles002"
  Base = -> Extrude061
  Edges = <same value as first occurrence — deduplicated (x6 in doc)>
  Placement = pos=(7,0.02,0) rot=(0,0,1;0rad)
FEATURE [Part::MultiFuse] Fusion130  label="bottom013"
  Shapes = -> [Cut054,Cut034]
FEATURE [Part::Cut] Cut055
  Base = -> Fusion130
  Tool = -> Fillet052
FEATURE [Part::Cylinder] Cylinder054
  Angle = 360
  AttacherType = Attacher::AttachEngine3D
  Height = 20
  Placement = pos=(0,0,36.15) rot=(0,0,1;0rad)
  Radius = 4
FEATURE [Sketcher::SketchObject] Sketch071  label="bottomSketch002"
  FullyConstrained = true
  sketch-geometry (32):
    g0: LineSegment StartX=3.3 StartY=-6.03275e-07 StartZ=0 EndX=98 EndY=-6.03275e-07 EndZ=0
    g1: ArcOfCircle CenterX=98 CenterY=19 CenterZ=0 NormalX=0 NormalY=0 NormalZ=1 AngleXU=0 Radius=19 StartAngle=4.71239 EndAngle=5.71103
    g2: LineSegment StartX=6.3 StartY=8 StartZ=0 EndX=3.3 EndY=8 EndZ=0
    g3: LineSegment StartX=3.3 StartY=8 StartZ=0 EndX=3.3 EndY=-6.03275e-07 EndZ=0
    g4: ArcOfCircle CenterX=8.3 CenterY=5 CenterZ=0 NormalX=0 NormalY=0 NormalZ=1 AngleXU=0 Radius=2 StartAngle=3.14159 EndAngle=4.71239
    g5: LineSegment StartX=6.3 StartY=8 StartZ=0 EndX=6.3 EndY=5 EndZ=0
    g6: ArcOfCircle CenterX=98 CenterY=19 CenterZ=0 NormalX=0 NormalY=0 NormalZ=1 AngleXU=0 Radius=12.7 StartAngle=4.71239 EndAngle=6.28319
    g7: LineSegment StartX=94.7 StartY=3 StartZ=0 EndX=8.3 EndY=3 EndZ=0
    g8-g12: Circle x5 (B-spline internal-alignment scaffolding for g13; pole/knot coordinates omitted)
    g13: BSplineCurve PolesCount=5 KnotsCount=3 Degree=3 IsPeriodic=0
    g14: GeomPoint X=98 Y=6.3 Z=0
    g15: GeomPoint X=96.3938 Y=4.71946 Z=0
    g16: GeomPoint X=94.7 Y=3 Z=0
    g17-g23: Circle x7 (B-spline internal-alignment scaffolding for g24; pole/knot coordinates omitted)
    g24: BSplineCurve PolesCount=7 KnotsCount=5 Degree=3 IsPeriodic=0
    g25-g29: GeomPoint x5 (B-spline internal-alignment scaffolding for g24; pole/knot coordinates omitted)
    g30: ArcOfCircle CenterX=98 CenterY=19 CenterZ=0 NormalX=0 NormalY=0 NormalZ=1 AngleXU=0 Radius=15.7 StartAngle=5.81226 EndAngle=6.28319
    g31: LineSegment StartX=110.7 StartY=19 StartZ=0 EndX=113.7 EndY=19 EndZ=0
  constraints (41):
    c: Horizontal(g0)
    c: Coincident(g1,g0)
    c: Block(g1)
    c: Horizontal(g2)
    c: Distance(g2) = 3
    c: Coincident(g3,g2)
    c: Vertical(g3)
    c: Coincident(g3,g0)
    c: Block(g4)
    c: Block(g2)
    c: Coincident(g5,g2)
    c: Coincident(g5,g4)
    c: Vertical(g5)
    c: Coincident(g6,g1)
    c: Block(g6)
    c: Coincident(g7,g4)
    c: Horizontal(g7)
    c: Block(g0)
    c: Block(g7)
    c: Block(g3)
    c: Coincident(g13,g6)
    c: Weight(g8) = 1
    c: Equal(g8, g9-g12) x4
    c: Coincident(g13,g7)
    c: InternalAlignment(g8-g12 -> g13) x5
    c: InternalAlignment(g14,g13)
    c: InternalAlignment(g15,g13)
    c: InternalAlignment(g16,g13)
    c: Block(g13)
    c: Weight(g17) = 1
    c: Equal(g17, g18-g23) x6
    c: Coincident(g24,g1)
    c: InternalAlignment(g17-g23 -> g24) x7
    c: InternalAlignment(g25-g29 -> g24) x5
    c: Block(g24)
    c: Coincident(g30,g24)
    c: Coincident(g31,g6)
    c: Coincident(g31,g30)
    c: Horizontal(g31)
    c: Block(g31)
    c: Block(g30)
FEATURE [Part::Extrusion] Extrude062  label="bottom014"
  Base = -> Sketch071
  Dir = (0,0,1)
  DirMode = 2
  FaceMakerClass = Part::FaceMakerBullseye
  LengthFwd = 71.4
  LengthRev = 0
  Placement = pos=(0,0,0.3) rot=(0,0,1;0rad)
  Solid = true
  Symmetric = false
FEATURE [Part::Fillet] Fillet054
  Base = -> Extrude062
  Edges = 1 edges r=2.4: [Edge17]
FEATURE [Part::Fillet] Fillet055  label="bottom015"
  Base = -> Fillet054
  Edges = 1 edges r=2.4: [Edge36]
FEATURE [Part::Cylinder] Cylinder055
  Angle = 360
  AttacherType = Attacher::AttachEngine3D
  Height = 10
  Placement = pos=(0,0,36.15) rot=(0,0,1;0rad)
  Radius = 4
FEATURE [Part::MultiFuse] Fusion131  label="removeToCreateHoleForPlugHousing002"
  Placement = pos=(70,19,36.15) rot=(0,1,0;1.5708rad)
  Shapes = -> [Cylinder054,Cylinder055]
FEATURE [Part::Cut] Cut056  label="Bottom001"
  Base = -> Fillet055
  Placement = pos=(9,0,0) rot=(0,0,1;0rad)
  Tool = -> Fusion131
FEATURE [Part::Cut] Cut057
  Base = -> Cut055
  Tool = -> Cut056
FEATURE [Sketcher::SketchObject] Sketch072  label="topSketch021"
  FullyConstrained = true
  sketch-geometry (4):
    g0: ArcOfCircle CenterX=105 CenterY=19 CenterZ=0 NormalX=0 NormalY=0 NormalZ=1 AngleXU=0 Radius=20.6155 StartAngle=5.54125 EndAngle=6.28319
    g1: ArcOfCircle CenterX=105 CenterY=19 CenterZ=0 NormalX=0 NormalY=0 NormalZ=1 AngleXU=0 Radius=13 StartAngle=5.54125 EndAngle=6.28319
    g2: LineSegment StartX=118 StartY=19 StartZ=0 EndX=125.616 EndY=19 EndZ=0
    g3: LineSegment StartX=114.583 StartY=10.2157 StartZ=0 EndX=120.197 EndY=5.06982 EndZ=0
  constraints (7):
    c: Block(g0)
    c: Block(g1)
    c: Coincident(g2,g1)
    c: Coincident(g2,g0)
    c: Horizontal(g2)
    c: Coincident(g3,g1)
    c: Coincident(g3,g0)
FEATURE [Part::Extrusion] Extrude063  label="bottomPlugHousingBit003"
  Base = -> Sketch072
  Dir = (0,0,1)
  DirMode = 2
  FaceMakerClass = Part::FaceMakerBullseye
  LengthFwd = 72
  LengthRev = 0
  Solid = true
  Symmetric = false
FEATURE [Part::Cylinder] Cylinder056
  Angle = 360
  AttacherType = Attacher::AttachEngine3D
  Height = 20
  Placement = pos=(0,0,36.15) rot=(0,0,1;0rad)
  Radius = 14.3
FEATURE [Part::Cylinder] Cylinder057
  Angle = 360
  AttacherType = Attacher::AttachEngine3D
  Height = 10
  Placement = pos=(0,0,36.15) rot=(0,0,1;0rad)
  Radius = 4
FEATURE [Part::Box] Box034  label="removeToCreteHoleForPlugHousing047"
  AttacherType = Attacher::AttachEngine3D
  Height = 28.6
  Length = 20
  Placement = pos=(106.15,0,21.7) rot=(0,0,1;0rad)
  Width = 19
FEATURE [Part::Cylinder] Cylinder058
  Angle = 360
  AttacherType = Attacher::AttachEngine3D
  Height = 20
  Placement = pos=(0,0,36.15) rot=(0,0,1;0rad)
  Radius = 14.3
FEATURE [Part::Cylinder] Cylinder059
  Angle = 360
  AttacherType = Attacher::AttachEngine3D
  Height = 10
  Placement = pos=(0,0,36.15) rot=(0,0,1;0rad)
  Radius = 4
FEATURE [Part::MultiFuse] Fusion134  label="removeToCreteHoleForPlugHousing046"
  Placement = pos=(70,19,36) rot=(0,1,0;1.5708rad)
  Shapes = -> [Cylinder058,Cylinder059]
FEATURE [Part::Cylinder] Cylinder060
  Angle = 360
  AttacherType = Attacher::AttachEngine3D
  Height = 20
  Placement = pos=(0,0,36.15) rot=(0,0,1;0rad)
  Radius = 14
FEATURE [Part::Cylinder] Cylinder061
  Angle = 360
  AttacherType = Attacher::AttachEngine3D
  Height = 10
  Placement = pos=(0,0,36.15) rot=(0,0,1;0rad)
  Radius = 4
FEATURE [Part::MultiFuse] Fusion135  label="removeToCreteHoleForPlugHousing048"
  Placement = pos=(70,19,36) rot=(0,1,0;1.5708rad)
  Shapes = -> [Cylinder060,Cylinder061]
FEATURE [Part::Box] Box035  label="removeToCreteHoleForPlugHousing049"
  AttacherType = Attacher::AttachEngine3D
  Height = 28.6
  Length = 20
  Placement = pos=(106.15,0,21.7) rot=(0,0,1;0rad)
  Width = 19
FEATURE [Part::MultiFuse] Fusion133  label="removeToCreteHoleForPlugHousing045"
  Placement = pos=(0,0,-28.3) rot=(0,0,1;0rad)
  Shapes = -> [Box035,Fusion134]
FEATURE [Part::MultiFuse] Fusion138  label="removeToCreteHoleForPlugHousing051"
  Placement = pos=(70,19,36) rot=(0,1,0;1.5708rad)
  Shapes = -> [Cylinder056,Cylinder057]
FEATURE [Part::MultiFuse] Fusion137  label="removeToCreteHoleForPlugHousing050"
  Placement = pos=(0,0,28.3) rot=(0,0,1;0rad)
  Shapes = -> [Box034,Fusion138]
FEATURE [Part::MultiFuse] Fusion132  label="removeToCreatePlugHousingBottomBit002"
  Shapes = -> [Fusion133,Fusion137]
FEATURE [Part::MultiFuse] Fusion136  label="removeToCreatePlugHousingBottomBit003"
  Shapes = -> [Fusion135,Fusion132]
FEATURE [Part::Cut] Cut058  label="bottomPlugHousingBit002"
  Base = -> Extrude063
  Placement = pos=(-0.09,0,0) rot=(0,0,1;0rad)
  Tool = -> Fusion136
FEATURE [Sketcher::SketchObject] Sketch073  label="bottomSketch003"
  FullyConstrained = true
  sketch-geometry (45):
    g0: LineSegment StartX=6.29999 StartY=8 StartZ=0 EndX=3.29999 EndY=8 EndZ=0
    g1: LineSegment StartX=3.29999 StartY=8 StartZ=0 EndX=3.29999 EndY=-6.03275e-07 EndZ=0
    g2: ArcOfCircle CenterX=8.29999 CenterY=5 CenterZ=0 NormalX=0 NormalY=0 NormalZ=1 AngleXU=0 Radius=2 StartAngle=3.14159 EndAngle=4.71239
    g3: LineSegment StartX=6.29999 StartY=8 StartZ=0 EndX=6.29999 EndY=5 EndZ=0
    g4: ArcOfCircle CenterX=105 CenterY=19 CenterZ=0 NormalX=0 NormalY=0 NormalZ=1 AngleXU=0 Radius=12.7 StartAngle=4.71239 EndAngle=5.94289
    g5-g11: Circle x7 (B-spline internal-alignment scaffolding for g12; pole/knot coordinates omitted)
    g12: BSplineCurve PolesCount=7 KnotsCount=5 Degree=3 IsPeriodic=0
    g13-g17: GeomPoint x5 (B-spline internal-alignment scaffolding for g12; pole/knot coordinates omitted)
    g18: ArcOfCircle CenterX=105 CenterY=19 CenterZ=0 NormalX=0 NormalY=0 NormalZ=1 AngleXU=0 Radius=15.7 StartAngle=5.81226 EndAngle=6.28319
    g19: BSplineCurve PolesCount=5 KnotsCount=3 Degree=3 IsPeriodic=0
    g20: LineSegment StartX=8.29999 StartY=3 StartZ=0 EndX=101.7 EndY=3 EndZ=0
    g21: LineSegment StartX=3.29999 StartY=-6.03275e-07 StartZ=0 EndX=105 EndY=-6.03275e-07 EndZ=0
    g22: LineSegment StartX=120.974 StartY=8.71251 StartZ=0 EndX=122.332 EndY=7.83778 EndZ=0
    g23: LineSegment StartX=105 StartY=-6.03274e-07 StartZ=0 EndX=113 EndY=-6.03274e-07 EndZ=0
    g24: ArcOfCircle CenterX=105 CenterY=19 CenterZ=0 NormalX=0 NormalY=0 NormalZ=1 AngleXU=0 Radius=20.6155 StartAngle=5.11091 EndAngle=5.71103
    g25: ArcOfCircle CenterX=117.7 CenterY=19 CenterZ=0 NormalX=0 NormalY=0 NormalZ=1 AngleXU=0 Radius=3 StartAngle=1.2e-15 EndAngle=2.10468
    g26: Circle CenterX=116.345 CenterY=16.3232 CenterZ=0 NormalX=0 NormalY=0 NormalZ=1 AngleXU=0 Radius=1
    g27: Circle CenterX=117.24 CenterY=15.7584 CenterZ=0 NormalX=0 NormalY=0 NormalZ=1 AngleXU=0 Radius=1
    g28: Circle CenterX=116.972 CenterY=14.7612 CenterZ=0 NormalX=0 NormalY=0 NormalZ=1 AngleXU=0 Radius=1
    g29: BSplineCurve PolesCount=3 KnotsCount=2 Degree=2 IsPeriodic=0
    g30: GeomPoint X=116.345 Y=16.3232 Z=0
    g31: GeomPoint X=116.972 Y=14.7612 Z=0
    g32: Circle CenterX=115.828 CenterY=17.157 CenterZ=0 NormalX=0 NormalY=0 NormalZ=1 AngleXU=0 Radius=1
    g33: Circle CenterX=115.841 CenterY=16.639 CenterZ=0 NormalX=0 NormalY=0 NormalZ=1 AngleXU=0 Radius=1
    g34: Circle CenterX=116.345 CenterY=16.3232 CenterZ=0 NormalX=0 NormalY=0 NormalZ=1 AngleXU=0 Radius=1
    g35: BSplineCurve PolesCount=3 KnotsCount=2 Degree=2 IsPeriodic=0
    g36: GeomPoint X=115.828 Y=17.157 Z=0
    g37: GeomPoint X=116.345 Y=16.3232 Z=0
    g38: LineSegment StartX=115.828 StartY=17.157 StartZ=0 EndX=115.828 EndY=20.8307 EndZ=0
    g39: Circle CenterX=115.828 CenterY=20.8307 CenterZ=0 NormalX=0 NormalY=0 NormalZ=1 AngleXU=0 Radius=1
    g40: Circle CenterX=115.831 CenterY=21.3396 CenterZ=0 NormalX=0 NormalY=0 NormalZ=1 AngleXU=0 Radius=1
    g41: Circle CenterX=116.173 CenterY=21.5825 CenterZ=0 NormalX=0 NormalY=0 NormalZ=1 AngleXU=0 Radius=1
    g42: BSplineCurve PolesCount=3 KnotsCount=2 Degree=2 IsPeriodic=0
    g43: GeomPoint X=115.828 Y=20.8307 Z=0
    g44: GeomPoint X=116.173 Y=21.5825 Z=0
  constraints (70):
    c: Horizontal(g0)
    c: Distance(g0) = 3
    c: Coincident(g1,g0)
    c: Vertical(g1)
    c: Block(g2)
    c: Block(g0)
    c: Coincident(g3,g0)
    c: Coincident(g3,g2)
    c: Vertical(g3)
    c: Block(g1)
    c: Block(g4)
    c: Coincident(g19,g4)
    c: Block(g19)
    c: Equal(g5, g6-g11) x6
    c: InternalAlignment(g5-g11 -> g12) x7
    c: InternalAlignment(g13-g17 -> g12) x5
    c: Block(g12)
    c: Coincident(g18,g12)
    c: Block(g18)
    c: Coincident(g20,g2)
    c: Coincident(g20,g19)
    c: Horizontal(g20)
    c: Distance(g20) = 93.4
    c: Coincident(g21,g1)
    c: Horizontal(g21)
    c: Distance(g21) = 101.7
    c: Horizontal(g23)
    c: Distance(g23) = 8
    c: Coincident(g24,g23)
    c: Block(g23)
    c: Coincident(g22,g24)
    c: Block(g24)
    c: Block(g22)
    c: Distance(g22) = 1.61553
    c: Coincident(g25,g18)
    c: Block(g25)
    c: Weight(g26) = 1
    c: Equal(g26,g27)
    c: Equal(g26,g28)
    c: Coincident(g29,g4)
    c: InternalAlignment(g26,g29)
    c: InternalAlignment(g27,g29)
    c: InternalAlignment(g28,g29)
    c: InternalAlignment(g30,g29)
    c: InternalAlignment(g31,g29)
    c: Block(g29)
    c: Weight(g32) = 1
    c: Equal(g32,g33)
    c: Equal(g32,g34)
    c: Coincident(g35,g29)
    c: InternalAlignment(g32,g35)
    c: InternalAlignment(g33,g35)
    c: InternalAlignment(g34,g35)
    c: InternalAlignment(g36,g35)
    c: InternalAlignment(g37,g35)
    c: Block(g35)
    c: Coincident(g38,g35)
    c: Vertical(g38)
    c: Block(g38)
    c: Coincident(g42,g38)
    c: Weight(g39) = 1
    c: Equal(g39,g40)
    c: Equal(g39,g41)
    c: Coincident(g42,g25)
    c: InternalAlignment(g39,g42)
    c: InternalAlignment(g40,g42)
    c: InternalAlignment(g41,g42)
    c: InternalAlignment(g43,g42)
    c: InternalAlignment(g44,g42)
    c: Block(g42)
FEATURE [Part::Extrusion] Extrude064  label="bottom016"
  Base = -> Sketch073
  Dir = (0,0,1)
  DirMode = 2
  FaceMakerClass = Part::FaceMakerBullseye
  LengthFwd = 71.4
  LengthRev = 0
  Placement = pos=(0,0,0.3) rot=(0,0,1;0rad)
  Solid = true
  Symmetric = false
FEATURE [Part::Revolution] Revolve157  label="removeToCreateScrewAndThreadedInsertHole063"
  Angle = 360
  Axis = (0,1,0)
  Base = (0,0,0)
  FaceMakerClass = Part::FaceMakerBullseye
  Placement = pos=(12.5,0,10) rot=(0,0,1;0rad)
  Solid = false
  Source = -> Face141
  Symmetric = false
FEATURE [Sketcher::SketchObject] Sketch074
  FullyConstrained = true
  Placement = pos=(117,19,0) rot=(0.57735,0.57735,0.57735;2.0944rad)
  sketch-geometry (48):
    g0: LineSegment StartX=-49.19 StartY=69.25 StartZ=0 EndX=-49.19 EndY=66.25 EndZ=0
    g1: LineSegment StartX=-49.19 StartY=63.5 StartZ=0 EndX=-49.19 EndY=60.5 EndZ=0
    g2: LineSegment StartX=-49.19 StartY=57.75 StartZ=0 EndX=-49.19 EndY=54.75 EndZ=0
    g3: LineSegment StartX=-49.19 StartY=52 StartZ=0 EndX=-49.19 EndY=49 EndZ=0
    g4: LineSegment StartX=-49.19 StartY=46.25 StartZ=0 EndX=-49.19 EndY=43.25 EndZ=0
    g5: LineSegment StartX=-49.19 StartY=40.5 StartZ=0 EndX=-49.19 EndY=37.5 EndZ=0
    g6: LineSegment StartX=-49.19 StartY=34.5 StartZ=0 EndX=-49.19 EndY=31.5 EndZ=0
    g7: LineSegment StartX=-49.19 StartY=28.75 StartZ=0 EndX=-49.19 EndY=25.75 EndZ=0
    g8: LineSegment StartX=-49.19 StartY=23 StartZ=0 EndX=-49.19 EndY=20 EndZ=0
    g9: LineSegment StartX=-49.19 StartY=17.25 StartZ=0 EndX=-49.19 EndY=14.25 EndZ=0
    g10: LineSegment StartX=-49.19 StartY=11.5 StartZ=0 EndX=-49.19 EndY=8.5 EndZ=0
    g11: LineSegment StartX=-49.19 StartY=5.75 StartZ=0 EndX=-49.19 EndY=2.75 EndZ=0
    g12: ArcOfCircle CenterX=-1.5 CenterY=67.75 CenterZ=0 NormalX=0 NormalY=0 NormalZ=1 AngleXU=0 Radius=1.5 StartAngle=4.71239 EndAngle=7.85398
    g13: ArcOfCircle CenterX=-1.5 CenterY=62 CenterZ=0 NormalX=0 NormalY=0 NormalZ=1 AngleXU=0 Radius=1.5 StartAngle=4.71239 EndAngle=7.85398
    g14: ArcOfCircle CenterX=-1.5 CenterY=56.25 CenterZ=0 NormalX=0 NormalY=0 NormalZ=1 AngleXU=0 Radius=1.5 StartAngle=4.71239 EndAngle=7.85398
    g15: ArcOfCircle CenterX=-11.49 CenterY=50.5 CenterZ=0 NormalX=0 NormalY=0 NormalZ=1 AngleXU=0 Radius=1.5 StartAngle=4.71239 EndAngle=7.85398
    g16: ArcOfCircle CenterX=-16.28 CenterY=44.75 CenterZ=0 NormalX=0 NormalY=0 NormalZ=1 AngleXU=0 Radius=1.5 StartAngle=4.71239 EndAngle=7.85398
    g17: ArcOfCircle CenterX=-18.2337 CenterY=39 CenterZ=0 NormalX=0 NormalY=0 NormalZ=1 AngleXU=0 Radius=1.5 StartAngle=4.71485 EndAngle=7.85398
    g18: ArcOfCircle CenterX=-16.2837 CenterY=27.25 CenterZ=0 NormalX=0 NormalY=0 NormalZ=1 AngleXU=0 Radius=1.5 StartAngle=4.71485 EndAngle=7.85398
    g19: ArcOfCircle CenterX=-18.2337 CenterY=33 CenterZ=0 NormalX=0 NormalY=0 NormalZ=1 AngleXU=0 Radius=1.5 StartAngle=4.71485 EndAngle=7.85398
    g20: ArcOfCircle CenterX=-11.49 CenterY=21.5 CenterZ=0 NormalX=0 NormalY=0 NormalZ=1 AngleXU=0 Radius=1.5 StartAngle=4.71239 EndAngle=7.85398
    g21: ArcOfCircle CenterX=-1.5 CenterY=4.25 CenterZ=0 NormalX=0 NormalY=0 NormalZ=1 AngleXU=0 Radius=1.5 StartAngle=4.71239 EndAngle=7.85398
    g22: ArcOfCircle CenterX=-1.5 CenterY=10 CenterZ=0 NormalX=0 NormalY=0 NormalZ=1 AngleXU=0 Radius=1.5 StartAngle=4.71239 EndAngle=7.85398
    g23: ArcOfCircle CenterX=-1.5 CenterY=15.75 CenterZ=0 NormalX=0 NormalY=0 NormalZ=1 AngleXU=0 Radius=1.5 StartAngle=4.71239 EndAngle=7.85398
    g24: LineSegment StartX=-49.19 StartY=69.25 StartZ=0 EndX=-1.5 EndY=69.25 EndZ=0
    g25: LineSegment StartX=-49.19 StartY=66.25 StartZ=0 EndX=-1.5 EndY=66.25 EndZ=0
    g26: LineSegment StartX=-49.19 StartY=63.5 StartZ=0 EndX=-1.5 EndY=63.5 EndZ=0
    g27: LineSegment StartX=-49.19 StartY=60.5 StartZ=0 EndX=-1.5 EndY=60.5 EndZ=0
    g28: LineSegment StartX=-49.19 StartY=57.75 StartZ=0 EndX=-1.5 EndY=57.75 EndZ=0
    g29: LineSegment StartX=-49.19 StartY=54.75 StartZ=0 EndX=-1.5 EndY=54.75 EndZ=0
    g30: LineSegment StartX=-49.19 StartY=52 StartZ=0 EndX=-11.49 EndY=52 EndZ=0
    g31: LineSegment StartX=-49.19 StartY=49 StartZ=0 EndX=-11.49 EndY=49 EndZ=0
    g32: LineSegment StartX=-49.19 StartY=46.25 StartZ=0 EndX=-16.28 EndY=46.25 EndZ=0
    g33: LineSegment StartX=-49.19 StartY=43.25 StartZ=0 EndX=-16.28 EndY=43.25 EndZ=0
    g34: LineSegment StartX=-49.19 StartY=40.5 StartZ=0 EndX=-18.2337 EndY=40.5 EndZ=0
    g35: LineSegment StartX=-49.19 StartY=37.5 StartZ=0 EndX=-18.23 EndY=37.5 EndZ=0
    g36: LineSegment StartX=-49.19 StartY=34.5 StartZ=0 EndX=-18.2337 EndY=34.5 EndZ=0
    g37: LineSegment StartX=-49.19 StartY=31.5 StartZ=0 EndX=-18.23 EndY=31.5 EndZ=0
    g38: LineSegment StartX=-49.19 StartY=28.75 StartZ=0 EndX=-16.2837 EndY=28.75 EndZ=0
    g39: LineSegment StartX=-49.19 StartY=25.75 StartZ=0 EndX=-16.28 EndY=25.75 EndZ=0
    g40: LineSegment StartX=-49.19 StartY=23 StartZ=0 EndX=-11.49 EndY=23 EndZ=0
    g41: LineSegment StartX=-49.19 StartY=20 StartZ=0 EndX=-11.49 EndY=20 EndZ=0
    g42: LineSegment StartX=-49.19 StartY=17.25 StartZ=0 EndX=-1.5 EndY=17.25 EndZ=0
    g43: LineSegment StartX=-49.19 StartY=14.25 StartZ=0 EndX=-1.5 EndY=14.25 EndZ=0
    g44: LineSegment StartX=-49.19 StartY=11.5 StartZ=0 EndX=-1.5 EndY=11.5 EndZ=0
    g45: LineSegment StartX=-49.19 StartY=8.5 StartZ=0 EndX=-1.5 EndY=8.5 EndZ=0
    g46: LineSegment StartX=-49.19 StartY=5.75 StartZ=0 EndX=-1.5 EndY=5.75 EndZ=0
    g47: LineSegment StartX=-49.19 StartY=2.75 StartZ=0 EndX=-1.5 EndY=2.75 EndZ=0
  constraints (120):
    c: Vertical(g0)
    c: Distance(g0) = 3
    c: Block(g0)
    c: Vertical(g1)
    c: Distance(g1) = 3
    c: Vertical(g2)
    c: Equal(g0,g2) = 3
    c: Block(g2)
    c: Vertical(g3)
    c: Equal(g1,g3) = 3
    c: Vertical(g4)
    c: Equal(g0,g4) = 3
    c: Block(g4)
    c: Vertical(g5)
    c: Equal(g1,g5) = 3
    c: Vertical(g6)
    c: Equal(g0,g6) = 3
    c: Block(g6)
    c: Vertical(g7)
    c: Equal(g1,g7) = 3
    c: Vertical(g8)
    c: Equal(g0,g8) = 3
    c: Block(g8)
    c: Vertical(g9)
    c: Equal(g1,g9) = 3
    c: Vertical(g10)
    c: Equal(g0,g10) = 3
    c: Block(g10)
    c: Vertical(g11)
    c: Equal(g1,g11) = 3
    c: Block(g12)
    c: Block(g13)
    c: Block(g14)
    c: Block(g15)
    c: Block(g16)
    c: Block(g17)
    c: Block(g18)
    c: Block(g19)
    c: Block(g20)
    c: Block(g21)
    c: Block(g22)
    c: Block(g23)
    c: Block(g11)
    c: Block(g9)
    c: Block(g7)
    c: Block(g5)
    c: Block(g3)
    c: Block(g1)
    c: Coincident(g24,g0)
    c: Coincident(g24,g12)
    c: Horizontal(g24)
    c: Coincident(g25,g0)
    c: Coincident(g25,g12)
    c: Horizontal(g25)
    c: Coincident(g26,g1)
    c: Coincident(g26,g13)
    c: Horizontal(g26)
    c: Coincident(g27,g1)
    c: Coincident(g27,g13)
    c: Horizontal(g27)
    c: Coincident(g28,g2)
    c: Coincident(g28,g14)
    c: Horizontal(g28)
    c: Coincident(g29,g2)
    c: Coincident(g29,g14)
    c: Horizontal(g29)
    c: Coincident(g30,g3)
    c: Coincident(g30,g15)
    c: Horizontal(g30)
    c: Coincident(g31,g3)
    c: Coincident(g31,g15)
    c: Horizontal(g31)
    c: Coincident(g32,g4)
    c: Coincident(g32,g16)
    c: Horizontal(g32)
    c: Coincident(g33,g4)
    c: Coincident(g33,g16)
    c: Horizontal(g33)
    c: Coincident(g34,g5)
    c: Coincident(g34,g17)
    c: Horizontal(g34)
    c: Coincident(g35,g5)
    c: Coincident(g35,g17)
    c: Horizontal(g35)
    c: Coincident(g36,g6)
    c: Coincident(g36,g19)
    c: Horizontal(g36)
    c: Coincident(g37,g6)
    c: Coincident(g37,g19)
    c: Horizontal(g37)
    c: Coincident(g38,g7)
    c: Coincident(g38,g18)
    c: Horizontal(g38)
    c: Coincident(g39,g7)
    c: Coincident(g39,g18)
    c: Horizontal(g39)
    c: Coincident(g40,g8)
    c: Coincident(g40,g20)
    c: Horizontal(g40)
    c: Coincident(g41,g8)
    c: Coincident(g41,g20)
    c: Horizontal(g41)
    c: Coincident(g42,g9)
    c: Coincident(g42,g23)
    c: Horizontal(g42)
    c: Coincident(g43,g9)
    c: Coincident(g43,g23)
    c: Horizontal(g43)
    c: Coincident(g44,g10)
    c: Coincident(g44,g22)
    c: Horizontal(g44)
    c: Coincident(g45,g10)
    c: Coincident(g45,g22)
    c: Horizontal(g45)
    c: Coincident(g46,g11)
    c: Coincident(g46,g21)
    c: Horizontal(g46)
    c: Coincident(g47,g11)
    c: Coincident(g47,g21)
    c: Horizontal(g47)
FEATURE [Part::Extrusion] Extrude065
  Base = -> Sketch074
  Dir = (1,0,0)
  DirMode = 2
  FaceMakerClass = Part::FaceMakerBullseye
  LengthFwd = 23
  LengthRev = 0
  Placement = pos=(-19,0,0) rot=(0,0,1;0rad)
  Solid = true
  Symmetric = false
FEATURE [Part::Fillet] Fillet056  label="removeToCreateVentalationHoles003"
  Base = -> Extrude065
  Edges = <same value as first occurrence — deduplicated (x6 in doc)>
  Placement = pos=(7,0.02,0) rot=(0,0,1;0rad)
FEATURE [Part::Revolution] Revolve158  label="removeToCreateScrewAndThreadedInsertHole065"
  Angle = 360
  Axis = (0,1,0)
  Base = (0,0,0)
  FaceMakerClass = Part::FaceMakerBullseye
  Placement = pos=(12.5,0,62) rot=(0,0,1;0rad)
  Solid = false
  Source = -> Face146
  Symmetric = false
FEATURE [Part::Revolution] Revolve159  label="removeToCreateScrewAndThreadedInsertHole066"
  Angle = 360
  Axis = (0,1,0)
  Base = (0,0,0)
  FaceMakerClass = Part::FaceMakerBullseye
  Placement = pos=(89.5,0,68.5) rot=(0,0,1;0rad)
  Solid = false
  Source = -> Face143
  Symmetric = false
FEATURE [Part::Revolution] Revolve160  label="removeToCreateScrewAndThreadedInsertHole067"
  Angle = 360
  Axis = (0,1,0)
  Base = (0,0,0)
  FaceMakerClass = Part::FaceMakerBullseye
  Placement = pos=(89.5,0,3.5) rot=(0,0,1;0rad)
  Solid = false
  Source = -> Face142
  Symmetric = false
FEATURE [Part::Revolution] Revolve161  label="removeToCreateScrewAndThreadedInsertHole068"
  Angle = 360
  Axis = (0,1,0)
  Base = (0,0,0)
  FaceMakerClass = Part::FaceMakerBullseye
  Placement = pos=(109.5,4.7,3.5) rot=(0,0,1;0rad)
  Solid = false
  Source = -> Face145
  Symmetric = false
FEATURE [Part::Revolution] Revolve162  label="removeToCreateScrewAndThreadedInsertHole069"
  Angle = 360
  Axis = (0,1,0)
  Base = (0,0,0)
  FaceMakerClass = Part::FaceMakerBullseye
  Placement = pos=(109.5,4.7,68.5) rot=(0,0,1;0rad)
  Solid = false
  Source = -> Face144
  Symmetric = false
FEATURE [Part::MultiFuse] Fusion141  label="removeToCreateScrewAndThreadedInsertHole064"
  Shapes = -> [Revolve162,Revolve161,Revolve160,Revolve159,Revolve158,Revolve157]
FEATURE [Part::Cylinder] Cylinder062
  Angle = 360
  AttacherType = Attacher::AttachEngine3D
  Height = 20
  Placement = pos=(0,0,36.15) rot=(0,0,1;0rad)
  Radius = 14
FEATURE [Part::Cylinder] Cylinder063
  Angle = 360
  AttacherType = Attacher::AttachEngine3D
  Height = 10
  Placement = pos=(0,0,36.15) rot=(0,0,1;0rad)
  Radius = 4
FEATURE [Part::MultiFuse] Fusion139  label="removeToCreteHoleForPlugHousing052"
  Placement = pos=(70,19,36) rot=(0,1,0;1.5708rad)
  Shapes = -> [Cylinder062,Cylinder063]
FEATURE [Part::Cut] Cut060  label="bottom017"
  Base = -> Extrude064
  Tool = -> Fusion139
FEATURE [Part::Cut] Cut061  label="bottom019"
  Base = -> Cut060
  Tool = -> Fusion141
FEATURE [Part::MultiFuse] Fusion140  label="bottom018"
  Shapes = -> [Cut061,Cut058]
FEATURE [Part::Cut] Cut059  label="bottom020"
  Base = -> Fusion140
  Tool = -> Fillet056
FEATURE [Part::Box] Box036  label="Cube021"
  AttacherType = Attacher::AttachEngine3D
  Height = 80
  Length = 26
  Placement = pos=(0,-1,-5) rot=(0,0,1;0rad)
  Width = 11
FEATURE [Part::Cut] Cut062  label="removeFromBottom002"
  Base = -> Cut057
  Tool = -> Box036
FEATURE [Part::Cut] Cut063
  Base = -> Cut059
  Tool = -> Cut062
FEATURE [Part::Cut] Cut064  label="pcbStands"
  Base = -> Fusion095
  Tool = -> Fusion127
FEATURE [Sketcher::SketchObject] Sketch075  label="topSketch022"
  FullyConstrained = true
  sketch-geometry (6):
    g0: LineSegment StartX=19 StartY=38 StartZ=0 EndX=117 EndY=38 EndZ=0
    g1: ArcOfCircle CenterX=19 CenterY=19 CenterZ=0 NormalX=0 NormalY=0 NormalZ=1 AngleXU=0 Radius=19 StartAngle=1.5708 EndAngle=3.14159
    g2: LineSegment StartX=117 StartY=38 StartZ=0 EndX=117 EndY=19 EndZ=0
    g3: LineSegment StartX=98 StartY=1.0161e-12 StartZ=0 EndX=5.22862e-06 EndY=1.0161e-12 EndZ=0
    g4: LineSegment StartX=5.22862e-06 StartY=19 StartZ=0 EndX=5.22862e-06 EndY=1.0161e-12 EndZ=0
    g5: ArcOfCircle CenterX=98 CenterY=19 CenterZ=0 NormalX=0 NormalY=0 NormalZ=1 AngleXU=0 Radius=19 StartAngle=4.71239 EndAngle=6.28319
  constraints (16):
    c: Horizontal(g0)
    c: Distance(g0) = 98
    c: Coincident(g1,g0)
    c: Block(g1)
    c: Coincident(g2,g0)
    c: Vertical(g2)
    c: Distance(g2) = 19
    c: Horizontal(g3)
    c: Coincident(g4,g1)
    c: Vertical(g4)
    c: Coincident(g3,g4)
    c: Block(g3)
    c: Coincident(g5,g2)
    c: Coincident(g5,g3)
    c: Block(g0)
    c: Block(g5)
FEATURE [Part::Extrusion] Extrude067  label="sideB003"
  Base = -> Sketch075
  Dir = (0,0,1)
  DirMode = 2
  FaceMakerClass = Part::FaceMakerBullseye
  LengthFwd = 3
  LengthRev = 0
  Placement = pos=(0,0,71.7) rot=(0,0,1;0rad)
  Solid = true
  Symmetric = false
FEATURE [Sketcher::SketchObject] Sketch076  label="topSketch023"
  FullyConstrained = true
  sketch-geometry (6):
    g0: LineSegment StartX=19 StartY=38 StartZ=0 EndX=117 EndY=38 EndZ=0
    g1: ArcOfCircle CenterX=19 CenterY=19 CenterZ=0 NormalX=0 NormalY=0 NormalZ=1 AngleXU=0 Radius=19 StartAngle=1.5708 EndAngle=3.14159
    g2: LineSegment StartX=117 StartY=38 StartZ=0 EndX=117 EndY=19 EndZ=0
    g3: LineSegment StartX=98 StartY=1.0161e-12 StartZ=0 EndX=5.22862e-06 EndY=1.0161e-12 EndZ=0
    g4: LineSegment StartX=5.22862e-06 StartY=19 StartZ=0 EndX=5.22862e-06 EndY=1.0161e-12 EndZ=0
    g5: ArcOfCircle CenterX=98 CenterY=19 CenterZ=0 NormalX=0 NormalY=0 NormalZ=1 AngleXU=0 Radius=19 StartAngle=4.71239 EndAngle=6.28319
  constraints (16):
    c: Horizontal(g0)
    c: Distance(g0) = 98
    c: Coincident(g1,g0)
    c: Block(g1)
    c: Coincident(g2,g0)
    c: Vertical(g2)
    c: Distance(g2) = 19
    c: Horizontal(g3)
    c: Coincident(g4,g1)
    c: Vertical(g4)
    c: Coincident(g3,g4)
    c: Block(g3)
    c: Coincident(g5,g2)
    c: Coincident(g5,g3)
    c: Block(g0)
    c: Block(g5)
FEATURE [Part::Extrusion] Extrude066  label="sideA003"
  Base = -> Sketch076
  Dir = (0,0,1)
  DirMode = 2
  FaceMakerClass = Part::FaceMakerBullseye
  LengthFwd = 3
  LengthRev = 0
  Placement = pos=(0,0,-2.7) rot=(0,0,1;0rad)
  Solid = true
  Symmetric = false
FEATURE [Part::MultiFuse] Fusion142  label="removeFromBottom003"
  Placement = pos=(2,0,0) rot=(0,0,1;0rad)
  Shapes = -> [Extrude066,Extrude067]
FEATURE [Part::Cut] Cut065  label="screwRetainers002"
  Base = -> Fusion096
  Tool = -> Fusion142
FEATURE [Sketcher::SketchObject] Sketch077
  FullyConstrained = true
  Placement = pos=(117,19,0) rot=(0.57735,0.57735,0.57735;2.0944rad)
  sketch-geometry (8):
    g0: LineSegment StartX=-49.19 StartY=63.5 StartZ=0 EndX=-49.19 EndY=60.5 EndZ=0
    g1: LineSegment StartX=-49.19 StartY=11.5 StartZ=0 EndX=-49.19 EndY=8.5 EndZ=0
    g2: ArcOfCircle CenterX=-1.5 CenterY=62 CenterZ=0 NormalX=0 NormalY=0 NormalZ=1 AngleXU=0 Radius=1.5 StartAngle=4.71239 EndAngle=7.85398
    g3: ArcOfCircle CenterX=-1.5 CenterY=10 CenterZ=0 NormalX=0 NormalY=0 NormalZ=1 AngleXU=0 Radius=1.5 StartAngle=4.71239 EndAngle=7.85398
    g4: LineSegment StartX=-49.19 StartY=63.5 StartZ=0 EndX=-1.5 EndY=63.5 EndZ=0
    g5: LineSegment StartX=-49.19 StartY=60.5 StartZ=0 EndX=-1.5 EndY=60.5 EndZ=0
    g6: LineSegment StartX=-49.19 StartY=11.5 StartZ=0 EndX=-1.5 EndY=11.5 EndZ=0
    g7: LineSegment StartX=-49.19 StartY=8.5 StartZ=0 EndX=-1.5 EndY=8.5 EndZ=0
  constraints (19):
    c: Vertical(g0)
    c: Distance(g0) = 3
    c: Vertical(g1)
    c: Block(g1)
    c: Block(g2)
    c: Block(g3)
    c: Block(g0)
    c: Coincident(g4,g0)
    c: Coincident(g4,g2)
    c: Horizontal(g4)
    c: Coincident(g5,g0)
    c: Coincident(g5,g2)
    c: Horizontal(g5)
    c: Coincident(g6,g1)
    c: Coincident(g6,g3)
    c: Horizontal(g6)
    c: Coincident(g7,g1)
    c: Coincident(g7,g3)
    c: Horizontal(g7)
FEATURE [Part::Extrusion] Extrude068
  Base = -> Sketch077
  Dir = (1,0,0)
  DirMode = 2
  FaceMakerClass = Part::FaceMakerBullseye
  LengthFwd = 10
  LengthRev = 0
  Solid = true
  Symmetric = false
FEATURE [Part::Fillet] Fillet057  label="removeFromtMoreFrontCaseScrewRetainers002"
  Base = -> Extrude068
  Edges = 4 edges r=1.49: [Edge6,Edge11,Edge18,Edge23]
  Placement = pos=(-12,0,0) rot=(0,0,1;0rad)
FEATURE [Sketcher::SketchObject] Sketch078
  FullyConstrained = true
  Placement = pos=(117,19,0) rot=(0.57735,0.57735,0.57735;2.0944rad)
  sketch-geometry (8):
    g0: LineSegment StartX=-49.19 StartY=69.25 StartZ=0 EndX=-49.19 EndY=66.25 EndZ=0
    g1: LineSegment StartX=-49.19 StartY=5.75 StartZ=0 EndX=-49.19 EndY=2.75 EndZ=0
    g2: ArcOfCircle CenterX=-1.5 CenterY=67.75 CenterZ=0 NormalX=0 NormalY=0 NormalZ=1 AngleXU=0 Radius=1.5 StartAngle=4.71239 EndAngle=7.85398
    g3: ArcOfCircle CenterX=-1.5 CenterY=4.25 CenterZ=0 NormalX=0 NormalY=0 NormalZ=1 AngleXU=0 Radius=1.5 StartAngle=4.71239 EndAngle=7.85398
    g4: LineSegment StartX=-49.19 StartY=69.25 StartZ=0 EndX=-1.5 EndY=69.25 EndZ=0
    g5: LineSegment StartX=-49.19 StartY=66.25 StartZ=0 EndX=-1.5 EndY=66.25 EndZ=0
    g6: LineSegment StartX=-49.19 StartY=5.75 StartZ=0 EndX=-1.5 EndY=5.75 EndZ=0
    g7: LineSegment StartX=-49.19 StartY=2.75 StartZ=0 EndX=-1.5 EndY=2.75 EndZ=0
  constraints (19):
    c: Vertical(g0)
    c: Distance(g0) = 3
    c: Block(g0)
    c: Vertical(g1)
    c: Block(g2)
    c: Block(g3)
    c: Block(g1)
    c: Coincident(g4,g0)
    c: Coincident(g4,g2)
    c: Horizontal(g4)
    c: Coincident(g5,g0)
    c: Coincident(g5,g2)
    c: Horizontal(g5)
    c: Coincident(g6,g1)
    c: Coincident(g6,g3)
    c: Horizontal(g6)
    c: Coincident(g7,g1)
    c: Coincident(g7,g3)
    c: Horizontal(g7)
FEATURE [Part::Extrusion] Extrude069
  Base = -> Sketch078
  Dir = (1,0,0)
  DirMode = 2
  FaceMakerClass = Part::FaceMakerBullseye
  LengthFwd = 10
  LengthRev = 0
  Solid = true
  Symmetric = false
FEATURE [Part::Fillet] Fillet058  label="removeFromtMoreFrontCaseScrewRetainers003"
  Base = -> Extrude069
  Edges = 4 edges r=1.49: [Edge6,Edge11,Edge18,Edge23]
  Placement = pos=(-4,0,0) rot=(0,0,1;0rad)
FEATURE [Part::Cut] Cut066
  Base = -> Cut065
  Tool = -> Fillet058
FEATURE [Part::Cut] Cut067  label="screwPillars"
  Base = -> Cut066
  Tool = -> Fillet057
FEATURE [Part::MultiFuse] Fusion143  label="bottom021"
  Shapes = -> [Cut031,Cut063]
FEATURE [Part::Cylinder] Cylinder
  Angle = 360
  AttacherType = Attacher::AttachEngine3D
  Height = 10
  Placement = pos=(20.65,12,4.68) rot=(1,0,0;1.5708rad)
  Radius = 2
FEATURE [Part::Cylinder] Cylinder064
  Angle = 360
  AttacherType = Attacher::AttachEngine3D
  Height = 10
  Placement = pos=(20.65,12,67.38) rot=(1,0,0;1.5708rad)
  Radius = 2
FEATURE [Part::Cylinder] Cylinder065
  Angle = 360
  AttacherType = Attacher::AttachEngine3D
  Height = 10
  Placement = pos=(77.15,12,67.38) rot=(1,0,0;1.5708rad)
  Radius = 2
FEATURE [Part::Cylinder] Cylinder066
  Angle = 360
  AttacherType = Attacher::AttachEngine3D
  Height = 10
  Placement = pos=(77.15,12,4.68) rot=(1,0,0;1.5708rad)
  Radius = 2
FEATURE [Part::MultiFuse] Fusion144  label="removeFromThreadedInsertHousing"
  Shapes = -> [Cylinder065,Cylinder064,Cylinder,Cylinder066]
FEATURE [Part::Cut] Cut068  label="pcbStands001"
  Base = -> Cut064
  Tool = -> Fusion144
FEATURE [Part::MultiFuse] Fusion145
  Shapes = -> [Cut068,Fusion143]
FEATURE [Part::MultiFuse] Fusion146
  Shapes = -> [Fusion145]
FEATURE [Part::MultiFuse] Fusion147  label="bottom022"
  Shapes = -> [Cut067,Fusion146]
FEATURE [Part::MultiFuse] Fusion148  label="casePillars005"
  Shapes = -> [Cut047,Fusion092]
FEATURE [Part::MultiFuse] Fusion149  label="bottom023"
  Shapes = -> [Fusion124,Fusion113,Fusion147]
FEATURE [Part::MultiFuse] Fusion150  label="topBits"
  Shapes = -> [Cut025,Fusion148,Cut030,Fillet034]
FEATURE [Part::Feature] Face149 .. Face152  x4 (patterned run collapsed; names and placements below)
  shape: bbox 3.2 x 1.5 x 2e-07 mm, 1 faces, 0 solids (baked)
FEATURE [Part::Feature] Face153
  shape: bbox 3.6 x 3.2 x 2e-07 mm, 1 faces, 0 solids (baked)
FEATURE [Part::Feature] Face154
  shape: bbox 3.6 x 3.2 x 2e-07 mm, 1 faces, 0 solids (baked)
FEATURE [Sketcher::SketchObject] Sketch079  label="topSketch024"
  FullyConstrained = true
  sketch-geometry (6):
    g0: LineSegment StartX=19 StartY=38 StartZ=0 EndX=117 EndY=38 EndZ=0
    g1: ArcOfCircle CenterX=19 CenterY=19 CenterZ=0 NormalX=0 NormalY=0 NormalZ=1 AngleXU=0 Radius=19 StartAngle=1.5708 EndAngle=3.14159
    g2: LineSegment StartX=117 StartY=38 StartZ=0 EndX=117 EndY=19 EndZ=0
    g3: LineSegment StartX=98 StartY=1.0161e-12 StartZ=0 EndX=5.22862e-06 EndY=1.0161e-12 EndZ=0
    g4: LineSegment StartX=5.22862e-06 StartY=19 StartZ=0 EndX=5.22862e-06 EndY=1.0161e-12 EndZ=0
    g5: ArcOfCircle CenterX=98 CenterY=19 CenterZ=0 NormalX=0 NormalY=0 NormalZ=1 AngleXU=0 Radius=19 StartAngle=4.71239 EndAngle=6.28319
  constraints (16):
    c: Horizontal(g0)
    c: Distance(g0) = 98
    c: Coincident(g1,g0)
    c: Block(g1)
    c: Coincident(g2,g0)
    c: Vertical(g2)
    c: Distance(g2) = 19
    c: Horizontal(g3)
    c: Coincident(g4,g1)
    c: Vertical(g4)
    c: Coincident(g3,g4)
    c: Block(g3)
    c: Coincident(g5,g2)
    c: Coincident(g5,g3)
    c: Block(g0)
    c: Block(g5)
FEATURE [Sketcher::SketchObject] Sketch080  label="topSketch025"
  FullyConstrained = true
  sketch-geometry (6):
    g0: LineSegment StartX=19 StartY=38 StartZ=0 EndX=117 EndY=38 EndZ=0
    g1: ArcOfCircle CenterX=19 CenterY=19 CenterZ=0 NormalX=0 NormalY=0 NormalZ=1 AngleXU=0 Radius=19 StartAngle=1.5708 EndAngle=3.14159
    g2: LineSegment StartX=117 StartY=38 StartZ=0 EndX=117 EndY=19 EndZ=0
    g3: LineSegment StartX=98 StartY=1.0161e-12 StartZ=0 EndX=5.22862e-06 EndY=1.0161e-12 EndZ=0
    g4: LineSegment StartX=5.22862e-06 StartY=19 StartZ=0 EndX=5.22862e-06 EndY=1.0161e-12 EndZ=0
    g5: ArcOfCircle CenterX=98 CenterY=19 CenterZ=0 NormalX=0 NormalY=0 NormalZ=1 AngleXU=0 Radius=19 StartAngle=4.71239 EndAngle=6.28319
  constraints (16):
    c: Horizontal(g0)
    c: Distance(g0) = 98
    c: Coincident(g1,g0)
    c: Block(g1)
    c: Coincident(g2,g0)
    c: Vertical(g2)
    c: Distance(g2) = 19
    c: Horizontal(g3)
    c: Coincident(g4,g1)
    c: Vertical(g4)
    c: Coincident(g3,g4)
    c: Block(g3)
    c: Coincident(g5,g2)
    c: Coincident(g5,g3)
    c: Block(g0)
    c: Block(g5)
FEATURE [Part::Extrusion] Extrude070  label="sideA004"
  Base = -> Sketch080
  Dir = (0,0,1)
  DirMode = 2
  FaceMakerClass = Part::FaceMakerBullseye
  LengthFwd = 3
  LengthRev = 0
  Placement = pos=(0,0,-2.7) rot=(0,0,1;0rad)
  Solid = true
  Symmetric = false
FEATURE [Sketcher::SketchObject] Sketch081
  FullyConstrained = true
  Placement = pos=(117,19,0) rot=(0.57735,0.57735,0.57735;2.0944rad)
  sketch-geometry (8):
    g0: LineSegment StartX=-49.19 StartY=63.5 StartZ=0 EndX=-49.19 EndY=60.5 EndZ=0
    g1: LineSegment StartX=-49.19 StartY=11.5 StartZ=0 EndX=-49.19 EndY=8.5 EndZ=0
    g2: ArcOfCircle CenterX=-1.5 CenterY=62 CenterZ=0 NormalX=0 NormalY=0 NormalZ=1 AngleXU=0 Radius=1.5 StartAngle=4.71239 EndAngle=7.85398
    g3: ArcOfCircle CenterX=-1.5 CenterY=10 CenterZ=0 NormalX=0 NormalY=0 NormalZ=1 AngleXU=0 Radius=1.5 StartAngle=4.71239 EndAngle=7.85398
    g4: LineSegment StartX=-49.19 StartY=63.5 StartZ=0 EndX=-1.5 EndY=63.5 EndZ=0
    g5: LineSegment StartX=-49.19 StartY=60.5 StartZ=0 EndX=-1.5 EndY=60.5 EndZ=0
    g6: LineSegment StartX=-49.19 StartY=11.5 StartZ=0 EndX=-1.5 EndY=11.5 EndZ=0
    g7: LineSegment StartX=-49.19 StartY=8.5 StartZ=0 EndX=-1.5 EndY=8.5 EndZ=0
  constraints (19):
    c: Vertical(g0)
    c: Distance(g0) = 3
    c: Vertical(g1)
    c: Block(g1)
    c: Block(g2)
    c: Block(g3)
    c: Block(g0)
    c: Coincident(g4,g0)
    c: Coincident(g4,g2)
    c: Horizontal(g4)
    c: Coincident(g5,g0)
    c: Coincident(g5,g2)
    c: Horizontal(g5)
    c: Coincident(g6,g1)
    c: Coincident(g6,g3)
    c: Horizontal(g6)
    c: Coincident(g7,g1)
    c: Coincident(g7,g3)
    c: Horizontal(g7)
FEATURE [Part::Extrusion] Extrude071  label="sideB004"
  Base = -> Sketch079
  Dir = (0,0,1)
  DirMode = 2
  FaceMakerClass = Part::FaceMakerBullseye
  LengthFwd = 3
  LengthRev = 0
  Placement = pos=(0,0,71.7) rot=(0,0,1;0rad)
  Solid = true
  Symmetric = false
FEATURE [Part::MultiFuse] Fusion152  label="removeFromBottom004"
  Placement = pos=(2,0,0) rot=(0,0,1;0rad)
  Shapes = -> [Extrude070,Extrude071]
FEATURE [Part::Extrusion] Extrude072
  Base = -> Sketch081
  Dir = (1,0,0)
  DirMode = 2
  FaceMakerClass = Part::FaceMakerBullseye
  LengthFwd = 10
  LengthRev = 0
  Solid = true
  Symmetric = false
FEATURE [Part::Fillet] Fillet059  label="removeFromtMoreFrontCaseScrewRetainers004"
  Base = -> Extrude072
  Edges = 4 edges r=1.49: [Edge6,Edge11,Edge18,Edge23]
  Placement = pos=(-12,0,0) rot=(0,0,1;0rad)
FEATURE [Sketcher::SketchObject] Sketch082
  FullyConstrained = true
  Placement = pos=(117,19,0) rot=(0.57735,0.57735,0.57735;2.0944rad)
  sketch-geometry (8):
    g0: LineSegment StartX=-49.19 StartY=69.25 StartZ=0 EndX=-49.19 EndY=66.25 EndZ=0
    g1: LineSegment StartX=-49.19 StartY=5.75 StartZ=0 EndX=-49.19 EndY=2.75 EndZ=0
    g2: ArcOfCircle CenterX=-1.5 CenterY=67.75 CenterZ=0 NormalX=0 NormalY=0 NormalZ=1 AngleXU=0 Radius=1.5 StartAngle=4.71239 EndAngle=7.85398
    g3: ArcOfCircle CenterX=-1.5 CenterY=4.25 CenterZ=0 NormalX=0 NormalY=0 NormalZ=1 AngleXU=0 Radius=1.5 StartAngle=4.71239 EndAngle=7.85398
    g4: LineSegment StartX=-49.19 StartY=69.25 StartZ=0 EndX=-1.5 EndY=69.25 EndZ=0
    g5: LineSegment StartX=-49.19 StartY=66.25 StartZ=0 EndX=-1.5 EndY=66.25 EndZ=0
    g6: LineSegment StartX=-49.19 StartY=5.75 StartZ=0 EndX=-1.5 EndY=5.75 EndZ=0
    g7: LineSegment StartX=-49.19 StartY=2.75 StartZ=0 EndX=-1.5 EndY=2.75 EndZ=0
  constraints (19):
    c: Vertical(g0)
    c: Distance(g0) = 3
    c: Block(g0)
    c: Vertical(g1)
    c: Block(g2)
    c: Block(g3)
    c: Block(g1)
    c: Coincident(g4,g0)
    c: Coincident(g4,g2)
    c: Horizontal(g4)
    c: Coincident(g5,g0)
    c: Coincident(g5,g2)
    c: Horizontal(g5)
    c: Coincident(g6,g1)
    c: Coincident(g6,g3)
    c: Horizontal(g6)
    c: Coincident(g7,g1)
    c: Coincident(g7,g3)
    c: Horizontal(g7)
FEATURE [Part::Extrusion] Extrude073
  Base = -> Sketch082
  Dir = (1,0,0)
  DirMode = 2
  FaceMakerClass = Part::FaceMakerBullseye
  LengthFwd = 10
  LengthRev = 0
  Solid = true
  Symmetric = false
FEATURE [Part::Fillet] Fillet060  label="removeFromtMoreFrontCaseScrewRetainers005"
  Base = -> Extrude073
  Edges = 4 edges r=1.49: [Edge6,Edge11,Edge18,Edge23]
  Placement = pos=(-4,0,0) rot=(0,0,1;0rad)
FEATURE [Part::Revolution] Revolve163  label="backCaseScrewRetainer004"
  Angle = 360
  Axis = (0,1,0)
  Base = (0,0,0)
  FaceMakerClass = Part::FaceMakerBullseye
  Placement = pos=(12.5,3,62) rot=(0,0,1;0rad)
  Solid = false
  Source = -> Face149
  Symmetric = false
FEATURE [Part::Revolution] Revolve164  label="frontCaseScrewRetainer006"
  Angle = 360
  Axis = (0,1,0)
  Base = (0,0,0)
  FaceMakerClass = Part::FaceMakerBullseye
  Placement = pos=(89.5,3,68.5) rot=(0,0,1;0rad)
  Solid = false
  Source = -> Face151
  Symmetric = false
FEATURE [Part::Revolution] Revolve165  label="frontCaseScrewRetainer007"
  Angle = 360
  Axis = (0,1,0)
  Base = (0,0,0)
  FaceMakerClass = Part::FaceMakerBullseye
  Placement = pos=(89.5,3,3.5) rot=(0,0,1;0rad)
  Solid = false
  Source = -> Face152
  Symmetric = false
FEATURE [Part::Revolution] Revolve166  label="backCaseScrewRetainer005"
  Angle = 360
  Axis = (0,1,0)
  Base = (0,0,0)
  FaceMakerClass = Part::FaceMakerBullseye
  Placement = pos=(12.5,3,10) rot=(0,0,1;0rad)
  Solid = false
  Source = -> Face150
  Symmetric = false
FEATURE [Part::Revolution] Revolve167  label="moreFrontCaseScrewRetainer006"
  Angle = 360
  Axis = (0,1,0)
  Base = (0,0,0)
  FaceMakerClass = Part::FaceMakerBullseye
  Placement = pos=(109.5,4.5,68.5) rot=(0,0,1;0rad)
  Solid = false
  Source = -> Face153
  Symmetric = false
FEATURE [Part::Revolution] Revolve168  label="moreFrontCaseScrewRetainer007"
  Angle = 360
  Axis = (0,1,0)
  Base = (0,0,0)
  FaceMakerClass = Part::FaceMakerBullseye
  Placement = pos=(109.5,4.5,3.5) rot=(0,0,1;0rad)
  Solid = false
  Source = -> Face154
  Symmetric = false
FEATURE [Part::MultiFuse] Fusion151  label="screwRetainers003"
  Shapes = -> [Revolve168,Revolve167,Revolve166,Revolve165,Revolve164,Revolve163]
FEATURE [Part::Cut] Cut069  label="screwRetainers004"
  Base = -> Fusion151
  Tool = -> Fusion152
FEATURE [Part::Cut] Cut070
  Base = -> Cut069
  Tool = -> Fillet060
FEATURE [Part::Cut] Cut071  label="screwPillars001"
  Base = -> Cut070
  Tool = -> Fillet059
FEATURE [Part::MultiFuse] Fusion153  label="bottom024"
  Shapes = -> [Fusion149,Cut071]
FEATURE [Part::Cylinder] Cylinder067
  Angle = 360
  AttacherType = Attacher::AttachEngine3D
  Height = 10
  Placement = pos=(20.65,12,4.68) rot=(1,0,0;1.5708rad)
  Radius = 2
FEATURE [Part::Cylinder] Cylinder068
  Angle = 360
  AttacherType = Attacher::AttachEngine3D
  Height = 10
  Placement = pos=(20.65,12,67.38) rot=(1,0,0;1.5708rad)
  Radius = 2
FEATURE [Part::Cylinder] Cylinder069
  Angle = 360
  AttacherType = Attacher::AttachEngine3D
  Height = 10
  Placement = pos=(77.15,12,67.38) rot=(1,0,0;1.5708rad)
  Radius = 2
FEATURE [Part::Cylinder] Cylinder070
  Angle = 360
  AttacherType = Attacher::AttachEngine3D
  Height = 10
  Placement = pos=(77.15,12,4.68) rot=(1,0,0;1.5708rad)
  Radius = 2
FEATURE [Part::MultiFuse] Fusion154  label="removeFromThreadedInsertHousing001"
  Shapes = -> [Cylinder069,Cylinder068,Cylinder067,Cylinder070]
FEATURE [Part::Cut] Cut072  label="bottom025"
  Base = -> Fusion153
  Tool = -> Fusion154
FEATURE [Image::ImagePlane] ImagePlane
  XSize = 339
  YSize = 72
FEATURE [Sketcher::SketchObject] Sketch083
  FullyConstrained = false
  MapMode = 5
  Support = -> [XY_Plane]
  sketch-geometry (96):
    g0: LineSegment StartX=-151.619 StartY=28.8932 StartZ=0 EndX=-140.819 EndY=28.8932 EndZ=0
    g1: LineSegment StartX=-151.619 StartY=24.0313 StartZ=0 EndX=-151.619 EndY=28.8932 EndZ=0
    g2: LineSegment StartX=-140.819 StartY=17.7713 StartZ=0 EndX=-151.619 EndY=17.7713 EndZ=0
    g3: LineSegment StartX=-151.619 StartY=17.7713 StartZ=0 EndX=-151.619 EndY=22.6313 EndZ=0
    g4: LineSegment StartX=-151.619 StartY=22.6313 StartZ=0 EndX=-145.128 EndY=22.6313 EndZ=0
    g5: LineSegment StartX=-145.128 StartY=24.0313 StartZ=0 EndX=-140.819 EndY=28.8932 EndZ=0
    g6: LineSegment StartX=-145.128 StartY=22.6313 StartZ=0 EndX=-140.819 EndY=17.7713 EndZ=0
    g7: ArcOfCircle CenterX=-155.157 CenterY=23.3323 CenterZ=0 NormalX=0 NormalY=0 NormalZ=1 AngleXU=0 Radius=6.92354 StartAngle=1.03434 EndAngle=5.24885
    g8: ArcOfCircle CenterX=-155.157 CenterY=23.3323 CenterZ=0 NormalX=0 NormalY=0 NormalZ=1 AngleXU=0 Radius=12.6269 StartAngle=1.28675 EndAngle=4.99643
    g9: LineSegment StartX=-151.619 StartY=35.4532 StartZ=0 EndX=-151.619 EndY=29.2832 EndZ=0
    g10: LineSegment StartX=-151.619 StartY=17.3813 StartZ=0 EndX=-151.619 EndY=11.2113 EndZ=0
    g11-g21: Circle x11 (B-spline internal-alignment scaffolding for g22; pole/knot coordinates omitted)
    g22: BSplineCurve PolesCount=11 KnotsCount=9 Degree=3 IsPeriodic=0
    g23-g31: GeomPoint x9 (B-spline internal-alignment scaffolding for g22; pole/knot coordinates omitted)
    g32-g49: Circle x18 (B-spline internal-alignment scaffolding for g50; pole/knot coordinates omitted)
    g50: BSplineCurve PolesCount=18 KnotsCount=16 Degree=3 IsPeriodic=0
    g51-g66: GeomPoint x16 (B-spline internal-alignment scaffolding for g50; pole/knot coordinates omitted)
    g67: LineSegment StartX=-117.124 StartY=30.093 StartZ=0 EndX=-117.603 EndY=26.5272 EndZ=0
    g68: LineSegment StartX=-117.603 StartY=17.8472 StartZ=0 EndX=-117.124 EndY=14.2659 EndZ=0
    g69: Ellipse CenterX=-109.671 CenterY=20.025 CenterZ=0 NormalX=0 NormalY=0 NormalZ=1 MajorRadius=3.34798 MinorRadius=2.71052 AngleXU=-1.56793
    g70: GeomPoint X=-109.666 Y=18.0598 Z=0
    g71: GeomPoint X=-109.677 Y=21.9902 Z=0
    g72: Ellipse CenterX=-109.671 CenterY=20.0123 CenterZ=0 NormalX=0 NormalY=0 NormalZ=1 MajorRadius=6.93002 MinorRadius=6.36273 AngleXU=-3.13976
    g73: GeomPoint X=-112.417 Y=20.0073 Z=0
    g74: GeomPoint X=-106.925 Y=20.0173 Z=0
    g75: Ellipse CenterX=-51.7682 CenterY=20.1463 CenterZ=0 NormalX=0 NormalY=0 NormalZ=1 MajorRadius=3.19279 MinorRadius=2.71052 AngleXU=-1.52774
    g76: GeomPoint X=-51.6955 Y=18.4606 Z=0
    g77: GeomPoint X=-51.8408 Y=21.832 Z=0
    g78: GeomPoint X=-54.5142 Y=20.1413 Z=0
    g79: GeomPoint X=-49.0221 Y=20.1513 Z=0
    g80: Ellipse CenterX=-51.7682 CenterY=20.1463 CenterZ=0 NormalX=0 NormalY=0 NormalZ=1 MajorRadius=6.93002 MinorRadius=6.36273 AngleXU=-3.13976
    g81: Ellipse CenterX=-22.8436 CenterY=20.1783 CenterZ=0 NormalX=0 NormalY=0 NormalZ=1 MajorRadius=3.31512 MinorRadius=2.71052 AngleXU=-1.60214
    g82: GeomPoint X=-22.9034 Y=18.2706 Z=0
    g83: GeomPoint X=-22.7838 Y=22.0861 Z=0
    g84: GeomPoint X=-25.5897 Y=20.1733 Z=0
    g85: GeomPoint X=-20.0976 Y=20.1833 Z=0
    g86: Ellipse CenterX=-22.8436 CenterY=20.1783 CenterZ=0 NormalX=0 NormalY=0 NormalZ=1 MajorRadius=6.93002 MinorRadius=6.36273 AngleXU=-3.13976
    g87: LineSegment StartX=-101.889 StartY=14.1107 StartZ=0 EndX=-97.7455 EndY=14.1107 EndZ=0
    g88: LineSegment StartX=-93.8155 StartY=14.1107 StartZ=0 EndX=-89.6755 EndY=14.1107 EndZ=0
    g89: LineSegment StartX=-85.7455 StartY=14.1107 StartZ=0 EndX=-81.6055 EndY=14.1107 EndZ=0
    g90: LineSegment StartX=-101.889 StartY=14.1107 StartZ=0 EndX=-101.889 EndY=25.9907 EndZ=0
    g91: LineSegment StartX=-101.889 StartY=25.9907 StartZ=0 EndX=-97.8594 EndY=25.9907 EndZ=0
    g92: LineSegment StartX=-97.8594 StartY=25.9907 StartZ=0 EndX=-97.8594 EndY=24.0907 EndZ=0
    g93: LineSegment StartX=-97.8594 StartY=24.0907 StartZ=0 EndX=-89.9522 EndY=24.0907 EndZ=0
    g94: LineSegment StartX=-97.7455 StartY=14.1107 StartZ=0 EndX=-97.7455 EndY=19.9107 EndZ=0
    g95: LineSegment StartX=-89.6755 StartY=14.1107 StartZ=0 EndX=-89.6755 EndY=19.9107 EndZ=0
  constraints (83):
    c: Coincident(g1,g0)
    c: Horizontal(g0)
    c: Vertical(g1)
    c: Coincident(g2,g3)
    c: Coincident(g3,g4)
    c: Horizontal(g4)
    c: Horizontal(g2)
    c: Vertical(g3)
    c: Block(g1)
    c: Distance(g3) = 4.86
    c: Block(g4)
    c: Distance(g0) = 10.8
    c: Distance(g2) = 10.8
    c: Coincident(g5,g0)
    c: Coincident(g6,g4)
    c: Coincident(g6,g2)
    c: Block(g8)
    c: Block(g7)
    c: Coincident(g9,g8)
    c: Coincident(g9,g7)
    c: Vertical(g9)
    c: Coincident(g10,g7)
    c: Coincident(g10,g8)
    c: Vertical(g10)
    c: Weight(g11) = 1
    c: Equal(g11, g12-g21) x10
    c: InternalAlignment(g11-g21 -> g22) x11
    c: InternalAlignment(g23-g31 -> g22) x9
    c: Block(g22)
    c: Weight(g32) = 1
    c: Equal(g32, g33-g49) x17
    c: InternalAlignment(g32-g49 -> g50) x18
    c: InternalAlignment(g51-g66 -> g50) x16
    c: Block(g50)
    c: Coincident(g67,g50)
    c: Coincident(g67,g22)
    c: Coincident(g68,g22)
    c: Coincident(g68,g50)
    c: InternalAlignment(g70,g69)
    c: InternalAlignment(g71,g69)
    c: Block(g69)
    c: InternalAlignment(g73,g72)
    c: InternalAlignment(g74,g72)
    c: Block(g72)
    c: InternalAlignment(g76,g75)
    c: InternalAlignment(g77,g75)
    c: InternalAlignment(g78,g80)
    c: InternalAlignment(g79,g80)
    c: Block(g80)
    c: Coincident(g75,g80)
    c: Block(g75)
    c: InternalAlignment(g82,g81)
    c: InternalAlignment(g83,g81)
    c: InternalAlignment(g84,g86)
    c: InternalAlignment(g85,g86)
    c: Block(g86)
    c: Coincident(g81,g86)
    c: Block(g81)
    c: Horizontal(g87)
    c: Block(g87)
    c: Horizontal(g88)
    c: Distance(g88) = 4.14
    c: Horizontal(g89)
    c: Equal(g88,g89) = 4.14
    c: Block(g89)
    c: Block(g88)
    c: Coincident(g90,g87)
    c: Vertical(g90)
    c: Distance(g90) = 11.88
    c: Coincident(g91,g90)
    c: Horizontal(g91)
    c: Coincident(g92,g91)
    c: Vertical(g92)
    c: Distance(g91) = 4.03
    c: Distance(g92) = 1.9
    c: Coincident(g93,g92)
    c: Horizontal(g93)
    c: Coincident(g94,g87)
    c: Vertical(g94)
    c: Vertical(g95)
    c: Coincident(g95,g88)
    c: Distance(g94) = 5.8
    c: Distance(g95) = 5.8
FEATURE [PartDesign::Body] Body
  Group = -> [Sketch083]
  Origin = -> Origin
FEATURE [Sketcher::SketchObject] Sketch084
  FullyConstrained = true
  MapMode = 5
  Support = -> [XY_Plane001]
FEATURE [PartDesign::Body] Body001
  Group = -> [Sketch084]
  Origin = -> Origin001
